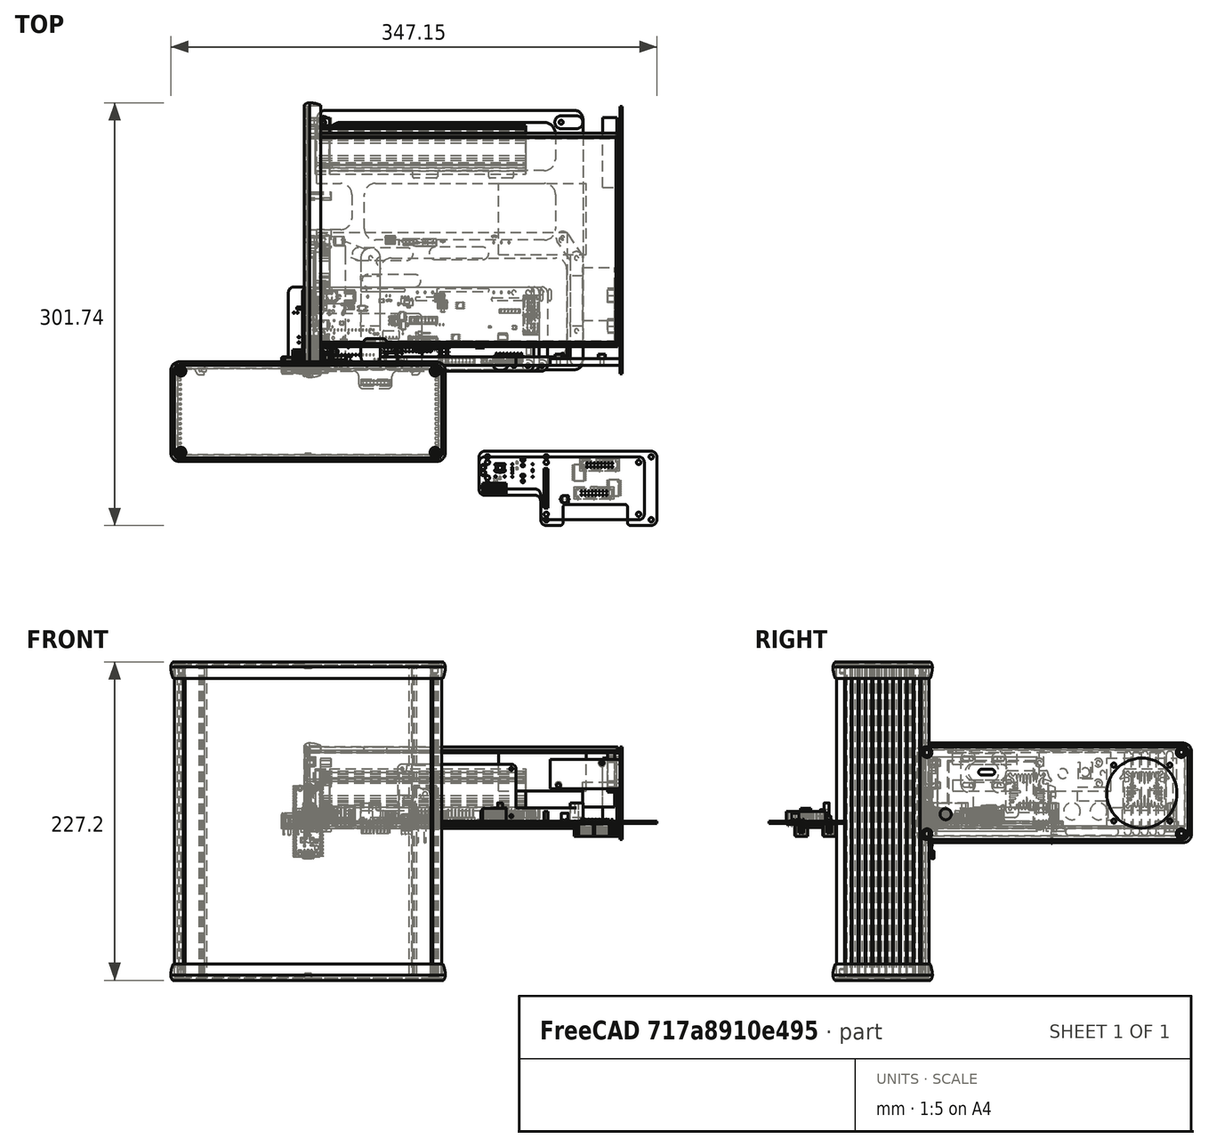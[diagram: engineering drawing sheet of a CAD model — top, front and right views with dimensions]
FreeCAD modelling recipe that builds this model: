
FCSTD DOCUMENT  (FreeCAD 1.0R39285 (Git))
Label: EL-Load-CaseV4
License: All rights reserved
LicenseURL: http://en.wikipedia.org/wiki/All_rights_reserved
objects: App::Link×772, Part::Feature×537, App::Part×80, Sketcher::SketchObject×39, PartDesign::Pad×19, PartDesign::Pocket×15, PartDesign::CoordinateSystem×8, PartDesign::Body×7, PartDesign::SubShapeBinder×6, Part::Box×5, PartDesign::Chamfer×2, PartDesign::Plane×2, PartDesign::FeatureBase×1, Part::Compound×1, Mesh::Feature×1
note: 754 computed .brp shape members not serialized (recipe doc carries the construction recipe); baked Part::Feature solids carry a one-line shape summary decoded from their .brp

FEATURE [Part::Feature] Part__Feature017  label="U extrusion 220mm"
  Placement = pos=(-8e-15,-66,0) rot=(0,0,1;3.14159rad)
  shape: bbox 191 x 66 x 220 mm, 418 faces (baked)
FEATURE [Part::Feature] Part__Feature018  label="T Extrusion Cap 220mm"
  Placement = pos=(8e-15,9.9e-14,0) rot=(0,0,1;0rad)
  shape: bbox 152.4 x 4.29 x 220 mm, 26 faces (baked)
FEATURE [Part::Feature] Part__Feature019  label="1455U Open Bezel"
  Placement = pos=(6.2e-15,-33.01,110) rot=(0,0,1;0rad)
  shape: bbox 196.1 x 71.1 x 11.6 mm, 100 faces (baked)
FEATURE [Part::Feature] Part__Feature020  label="1455U Open Bezel001"
  Placement = pos=(-3.66e-13,-33.01,-110) rot=(1,0,0;3.14159rad)
  shape: bbox 196.1 x 71.1 x 11.6 mm, 100 faces (baked)
FEATURE [Part::Feature] Part__Feature021  label="U End Panel"
  Placement = pos=(-2.49e-13,-33,111.8) rot=(0,0,1;0rad)
  shape: bbox 191 x 66 x 1.626 mm, 14 faces (baked)
FEATURE [Part::Feature] Part__Feature022  label="U End Panel001"
  Placement = pos=(-1.092e-12,-33,-111.8) rot=(1,0,0;3.14159rad)
  shape: bbox 191 x 66 x 1.626 mm, 14 faces (baked)
FEATURE [Part::Feature] Part__Feature023  label="1455 screw"
  Placement = pos=(90.75,-62.01,113.426) rot=(1,0,0;3.14159rad)
  shape: bbox 5.5 x 5.5 x 8 mm, 18 faces (baked)
FEATURE [Part::Feature] Part__Feature024  label="1455 screw001"
  Placement = pos=(90.75,-3.99,113.426) rot=(1,0,0;3.14159rad)
  shape: bbox 5.5 x 5.5 x 8 mm, 18 faces (baked)
FEATURE [Part::Feature] Part__Feature025  label="1455 screw002"
  Placement = pos=(-90.75,-62.01,113.426) rot=(1,0,0;3.14159rad)
  shape: bbox 5.5 x 5.5 x 8 mm, 18 faces (baked)
FEATURE [Part::Feature] Part__Feature026  label="1455 screw003"
  Placement = pos=(-90.75,-3.99,113.426) rot=(1,0,0;3.14159rad)
  shape: bbox 5.5 x 5.5 x 8 mm, 18 faces (baked)
FEATURE [Part::Feature] Part__Feature027  label="1455 screw004"
  Placement = pos=(-90.75,-3.99,-113.426) rot=(0,0,-1;0.01524rad)
  shape: bbox 5.5 x 5.5 x 8 mm, 18 faces (baked)
FEATURE [Part::Feature] Part__Feature028  label="1455 screw005"
  Placement = pos=(-90.75,-62.01,-113.426) rot=(0,0,1;0rad)
  shape: bbox 5.5 x 5.5 x 8 mm, 18 faces (baked)
FEATURE [Part::Feature] Part__Feature029  label="1455 screw006"
  Placement = pos=(90.75,-62.01,-113.426) rot=(0,0,-1;0.007552rad)
  shape: bbox 5.5 x 5.5 x 8 mm, 18 faces (baked)
FEATURE [Part::Feature] Part__Feature030  label="1455 screw007"
  Placement = pos=(90.75,-3.99,-113.426) rot=(0,0,1;0rad)
  shape: bbox 5.5 x 5.5 x 8 mm, 18 faces (baked)
FEATURE [App::Part] _455U2201  label="1455U2201"
  Group = -> [Part__Feature017,Part__Feature018,Part__Feature019,Part__Feature020,Part__Feature021,Part__Feature022,Part__Feature023,Part__Feature024,Part__Feature025,Part__Feature026,Part__Feature027,Part__Feature028,Part__Feature029,Part__Feature030]
  Origin = -> Origin020
  Placement = pos=(111,89.5,53.1) rot=(0.57735,-0.57735,-0.57735;2.0944rad)
FEATURE [Part::Box] Box  label="TFT"
  AttacherType = Attacher::AttachEngine3D
  Height = 53
  Length = 4.5
  Placement = pos=(-0.5,6,-7) rot=(0,0,1;0rad)
  Width = 71
FEATURE [Part::Box] Box001  label="Fan1"
  AttacherType = Attacher::AttachEngine3D
  Height = 50
  Length = 10
  Placement = pos=(210.5,127,-5) rot=(0,0,1;0rad)
  Width = 50
FEATURE [App::Link] C303_C_0805_2012Metric_1d86ef2bb22f_ln_097  label="C26_C_0805_2012Metric_d5dbb9e88232"
  LinkPlacement = pos=(114.675,21.075,0) rot=(0,0,-1;1.5708rad)
  LinkedObject = -> Shape068
  Placement = pos=(114.675,21.075,0) rot=(0,0,-1;1.5708rad)
FEATURE [App::Link] C303_C_0805_2012Metric_1d86ef2bb22f_ln_098  label="C23_C_0805_2012Metric_000a25718fd004"
  LinkPlacement = pos=(127.75,16.625,0) rot=(0,0,1;1.5708rad)
  LinkedObject = -> Shape068
  Placement = pos=(127.75,16.625,0) rot=(0,0,1;1.5708rad)
FEATURE [App::Link] C303_C_0805_2012Metric_1d86ef2bb22f_ln_099  label="C311_C_0805_2012Metric_e7a3c8a1d567"
  LinkPlacement = pos=(69.6,18.85,0) rot=(0,0,1;1.5708rad)
  LinkedObject = -> Shape068
  Placement = pos=(69.6,18.85,0) rot=(0,0,1;1.5708rad)
FEATURE [App::Link] C303_C_0805_2012Metric_1d86ef2bb22f_ln_100  label="C211_C_0805_2012Metric_f6e2775f9a029"
  LinkPlacement = pos=(103.35,92.55,0) rot=(0,0,1;1.5708rad)
  LinkedObject = -> Shape068
  Placement = pos=(103.35,92.55,0) rot=(0,0,1;1.5708rad)
FEATURE [App::Link] C303_C_0805_2012Metric_1d86ef2bb22f_ln_101  label="C13_C_0805_2012Metric_584e764d642c001"
  LinkPlacement = pos=(42.45,2.35,0) rot=(0,0,1;1.5708rad)
  LinkedObject = -> Shape068
  Placement = pos=(42.45,2.35,0) rot=(0,0,1;1.5708rad)
FEATURE [App::Link] C303_C_0805_2012Metric_1d86ef2bb22f_ln_102  label="C49_C_0805_2012Metric_974e61c4247c"
  LinkPlacement = pos=(99.8,39.3625,0) rot=(0,0,1;1.5708rad)
  LinkedObject = -> Shape068
  Placement = pos=(99.8,39.3625,0) rot=(0,0,1;1.5708rad)
FEATURE [App::Link] C303_C_0805_2012Metric_1d86ef2bb22f_ln_103  label="C309_C_0805_2012Metric_4bea97f5e1ff001"
  LinkPlacement = pos=(85.7125,21.575,0) rot=(0,0,-1;1.5708rad)
  LinkedObject = -> Shape068
  Placement = pos=(85.7125,21.575,0) rot=(0,0,-1;1.5708rad)
FEATURE [App::Link] C303_C_0805_2012Metric_1d86ef2bb22f_ln_007  label="C38_C_0805_2012Metric_d30376c11af007"
  LinkPlacement = pos=(135.55,33.075,0) rot=(0,0,1;0rad)
  LinkedObject = -> Shape068
  Placement = pos=(135.55,33.075,0) rot=(0,0,1;0rad)
FEATURE [App::Link] C303_C_0805_2012Metric_1d86ef2bb22f_ln_104  label="C223_C_0805_2012Metric_fc6fab0a5f9d001"
  LinkPlacement = pos=(175,91.5,0) rot=(0,0,1;1.5708rad)
  LinkedObject = -> Shape068
  Placement = pos=(175,91.5,0) rot=(0,0,1;1.5708rad)
FEATURE [App::Link] C303_C_0805_2012Metric_1d86ef2bb22f_ln_105  label="C504_C_0805_2012Metric_f896a043f44d001"
  LinkPlacement = pos=(101.25,30.175,0) rot=(0,0,1;1.5708rad)
  LinkedObject = -> Shape068
  Placement = pos=(101.25,30.175,0) rot=(0,0,1;1.5708rad)
FEATURE [App::Link] C303_C_0805_2012Metric_1d86ef2bb22f_ln_106  label="C226_C_0805_2012Metric_2eb8bf28e24e001"
  LinkPlacement = pos=(117.6,45.9,0) rot=(0,0,1;0rad)
  LinkedObject = -> Shape068
  Placement = pos=(117.6,45.9,0) rot=(0,0,1;0rad)
FEATURE [App::Link] C303_C_0805_2012Metric_1d86ef2bb22f_ln_107  label="C214_C_0805_2012Metric_e2b81b34a7d003"
  LinkPlacement = pos=(51.9,45.5,0) rot=(0,0,1;3.14159rad)
  LinkedObject = -> Shape068
  Placement = pos=(51.9,45.5,0) rot=(0,0,1;3.14159rad)
FEATURE [App::Link] C303_C_0805_2012Metric_1d86ef2bb22f_ln_108  label="C221_C_0805_2012Metric_b44e2667bcf008"
  LinkPlacement = pos=(165.5,5.5,0) rot=(0,0,1;1.5708rad)
  LinkedObject = -> Shape068
  Placement = pos=(165.5,5.5,0) rot=(0,0,1;1.5708rad)
FEATURE [App::Link] C303_C_0805_2012Metric_1d86ef2bb22f_ln_109  label="C209_C_0805_2012Metric_f79f18431d004"
  LinkPlacement = pos=(114.35,91.65,0) rot=(0,0,1;1.5708rad)
  LinkedObject = -> Shape068
  Placement = pos=(114.35,91.65,0) rot=(0,0,1;1.5708rad)
FEATURE [App::Link] C303_C_0805_2012Metric_1d86ef2bb22f_ln_110  label="C205_C_0805_2012Metric_92a2149bb90f001"
  LinkPlacement = pos=(60.2,50.5,0) rot=(0,0,1;1.5708rad)
  LinkedObject = -> Shape068
  Placement = pos=(60.2,50.5,0) rot=(0,0,1;1.5708rad)
FEATURE [App::Link] C303_C_0805_2012Metric_1d86ef2bb22f_ln_111  label="C29_C_0805_2012Metric_fa1848d19679"
  LinkPlacement = pos=(138.375,38.725,0) rot=(0,0,1;0rad)
  LinkedObject = -> Shape068
  Placement = pos=(138.375,38.725,0) rot=(0,0,1;0rad)
FEATURE [App::Link] C303_C_0805_2012Metric_1d86ef2bb22f_ln_112  label="C505_C_0805_2012Metric_bcf27ea4bc011"
  LinkPlacement = pos=(113.225,27.5,0) rot=(0,0,-1;1.5708rad)
  LinkedObject = -> Shape068
  Placement = pos=(113.225,27.5,0) rot=(0,0,-1;1.5708rad)
FEATURE [App::Link] C303_C_0805_2012Metric_1d86ef2bb22f_ln_113  label="C19_C_0805_2012Metric_5594ae341428"
  LinkPlacement = pos=(115.725,25.05,0) rot=(0,0,1;1.5708rad)
  LinkedObject = -> Shape068
  Placement = pos=(115.725,25.05,0) rot=(0,0,1;1.5708rad)
FEATURE [App::Link] C303_C_0805_2012Metric_1d86ef2bb22f_ln_114  label="C217_C_0805_2012Metric_6c92b5ed4841"
  LinkPlacement = pos=(183.3,31.7,0) rot=(0,0,1;1.5708rad)
  LinkedObject = -> Shape068
  Placement = pos=(183.3,31.7,0) rot=(0,0,1;1.5708rad)
FEATURE [App::Link] C303_C_0805_2012Metric_1d86ef2bb22f_ln_115  label="C316_C_0805_2012Metric_cd1ffc8391ec001"
  LinkPlacement = pos=(72.687,27.995,0) rot=(0,0,1;3.14159rad)
  LinkedObject = -> Shape068
  Placement = pos=(72.687,27.995,0) rot=(0,0,1;3.14159rad)
FEATURE [App::Link] C303_C_0805_2012Metric_1d86ef2bb22f_ln_116  label="C225_C_0805_2012Metric_ffd9329e2dcc001"
  LinkPlacement = pos=(161.69,92.5,0) rot=(0,0,1;3.14159rad)
  LinkedObject = -> Shape068
  Placement = pos=(161.69,92.5,0) rot=(0,0,1;3.14159rad)
FEATURE [App::Link] C303_C_0805_2012Metric_1d86ef2bb22f_ln_117  label="C35_C_0805_2012Metric_ffb163dd22d004"
  LinkPlacement = pos=(145.625,33.725,0) rot=(0,0,1;3.14159rad)
  LinkedObject = -> Shape068
  Placement = pos=(145.625,33.725,0) rot=(0,0,1;3.14159rad)
FEATURE [App::Link] C303_C_0805_2012Metric_1d86ef2bb22f_ln_118  label="C52_C_0805_2012Metric_ac194752d0a1"
  LinkPlacement = pos=(80.2,36.8,0) rot=(0,0,1;3.14159rad)
  LinkedObject = -> Shape068
  Placement = pos=(80.2,36.8,0) rot=(0,0,1;3.14159rad)
FEATURE [App::Link] C303_C_0805_2012Metric_1d86ef2bb22f_ln_119  label="C404_C_0805_2012Metric_dd9989736423"
  LinkPlacement = pos=(105.09,9.575,0) rot=(0,0,1;3.14159rad)
  LinkedObject = -> Shape068
  Placement = pos=(105.09,9.575,0) rot=(0,0,1;3.14159rad)
FEATURE [App::Link] C303_C_0805_2012Metric_1d86ef2bb22f_ln_120  label="C27_C_0805_2012Metric_c813a18685a010"
  LinkPlacement = pos=(114.85,12.65,0) rot=(0,0,-1;1.5708rad)
  LinkedObject = -> Shape068
  Placement = pos=(114.85,12.65,0) rot=(0,0,-1;1.5708rad)
FEATURE [App::Link] C303_C_0805_2012Metric_1d86ef2bb22f_ln_121  label="C222_C_0805_2012Metric_211188bab275"
  LinkPlacement = pos=(165.438,13.5,0) rot=(0,0,1;1.5708rad)
  LinkedObject = -> Shape068
  Placement = pos=(165.438,13.5,0) rot=(0,0,1;1.5708rad)
FEATURE [App::Link] C303_C_0805_2012Metric_1d86ef2bb22f_ln_122  label="C1_C_0805_2012Metric_e1adf31e506d001"
  LinkPlacement = pos=(107.075,36.85,0) rot=(0,0,1;3.14159rad)
  LinkedObject = -> Shape068
  Placement = pos=(107.075,36.85,0) rot=(0,0,1;3.14159rad)
FEATURE [App::Link] C303_C_0805_2012Metric_1d86ef2bb22f_ln_123  label="C207_C_0805_2012Metric_e7225891546f001"
  LinkPlacement = pos=(171.545,23.4584,0) rot=(0,0,1;1.5708rad)
  LinkedObject = -> Shape068
  Placement = pos=(171.545,23.4584,0) rot=(0,0,1;1.5708rad)
FEATURE [App::Link] C303_C_0805_2012Metric_1d86ef2bb22f_ln_124  label="C315_C_0805_2012Metric_75f11421f159"
  LinkPlacement = pos=(120.231,38.4938,0) rot=(0,0,-1;1.5708rad)
  LinkedObject = -> Shape068
  Placement = pos=(120.231,38.4938,0) rot=(0,0,-1;1.5708rad)
FEATURE [App::Link] C303_C_0805_2012Metric_1d86ef2bb22f_ln_125  label="C2_C_0805_2012Metric_05101afe5804"
  LinkPlacement = pos=(118.85,34.6,0) rot=(0,0,1;3.14159rad)
  LinkedObject = -> Shape068
  Placement = pos=(118.85,34.6,0) rot=(0,0,1;3.14159rad)
FEATURE [App::Link] C303_C_0805_2012Metric_1d86ef2bb22f_ln_126  label="C24_C_0805_2012Metric_9756039021d010"
  LinkPlacement = pos=(127.8,23.325,0) rot=(0,0,1;1.5708rad)
  LinkedObject = -> Shape068
  Placement = pos=(127.8,23.325,0) rot=(0,0,1;1.5708rad)
FEATURE [App::Link] C303_C_0805_2012Metric_1d86ef2bb22f_ln_127  label="C305_C_0805_2012Metric_8cc8a682d548"
  LinkPlacement = pos=(52,26.85,0) rot=(0,0,1;1.5708rad)
  LinkedObject = -> Shape068
  Placement = pos=(52,26.85,0) rot=(0,0,1;1.5708rad)
FEATURE [App::Link] C303_C_0805_2012Metric_1d86ef2bb22f_ln_128  label="C215_C_0805_2012Metric_46fa3c3d31ac001"
  LinkPlacement = pos=(163.5,88,0) rot=(0,0,1;1.5708rad)
  LinkedObject = -> Shape068
  Placement = pos=(163.5,88,0) rot=(0,0,1;1.5708rad)
FEATURE [App::Link] C303_C_0805_2012Metric_1d86ef2bb22f_ln_129  label="C407_C_0805_2012Metric_fedbb3076933"
  LinkPlacement = pos=(53.45,36.2,0) rot=(0,0,1;3.14159rad)
  LinkedObject = -> Shape068
  Placement = pos=(53.45,36.2,0) rot=(0,0,1;3.14159rad)
FEATURE [App::Link] C303_C_0805_2012Metric_1d86ef2bb22f_ln_130  label="C51_C_0805_2012Metric_83d383f6edd7"
  LinkPlacement = pos=(65.4,39.6,0) rot=(0,0,1;0rad)
  LinkedObject = -> Shape068
  Placement = pos=(65.4,39.6,0) rot=(0,0,1;0rad)
FEATURE [App::Link] C303_C_0805_2012Metric_1d86ef2bb22f_ln_131  label="C54_C_0805_2012Metric_413553e36d7c"
  LinkPlacement = pos=(84.4,44,0) rot=(0,0,1;0rad)
  LinkedObject = -> Shape068
  Placement = pos=(84.4,44,0) rot=(0,0,1;0rad)
FEATURE [App::Link] C303_C_0805_2012Metric_1d86ef2bb22f_ln_132  label="C313_C_0805_2012Metric_612cf4179c1d001"
  LinkPlacement = pos=(56.55,17.875,0) rot=(0,0,1;3.14159rad)
  LinkedObject = -> Shape068
  Placement = pos=(56.55,17.875,0) rot=(0,0,1;3.14159rad)
FEATURE [App::Link] C303_C_0805_2012Metric_1d86ef2bb22f_ln_037  label="C28_C_0805_2012Metric_180589c75c030"
  LinkPlacement = pos=(116.75,21.075,0) rot=(0,0,-1;1.5708rad)
  LinkedObject = -> Shape068
  Placement = pos=(116.75,21.075,0) rot=(0,0,-1;1.5708rad)
FEATURE [App::Link] C303_C_0805_2012Metric_1d86ef2bb22f_ln_133  label="C314_C_0805_2012Metric_20f103a6412f001"
  LinkPlacement = pos=(56.775,26.55,0) rot=(0,0,1;0rad)
  LinkedObject = -> Shape068
  Placement = pos=(56.775,26.55,0) rot=(0,0,1;0rad)
FEATURE [App::Link] C303_C_0805_2012Metric_1d86ef2bb22f_ln_134  label="C218_C_0805_2012Metric_5d7354e4fb6b001"
  LinkPlacement = pos=(183.3,23.7,0) rot=(0,0,1;1.5708rad)
  LinkedObject = -> Shape068
  Placement = pos=(183.3,23.7,0) rot=(0,0,1;1.5708rad)
FEATURE [App::Link] C303_C_0805_2012Metric_1d86ef2bb22f_ln_135  label="C11_C_0805_2012Metric_48f704f1522c001"
  LinkPlacement = pos=(110.45,20.925,0) rot=(0,0,1;1.5708rad)
  LinkedObject = -> Shape068
  Placement = pos=(110.45,20.925,0) rot=(0,0,1;1.5708rad)
FEATURE [App::Link] C303_C_0805_2012Metric_1d86ef2bb22f_ln_136  label="C401_C_0805_2012Metric_e86e7a8ffe026"
  LinkPlacement = pos=(57.5,36.2,0) rot=(0,0,1;0rad)
  LinkedObject = -> Shape068
  Placement = pos=(57.5,36.2,0) rot=(0,0,1;0rad)
FEATURE [App::Link] C303_C_0805_2012Metric_1d86ef2bb22f_ln_137  label="C216_C_0805_2012Metric_21734a4147f005"
  LinkPlacement = pos=(170,93.5,0) rot=(0,0,1;3.14159rad)
  LinkedObject = -> Shape068
  Placement = pos=(170,93.5,0) rot=(0,0,1;3.14159rad)
FEATURE [App::Link] C303_C_0805_2012Metric_1d86ef2bb22f_ln_138  label="C22_C_0805_2012Metric_4bb9130e18a003"
  LinkPlacement = pos=(114.9,16.875,0) rot=(0,0,1;1.5708rad)
  LinkedObject = -> Shape068
  Placement = pos=(114.9,16.875,0) rot=(0,0,1;1.5708rad)
FEATURE [App::Link] C303_C_0805_2012Metric_1d86ef2bb22f_ln_139  label="C43_C_0805_2012Metric_6d7e732d062c001"
  LinkPlacement = pos=(141.725,33.725,0) rot=(0,0,1;3.14159rad)
  LinkedObject = -> Shape068
  Placement = pos=(141.725,33.725,0) rot=(0,0,1;3.14159rad)
FEATURE [App::Link] C303_C_0805_2012Metric_1d86ef2bb22f_ln_140  label="C208_C_0805_2012Metric_e46bcdf7084c001"
  LinkPlacement = pos=(171.545,31.5356,0) rot=(0,0,1;1.5708rad)
  LinkedObject = -> Shape068
  Placement = pos=(171.545,31.5356,0) rot=(0,0,1;1.5708rad)
FEATURE [App::Link] C303_C_0805_2012Metric_1d86ef2bb22f_ln_141  label="C44_C_0805_2012Metric_ee162983a6f006"
  LinkPlacement = pos=(144.025,17.225,0) rot=(0,0,1;1.5708rad)
  LinkedObject = -> Shape068
  Placement = pos=(144.025,17.225,0) rot=(0,0,1;1.5708rad)
FEATURE [App::Link] C303_C_0805_2012Metric_1d86ef2bb22f_ln_142  label="C47_C_0805_2012Metric_5ea36896183c"
  LinkPlacement = pos=(94.3,35.6,0) rot=(0,0,1;1.5708rad)
  LinkedObject = -> Shape068
  Placement = pos=(94.3,35.6,0) rot=(0,0,1;1.5708rad)
FEATURE [App::Link] C303_C_0805_2012Metric_1d86ef2bb22f_ln_143  label="C502_C_0805_2012Metric_bafe37840d085"
  LinkPlacement = pos=(101.25,26.6,0) rot=(0,0,1;1.5708rad)
  LinkedObject = -> Shape068
  Placement = pos=(101.25,26.6,0) rot=(0,0,1;1.5708rad)
FEATURE [App::Link] C303_C_0805_2012Metric_1d86ef2bb22f_ln_049  label="C213_C_0805_2012Metric_9d17bd507aac001"
  LinkPlacement = pos=(116.6,87.8,0) rot=(0,0,-1;1.5708rad)
  LinkedObject = -> Shape068
  Placement = pos=(116.6,87.8,0) rot=(0,0,-1;1.5708rad)
FEATURE [App::Link] C303_C_0805_2012Metric_1d86ef2bb22f_ln_144  label="C220_C_0805_2012Metric_c961a865a417"
  LinkPlacement = pos=(106.929,45.08,0) rot=(0,0,1;0rad)
  LinkedObject = -> Shape068
  Placement = pos=(106.929,45.08,0) rot=(0,0,1;0rad)
FEATURE [App::Link] C303_C_0805_2012Metric_1d86ef2bb22f_ln_145  label="C45_C_0805_2012Metric_5ed4bf02781a001"
  LinkPlacement = pos=(141.95,13.775,0) rot=(0,0,-1;1.5708rad)
  LinkedObject = -> Shape068
  Placement = pos=(141.95,13.775,0) rot=(0,0,-1;1.5708rad)
FEATURE [App::Link] C303_C_0805_2012Metric_1d86ef2bb22f_ln_146  label="C12_C_0805_2012Metric_390cc82b5c077"
  LinkPlacement = pos=(110.45,17.33,0) rot=(0,0,-1;1.5708rad)
  LinkedObject = -> Shape068
  Placement = pos=(110.45,17.33,0) rot=(0,0,-1;1.5708rad)
FEATURE [App::Link] C303_C_0805_2012Metric_1d86ef2bb22f_ln_147  label="C227_C_0805_2012Metric_cabb4cdcbf013"
  LinkPlacement = pos=(175,87.5,0) rot=(0,0,-1;1.5708rad)
  LinkedObject = -> Shape068
  Placement = pos=(175,87.5,0) rot=(0,0,-1;1.5708rad)
FEATURE [App::Link] C303_C_0805_2012Metric_1d86ef2bb22f_ln_148  label="C206_C_0805_2012Metric_59b2e2985f093"
  LinkPlacement = pos=(47.5,48.7,0) rot=(0,0,1;3.14159rad)
  LinkedObject = -> Shape068
  Placement = pos=(47.5,48.7,0) rot=(0,0,1;3.14159rad)
FEATURE [App::Link] C303_C_0805_2012Metric_1d86ef2bb22f_ln_149  label="C37_C_0805_2012Metric_2f8f93623fdd001"
  LinkPlacement = pos=(150.65,26.0125,0) rot=(0,0,1;1.5708rad)
  LinkedObject = -> Shape068
  Placement = pos=(150.65,26.0125,0) rot=(0,0,1;1.5708rad)
FEATURE [App::Link] C303_C_0805_2012Metric_1d86ef2bb22f_ln_150  label="C219_C_0805_2012Metric_1120eae39659"
  LinkPlacement = pos=(113.429,48.58,0) rot=(0,0,1;1.5708rad)
  LinkedObject = -> Shape068
  Placement = pos=(113.429,48.58,0) rot=(0,0,1;1.5708rad)
FEATURE [App::Link] C303_C_0805_2012Metric_1d86ef2bb22f_ln_151  label="C203_C_0805_2012Metric_dba0b3a855a008"
  LinkPlacement = pos=(177.565,5.399,0) rot=(0,0,1;1.5708rad)
  LinkedObject = -> Shape068
  Placement = pos=(177.565,5.399,0) rot=(0,0,1;1.5708rad)
FEATURE [App::Link] C303_C_0805_2012Metric_1d86ef2bb22f_ln_152  label="C39_C_0805_2012Metric_7a4cbeef3a034"
  LinkPlacement = pos=(130.175,31.575,0) rot=(0,0,-1;1.5708rad)
  LinkedObject = -> Shape068
  Placement = pos=(130.175,31.575,0) rot=(0,0,-1;1.5708rad)
FEATURE [App::Link] C303_C_0805_2012Metric_1d86ef2bb22f_ln_153  label="C21_C_0805_2012Metric_01105218e7e007"
  LinkPlacement = pos=(117.825,25.05,0) rot=(0,0,1;1.5708rad)
  LinkedObject = -> Shape068
  Placement = pos=(117.825,25.05,0) rot=(0,0,1;1.5708rad)
FEATURE [App::Link] C303_C_0805_2012Metric_1d86ef2bb22f_ln_154  label="C501_C_0805_2012Metric_228dc7cb5e5d001"
  LinkPlacement = pos=(111.1,31.9,0) rot=(0,0,1;1.5708rad)
  LinkedObject = -> Shape068
  Placement = pos=(111.1,31.9,0) rot=(0,0,1;1.5708rad)
FEATURE [App::Link] C303_C_0805_2012Metric_1d86ef2bb22f_ln_155  label="C503_C_0805_2012Metric_16dcb8b1dc045"
  LinkPlacement = pos=(107.075,16.05,0) rot=(0,0,1;3.14159rad)
  LinkedObject = -> Shape068
  Placement = pos=(107.075,16.05,0) rot=(0,0,1;3.14159rad)
FEATURE [App::Link] C303_C_0805_2012Metric_1d86ef2bb22f_ln_156  label="C307_C_0805_2012Metric_ef573f1286a005"
  LinkPlacement = pos=(153.839,29.544,0) rot=(0,0,-1;1.5708rad)
  LinkedObject = -> Shape068
  Placement = pos=(153.839,29.544,0) rot=(0,0,-1;1.5708rad)
FEATURE [App::Link] C303_C_0805_2012Metric_1d86ef2bb22f_ln_157  label="C312_C_0805_2012Metric_204514eca08f001"
  LinkPlacement = pos=(67.2,22.35,0) rot=(0,0,1;1.5708rad)
  LinkedObject = -> Shape068
  Placement = pos=(67.2,22.35,0) rot=(0,0,1;1.5708rad)
FEATURE [App::Link] C303_C_0805_2012Metric_1d86ef2bb22f_ln_158  label="C10_C_0805_2012Metric_f6a3d44cf72c001"
  LinkPlacement = pos=(100.7,19.225,0) rot=(0,0,-1;1.5708rad)
  LinkedObject = -> Shape068
  Placement = pos=(100.7,19.225,0) rot=(0,0,-1;1.5708rad)
FEATURE [App::Link] C303_C_0805_2012Metric_1d86ef2bb22f_ln_159  label="C308_C_0805_2012Metric_86bc2e49f05b001"
  LinkPlacement = pos=(156.024,22.178,0) rot=(0,0,1;3.14159rad)
  LinkedObject = -> Shape068
  Placement = pos=(156.024,22.178,0) rot=(0,0,1;3.14159rad)
FEATURE [App::Link] C303_C_0805_2012Metric_1d86ef2bb22f_ln_160  label="C48_C_0805_2012Metric_3d6e9560ce49"
  LinkPlacement = pos=(92.8,39.4,0) rot=(0,0,-1;1.5708rad)
  LinkedObject = -> Shape068
  Placement = pos=(92.8,39.4,0) rot=(0,0,-1;1.5708rad)
FEATURE [App::Link] C303_C_0805_2012Metric_1d86ef2bb22f_ln_161  label="C40_C_0805_2012Metric_aa59399f450c001"
  LinkPlacement = pos=(141.637,25.3125,0) rot=(0,0,1;3.14159rad)
  LinkedObject = -> Shape068
  Placement = pos=(141.637,25.3125,0) rot=(0,0,1;3.14159rad)
FEATURE [App::Link] C303_C_0805_2012Metric_1d86ef2bb22f_ln_068  label="C212_C_0805_2012Metric_ff8aa67397a010"
  LinkPlacement = pos=(55.9,45.7,0) rot=(0,0,1;0rad)
  LinkedObject = -> Shape068
  Placement = pos=(55.9,45.7,0) rot=(0,0,1;0rad)
FEATURE [App::Link] C303_C_0805_2012Metric_1d86ef2bb22f_ln_162  label="C210_C_0805_2012Metric_6be0f132b8e008"
  LinkPlacement = pos=(47.5,50.8,0) rot=(0,0,1;0rad)
  LinkedObject = -> Shape068
  Placement = pos=(47.5,50.8,0) rot=(0,0,1;0rad)
FEATURE [App::Link] C303_C_0805_2012Metric_1d86ef2bb22f_ln_163  label="C20_C_0805_2012Metric_5e1706738731"
  LinkPlacement = pos=(117,16.9,0) rot=(0,0,1;1.5708rad)
  LinkedObject = -> Shape068
  Placement = pos=(117,16.9,0) rot=(0,0,1;1.5708rad)
FEATURE [App::Link] C303_C_0805_2012Metric_1d86ef2bb22f_ln_164  label="C310_C_0805_2012Metric_490b81cdc352"
  LinkPlacement = pos=(52.825,20.25,0) rot=(0,0,1;0rad)
  LinkedObject = -> Shape068
  Placement = pos=(52.825,20.25,0) rot=(0,0,1;0rad)
FEATURE [App::Link] C303_C_0805_2012Metric_1d86ef2bb22f_ln_165  label="C42_C_0805_2012Metric_4eb63d81472c001"
  LinkPlacement = pos=(143.675,22.15,0) rot=(0,0,-1;1.5708rad)
  LinkedObject = -> Shape068
  Placement = pos=(143.675,22.15,0) rot=(0,0,-1;1.5708rad)
FEATURE [App::Link] C303_C_0805_2012Metric_1d86ef2bb22f_ln_166  label="C306_C_0805_2012Metric_f55fe554345e001"
  LinkPlacement = pos=(51.95,32,0) rot=(0,0,1;1.5708rad)
  LinkedObject = -> Shape068
  Placement = pos=(51.95,32,0) rot=(0,0,1;1.5708rad)
FEATURE [App::Link] C303_C_0805_2012Metric_1d86ef2bb22f_ln_167  label="C34_C_0805_2012Metric_faa94f78bcbd001"
  LinkPlacement = pos=(144.275,40.025,0) rot=(0,0,1;3.14159rad)
  LinkedObject = -> Shape068
  Placement = pos=(144.275,40.025,0) rot=(0,0,1;3.14159rad)
FEATURE [App::Link] C303_C_0805_2012Metric_1d86ef2bb22f_ln_168  label="C50_C_0805_2012Metric_12a32574f717"
  LinkPlacement = pos=(72.6,38.2,0) rot=(0,0,1;1.5708rad)
  LinkedObject = -> Shape068
  Placement = pos=(72.6,38.2,0) rot=(0,0,1;1.5708rad)
FEATURE [App::Link] C303_C_0805_2012Metric_1d86ef2bb22f_ln_169  label="C18_C_0805_2012Metric_c6e5c3101df009"
  LinkPlacement = pos=(117.475,2.725,0) rot=(0,0,1;0rad)
  LinkedObject = -> Shape068
  Placement = pos=(117.475,2.725,0) rot=(0,0,1;0rad)
FEATURE [App::Link] C303_C_0805_2012Metric_1d86ef2bb22f_ln_077  label="C41_C_0805_2012Metric_23af0ccbd41e001"
  LinkPlacement = pos=(137.738,25.3125,0) rot=(0,0,1;0rad)
  LinkedObject = -> Shape068
  Placement = pos=(137.738,25.3125,0) rot=(0,0,1;0rad)
FEATURE [App::Link] C303_C_0805_2012Metric_1d86ef2bb22f_ln_170  label="C228_C_0805_2012Metric_db3eaee78164"
  LinkPlacement = pos=(110.929,45.08,0) rot=(0,0,1;0rad)
  LinkedObject = -> Shape068
  Placement = pos=(110.929,45.08,0) rot=(0,0,1;0rad)
FEATURE [App::Link] C303_C_0805_2012Metric_1d86ef2bb22f_ln_171  label="C202_C_0805_2012Metric_d255fea7448e001"
  LinkPlacement = pos=(110.25,93.45,0) rot=(0,0,1;3.14159rad)
  LinkedObject = -> Shape068
  Placement = pos=(110.25,93.45,0) rot=(0,0,1;3.14159rad)
FEATURE [App::Link] C303_C_0805_2012Metric_1d86ef2bb22f_ln_172  label="C405_C_0805_2012Metric_7b2220de55d006"
  LinkPlacement = pos=(128.325,2.6,0) rot=(0,0,-1;1.5708rad)
  LinkedObject = -> Shape068
  Placement = pos=(128.325,2.6,0) rot=(0,0,-1;1.5708rad)
FEATURE [App::Link] C303_C_0805_2012Metric_1d86ef2bb22f_ln_173  label="C304_C_0805_2012Metric_d3558c6d708f001"
  LinkPlacement = pos=(92.1,27.376,0) rot=(0,0,1;3.14159rad)
  LinkedObject = -> Shape068
  Placement = pos=(92.1,27.376,0) rot=(0,0,1;3.14159rad)
FEATURE [App::Link] C303_C_0805_2012Metric_1d86ef2bb22f_ln_174  label="C406_C_0805_2012Metric_f1b2804f82f009"
  LinkPlacement = pos=(61.625,41.675,0) rot=(0,0,-1;1.5708rad)
  LinkedObject = -> Shape068
  Placement = pos=(61.625,41.675,0) rot=(0,0,-1;1.5708rad)
FEATURE [App::Link] C303_C_0805_2012Metric_1d86ef2bb22f_ln_175  label="C36_C_0805_2012Metric_3d0ec07c9d2c001"
  LinkPlacement = pos=(147.175,24.2375,0) rot=(0,0,1;0rad)
  LinkedObject = -> Shape068
  Placement = pos=(147.175,24.2375,0) rot=(0,0,1;0rad)
FEATURE [App::Link] C303_C_0805_2012Metric_1d86ef2bb22f_ln_176  label="C53_C_0805_2012Metric_0b477a83f040"
  LinkPlacement = pos=(80.2,39.2,0) rot=(0,0,1;3.14159rad)
  LinkedObject = -> Shape068
  Placement = pos=(80.2,39.2,0) rot=(0,0,1;3.14159rad)
FEATURE [App::Link] C303_C_0805_2012Metric_1d86ef2bb22f_ln_177  label="C224_C_0805_2012Metric_f777ef533c5e001"
  LinkPlacement = pos=(103.015,49.8,0) rot=(0,0,-1;1.5708rad)
  LinkedObject = -> Shape068
  Placement = pos=(103.015,49.8,0) rot=(0,0,-1;1.5708rad)
FEATURE [App::Link] C303_C_0805_2012Metric_1d86ef2bb22f_ln_178  label="C302_C_0805_2012Metric_95746b57ac046"
  LinkPlacement = pos=(108.2,34.2,0) rot=(0,0,1;3.14159rad)
  LinkedObject = -> Shape068
  Placement = pos=(108.2,34.2,0) rot=(0,0,1;3.14159rad)
FEATURE [App::Link] C303_C_0805_2012Metric_1d86ef2bb22f_ln_179  label="C301_C_0805_2012Metric_27f5d4edfcf005"
  LinkPlacement = pos=(116.6,42.175,0) rot=(0,0,1;3.14159rad)
  LinkedObject = -> Shape068
  Placement = pos=(116.6,42.175,0) rot=(0,0,1;3.14159rad)
FEATURE [App::Link] C303_C_0805_2012Metric_1d86ef2bb22f_ln_180  label="C204_C_0805_2012Metric_93e9081341c005"
  LinkPlacement = pos=(177.59,13.4508,0) rot=(0,0,1;1.5708rad)
  LinkedObject = -> Shape068
  Placement = pos=(177.59,13.4508,0) rot=(0,0,1;1.5708rad)
FEATURE [App::Link] C303_C_0805_2012Metric_1d86ef2bb22f_ln_181  label="C201_C_0805_2012Metric_3c6c4e562b077"
  LinkPlacement = pos=(103.9,87.55,0) rot=(0,0,1;1.5708rad)
  LinkedObject = -> Shape068
  Placement = pos=(103.9,87.55,0) rot=(0,0,1;1.5708rad)
FEATURE [App::Link] C303_C_0805_2012Metric_1d86ef2bb22f_ln_182  label="C25_C_0805_2012Metric_a8b56f256ab007"
  LinkPlacement = pos=(117.025,12.65,0) rot=(0,0,-1;1.5708rad)
  LinkedObject = -> Shape068
  Placement = pos=(117.025,12.65,0) rot=(0,0,-1;1.5708rad)
FEATURE [App::Link] C303_C_0805_2012Metric_1d86ef2bb22f_ln_183  label="C402_C_0805_2012Metric_2602be6c4c100"
  LinkPlacement = pos=(125.1,7.25,0) rot=(0,0,1;0rad)
  LinkedObject = -> Shape068
  Placement = pos=(125.1,7.25,0) rot=(0,0,1;0rad)
FEATURE [App::Link] C303_C_0805_2012Metric_1d86ef2bb22f_ln_184  label="C32_C_0805_2012Metric_6c00573259a007"
  LinkPlacement = pos=(138.375,35.925,0) rot=(0,0,1;0rad)
  LinkedObject = -> Shape068
  Placement = pos=(138.375,35.925,0) rot=(0,0,1;0rad)
FEATURE [App::Link] D208_D_MiniMELF_Standard_5646c313d2d3_ln_011  label="D301_D_MiniMELF_Standard_dd8a013c1900"
  LinkPlacement = pos=(109.025,42.1,0) rot=(0,0,1;3.14159rad)
  LinkedObject = -> Shape073
  Placement = pos=(109.025,42.1,0) rot=(0,0,1;3.14159rad)
FEATURE [App::Link] D208_D_MiniMELF_Standard_5646c313d2d3_ln_012  label="D202_D_MiniMELF_Standard_af40c77ecb096"
  LinkPlacement = pos=(71.2,51.5,0) rot=(0,0,1;1.5708rad)
  LinkedObject = -> Shape073
  Placement = pos=(71.2,51.5,0) rot=(0,0,1;1.5708rad)
FEATURE [App::Link] D208_D_MiniMELF_Standard_5646c313d2d3_ln_013  label="D206_D_MiniMELF_Standard_12c2ef1d76fd001"
  LinkPlacement = pos=(79.1,92.2,0) rot=(0,0,1;0rad)
  LinkedObject = -> Shape073
  Placement = pos=(79.1,92.2,0) rot=(0,0,1;0rad)
FEATURE [App::Link] D208_D_MiniMELF_Standard_5646c313d2d3_ln_014  label="D302_D_MiniMELF_Standard_4cb12e1780df001"
  LinkPlacement = pos=(96.0875,22.7,0) rot=(0,0,1;1.5708rad)
  LinkedObject = -> Shape073
  Placement = pos=(96.0875,22.7,0) rot=(0,0,1;1.5708rad)
FEATURE [App::Link] D208_D_MiniMELF_Standard_5646c313d2d3_ln_015  label="D205_D_MiniMELF_Standard_e613e3e799f003"
  LinkPlacement = pos=(127,50.1,0) rot=(0,0,1;0rad)
  LinkedObject = -> Shape073
  Placement = pos=(127,50.1,0) rot=(0,0,1;0rad)
FEATURE [App::Link] D208_D_MiniMELF_Standard_5646c313d2d3_ln_016  label="D209_D_MiniMELF_Standard_1ec4f44d5c035"
  LinkPlacement = pos=(127,47.6,0) rot=(0,0,1;0rad)
  LinkedObject = -> Shape073
  Placement = pos=(127,47.6,0) rot=(0,0,1;0rad)
FEATURE [App::Link] D208_D_MiniMELF_Standard_5646c313d2d3_ln_017  label="D201_D_MiniMELF_Standard_1d564c9b7722"
  LinkPlacement = pos=(84.6,92.2,0) rot=(0,0,1;3.14159rad)
  LinkedObject = -> Shape073
  Placement = pos=(84.6,92.2,0) rot=(0,0,1;3.14159rad)
FEATURE [App::Link] D208_D_MiniMELF_Standard_5646c313d2d3_ln_018  label="D204_D_MiniMELF_Standard_15f0fdcadfec001"
  LinkPlacement = pos=(138.9,92.1,0) rot=(0,0,1;3.14159rad)
  LinkedObject = -> Shape073
  Placement = pos=(138.9,92.1,0) rot=(0,0,1;3.14159rad)
FEATURE [App::Link] D208_D_MiniMELF_Standard_5646c313d2d3_ln_019  label="D207_D_MiniMELF_Standard_e976a3a262de001"
  LinkPlacement = pos=(73.9,51.5,0) rot=(0,0,1;1.5708rad)
  LinkedObject = -> Shape073
  Placement = pos=(73.9,51.5,0) rot=(0,0,1;1.5708rad)
FEATURE [App::Link] D208_D_MiniMELF_Standard_5646c313d2d3_ln_020  label="D2_D_MiniMELF_Standard_05f98c6ed1d009"
  LinkPlacement = pos=(41.5,29.3,-1.57252) rot=(0.707107,-0.707107,0;3.14159rad)
  LinkedObject = -> Shape073
  Placement = pos=(41.5,29.3,-1.57252) rot=(0.707107,-0.707107,0;3.14159rad)
FEATURE [App::Link] D208_D_MiniMELF_Standard_5646c313d2d3_ln_021  label="D3_D_MiniMELF_Standard_f91f685f11d004"
  LinkPlacement = pos=(32.35,29.4,-1.57252) rot=(0.707107,-0.707107,0;3.14159rad)
  LinkedObject = -> Shape073
  Placement = pos=(32.35,29.4,-1.57252) rot=(0.707107,-0.707107,0;3.14159rad)
FEATURE [App::Link] J9_JST_B2B_XH_A_e9e719df0531_ln_  label="J1_JST_B2B_XH_A_c76c184b747b"
  LinkPlacement = pos=(150.65,14.625,0) rot=(0,0,1;0rad)
  LinkedObject = -> Shape078
  Placement = pos=(150.65,14.625,0) rot=(0,0,1;0rad)
FEATURE [PartDesign::CoordinateSystem] Local_CS_29d001
  AttacherType = Attacher::AttachEngine3D
  AttachmentSupport = -> [X_Axis036]
  MapMode = 2
FEATURE [Sketcher::SketchObject] PCB_Sketch_29d001
  ArcFitTolerance = 0
  FullyConstrained = false
  MakeInternals = false
  sketch-geometry (64):
    g0: LineSegment StartX=155 StartY=47.5 StartZ=0 EndX=155 EndY=47 EndZ=0
    g1: LineSegment StartX=131.8 StartY=48.3 StartZ=0 EndX=154.2 EndY=48.3 EndZ=0
    g2: LineSegment StartX=154.2 StartY=46.2 StartZ=0 EndX=131.8 EndY=46.2 EndZ=0
    g3: LineSegment StartX=37.6 StartY=53.9 StartZ=0 EndX=37.6 EndY=53.6 EndZ=0
    g4: LineSegment StartX=185 StartY=95 StartZ=0 EndX=185 EndY=0 EndZ=0
    g5: LineSegment StartX=76.6 StartY=47.7 StartZ=0 EndX=76.6 EndY=47.3 EndZ=0
    g6: LineSegment StartX=91.8 StartY=48.5 StartZ=0 EndX=77.4 EndY=48.5 EndZ=0
    g7: LineSegment StartX=69.3 StartY=53.6 StartZ=0 EndX=69.3 EndY=53.9 EndZ=0
    g8: LineSegment StartX=5.5 StartY=9 StartZ=0 EndX=0 EndY=9 EndZ=0
    g9: LineSegment StartX=36 StartY=75 StartZ=0 EndX=70.5 EndY=75 EndZ=0
    g10: LineSegment StartX=173.5 StartY=53.4 StartZ=0 EndX=173.5 EndY=47.2 EndZ=0
    g11: LineSegment StartX=43 StartY=56 StartZ=0 EndX=76 EndY=56 EndZ=0
    g12: LineSegment StartX=129.3 StartY=53.6 StartZ=0 EndX=129.3 EndY=53.9 EndZ=0
    g13: LineSegment StartX=94.3 StartY=52.8 StartZ=0 EndX=128.5 EndY=52.8 EndZ=0
    g14: LineSegment StartX=6.5 StartY=0 StartZ=0 EndX=6.5 EndY=8 EndZ=0
    g15: LineSegment StartX=77.4 StartY=46.5 StartZ=0 EndX=93.5 EndY=46.5 EndZ=0
    g16: LineSegment StartX=159.3 StartY=53.3 StartZ=0 EndX=159.3 EndY=47.3 EndZ=0
    g17: LineSegment StartX=165.5 StartY=53.3 StartZ=0 EndX=165.5 EndY=47.3 EndZ=0
    g18: LineSegment StartX=128.5 StartY=54.7 StartZ=0 EndX=92.6 EndY=54.7 EndZ=0
    g19: LineSegment StartX=171.5 StartY=47.2 StartZ=0 EndX=171.5 EndY=53.4 EndZ=0
    g20: LineSegment StartX=0 StartY=9 StartZ=0 EndX=0 EndY=86 EndZ=0
    g21: LineSegment StartX=185 StartY=0 StartZ=0 EndX=6.5 EndY=0 EndZ=0
    g22: LineSegment StartX=6.5 StartY=95 StartZ=0 EndX=185 EndY=95 EndZ=0
    g23: LineSegment StartX=167.7 StartY=47.3 StartZ=0 EndX=167.7 EndY=53.3 EndZ=0
    g24: LineSegment StartX=38.4 StartY=52.8 StartZ=0 EndX=68.5 EndY=52.8 EndZ=0
    g25: LineSegment StartX=70.5 StartY=84 StartZ=0 EndX=36 EndY=84 EndZ=0
    g26: LineSegment StartX=68.5 StartY=54.7 StartZ=0 EndX=38.4 EndY=54.7 EndZ=0
    g27: LineSegment StartX=161.5 StartY=47.3 StartZ=0 EndX=161.5 EndY=53.3 EndZ=0
    g28: LineSegment StartX=131 StartY=47 StartZ=0 EndX=131 EndY=47.5 EndZ=0
    g29: LineSegment StartX=124.5 StartY=84.5 StartZ=0 EndX=91 EndY=84.5 EndZ=0
    g30: LineSegment StartX=0 StartY=86 StartZ=0 EndX=5.5 EndY=86 EndZ=0
    g31: LineSegment StartX=94.3 StartY=47.3 StartZ=0 EndX=94.3 EndY=52.8 EndZ=0
    g32: LineSegment StartX=91 StartY=75.5 StartZ=0 EndX=124.5 EndY=75.5 EndZ=0
    g33: LineSegment StartX=6.5 StartY=87 StartZ=0 EndX=6.5 EndY=95 EndZ=0
    g34: LineSegment StartX=91.8 StartY=53.9 StartZ=0 EndX=91.8 EndY=48.5 EndZ=0
    g35: LineSegment StartX=76 StartY=65 StartZ=0 EndX=43 EndY=65 EndZ=0
    g36: ArcOfCircle CenterX=131.8 CenterY=47 CenterZ=0 NormalX=0 NormalY=0 NormalZ=-1 AngleXU=-1.57079 Radius=0.800001 StartAngle=0 EndAngle=1.57079
    g37: ArcOfCircle CenterX=160.4 CenterY=53.3 CenterZ=0 NormalX=0 NormalY=0 NormalZ=-1 AngleXU=-1.29e-14 Radius=1.1 StartAngle=0 EndAngle=3.14159
    g38: ArcOfCircle CenterX=68.5 CenterY=53.9 CenterZ=0 NormalX=0 NormalY=0 NormalZ=-1 AngleXU=1.5708 Radius=0.800001 StartAngle=0 EndAngle=1.57079
    g39: ArcOfCircle CenterX=43 CenterY=60.5 CenterZ=0 NormalX=0 NormalY=0 NormalZ=-1 AngleXU=-1.5708 Radius=4.5 StartAngle=0 EndAngle=3.14159
    g40: ArcOfCircle CenterX=38.4 CenterY=53.9 CenterZ=0 NormalX=0 NormalY=0 NormalZ=-1 AngleXU=1.81358e-06 Radius=0.800001 StartAngle=0 EndAngle=1.57079
    g41: ArcOfCircle CenterX=166.6 CenterY=53.3 CenterZ=0 NormalX=0 NormalY=0 NormalZ=-1 AngleXU=-1.29e-14 Radius=1.1 StartAngle=0 EndAngle=3.14159
    g42: ArcOfCircle CenterX=172.5 CenterY=47.2 CenterZ=0 NormalX=0 NormalY=0 NormalZ=-1 AngleXU=-3.14159 Radius=1 StartAngle=0 EndAngle=3.14159
    g43: ArcOfCircle CenterX=124.5 CenterY=80 CenterZ=0 NormalX=0 NormalY=0 NormalZ=-1 AngleXU=1.5708 Radius=4.5 StartAngle=0 EndAngle=3.14159
    g44: ArcOfCircle CenterX=77.4 CenterY=47.7 CenterZ=0 NormalX=0 NormalY=0 NormalZ=-1 AngleXU=1.81359e-06 Radius=0.800001 StartAngle=0 EndAngle=1.57079
    g45: ArcOfCircle CenterX=93.5 CenterY=47.3 CenterZ=0 NormalX=0 NormalY=0 NormalZ=-1 AngleXU=-3.14159 Radius=0.800001 StartAngle=0 EndAngle=1.57079
    g46: ArcOfCircle CenterX=172.5 CenterY=53.4 CenterZ=0 NormalX=0 NormalY=0 NormalZ=-1 AngleXU=0 Radius=1 StartAngle=0 EndAngle=3.14159
    g47: ArcOfCircle CenterX=128.5 CenterY=53.9 CenterZ=0 NormalX=0 NormalY=0 NormalZ=-1 AngleXU=1.5708 Radius=0.800001 StartAngle=0 EndAngle=1.57079
    g48: ArcOfCircle CenterX=5.5 CenterY=87 CenterZ=0 NormalX=0 NormalY=0 NormalZ=-1 AngleXU=3.14159 Radius=0.999999 StartAngle=0 EndAngle=1.5708
    g49: ArcOfCircle CenterX=38.4 CenterY=53.6 CenterZ=0 NormalX=0 NormalY=0 NormalZ=-1 AngleXU=-1.57079 Radius=0.800001 StartAngle=0 EndAngle=1.57079
    g50: ArcOfCircle CenterX=166.6 CenterY=47.3 CenterZ=0 NormalX=0 NormalY=0 NormalZ=-1 AngleXU=3.14159 Radius=1.1 StartAngle=0 EndAngle=3.14159
    g51: ArcOfCircle CenterX=128.5 CenterY=53.6 CenterZ=0 NormalX=0 NormalY=0 NormalZ=-1 AngleXU=-3.14159 Radius=0.800001 StartAngle=0 EndAngle=1.57079
    g52: ArcOfCircle CenterX=70.5 CenterY=79.5 CenterZ=0 NormalX=0 NormalY=0 NormalZ=-1 AngleXU=1.5708 Radius=4.5 StartAngle=0 EndAngle=3.14159
    g53: ArcOfCircle CenterX=131.8 CenterY=47.5 CenterZ=0 NormalX=0 NormalY=0 NormalZ=-1 AngleXU=1.81358e-06 Radius=0.800001 StartAngle=0 EndAngle=1.57079
    g54: ArcOfCircle CenterX=5.5 CenterY=8 CenterZ=0 NormalX=0 NormalY=0 NormalZ=-1 AngleXU=1.5708 Radius=0.999999 StartAngle=0 EndAngle=1.5708
    g55: ArcOfCircle CenterX=91 CenterY=80 CenterZ=0 NormalX=0 NormalY=0 NormalZ=-1 AngleXU=-1.5708 Radius=4.5 StartAngle=0 EndAngle=3.14159
    g56: ArcOfCircle CenterX=154.2 CenterY=47.5 CenterZ=0 NormalX=0 NormalY=0 NormalZ=-1 AngleXU=1.5708 Radius=0.800001 StartAngle=0 EndAngle=1.57079
    g57: ArcOfCircle CenterX=76 CenterY=60.5 CenterZ=0 NormalX=0 NormalY=0 NormalZ=-1 AngleXU=1.5708 Radius=4.5 StartAngle=0 EndAngle=3.14159
    g58: ArcOfCircle CenterX=68.5 CenterY=53.6 CenterZ=0 NormalX=0 NormalY=0 NormalZ=-1 AngleXU=-3.14159 Radius=0.800001 StartAngle=0 EndAngle=1.57079
    g59: ArcOfCircle CenterX=160.4 CenterY=47.3 CenterZ=0 NormalX=0 NormalY=0 NormalZ=-1 AngleXU=3.14159 Radius=1.1 StartAngle=0 EndAngle=3.14159
    g60: ArcOfCircle CenterX=92.6 CenterY=53.9 CenterZ=0 NormalX=0 NormalY=0 NormalZ=-1 AngleXU=1.81359e-06 Radius=0.800001 StartAngle=0 EndAngle=1.57079
    g61: ArcOfCircle CenterX=36 CenterY=79.5 CenterZ=0 NormalX=0 NormalY=0 NormalZ=-1 AngleXU=-1.5708 Radius=4.5 StartAngle=0 EndAngle=3.14159
    g62: ArcOfCircle CenterX=77.4 CenterY=47.3 CenterZ=0 NormalX=0 NormalY=0 NormalZ=-1 AngleXU=-1.57079 Radius=0.800001 StartAngle=0 EndAngle=1.57079
    g63: ArcOfCircle CenterX=154.2 CenterY=47 CenterZ=0 NormalX=0 NormalY=0 NormalZ=-1 AngleXU=-3.14159 Radius=0.800001 StartAngle=0 EndAngle=1.57079
  constraints (64):
    c: Coincident(g8,g20)
    c: Coincident(g20,g30)
    c: Coincident(g8,g54)
    c: Coincident(g30,g48)
    c: Coincident(g14,g21)
    c: Coincident(g14,g54)
    c: Coincident(g33,g48)
    c: Coincident(g22,g33)
    c: Coincident(g9,g61)
    c: Coincident(g25,g61)
    c: Coincident(g3,g49)
    c: Coincident(g3,g40)
    c: Coincident(g24,g49)
    c: Coincident(g26,g40)
    c: Coincident(g11,g39)
    c: Coincident(g35,g39)
    c: Coincident(g24,g58)
    c: Coincident(g26,g38)
    c: Coincident(g7,g58)
    c: Coincident(g7,g38)
    c: Coincident(g9,g52)
    c: Coincident(g25,g52)
    c: Coincident(g11,g57)
    c: Coincident(g35,g57)
    c: Coincident(g5,g62)
    c: Coincident(g5,g44)
    c: Coincident(g15,g62)
    c: Coincident(g6,g44)
    c: Coincident(g32,g55)
    c: Coincident(g29,g55)
    c: Coincident(g6,g34)
    c: Coincident(g34,g60)
    c: Coincident(g18,g60)
    c: Coincident(g15,g45)
    c: Coincident(g31,g45)
    c: Coincident(g13,g31)
    c: Coincident(g32,g43)
    c: Coincident(g29,g43)
    c: Coincident(g13,g51)
    c: Coincident(g18,g47)
    c: Coincident(g12,g51)
    c: Coincident(g12,g47)
    c: Coincident(g28,g36)
    c: Coincident(g28,g53)
    c: Coincident(g2,g36)
    c: Coincident(g1,g53)
    c: Coincident(g2,g63)
    c: Coincident(g1,g56)
    c: Coincident(g0,g63)
    c: Coincident(g0,g56)
    c: Coincident(g16,g59)
    c: Coincident(g16,g37)
    c: Coincident(g27,g59)
    c: Coincident(g27,g37)
    c: Coincident(g17,g50)
    c: Coincident(g17,g41)
    c: Coincident(g23,g50)
    c: Coincident(g23,g41)
    c: Coincident(g19,g42)
    c: Coincident(g19,g46)
    c: Coincident(g10,g42)
    c: Coincident(g10,g46)
    c: Coincident(g4,g21)
    c: Coincident(g4,g22)
FEATURE [Part::Feature] Part__Feature223  label="729b0bae-9266-11ed-9e62-a0cec80452fd_part001"
  shape: bbox 3.9 x 4.905 x 1.75 mm, 84 faces (baked)
FEATURE [Part::Feature] Part__Feature224  label="729b0e92-9266-11ed-9e62-a0cec80452fd_part009"
  shape: bbox 1.198 x 0.41 x 1.07 mm, 14 faces (baked)
FEATURE [Part::Feature] Part__Feature225  label="729b0e92-9266-11ed-9e62-a0cec80452fd_part010"
  shape: bbox 1.198 x 0.41 x 1.07 mm, 14 faces (baked)
FEATURE [Part::Feature] Part__Feature226  label="729b0e92-9266-11ed-9e62-a0cec80452fd_part011"
  shape: bbox 1.198 x 0.41 x 1.07 mm, 14 faces (baked)
FEATURE [Part::Feature] Part__Feature227  label="729b0e92-9266-11ed-9e62-a0cec80452fd_part012"
  shape: bbox 1.198 x 0.41 x 1.07 mm, 14 faces (baked)
FEATURE [Part::Feature] Part__Feature228  label="729b0e92-9266-11ed-9e62-a0cec80452fd_part013"
  shape: bbox 1.198 x 0.41 x 1.07 mm, 14 faces (baked)
FEATURE [Part::Feature] Part__Feature229  label="729b0e92-9266-11ed-9e62-a0cec80452fd_part014"
  shape: bbox 1.198 x 0.41 x 1.07 mm, 14 faces (baked)
FEATURE [Part::Feature] Part__Feature230  label="729b0e92-9266-11ed-9e62-a0cec80452fd_part015"
  shape: bbox 1.198 x 0.41 x 1.07 mm, 14 faces (baked)
FEATURE [Part::Feature] Part__Feature231  label="729b0e92-9266-11ed-9e62-a0cec80452fd_part016"
  shape: bbox 1.198 x 0.41 x 1.07 mm, 14 faces (baked)
FEATURE [Part::Feature] Part__Feature232  label="729b1108-9266-11ed-9e62-a0cec80452fd_part001"
  shape: bbox 0.4 x 0.4 x 0.05 mm, 3 faces (baked)
FEATURE [Part::Feature] Pcb_29d001
  Placement = pos=(-25,115,0) rot=(0,0,1;0rad)
  shape: bbox 185 x 95 x 1.573 mm, 144 faces (baked)
FEATURE [App::Part] Board_Geoms_29d001  label="Board_Geoms_29d002"
  Group = -> [Pcb_29d001,PCB_Sketch_29d001]
  Origin = -> Origin035
FEATURE [App::Link] Q201_SOT_23_fb4564768f05_ln_006  label="Q2_SOT_23_d3792941e743"
  LinkPlacement = pos=(48.65,37.3,0) rot=(0,0,-1;1.5708rad)
  LinkedObject = -> Shape074
  Placement = pos=(48.65,37.3,0) rot=(0,0,-1;1.5708rad)
FEATURE [App::Link] Q201_SOT_23_fb4564768f05_ln_007  label="Q202_SOT_23_8fd5338d1ad004"
  LinkPlacement = pos=(67.6,50.4,0) rot=(0,0,1;1.5708rad)
  LinkedObject = -> Shape074
  Placement = pos=(67.6,50.4,0) rot=(0,0,1;1.5708rad)
FEATURE [App::Link] Q201_SOT_23_fb4564768f05_ln_008  label="Q206_SOT_23_7613cc9079a006"
  LinkPlacement = pos=(121.1,47.8,0) rot=(0,0,1;1.5708rad)
  LinkedObject = -> Shape074
  Placement = pos=(121.1,47.8,0) rot=(0,0,1;1.5708rad)
FEATURE [App::Link] Q201_SOT_23_fb4564768f05_ln_009  label="Q1_SOT_23_9944ca6c78aa001"
  LinkPlacement = pos=(48.7,21.6875,0) rot=(0,0,1;1.5708rad)
  LinkedObject = -> Shape074
  Placement = pos=(48.7,21.6875,0) rot=(0,0,1;1.5708rad)
FEATURE [App::Link] Q201_SOT_23_fb4564768f05_ln_010  label="Q301_SOT_23_3dcddfe8769a001"
  LinkPlacement = pos=(82.8125,21.55,0) rot=(0,0,1;1.5708rad)
  LinkedObject = -> Shape074
  Placement = pos=(82.8125,21.55,0) rot=(0,0,1;1.5708rad)
FEATURE [App::Link] Q201_SOT_23_fb4564768f05_ln_011  label="Q205_SOT_23_ab3f773d3a7f001"
  LinkPlacement = pos=(150.5,88.5,0) rot=(0,0,1;3.14159rad)
  LinkedObject = -> Shape074
  Placement = pos=(150.5,88.5,0) rot=(0,0,1;3.14159rad)
FEATURE [App::Link] Q201_SOT_23_fb4564768f05_ln_012  label="Q4_SOT_23_78596e99f7ac"
  LinkPlacement = pos=(153.65,10.1,-1.57252) rot=(0.707107,0.707107,0;3.14159rad)
  LinkedObject = -> Shape074
  Placement = pos=(153.65,10.1,-1.57252) rot=(0.707107,0.707107,0;3.14159rad)
FEATURE [App::Link] Q203_TO_247_3_Vertical_e30fe5b94042_ln_003  label="Q207_TO-247-3_Vertical_764ed6fad74f001"
  LinkPlacement = pos=(143.45,87.82,0) rot=(0,0,1;3.14159rad)
  LinkedObject = -> Shape070
  Placement = pos=(143.45,87.82,0) rot=(0,0,1;3.14159rad)
FEATURE [App::Link] Q203_TO_247_3_Vertical_e30fe5b94042_ln_004  label="Q208_TO-247-3_Vertical_50f58b44882c001"
  LinkPlacement = pos=(132.55,52.18,0) rot=(0,0,1;0rad)
  LinkedObject = -> Shape070
  Placement = pos=(132.55,52.18,0) rot=(0,0,1;0rad)
FEATURE [App::Link] Q203_TO_247_3_Vertical_e30fe5b94042_ln_005  label="Q204_TO-247-3_Vertical_97f5affc5a013"
  LinkPlacement = pos=(78.1,52.18,0) rot=(0,0,1;0rad)
  LinkedObject = -> Shape070
  Placement = pos=(78.1,52.18,0) rot=(0,0,1;0rad)
FEATURE [App::Link] R240_R_2512_6332Metric_fe718b218676_ln_003  label="R239_R_2512_6332Metric_f1ce88b7dc038"
  LinkPlacement = pos=(175.5,27.05,-1.57252) rot=(0.707107,-0.707107,0;3.14159rad)
  LinkedObject = -> Shape086
  Placement = pos=(175.5,27.05,-1.57252) rot=(0.707107,-0.707107,0;3.14159rad)
FEATURE [App::Link] R240_R_2512_6332Metric_fe718b218676_ln_004  label="R220_R_2512_6332Metric_bee22148888a001"
  LinkPlacement = pos=(163.5,27,-1.57252) rot=(0.707107,-0.707107,0;3.14159rad)
  LinkedObject = -> Shape086
  Placement = pos=(163.5,27,-1.57252) rot=(0.707107,-0.707107,0;3.14159rad)
FEATURE [App::Link] R240_R_2512_6332Metric_fe718b218676_ln_005  label="R219_R_2512_6332Metric_1ec88cb2b337"
  LinkPlacement = pos=(169.55,11.5,-1.57252) rot=(0.707107,-0.707107,0;3.14159rad)
  LinkedObject = -> Shape086
  Placement = pos=(169.55,11.5,-1.57252) rot=(0.707107,-0.707107,0;3.14159rad)
FEATURE [App::Link] R28_R_0805_2012Metric_56a8941a8a89_ln_101  label="R232_R_0805_2012Metric_d40f949d485b001"
  LinkPlacement = pos=(181.3,23.7,0) rot=(0,0,1;1.5708rad)
  LinkedObject = -> Shape067
  Placement = pos=(181.3,23.7,0) rot=(0,0,1;1.5708rad)
FEATURE [App::Link] R28_R_0805_2012Metric_56a8941a8a89_ln_102  label="R30_R_0805_2012Metric_d3033175b96b001"
  LinkPlacement = pos=(133.6,27.375,0) rot=(0,0,1;0rad)
  LinkedObject = -> Shape067
  Placement = pos=(133.6,27.375,0) rot=(0,0,1;0rad)
FEATURE [App::Link] R28_R_0805_2012Metric_56a8941a8a89_ln_103  label="R234_R_0805_2012Metric_dea6c1b14177"
  LinkPlacement = pos=(163.438,5.5,0) rot=(0,0,1;1.5708rad)
  LinkedObject = -> Shape067
  Placement = pos=(163.438,5.5,0) rot=(0,0,1;1.5708rad)
FEATURE [App::Link] R28_R_0805_2012Metric_56a8941a8a89_ln_104  label="R229_R_0805_2012Metric_297f9286941b001"
  LinkPlacement = pos=(154,90.5,0) rot=(0,0,-1;1.5708rad)
  LinkedObject = -> Shape067
  Placement = pos=(154,90.5,0) rot=(0,0,-1;1.5708rad)
FEATURE [App::Link] R28_R_0805_2012Metric_56a8941a8a89_ln_105  label="R212_R_0805_2012Metric_83b1380610ae001"
  LinkPlacement = pos=(175.564,5.44,0) rot=(0,0,1;1.5708rad)
  LinkedObject = -> Shape067
  Placement = pos=(175.564,5.44,0) rot=(0,0,1;1.5708rad)
FEATURE [App::Link] R28_R_0805_2012Metric_56a8941a8a89_ln_106  label="R402_R_0805_2012Metric_8a70a5abb1a001"
  LinkPlacement = pos=(51.9,41.55,0) rot=(0,0,-1;1.5708rad)
  LinkedObject = -> Shape067
  Placement = pos=(51.9,41.55,0) rot=(0,0,-1;1.5708rad)
FEATURE [App::Link] R28_R_0805_2012Metric_56a8941a8a89_ln_107  label="R405_R_0805_2012Metric_12c457529534"
  LinkPlacement = pos=(128.275,6.125,0) rot=(0,0,1;1.5708rad)
  LinkedObject = -> Shape067
  Placement = pos=(128.275,6.125,0) rot=(0,0,1;1.5708rad)
FEATURE [App::Link] R28_R_0805_2012Metric_56a8941a8a89_ln_108  label="R322_R_0805_2012Metric_120e3dbff6d006"
  LinkPlacement = pos=(60.65,28.175,0) rot=(0,0,1;3.14159rad)
  LinkedObject = -> Shape067
  Placement = pos=(60.65,28.175,0) rot=(0,0,1;3.14159rad)
FEATURE [App::Link] R28_R_0805_2012Metric_56a8941a8a89_ln_109  label="R202_R_0805_2012Metric_c207ca0a30a006"
  LinkPlacement = pos=(40.9,50.3,0) rot=(0,0,1;1.5708rad)
  LinkedObject = -> Shape067
  Placement = pos=(40.9,50.3,0) rot=(0,0,1;1.5708rad)
FEATURE [App::Link] R28_R_0805_2012Metric_56a8941a8a89_ln_110  label="R19_R_0805_2012Metric_4ce773df796d001"
  LinkPlacement = pos=(44.45,16.7,0) rot=(0,0,1;0rad)
  LinkedObject = -> Shape067
  Placement = pos=(44.45,16.7,0) rot=(0,0,1;0rad)
FEATURE [App::Link] R28_R_0805_2012Metric_56a8941a8a89_ln_111  label="R325_R_0805_2012Metric_73d95f8b1a029"
  LinkPlacement = pos=(64.2125,25.05,0) rot=(0,0,1;3.14159rad)
  LinkedObject = -> Shape067
  Placement = pos=(64.2125,25.05,0) rot=(0,0,1;3.14159rad)
FEATURE [App::Link] R28_R_0805_2012Metric_56a8941a8a89_ln_112  label="R305_R_0805_2012Metric_eef09c2e666f001"
  LinkPlacement = pos=(48.95,33.2,0) rot=(0,0,1;0rad)
  LinkedObject = -> Shape067
  Placement = pos=(48.95,33.2,0) rot=(0,0,1;0rad)
FEATURE [App::Link] R28_R_0805_2012Metric_56a8941a8a89_ln_113  label="R40_R_0805_2012Metric_ae05bab19ef2"
  LinkPlacement = pos=(80.2,43.6,0) rot=(0,0,1;0rad)
  LinkedObject = -> Shape067
  Placement = pos=(80.2,43.6,0) rot=(0,0,1;0rad)
FEATURE [App::Link] R28_R_0805_2012Metric_56a8941a8a89_ln_114  label="R323_R_0805_2012Metric_93b05d35d6e008"
  LinkPlacement = pos=(55.8,20.6,0) rot=(0,0,-1;1.5708rad)
  LinkedObject = -> Shape067
  Placement = pos=(55.8,20.6,0) rot=(0,0,-1;1.5708rad)
FEATURE [App::Link] R28_R_0805_2012Metric_56a8941a8a89_ln_115  label="R330_R_0805_2012Metric_4650af7f38e010"
  LinkPlacement = pos=(60.6875,25.05,0) rot=(0,0,1;0rad)
  LinkedObject = -> Shape067
  Placement = pos=(60.6875,25.05,0) rot=(0,0,1;0rad)
FEATURE [App::Link] R28_R_0805_2012Metric_56a8941a8a89_ln_116  label="R218_R_0805_2012Metric_8cee86029e026"
  LinkPlacement = pos=(167.5,23.5,0) rot=(0,0,1;1.5708rad)
  LinkedObject = -> Shape067
  Placement = pos=(167.5,23.5,0) rot=(0,0,1;1.5708rad)
FEATURE [App::Link] R28_R_0805_2012Metric_56a8941a8a89_ln_117  label="R27_R_0805_2012Metric_dfc48d5b5f066"
  LinkPlacement = pos=(152.925,25.625,0) rot=(0,0,1;1.5708rad)
  LinkedObject = -> Shape067
  Placement = pos=(152.925,25.625,0) rot=(0,0,1;1.5708rad)
FEATURE [App::Link] R28_R_0805_2012Metric_56a8941a8a89_ln_118  label="R29_R_0805_2012Metric_b7007f5b310c001"
  LinkPlacement = pos=(149.5,29.9,0) rot=(0,0,1;0rad)
  LinkedObject = -> Shape067
  Placement = pos=(149.5,29.9,0) rot=(0,0,1;0rad)
FEATURE [App::Link] R28_R_0805_2012Metric_56a8941a8a89_ln_119  label="R317_R_0805_2012Metric_18c7baa40ddc001"
  LinkPlacement = pos=(33,37.1,0) rot=(0,0,1;0rad)
  LinkedObject = -> Shape067
  Placement = pos=(33,37.1,0) rot=(0,0,1;0rad)
FEATURE [App::Link] R28_R_0805_2012Metric_56a8941a8a89_ln_120  label="R32_R_0805_2012Metric_d8646d91ff031"
  LinkPlacement = pos=(142.7,28.2625,0) rot=(0,0,-1;1.5708rad)
  LinkedObject = -> Shape067
  Placement = pos=(142.7,28.2625,0) rot=(0,0,-1;1.5708rad)
FEATURE [App::Link] R28_R_0805_2012Metric_56a8941a8a89_ln_121  label="R314_R_0805_2012Metric_0aa6922b32fc001"
  LinkPlacement = pos=(32.85,19.45,0) rot=(0,0,1;0rad)
  LinkedObject = -> Shape067
  Placement = pos=(32.85,19.45,0) rot=(0,0,1;0rad)
FEATURE [App::Link] R28_R_0805_2012Metric_56a8941a8a89_ln_122  label="R301_R_0805_2012Metric_6580910332ae001"
  LinkPlacement = pos=(85.7375,25.1,0) rot=(0,0,-1;1.5708rad)
  LinkedObject = -> Shape067
  Placement = pos=(85.7375,25.1,0) rot=(0,0,-1;1.5708rad)
FEATURE [App::Link] R28_R_0805_2012Metric_56a8941a8a89_ln_123  label="R321_R_0805_2012Metric_afbedf02a5f010"
  LinkPlacement = pos=(52.825,22.325,0) rot=(0,0,1;0rad)
  LinkedObject = -> Shape067
  Placement = pos=(52.825,22.325,0) rot=(0,0,1;0rad)
FEATURE [App::Link] R28_R_0805_2012Metric_56a8941a8a89_ln_124  label="R320_R_0805_2012Metric_c88965fec193"
  LinkPlacement = pos=(82.8375,18.5,0) rot=(0,0,1;3.14159rad)
  LinkedObject = -> Shape067
  Placement = pos=(82.8375,18.5,0) rot=(0,0,1;3.14159rad)
FEATURE [App::Link] R28_R_0805_2012Metric_56a8941a8a89_ln_125  label="R233_R_0805_2012Metric_f44218af8ec009"
  LinkPlacement = pos=(163.438,13.5,0) rot=(0,0,1;1.5708rad)
  LinkedObject = -> Shape067
  Placement = pos=(163.438,13.5,0) rot=(0,0,1;1.5708rad)
FEATURE [App::Link] R28_R_0805_2012Metric_56a8941a8a89_ln_126  label="R238_R_0805_2012Metric_d4b0e688e9b005"
  LinkPlacement = pos=(161.438,5.5,0) rot=(0,0,1;1.5708rad)
  LinkedObject = -> Shape067
  Placement = pos=(161.438,5.5,0) rot=(0,0,1;1.5708rad)
FEATURE [App::Link] R28_R_0805_2012Metric_56a8941a8a89_ln_127  label="R210_R_0805_2012Metric_e3249320b20a001"
  LinkPlacement = pos=(62.3,50.5,0) rot=(0,0,-1;1.5708rad)
  LinkedObject = -> Shape067
  Placement = pos=(62.3,50.5,0) rot=(0,0,-1;1.5708rad)
FEATURE [App::Link] R28_R_0805_2012Metric_56a8941a8a89_ln_128  label="R404_R_0805_2012Metric_8929ad84e0bc001"
  LinkPlacement = pos=(117.45,5.65,0) rot=(0,0,1;3.14159rad)
  LinkedObject = -> Shape067
  Placement = pos=(117.45,5.65,0) rot=(0,0,1;3.14159rad)
FEATURE [App::Link] R28_R_0805_2012Metric_56a8941a8a89_ln_129  label="R303_R_0805_2012Metric_045e79a600fb001"
  LinkPlacement = pos=(122.4,35.7,0) rot=(0,0,-1;1.5708rad)
  LinkedObject = -> Shape067
  Placement = pos=(122.4,35.7,0) rot=(0,0,-1;1.5708rad)
FEATURE [App::Link] R28_R_0805_2012Metric_56a8941a8a89_ln_130  label="R225_R_0805_2012Metric_c06b0ccb0e2f001"
  LinkPlacement = pos=(98.815,50.9,0) rot=(0,0,1;3.14159rad)
  LinkedObject = -> Shape067
  Placement = pos=(98.815,50.9,0) rot=(0,0,1;3.14159rad)
FEATURE [App::Link] R28_R_0805_2012Metric_56a8941a8a89_ln_131  label="R312_R_0805_2012Metric_07deda23b152"
  LinkPlacement = pos=(36.45,21.55,0) rot=(0,0,1;0rad)
  LinkedObject = -> Shape067
  Placement = pos=(36.45,21.55,0) rot=(0,0,1;0rad)
FEATURE [App::Link] R28_R_0805_2012Metric_56a8941a8a89_ln_132  label="R503_R_0805_2012Metric_0159c068ed8e001"
  LinkPlacement = pos=(106.3,23.925,0) rot=(0,0,1;0rad)
  LinkedObject = -> Shape067
  Placement = pos=(106.3,23.925,0) rot=(0,0,1;0rad)
FEATURE [App::Link] R28_R_0805_2012Metric_56a8941a8a89_ln_133  label="R507_R_0805_2012Metric_bb3ac16f6f0c001"
  LinkPlacement = pos=(109.825,25.1,0) rot=(0,0,1;0rad)
  LinkedObject = -> Shape067
  Placement = pos=(109.825,25.1,0) rot=(0,0,1;0rad)
FEATURE [App::Link] R28_R_0805_2012Metric_56a8941a8a89_ln_134  label="R35_R_0805_2012Metric_bc73c2b9906b001"
  LinkPlacement = pos=(138.65,28.2625,0) rot=(0,0,-1;1.5708rad)
  LinkedObject = -> Shape067
  Placement = pos=(138.65,28.2625,0) rot=(0,0,-1;1.5708rad)
FEATURE [App::Link] R28_R_0805_2012Metric_56a8941a8a89_ln_135  label="R223_R_0805_2012Metric_527af22d81bc001"
  LinkPlacement = pos=(182.264,82.996,0) rot=(0,0,1;0rad)
  LinkedObject = -> Shape067
  Placement = pos=(182.264,82.996,0) rot=(0,0,1;0rad)
FEATURE [App::Link] R28_R_0805_2012Metric_56a8941a8a89_ln_136  label="R324_R_0805_2012Metric_1560be6bd8ac001"
  LinkPlacement = pos=(56.725,23.35,0) rot=(0,0,1;3.14159rad)
  LinkedObject = -> Shape067
  Placement = pos=(56.725,23.35,0) rot=(0,0,1;3.14159rad)
FEATURE [App::Link] R28_R_0805_2012Metric_56a8941a8a89_ln_137  label="R204_R_0805_2012Metric_b14df3f58a038"
  LinkPlacement = pos=(161.052,24.972,0) rot=(0,0,1;3.14159rad)
  LinkedObject = -> Shape067
  Placement = pos=(161.052,24.972,0) rot=(0,0,1;3.14159rad)
FEATURE [App::Link] R28_R_0805_2012Metric_56a8941a8a89_ln_138  label="R221_R_0805_2012Metric_e443798ed64c001"
  LinkPlacement = pos=(179.216,80.726,0) rot=(0,0,1;1.5708rad)
  LinkedObject = -> Shape067
  Placement = pos=(179.216,80.726,0) rot=(0,0,1;1.5708rad)
FEATURE [App::Link] R28_R_0805_2012Metric_56a8941a8a89_ln_139  label="R206_R_0805_2012Metric_b3859810ddf008"
  LinkPlacement = pos=(161.052,29.544,0) rot=(0,0,1;3.14159rad)
  LinkedObject = -> Shape067
  Placement = pos=(161.052,29.544,0) rot=(0,0,1;3.14159rad)
FEATURE [App::Link] R28_R_0805_2012Metric_56a8941a8a89_ln_140  label="R208_R_0805_2012Metric_7a516ad4c098"
  LinkPlacement = pos=(64.5,47.3,0) rot=(0,0,1;0rad)
  LinkedObject = -> Shape067
  Placement = pos=(64.5,47.3,0) rot=(0,0,1;0rad)
FEATURE [App::Link] R28_R_0805_2012Metric_56a8941a8a89_ln_141  label="R315_R_0805_2012Metric_a309409b1046"
  LinkPlacement = pos=(161.052,20.3,0) rot=(0,0,1;0rad)
  LinkedObject = -> Shape067
  Placement = pos=(161.052,20.3,0) rot=(0,0,1;0rad)
FEATURE [App::Link] R28_R_0805_2012Metric_56a8941a8a89_ln_142  label="R401_R_0805_2012Metric_89f38c3af4c006"
  LinkPlacement = pos=(55.9,32,0) rot=(0,0,1;1.5708rad)
  LinkedObject = -> Shape067
  Placement = pos=(55.9,32,0) rot=(0,0,1;1.5708rad)
FEATURE [App::Link] R28_R_0805_2012Metric_56a8941a8a89_ln_143  label="R309_R_0805_2012Metric_617f4d9395ee001"
  LinkPlacement = pos=(40.2,37.1,0) rot=(0,0,1;3.14159rad)
  LinkedObject = -> Shape067
  Placement = pos=(40.2,37.1,0) rot=(0,0,1;3.14159rad)
FEATURE [App::Link] R28_R_0805_2012Metric_56a8941a8a89_ln_144  label="R201_R_0805_2012Metric_906e28a1cc1a001"
  LinkPlacement = pos=(117.5,92.45,0) rot=(0,0,1;3.14159rad)
  LinkedObject = -> Shape067
  Placement = pos=(117.5,92.45,0) rot=(0,0,1;3.14159rad)
FEATURE [App::Link] R28_R_0805_2012Metric_56a8941a8a89_ln_145  label="R235_R_0805_2012Metric_c6c2d3c2ed7d001"
  LinkPlacement = pos=(179.3,31.7,0) rot=(0,0,1;1.5708rad)
  LinkedObject = -> Shape067
  Placement = pos=(179.3,31.7,0) rot=(0,0,1;1.5708rad)
FEATURE [App::Link] R28_R_0805_2012Metric_56a8941a8a89_ln_146  label="R217_R_0805_2012Metric_959eef384818"
  LinkPlacement = pos=(167.5,31.5,0) rot=(0,0,1;1.5708rad)
  LinkedObject = -> Shape067
  Placement = pos=(167.5,31.5,0) rot=(0,0,1;1.5708rad)
FEATURE [App::Link] R28_R_0805_2012Metric_56a8941a8a89_ln_147  label="R504_R_0805_2012Metric_879b1bd5ddf010"
  LinkPlacement = pos=(99.15,30.15,0) rot=(0,0,1;1.5708rad)
  LinkedObject = -> Shape067
  Placement = pos=(99.15,30.15,0) rot=(0,0,1;1.5708rad)
FEATURE [App::Link] R28_R_0805_2012Metric_56a8941a8a89_ln_148  label="R502_R_0805_2012Metric_ac830f34afeb001"
  LinkPlacement = pos=(103.45,24.475,0) rot=(0,0,1;1.5708rad)
  LinkedObject = -> Shape067
  Placement = pos=(103.45,24.475,0) rot=(0,0,1;1.5708rad)
FEATURE [App::Link] R28_R_0805_2012Metric_56a8941a8a89_ln_149  label="R205_R_0805_2012Metric_bc8565b3ccd004"
  LinkPlacement = pos=(47.5,46.5,0) rot=(0,0,1;3.14159rad)
  LinkedObject = -> Shape067
  Placement = pos=(47.5,46.5,0) rot=(0,0,1;3.14159rad)
FEATURE [App::Link] R28_R_0805_2012Metric_56a8941a8a89_ln_150  label="R38_R_0805_2012Metric_75b1e7ddb321"
  LinkPlacement = pos=(137.55,13.525,0) rot=(0,0,-1;1.5708rad)
  LinkedObject = -> Shape067
  Placement = pos=(137.55,13.525,0) rot=(0,0,-1;1.5708rad)
FEATURE [App::Link] R28_R_0805_2012Metric_56a8941a8a89_ln_151  label="R213_R_0805_2012Metric_7f63307805dd001"
  LinkPlacement = pos=(169.5,31.5,0) rot=(0,0,1;1.5708rad)
  LinkedObject = -> Shape067
  Placement = pos=(169.5,31.5,0) rot=(0,0,1;1.5708rad)
FEATURE [App::Link] R28_R_0805_2012Metric_56a8941a8a89_ln_152  label="R216_R_0805_2012Metric_6f09a1d043a008"
  LinkPlacement = pos=(173.564,5.44,0) rot=(0,0,1;1.5708rad)
  LinkedObject = -> Shape067
  Placement = pos=(173.564,5.44,0) rot=(0,0,1;1.5708rad)
FEATURE [App::Link] R28_R_0805_2012Metric_56a8941a8a89_ln_153  label="R224_R_0805_2012Metric_6ab6096b3db003"
  LinkPlacement = pos=(161.052,27.258,0) rot=(0,0,1;3.14159rad)
  LinkedObject = -> Shape067
  Placement = pos=(161.052,27.258,0) rot=(0,0,1;3.14159rad)
FEATURE [App::Link] R28_R_0805_2012Metric_56a8941a8a89_ln_154  label="R237_R_0805_2012Metric_03f2d14f6dd008"
  LinkPlacement = pos=(161.438,13.5,0) rot=(0,0,1;1.5708rad)
  LinkedObject = -> Shape067
  Placement = pos=(161.438,13.5,0) rot=(0,0,1;1.5708rad)
FEATURE [App::Link] R28_R_0805_2012Metric_56a8941a8a89_ln_155  label="R226_R_0805_2012Metric_8c5f65e5c5e002"
  LinkPlacement = pos=(161.052,22.636,0) rot=(0,0,1;3.14159rad)
  LinkedObject = -> Shape067
  Placement = pos=(161.052,22.636,0) rot=(0,0,1;3.14159rad)
FEATURE [App::Link] R28_R_0805_2012Metric_56a8941a8a89_ln_156  label="R26_R_0805_2012Metric_964cbbcd5237"
  LinkPlacement = pos=(128.05,30.35,0) rot=(0,0,-1;1.5708rad)
  LinkedObject = -> Shape067
  Placement = pos=(128.05,30.35,0) rot=(0,0,-1;1.5708rad)
FEATURE [App::Link] R28_R_0805_2012Metric_56a8941a8a89_ln_157  label="R20_R_0805_2012Metric_df453e6bea019"
  LinkPlacement = pos=(48.6,40.45,0) rot=(0,0,1;0rad)
  LinkedObject = -> Shape067
  Placement = pos=(48.6,40.45,0) rot=(0,0,1;0rad)
FEATURE [App::Link] R28_R_0805_2012Metric_56a8941a8a89_ln_158  label="R313_R_0805_2012Metric_8c169fd2acfc001"
  LinkPlacement = pos=(33,39.2,0) rot=(0,0,1;3.14159rad)
  LinkedObject = -> Shape067
  Placement = pos=(33,39.2,0) rot=(0,0,1;3.14159rad)
FEATURE [App::Link] R28_R_0805_2012Metric_56a8941a8a89_ln_159  label="R211_R_0805_2012Metric_3ad5823d24fb001"
  LinkPlacement = pos=(175.564,13.44,0) rot=(0,0,1;1.5708rad)
  LinkedObject = -> Shape067
  Placement = pos=(175.564,13.44,0) rot=(0,0,1;1.5708rad)
FEATURE [App::Link] R28_R_0805_2012Metric_56a8941a8a89_ln_160  label="R18_R_0805_2012Metric_05efc19aec047"
  LinkPlacement = pos=(44.5,42.1,0) rot=(0,0,1;0rad)
  LinkedObject = -> Shape067
  Placement = pos=(44.5,42.1,0) rot=(0,0,1;0rad)
FEATURE [App::Link] R28_R_0805_2012Metric_56a8941a8a89_ln_161  label="R319_R_0805_2012Metric_2d5fad86d1aa001"
  LinkPlacement = pos=(158.052,29.798,0) rot=(0,0,-1;1.5708rad)
  LinkedObject = -> Shape067
  Placement = pos=(158.052,29.798,0) rot=(0,0,-1;1.5708rad)
FEATURE [App::Link] R28_R_0805_2012Metric_56a8941a8a89_ln_162  label="R39_R_0805_2012Metric_b2f2924be4e8"
  LinkPlacement = pos=(80.2,41.4,0) rot=(0,0,1;3.14159rad)
  LinkedObject = -> Shape067
  Placement = pos=(80.2,41.4,0) rot=(0,0,1;3.14159rad)
FEATURE [App::Link] R28_R_0805_2012Metric_56a8941a8a89_ln_163  label="R310_R_0805_2012Metric_f6025bc696d010"
  LinkPlacement = pos=(40.05,21.55,0) rot=(0,0,1;0rad)
  LinkedObject = -> Shape067
  Placement = pos=(40.05,21.55,0) rot=(0,0,1;0rad)
FEATURE [App::Link] R28_R_0805_2012Metric_56a8941a8a89_ln_164  label="R308_R_0805_2012Metric_7133bf9c9c008"
  LinkPlacement = pos=(43.65,21.55,0) rot=(0,0,1;0rad)
  LinkedObject = -> Shape067
  Placement = pos=(43.65,21.55,0) rot=(0,0,1;0rad)
FEATURE [App::Link] R28_R_0805_2012Metric_56a8941a8a89_ln_165  label="R37_R_0805_2012Metric_006564c923aa001"
  LinkPlacement = pos=(135.05,13.925,0) rot=(0,0,-1;1.5708rad)
  LinkedObject = -> Shape067
  Placement = pos=(135.05,13.925,0) rot=(0,0,-1;1.5708rad)
FEATURE [App::Link] R28_R_0805_2012Metric_56a8941a8a89_ln_166  label="R214_R_0805_2012Metric_3d6add19a857"
  LinkPlacement = pos=(169.5,23.5,0) rot=(0,0,1;1.5708rad)
  LinkedObject = -> Shape067
  Placement = pos=(169.5,23.5,0) rot=(0,0,1;1.5708rad)
FEATURE [App::Link] R28_R_0805_2012Metric_56a8941a8a89_ln_167  label="R36_R_0805_2012Metric_a42cad75e8b006"
  LinkPlacement = pos=(139.925,13.775,0) rot=(0,0,-1;1.5708rad)
  LinkedObject = -> Shape067
  Placement = pos=(139.925,13.775,0) rot=(0,0,-1;1.5708rad)
FEATURE [App::Link] R28_R_0805_2012Metric_56a8941a8a89_ln_168  label="R316_R_0805_2012Metric_fb924ddbbf051"
  LinkPlacement = pos=(156.052,29.798,0) rot=(0,0,1;1.5708rad)
  LinkedObject = -> Shape067
  Placement = pos=(156.052,29.798,0) rot=(0,0,1;1.5708rad)
FEATURE [App::Link] R28_R_0805_2012Metric_56a8941a8a89_ln_169  label="R304_R_0805_2012Metric_2a688e8f4436"
  LinkPlacement = pos=(118.131,38.4938,0) rot=(0,0,1;1.5708rad)
  LinkedObject = -> Shape067
  Placement = pos=(118.131,38.4938,0) rot=(0,0,1;1.5708rad)
FEATURE [App::Link] R28_R_0805_2012Metric_56a8941a8a89_ln_170  label="R228_R_0805_2012Metric_f03863a12791"
  LinkPlacement = pos=(117.2,49.4,0) rot=(0,0,1;0rad)
  LinkedObject = -> Shape067
  Placement = pos=(117.2,49.4,0) rot=(0,0,1;0rad)
FEATURE [App::Link] R28_R_0805_2012Metric_56a8941a8a89_ln_171  label="R302_R_0805_2012Metric_fa1ee39c645f001"
  LinkPlacement = pos=(107.075,38.875,0) rot=(0,0,1;3.14159rad)
  LinkedObject = -> Shape067
  Placement = pos=(107.075,38.875,0) rot=(0,0,1;3.14159rad)
FEATURE [App::Link] R28_R_0805_2012Metric_56a8941a8a89_ln_172  label="R16_R_0805_2012Metric_b01da35dd509"
  LinkPlacement = pos=(48.7,18.6,0) rot=(0,0,1;3.14159rad)
  LinkedObject = -> Shape067
  Placement = pos=(48.7,18.6,0) rot=(0,0,1;3.14159rad)
FEATURE [App::Link] R28_R_0805_2012Metric_56a8941a8a89_ln_173  label="R236_R_0805_2012Metric_c2c65c50b430"
  LinkPlacement = pos=(179.3,23.7,0) rot=(0,0,1;1.5708rad)
  LinkedObject = -> Shape067
  Placement = pos=(179.3,23.7,0) rot=(0,0,1;1.5708rad)
FEATURE [App::Link] R28_R_0805_2012Metric_56a8941a8a89_ln_174  label="R17_R_0805_2012Metric_430e81cda9d003"
  LinkPlacement = pos=(120.9,9.4,0) rot=(0,0,1;0rad)
  LinkedObject = -> Shape067
  Placement = pos=(120.9,9.4,0) rot=(0,0,1;0rad)
FEATURE [App::Link] R28_R_0805_2012Metric_56a8941a8a89_ln_175  label="R41_R_0805_2012Metric_b5d63ce3a870"
  LinkPlacement = pos=(89.2,44,0) rot=(0,0,1;0rad)
  LinkedObject = -> Shape067
  Placement = pos=(89.2,44,0) rot=(0,0,1;0rad)
FEATURE [App::Link] R28_R_0805_2012Metric_56a8941a8a89_ln_176  label="R306_R_0805_2012Metric_1ae52f8f6f7f001"
  LinkPlacement = pos=(49.05,26.2,0) rot=(0,0,1;0rad)
  LinkedObject = -> Shape067
  Placement = pos=(49.05,26.2,0) rot=(0,0,1;0rad)
FEATURE [App::Link] R28_R_0805_2012Metric_56a8941a8a89_ln_177  label="R230_R_0805_2012Metric_bf8a3ed9581b001"
  LinkPlacement = pos=(122.5,51,0) rot=(0,0,1;3.14159rad)
  LinkedObject = -> Shape067
  Placement = pos=(122.5,51,0) rot=(0,0,1;3.14159rad)
FEATURE [App::Link] R28_R_0805_2012Metric_56a8941a8a89_ln_178  label="R23_R_0805_2012Metric_437ce9947685"
  LinkPlacement = pos=(11.6,11.4,0) rot=(0,0,1;3.14159rad)
  LinkedObject = -> Shape067
  Placement = pos=(11.6,11.4,0) rot=(0,0,1;3.14159rad)
FEATURE [App::Link] R28_R_0805_2012Metric_56a8941a8a89_ln_179  label="R203_R_0805_2012Metric_44af99049a022"
  LinkPlacement = pos=(121,86.9,0) rot=(0,0,1;0rad)
  LinkedObject = -> Shape067
  Placement = pos=(121,86.9,0) rot=(0,0,1;0rad)
FEATURE [App::Link] R28_R_0805_2012Metric_56a8941a8a89_ln_180  label="R509_R_0805_2012Metric_d00c98e99795"
  LinkPlacement = pos=(111.075,28.35,0) rot=(0,0,1;1.5708rad)
  LinkedObject = -> Shape067
  Placement = pos=(111.075,28.35,0) rot=(0,0,1;1.5708rad)
FEATURE [App::Link] R28_R_0805_2012Metric_56a8941a8a89_ln_181  label="R318_R_0805_2012Metric_d8dd17164e4a001"
  LinkPlacement = pos=(32.8625,21.55,0) rot=(0,0,1;3.14159rad)
  LinkedObject = -> Shape067
  Placement = pos=(32.8625,21.55,0) rot=(0,0,1;3.14159rad)
FEATURE [App::Link] R28_R_0805_2012Metric_56a8941a8a89_ln_182  label="R33_R_0805_2012Metric_ee9e5949bf014"
  LinkPlacement = pos=(140.7,28.2625,0) rot=(0,0,-1;1.5708rad)
  LinkedObject = -> Shape067
  Placement = pos=(140.7,28.2625,0) rot=(0,0,-1;1.5708rad)
FEATURE [App::Link] R28_R_0805_2012Metric_56a8941a8a89_ln_183  label="R207_R_0805_2012Metric_bdedbc6ea7d005"
  LinkPlacement = pos=(100.5,87.4,0) rot=(0,0,-1;1.5708rad)
  LinkedObject = -> Shape067
  Placement = pos=(100.5,87.4,0) rot=(0,0,-1;1.5708rad)
FEATURE [App::Link] R28_R_0805_2012Metric_56a8941a8a89_ln_184  label="R209_R_0805_2012Metric_25a065108417"
  LinkPlacement = pos=(93.35,92.4,0) rot=(0,0,1;0rad)
  LinkedObject = -> Shape067
  Placement = pos=(93.35,92.4,0) rot=(0,0,1;0rad)
FEATURE [App::Link] R28_R_0805_2012Metric_56a8941a8a89_ln_185  label="R231_R_0805_2012Metric_e111ffe9ff5f001"
  LinkPlacement = pos=(181.3,31.7,0) rot=(0,0,1;1.5708rad)
  LinkedObject = -> Shape067
  Placement = pos=(181.3,31.7,0) rot=(0,0,1;1.5708rad)
FEATURE [App::Link] R28_R_0805_2012Metric_56a8941a8a89_ln_186  label="R31_R_0805_2012Metric_8e5e187749da001"
  LinkPlacement = pos=(145.65,29.9,0) rot=(0,0,1;3.14159rad)
  LinkedObject = -> Shape067
  Placement = pos=(145.65,29.9,0) rot=(0,0,1;3.14159rad)
FEATURE [App::Link] R28_R_0805_2012Metric_56a8941a8a89_ln_187  label="R34_R_0805_2012Metric_cce574930be010"
  LinkPlacement = pos=(136.625,28.2625,0) rot=(0,0,-1;1.5708rad)
  LinkedObject = -> Shape067
  Placement = pos=(136.625,28.2625,0) rot=(0,0,-1;1.5708rad)
FEATURE [App::Link] R28_R_0805_2012Metric_56a8941a8a89_ln_188  label="R403_R_0805_2012Metric_388f8d12b48e001"
  LinkPlacement = pos=(131.4,8.625,0) rot=(0,0,-1;1.5708rad)
  LinkedObject = -> Shape067
  Placement = pos=(131.4,8.625,0) rot=(0,0,-1;1.5708rad)
FEATURE [App::Link] R28_R_0805_2012Metric_56a8941a8a89_ln_189  label="R227_R_0805_2012Metric_51e4e134bd041"
  LinkPlacement = pos=(150.514,91.632,0) rot=(0,0,1;3.14159rad)
  LinkedObject = -> Shape067
  Placement = pos=(150.514,91.632,0) rot=(0,0,1;3.14159rad)
FEATURE [App::Link] R28_R_0805_2012Metric_56a8941a8a89_ln_190  label="R215_R_0805_2012Metric_b89aa1ef979c001"
  LinkPlacement = pos=(173.564,13.44,0) rot=(0,0,1;1.5708rad)
  LinkedObject = -> Shape067
  Placement = pos=(173.564,13.44,0) rot=(0,0,1;1.5708rad)
FEATURE [App::Link] R28_R_0805_2012Metric_56a8941a8a89_ln_191  label="R311_R_0805_2012Metric_05820cc1f1c001"
  LinkPlacement = pos=(36.6,37.1,0) rot=(0,0,1;3.14159rad)
  LinkedObject = -> Shape067
  Placement = pos=(36.6,37.1,0) rot=(0,0,1;3.14159rad)
FEATURE [App::Link] R28_R_0805_2012Metric_56a8941a8a89_ln_192  label="R222_R_0805_2012Metric_985d7a203053"
  LinkPlacement = pos=(98.815,46.3,0) rot=(0,0,1;0rad)
  LinkedObject = -> Shape067
  Placement = pos=(98.815,46.3,0) rot=(0,0,1;0rad)
FEATURE [App::Link] R28_R_0805_2012Metric_56a8941a8a89_ln_193  label="R307_R_0805_2012Metric_97ea5f9f84ef001"
  LinkPlacement = pos=(43.85,37.1,0) rot=(0,0,1;3.14159rad)
  LinkedObject = -> Shape067
  Placement = pos=(43.85,37.1,0) rot=(0,0,1;3.14159rad)
FEATURE [App::Link] R28_R_0805_2012Metric_56a8941a8a89_ln_194  label="R14_R_0805_2012Metric_c9232d1a5cfb001"
  LinkPlacement = pos=(81,15.8,-1.57252) rot=(0,1,0;3.14159rad)
  LinkedObject = -> Shape067
  Placement = pos=(81,15.8,-1.57252) rot=(0,1,0;3.14159rad)
FEATURE [App::Link] R28_R_0805_2012Metric_56a8941a8a89_ln_195  label="R13_R_0805_2012Metric_f526a781bf017"
  LinkPlacement = pos=(77.5,15.8,-1.57252) rot=(0,1,0;3.14159rad)
  LinkedObject = -> Shape067
  Placement = pos=(77.5,15.8,-1.57252) rot=(0,1,0;3.14159rad)
FEATURE [App::Link] R28_R_0805_2012Metric_56a8941a8a89_ln_196  label="R15_R_0805_2012Metric_05f071cc9f023"
  LinkPlacement = pos=(73.95,15.8,-1.57252) rot=(1,0,0;3.14159rad)
  LinkedObject = -> Shape067
  Placement = pos=(73.95,15.8,-1.57252) rot=(1,0,0;3.14159rad)
FEATURE [Part::Feature] Shape067  label="R28_R_0805_2012Metric_56a8941a8a090"
  Placement = pos=(129.7,27.375,0) rot=(0,0,1;3.14159rad)
  shape: bbox 2 x 1.2 x 0.45 mm, 26 faces (baked)
FEATURE [Part::Feature] Shape068  label="C303_C_0805_2012Metric_1d86ef2bb22f001"
  Placement = pos=(89.1655,19.502,0) rot=(0,0,1;3.14159rad)
  shape: bbox 2 x 1.25 x 1.25 mm, 28 faces (baked)
FEATURE [Part::Feature] Shape069  label="U18_SOT_23_5_bd1fc933e1e001"
  Placement = pos=(147.35,27.0625,0) rot=(0,0,1;3.14159rad)
  shape: bbox 2.8 x 2.9 x 1.55 mm, 109 faces (baked)
FEATURE [Part::Feature] Shape070  label="Q203_TO-247-3_Vertical_e30fe5b94043"
  Placement = pos=(89,87.82,0) rot=(0,0,1;3.14159rad)
  shape: bbox 15.9 x 5.03 x 41.1 mm, 64 faces (baked)
FEATURE [Part::Feature] Shape071  label="F1_A_Schurter_0031_8201_345dd88a4ad007"
  Placement = pos=(10.075,49.05,0) rot=(0,0,1;0rad)
  shape: bbox 22.8 x 9.6 x 15.5 mm, 119 faces (baked)
FEATURE [Part::Feature] Shape072  label="U23_SOT_223_402f57ec59fc"
  Placement = pos=(67,34.8,0) rot=(0,0,1;3.14159rad)
  shape: bbox 7 x 6.5 x 1.7 mm, 78 faces (baked)
FEATURE [Part::Feature] Shape006  label="U4_SOIC_8_39x49mm_P127mm_5e7587483eba001"
  Placement = pos=(105.55,19.9,0) rot=(0,0,1;0rad)
  shape: bbox 6 x 4.9 x 1.75 mm, 156 faces (baked)
FEATURE [Part::Feature] Shape073  label="D208_D_MiniMELF_Standard_5646c313d2d004"
  Placement = pos=(133,92.1,0) rot=(0,0,1;0rad)
  shape: bbox 3.6 x 1.4 x 1.4 mm, 13 faces (baked)
FEATURE [Part::Feature] Shape074  label="Q201_SOT_23_fb4564768f006"
  Placement = pos=(96.2,88.75,0) rot=(0,0,-1;1.5708rad)
  shape: bbox 3 x 2.5 x 1.2 mm, 76 faces (baked)
FEATURE [Part::Feature] Shape075  label="U11_TSSOP_16_44x5mm_P065mm_2417ac1ea51e001"
  Placement = pos=(122.775,14.875,0) rot=(0,0,1;0rad)
  shape: bbox 6.4 x 5 x 1.1 mm, 260 faces (baked)
FEATURE [Part::Feature] Shape076  label="U20_TSSOP_20_44x65mm_P065mm_4fdb420d92f005"
  Placement = pos=(139.025,20.075,0) rot=(0,0,-1;1.5708rad)
  shape: bbox 6.5 x 6.4 x 1.2 mm, 336 faces (baked)
FEATURE [Part::Feature] Shape077  label="J8_PinSocket_2x08_P254mm_Vertical_SMD_d83103ec4f9e001"
  Placement = pos=(143.48,4.95,0) rot=(0,0,1;1.5708rad)
  shape: bbox 20.32 x 7.94 x 7.3 mm, 570 faces (baked)
FEATURE [Part::Feature] Shape078  label="J9_JST_B2B_XH_A_e9e719df0531"
  Placement = pos=(57.5,90.275,0) rot=(0,0,1;0rad)
  shape: bbox 7.4 x 5.75 x 10.4 mm, 89 faces (baked)
FEATURE [Part::Feature] Shape079  label="U8_SO_4_44x43mm_P254mm_922b2c4537c008"
  Placement = pos=(38.7875,40.65,0) rot=(0,0,1;3.14159rad)
  shape: bbox 7 x 4.3 x 1.6 mm, 96 faces (baked)
FEATURE [Part::Feature] Shape080  label="J3_PinSocket_2x06_P254mm_Vertical_SMD_69addfe34575"
  Placement = pos=(96.98,8.25,0) rot=(0,0,1;0rad)
  shape: bbox 7.94 x 15.24 x 7.3 mm, 430 faces (baked)
FEATURE [Part::Feature] Shape081  label="D203_D_SMC_759b5137743e001"
  Placement = pos=(11.3,29.2,0) rot=(0,0,1;3.14159rad)
  shape: bbox 8 x 5.9 x 2.31 mm, 41 faces (baked)
FEATURE [Part::Feature] Shape082  label="HS102_LAM_3_K_93827ea2b8e010"
  Placement = pos=(5.3,70,21) rot=(0.57735,0.57735,0.57735;2.0944rad)
  shape: bbox 10 x 34.69 x 30 mm, 252 faces (baked)
FEATURE [Part::Feature] Shape083  label="J4_PinSocket_2x08_P254mm_Vertical_5fc2a641843f"
  Placement = pos=(73.605,33.49,0) rot=(0,0,1;1.5708rad)
  shape: bbox 20.32 x 5.08 x 10.1 mm, 506 faces (baked)
FEATURE [Part::Feature] Shape084  label="U21_TSOT_23_5_98ea53a2906e"
  Placement = pos=(96.2,39.4,0) rot=(0,0,1;0rad)
  shape: bbox 2.8 x 2.9 x 0.95 mm, 109 faces (baked)
FEATURE [Part::Feature] Shape085  label="Q101_TO-220-3_Vertical_ee802e7c2219"
  Placement = pos=(72.5,88.838,0) rot=(0,0,1;3.14159rad)
  shape: bbox 10.25 x 4.455 x 28.53 mm, 48 faces (baked)
FEATURE [Part::Feature] Shape086  label="R240_R_2512_6332Metric_fe718b218677"
  Placement = pos=(157.4,9.9,-1.57252) rot=(0.707107,-0.707107,0;3.14159rad)
  shape: bbox 3.2 x 6.3 x 0.6 mm, 26 faces (baked)
FEATURE [App::Part] Bot_29d001  label="Bot_29d002"
  Group = -> [R28_R_0805_2012Metric_56a8941a8a89_ln_194,Shape086,R28_R_0805_2012Metric_56a8941a8a89_ln_195,D208_D_MiniMELF_Standard_5646c313d2d3_ln_020,D208_D_MiniMELF_Standard_5646c313d2d3_ln_021,R240_R_2512_6332Metric_fe718b218676_ln_003,Q201_SOT_23_fb4564768f05_ln_012,R240_R_2512_6332Metric_fe718b218676_ln_004,R28_R_0805_2012Metric_56a8941a8a89_ln_196,R240_R_2512_6332Metric_fe718b218676_ln_005]
  Origin = -> Origin039
FEATURE [App::Part] TopV_29d001  label="TopV_29d002"
  Group = -> [Shape082]
  Origin = -> Origin041
FEATURE [App::Part] Step_Virtual_Models_29d001  label="Step_Virtual_Models_29d002"
  Group = -> [TopV_29d001]
  Origin = -> Origin040
FEATURE [App::Link] U11_TSSOP_16_44x5mm_P065mm_2417ac1ea51e_ln_001  label="U12_TSSOP_16_44x5mm_P065mm_b3bc334b253a001"
  LinkPlacement = pos=(122.8,22.225,0) rot=(0,0,1;0rad)
  LinkedObject = -> Shape075
  Placement = pos=(122.8,22.225,0) rot=(0,0,1;0rad)
FEATURE [App::Link] U18_SOT_23_5_bd1fc933e1e0_ln_009  label="U208_SOT_23_5_f89bbcba48aa001"
  LinkPlacement = pos=(164.4,9.5,0) rot=(0,0,-1;1.5708rad)
  LinkedObject = -> Shape069
  Placement = pos=(164.4,9.5,0) rot=(0,0,-1;1.5708rad)
FEATURE [App::Link] U18_SOT_23_5_bd1fc933e1e0_ln_010  label="U17_SOT_23_5_436ec76bf38b001"
  LinkPlacement = pos=(143.7,36.8875,0) rot=(0,0,-1;1.5708rad)
  LinkedObject = -> Shape069
  Placement = pos=(143.7,36.8875,0) rot=(0,0,-1;1.5708rad)
FEATURE [App::Link] U18_SOT_23_5_bd1fc933e1e0_ln_011  label="U15_SOT_23_5_f0dbcf2746ad001"
  LinkPlacement = pos=(134.55,37.35,0) rot=(0,0,-1;1.5708rad)
  LinkedObject = -> Shape069
  Placement = pos=(134.55,37.35,0) rot=(0,0,-1;1.5708rad)
FEATURE [App::Link] U18_SOT_23_5_bd1fc933e1e0_ln_012  label="U204_SOT_23_5_03575cd2eb1a001"
  LinkPlacement = pos=(170.453,27.497,0) rot=(0,0,-1;1.5708rad)
  LinkedObject = -> Shape069
  Placement = pos=(170.453,27.497,0) rot=(0,0,-1;1.5708rad)
FEATURE [App::Link] U18_SOT_23_5_bd1fc933e1e0_ln_013  label="U19_SOT_23_5_20d0edf1befc001"
  LinkPlacement = pos=(133.387,30.2,0) rot=(0,0,1;0rad)
  LinkedObject = -> Shape069
  Placement = pos=(133.387,30.2,0) rot=(0,0,1;0rad)
FEATURE [App::Link] U18_SOT_23_5_bd1fc933e1e0_ln_014  label="U303_SOT_23_5_a2d428d63c041"
  LinkPlacement = pos=(49.0136,29.5848,0) rot=(0,0,-1;1.5708rad)
  LinkedObject = -> Shape069
  Placement = pos=(49.0136,29.5848,0) rot=(0,0,-1;1.5708rad)
FEATURE [App::Link] U18_SOT_23_5_bd1fc933e1e0_ln_015  label="U203_SOT_23_5_686605622b006"
  LinkPlacement = pos=(176.55,9.45,0) rot=(0,0,-1;1.5708rad)
  LinkedObject = -> Shape069
  Placement = pos=(176.55,9.45,0) rot=(0,0,-1;1.5708rad)
FEATURE [App::Link] U18_SOT_23_5_bd1fc933e1e0_ln_016  label="U304_SOT_23_5_069fc6069df007"
  LinkPlacement = pos=(157.04,25.5816,0) rot=(0,0,1;1.5708rad)
  LinkedObject = -> Shape069
  Placement = pos=(157.04,25.5816,0) rot=(0,0,1;1.5708rad)
FEATURE [App::Link] U18_SOT_23_5_bd1fc933e1e0_ln_017  label="U207_SOT_23_5_5b9b638b9294"
  LinkPlacement = pos=(182.5,27.7,0) rot=(0,0,-1;1.5708rad)
  LinkedObject = -> Shape069
  Placement = pos=(182.5,27.7,0) rot=(0,0,-1;1.5708rad)
FEATURE [App::Link] U23_SOT_223_402f57ec59fc_ln_  label="U22_SOT_223_6c512a09e791"
  LinkPlacement = pos=(86.8,39.2,0) rot=(0,0,1;0rad)
  LinkedObject = -> Shape072
  Placement = pos=(86.8,39.2,0) rot=(0,0,1;0rad)
FEATURE [App::Link] U4_SOIC_8_39x49mm_P127mm_5e7587483eba_ln_010  label="U205_SOIC_8_39x49mm_P127mm_c7dffb358f062"
  LinkPlacement = pos=(168.5,89.5,0) rot=(0,0,1;3.14159rad)
  LinkedObject = -> Shape006
  Placement = pos=(168.5,89.5,0) rot=(0,0,1;3.14159rad)
FEATURE [App::Link] U4_SOIC_8_39x49mm_P127mm_5e7587483eba_ln_011  label="U201_SOIC_8_39x49mm_P127mm_d6a775eb0fcb001"
  LinkPlacement = pos=(109.2,89.55,0) rot=(0,0,1;3.14159rad)
  LinkedObject = -> Shape006
  Placement = pos=(109.2,89.55,0) rot=(0,0,1;3.14159rad)
FEATURE [App::Link] U4_SOIC_8_39x49mm_P127mm_5e7587483eba_ln_012  label="U302_SOIC_8_39x49mm_P127mm_e17913fd2d068"
  LinkPlacement = pos=(90.9435,23.312,0) rot=(0,0,1;3.14159rad)
  LinkedObject = -> Shape006
  Placement = pos=(90.9435,23.312,0) rot=(0,0,1;3.14159rad)
FEATURE [App::Link] U4_SOIC_8_39x49mm_P127mm_5e7587483eba_ln_013  label="U306_SOIC_8_39x49mm_P127mm_c9db6429261b001"
  LinkPlacement = pos=(62.3,21.2,0) rot=(0,0,1;0rad)
  LinkedObject = -> Shape006
  Placement = pos=(62.3,21.2,0) rot=(0,0,1;0rad)
FEATURE [App::Link] U4_SOIC_8_39x49mm_P127mm_5e7587483eba_ln_014  label="U301_SOIC_8_39x49mm_P127mm_0413ce41aa030"
  LinkPlacement = pos=(113.231,37.9938,0) rot=(0,0,1;0rad)
  LinkedObject = -> Shape006
  Placement = pos=(113.231,37.9938,0) rot=(0,0,1;0rad)
FEATURE [App::Link] U4_SOIC_8_39x49mm_P127mm_5e7587483eba_ln_015  label="U402_SOIC_8_39x49mm_P127mm_2080084d9266"
  LinkPlacement = pos=(123.125,3.4,0) rot=(0,0,1;0rad)
  LinkedObject = -> Shape006
  Placement = pos=(123.125,3.4,0) rot=(0,0,1;0rad)
FEATURE [App::Link] U4_SOIC_8_39x49mm_P127mm_5e7587483eba_ln_016  label="U10_SOIC_8_39x49mm_P127mm_88c4924da8b004"
  LinkPlacement = pos=(106.1,29,0) rot=(0,0,1;0rad)
  LinkedObject = -> Shape006
  Placement = pos=(106.1,29,0) rot=(0,0,1;0rad)
FEATURE [App::Link] U4_SOIC_8_39x49mm_P127mm_5e7587483eba_ln_017  label="U202_SOIC_8_39x49mm_P127mm_747131a1281f001"
  LinkPlacement = pos=(53.9,49.5,0) rot=(0,0,1;0rad)
  LinkedObject = -> Shape006
  Placement = pos=(53.9,49.5,0) rot=(0,0,1;0rad)
FEATURE [App::Link] U4_SOIC_8_39x49mm_P127mm_5e7587483eba_ln_018  label="U206_SOIC_8_39x49mm_P127mm_1ada100df059"
  LinkPlacement = pos=(108.429,49.08,0) rot=(0,0,1;0rad)
  LinkedObject = -> Shape006
  Placement = pos=(108.429,49.08,0) rot=(0,0,1;0rad)
FEATURE [App::Link] U4_SOIC_8_39x49mm_P127mm_5e7587483eba_ln_019  label="U401_SOIC_8_39x49mm_P127mm_e9e5c7414b6c001"
  LinkPlacement = pos=(56.725,40.05,0) rot=(0,0,1;0rad)
  LinkedObject = -> Shape006
  Placement = pos=(56.725,40.05,0) rot=(0,0,1;0rad)
FEATURE [App::Link] U8_SO_4_44x43mm_P254mm_922b2c4537c7_ln_001  label="U9_SO_4_44x43mm_P254mm_234cd6d6f7de001"
  LinkPlacement = pos=(38.6,18,0) rot=(0,0,1;3.14159rad)
  LinkedObject = -> Shape079
  Placement = pos=(38.6,18,0) rot=(0,0,1;3.14159rad)
FEATURE [App::Part] _29b0bae_9266_11ed_9e62_a0cec80452fd001  label="729b0bae-9266-11ed-9e62-a0cec80452fd001"
  Group = -> [Part__Feature223]
  Origin = -> Origin042
FEATURE [App::Part] _29b0e92_9266_11ed_9e62_a0cec80452fd_part001  label="729b0e92-9266-11ed-9e62-a0cec80452fd_part017"
  Group = -> [Part__Feature224,Part__Feature225,Part__Feature226,Part__Feature227,Part__Feature228,Part__Feature229,Part__Feature230,Part__Feature231]
  Origin = -> Origin043
FEATURE [App::Part] _29b0e92_9266_11ed_9e62_a0cec80452fd001  label="729b0e92-9266-11ed-9e62-a0cec80452fd001"
  Group = -> [_29b0e92_9266_11ed_9e62_a0cec80452fd_part001]
  Origin = -> Origin044
FEATURE [App::Part] _29b1108_9266_11ed_9e62_a0cec80452fd001  label="729b1108-9266-11ed-9e62-a0cec80452fd001"
  Group = -> [Part__Feature232]
  Origin = -> Origin045
FEATURE [App::Part] _29b06ae_9266_11ed_9e62_a0cec80452fd001  label="729b06ae-9266-11ed-9e62-a0cec80452fd001"
  Group = -> [_29b0bae_9266_11ed_9e62_a0cec80452fd001,_29b0e92_9266_11ed_9e62_a0cec80452fd001,_29b1108_9266_11ed_9e62_a0cec80452fd001]
  Origin = -> Origin046
FEATURE [App::Part] CQ_assembly002  label="U5_CQ assembly_2818d1c648ca001"
  Group = -> [_29b06ae_9266_11ed_9e62_a0cec80452fd001]
  Origin = -> Origin047
  Placement = pos=(47.45,3.25,0) rot=(0,0,1;3.14159rad)
FEATURE [App::Part] Top_29d001  label="Top_29d002"
  Group = -> [Shape067,Shape068,C303_C_0805_2012Metric_1d86ef2bb22f_ln_097,Shape069,Shape070,Shape071,C303_C_0805_2012Metric_1d86ef2bb22f_ln_098,C303_C_0805_2012Metric_1d86ef2bb22f_ln_099,R28_R_0805_2012Metric_56a8941a8a89_ln_101,C303_C_0805_2012Metric_1d86ef2bb22f_ln_100,C303_C_0805_2012Metric_1d86ef2bb22f_ln_101,R28_R_0805_2012Metric_56a8941a8a89_ln_102,R28_R_0805_2012Metric_56a8941a8a89_ln_103,+234 more]
  Origin = -> Origin038
FEATURE [App::Part] Step_Models_29d001  label="Step_Models_29d002"
  Group = -> [Top_29d001,Bot_29d001]
  Origin = -> Origin037
FEATURE [App::Part] Board_29d001  label="EL-Load-Analog001"
  Group = -> [Local_CS_29d001,Board_Geoms_29d001,Step_Models_29d001,Step_Virtual_Models_29d001]
  Origin = -> Origin036
  Placement = pos=(0,84,1.5) rot=(0,0,1;0rad)
FEATURE [Part::Box] Box004  label="meanwell rs15-5"
  AttacherType = Attacher::AttachEngine3D
  Height = 28
  Length = 62.5
  Placement = pos=(136,79,21.5) rot=(0,0,1;0rad)
  Width = 51
FEATURE [Part::Box] Box005  label="Cube"
  AttacherType = Attacher::AttachEngine3D
  Height = 18
  Length = 23
  Placement = pos=(196,32,10) rot=(0,0,1;0rad)
  Width = 38
FEATURE [App::Link] C5_C_0805_2012Metric_dc37d78c0e7e_ln_  label="C2_C_0805_2012Metric_83a90d12aea5"
  LinkPlacement = pos=(186.4,-72.5,-1.6) rot=(0.707107,-0.707107,0;3.14159rad)
  LinkedObject = -> Shape003
  Placement = pos=(186.4,-72.5,-1.6) rot=(0.707107,-0.707107,0;3.14159rad)
FEATURE [App::Link] C5_C_0805_2012Metric_dc37d78c0e7e_ln_001  label="C1_C_0805_2012Metric_7f214d5325a3"
  LinkPlacement = pos=(166.7,-76.4,-1.6) rot=(0.707107,0.707107,0;3.14159rad)
  LinkedObject = -> Shape003
  Placement = pos=(166.7,-76.4,-1.6) rot=(0.707107,0.707107,0;3.14159rad)
FEATURE [App::Link] C5_C_0805_2012Metric_dc37d78c0e7e_ln_002  label="C4_C_0805_2012Metric_61f9bc760d65"
  LinkPlacement = pos=(145.65,-84,-1.6) rot=(0.707107,0.707107,0;3.14159rad)
  LinkedObject = -> Shape003
  Placement = pos=(145.65,-84,-1.6) rot=(0.707107,0.707107,0;3.14159rad)
FEATURE [App::Link] C5_C_0805_2012Metric_dc37d78c0e7e_ln_003  label="C3_C_0805_2012Metric_59e6fa2387b6"
  LinkPlacement = pos=(165.05,-84.6,-1.6) rot=(1,0,0;3.14159rad)
  LinkedObject = -> Shape003
  Placement = pos=(165.05,-84.6,-1.6) rot=(1,0,0;3.14159rad)
FEATURE [App::Link] C5_C_0805_2012Metric_dc37d78c0e7e_ln_004  label="C7_C_0805_2012Metric_3fd35ebc905f"
  LinkPlacement = pos=(145.85,-71.3,-1.6) rot=(0.707107,0.707107,0;3.14159rad)
  LinkedObject = -> Shape003
  Placement = pos=(145.85,-71.3,-1.6) rot=(0.707107,0.707107,0;3.14159rad)
FEATURE [PartDesign::CoordinateSystem] Local_CS_85fa
  AttacherType = Attacher::AttachEngine3D
  AttachmentSupport = -> [X_Axis001]
  MapMode = 2
FEATURE [Sketcher::SketchObject] PCB_Sketch_85fa
  ArcFitTolerance = 0
  FullyConstrained = false
  MakeInternals = false
  sketch-geometry (12):
    g0: LineSegment StartX=170.1 StartY=-110.2 StartZ=0 EndX=236.1 EndY=-110.2 EndZ=0
    g1: LineSegment StartX=122.1 StartY=-69.2 StartZ=0 EndX=122.101 EndY=-84.2 EndZ=0
    g2: LineSegment StartX=126.1 StartY=-65.2 StartZ=0 EndX=236.1 EndY=-65.2 EndZ=0
    g3: LineSegment StartX=126.1 StartY=-88.1986 StartZ=0 EndX=162.101 EndY=-88.2014 EndZ=0
    g4: LineSegment StartX=166.1 StartY=-106.2 StartZ=0 EndX=166.1 EndY=-92.2 EndZ=0
    g5: LineSegment StartX=240.1 StartY=-69.2 StartZ=0 EndX=240.1 EndY=-106.2 EndZ=0
    g6: ArcOfCircle CenterX=236.1 CenterY=-69.2 CenterZ=0 NormalX=0 NormalY=0 NormalZ=-1 AngleXU=1.5708 Radius=4 StartAngle=0 EndAngle=1.5708
    g7: ArcOfCircle CenterX=170.1 CenterY=-106.2 CenterZ=0 NormalX=0 NormalY=0 NormalZ=-1 AngleXU=-1.5708 Radius=4 StartAngle=0 EndAngle=1.5708
    g8: ArcOfCircle CenterX=162.101 CenterY=-92.2 CenterZ=0 NormalX=0 NormalY=0 NormalZ=-1 AngleXU=1.5708 Radius=3.99862 StartAngle=0 EndAngle=1.5708
    g9: ArcOfCircle CenterX=126.1 CenterY=-69.2 CenterZ=0 NormalX=0 NormalY=0 NormalZ=-1 AngleXU=1.06478e-07 Radius=4 StartAngle=0 EndAngle=1.5708
    g10: ArcOfCircle CenterX=126.1 CenterY=-84.2 CenterZ=0 NormalX=0 NormalY=0 NormalZ=-1 AngleXU=-1.5708 Radius=3.99862 StartAngle=0 EndAngle=1.5708
    g11: ArcOfCircle CenterX=236.1 CenterY=-106.2 CenterZ=0 NormalX=0 NormalY=0 NormalZ=-1 AngleXU=-3.14159 Radius=4 StartAngle=0 EndAngle=1.5708
  constraints (12):
    c: Coincident(g1,g10)
    c: Coincident(g1,g9)
    c: Coincident(g3,g10)
    c: Coincident(g2,g9)
    c: Coincident(g3,g8)
    c: Coincident(g4,g7)
    c: Coincident(g4,g8)
    c: Coincident(g0,g7)
    c: Coincident(g0,g11)
    c: Coincident(g2,g6)
    c: Coincident(g5,g11)
    c: Coincident(g5,g6)
FEATURE [Part::Feature] Part__Feature  label="EC11_Rotary_Encoder_Switched"
  shape: bbox 1.5 x 1.93 x 7.07 mm, 34 faces (baked)
FEATURE [Part::Feature] Part__Feature001  label="EC11_Rotary_Encoder_Switched001"
  shape: bbox 1.5 x 1.93 x 7.07 mm, 34 faces (baked)
FEATURE [Part::Feature] Part__Feature002  label="EC11_Rotary_Encoder_Switched002"
  shape: bbox 1.5 x 1.93 x 7.07 mm, 34 faces (baked)
FEATURE [Part::Feature] Part__Feature003  label="EC11_Rotary_Encoder_Switched003"
  shape: bbox 1.5 x 1.93 x 7.07 mm, 34 faces (baked)
FEATURE [Part::Feature] Part__Feature004  label="EC11_Rotary_Encoder_Switched004"
  shape: bbox 1.5 x 1.93 x 7.07 mm, 34 faces (baked)
FEATURE [Part::Feature] Part__Feature005  label="EC11_Rotary_Encoder_Switched005"
  shape: bbox 13.1 x 12 x 9.87 mm, 116 faces (baked)
FEATURE [Part::Feature] Part__Feature006  label="EC11_Rotary_Encoder_Switched006"
  shape: bbox 11.8 x 12 x 1.6 mm, 18 faces (baked)
FEATURE [Part::Feature] Part__Feature007  label="EC11_Rotary_Encoder_Switched007"
  shape: bbox 11.8 x 12 x 3.4 mm, 82 faces (baked)
FEATURE [Part::Feature] Part__Feature008  label="EC11_Rotary_Encoder_Switched008"
  shape: bbox 11.8 x 12.5 x 8.743 mm, 73 faces (baked)
FEATURE [Part::Feature] Part__Feature009  label="EC11_Rotary_Encoder_Switched009"
  shape: bbox 5.658 x 5.782 x 13.3 mm, 102 faces (baked)
FEATURE [App::Part] EC11_Rotary_Encoder_Switched  label="ENC1_EC11_Rotary_Encoder_Switched010_dff9b8aaf94f[2]"
  Group = -> [Part__Feature,Part__Feature001,Part__Feature002,Part__Feature003,Part__Feature004,Part__Feature005,Part__Feature006,Part__Feature007,Part__Feature008,Part__Feature009]
  Origin = -> Origin008
  Placement = pos=(153.4,-77,0) rot=(0,0,-1;1.5708rad)
FEATURE [Part::Feature] Pcb_85fa
  shape: bbox 118 x 45 x 1.6 mm, 70 faces (baked)
FEATURE [App::Part] Board_Geoms_85fa
  Group = -> [Pcb_85fa,PCB_Sketch_85fa]
  Origin = -> Origin
FEATURE [App::Link] R13_R_0805_2012Metric_5b6da7abc100_ln_  label="R12_R_0805_2012Metric_ea710e860d27"
  LinkPlacement = pos=(149.1,-76.9875,-1.6) rot=(0.707107,0.707107,0;3.14159rad)
  LinkedObject = -> Shape002
  Placement = pos=(149.1,-76.9875,-1.6) rot=(0.707107,0.707107,0;3.14159rad)
FEATURE [App::Link] R13_R_0805_2012Metric_5b6da7abc100_ln_001  label="R6_R_0805_2012Metric_64955dbcc53a"
  LinkPlacement = pos=(149.1,-83.9875,-1.6) rot=(0.707107,0.707107,0;3.14159rad)
  LinkedObject = -> Shape002
  Placement = pos=(149.1,-83.9875,-1.6) rot=(0.707107,0.707107,0;3.14159rad)
FEATURE [App::Link] R13_R_0805_2012Metric_5b6da7abc100_ln_002  label="R5_R_0805_2012Metric_08355fbe83b5"
  LinkPlacement = pos=(161.35,-84.2,-1.6) rot=(0,1,0;3.14159rad)
  LinkedObject = -> Shape002
  Placement = pos=(161.35,-84.2,-1.6) rot=(0,1,0;3.14159rad)
FEATURE [App::Link] R13_R_0805_2012Metric_5b6da7abc100_ln_003  label="R10_R_0805_2012Metric_d85e806fa757"
  LinkPlacement = pos=(136.9,-73.3125,-1.6) rot=(0.707107,-0.707107,0;3.14159rad)
  LinkedObject = -> Shape002
  Placement = pos=(136.9,-73.3125,-1.6) rot=(0.707107,-0.707107,0;3.14159rad)
FEATURE [App::Link] R13_R_0805_2012Metric_5b6da7abc100_ln_004  label="R2_R_0805_2012Metric_a72552903f90"
  LinkPlacement = pos=(210.287,-71.2,-1.6) rot=(0,1,0;3.14159rad)
  LinkedObject = -> Shape002
  Placement = pos=(210.287,-71.2,-1.6) rot=(0,1,0;3.14159rad)
FEATURE [App::Link] R13_R_0805_2012Metric_5b6da7abc100_ln_005  label="R18_R_0805_2012Metric_25f6bbecb288"
  LinkPlacement = pos=(129.9,-76.7,-1.6) rot=(0,1,0;3.14159rad)
  LinkedObject = -> Shape002
  Placement = pos=(129.9,-76.7,-1.6) rot=(0,1,0;3.14159rad)
FEATURE [App::Link] R13_R_0805_2012Metric_5b6da7abc100_ln_006  label="R7_R_0805_2012Metric_691f852aec81"
  LinkPlacement = pos=(136.9,-76.9,-1.6) rot=(0.707107,0.707107,0;3.14159rad)
  LinkedObject = -> Shape002
  Placement = pos=(136.9,-76.9,-1.6) rot=(0.707107,0.707107,0;3.14159rad)
FEATURE [App::Link] R13_R_0805_2012Metric_5b6da7abc100_ln_007  label="R4_R_0805_2012Metric_bccac18c3cb5"
  LinkPlacement = pos=(161.35,-82.1,-1.6) rot=(0,1,0;3.14159rad)
  LinkedObject = -> Shape002
  Placement = pos=(161.35,-82.1,-1.6) rot=(0,1,0;3.14159rad)
FEATURE [App::Link] R13_R_0805_2012Metric_5b6da7abc100_ln_008  label="R8_R_0805_2012Metric_f9269aa7d845"
  LinkPlacement = pos=(149.1,-80.4875,-1.6) rot=(0.707107,-0.707107,0;3.14159rad)
  LinkedObject = -> Shape002
  Placement = pos=(149.1,-80.4875,-1.6) rot=(0.707107,-0.707107,0;3.14159rad)
FEATURE [App::Link] R13_R_0805_2012Metric_5b6da7abc100_ln_009  label="R3_R_0805_2012Metric_9573904aba2f"
  LinkPlacement = pos=(210.488,-82.1,-1.6) rot=(0,1,0;3.14159rad)
  LinkedObject = -> Shape002
  Placement = pos=(210.488,-82.1,-1.6) rot=(0,1,0;3.14159rad)
FEATURE [App::Link] R13_R_0805_2012Metric_5b6da7abc100_ln_010  label="R1_R_0805_2012Metric_a6e6cdb9ead7"
  LinkPlacement = pos=(210.287,-68.5,-1.6) rot=(0,1,0;3.14159rad)
  LinkedObject = -> Shape002
  Placement = pos=(210.287,-68.5,-1.6) rot=(0,1,0;3.14159rad)
FEATURE [Part::Feature] Shape  label="D1_LED_D3.0mm_e0fd27398e71"
  Placement = pos=(123.725,-76.7,0) rot=(0,0,1;0rad)
  shape: bbox 3.4 x 3.8 x 10.8 mm, 16 faces (baked)
FEATURE [Part::Feature] Shape001  label="J1_PinSocket_1x11_P254mm_Vertical_aa5addac6e48"
  Placement = pos=(170.125,-75.025,0) rot=(0,0,1;0rad)
  shape: bbox 2.54 x 27.94 x 10.1 mm, 351 faces (baked)
FEATURE [Part::Feature] Shape002  label="R13_R_0805_2012Metric_5b6da7abc100"
  Placement = pos=(149.1,-73.4875,-1.6) rot=(0.707107,-0.707107,0;3.14159rad)
  shape: bbox 1.2 x 2 x 0.45 mm, 26 faces (baked)
FEATURE [Part::Feature] Shape003  label="C5_C_0805_2012Metric_dc37d78c0e7e"
  Placement = pos=(136.9,-80.4125,-1.6) rot=(0.707107,-0.707107,0;3.14159rad)
  shape: bbox 1.25 x 2 x 1.25 mm, 28 faces (baked)
FEATURE [Part::Feature] Shape004  label="J2_IDC_Header_2x08_P254mm_Vertical_7d590179e4ec"
  Placement = pos=(195.28,-89.8,-1.6) rot=(0.707107,-0.707107,0;3.14159rad)
  shape: bbox 27.98 x 9.1 x 12.1 mm, 330 faces (baked)
FEATURE [Part::Feature] Shape005  label="U1_SOIC_18W_75x116mm_P127mm_06d87b56a7a8"
  Placement = pos=(193.6,-76.6,-1.6) rot=(0,1,0;3.14159rad)
  shape: bbox 10.3 x 11.55 x 2.75 mm, 306 faces (baked)
FEATURE [App::Part] Bot_85fa
  Group = -> [Shape002,Shape003,R13_R_0805_2012Metric_5b6da7abc100_ln_,R13_R_0805_2012Metric_5b6da7abc100_ln_001,R13_R_0805_2012Metric_5b6da7abc100_ln_002,R13_R_0805_2012Metric_5b6da7abc100_ln_003,R13_R_0805_2012Metric_5b6da7abc100_ln_004,R13_R_0805_2012Metric_5b6da7abc100_ln_005,C5_C_0805_2012Metric_dc37d78c0e7e_ln_,R13_R_0805_2012Metric_5b6da7abc100_ln_006,R13_R_0805_2012Metric_5b6da7abc100_ln_007,+9 more]
  Origin = -> Origin004
FEATURE [App::Part] Top_85fa
  Group = -> [Shape,Shape001,EC11_Rotary_Encoder_Switched]
  Origin = -> Origin003
FEATURE [App::Part] Step_Models_85fa
  Group = -> [Top_85fa,Bot_85fa]
  Origin = -> Origin002
FEATURE [App::Part] Board_85fa  label="EL-Load-Panel"
  Group = -> [Local_CS_85fa,Board_Geoms_85fa,Step_Models_85fa]
  Origin = -> Origin001
  Placement = pos=(11.5,245,113.5) rot=(-0.57735,0.57735,0.57735;4.18879rad)
FEATURE [App::Link] C22_C_0805_2012Metric_c419cd9c4a2f_ln_  label="C11_C_0805_2012Metric_a49b18341ced"
  LinkPlacement = pos=(30.4,11.2,0) rot=(0,0,1;0rad)
  LinkedObject = -> Shape088
  Placement = pos=(30.4,11.2,0) rot=(0,0,1;0rad)
FEATURE [App::Link] C22_C_0805_2012Metric_c419cd9c4a2f_ln_001  label="C26_C_0805_2012Metric_9980a3fec6f0"
  LinkPlacement = pos=(17.9,47.79,0) rot=(0,0,1;1.5708rad)
  LinkedObject = -> Shape088
  Placement = pos=(17.9,47.79,0) rot=(0,0,1;1.5708rad)
FEATURE [App::Link] C22_C_0805_2012Metric_c419cd9c4a2f_ln_002  label="C3_C_0805_2012Metric_15e1a894cb01"
  LinkPlacement = pos=(48,32.7,0) rot=(0,0,1;3.14159rad)
  LinkedObject = -> Shape088
  Placement = pos=(48,32.7,0) rot=(0,0,1;3.14159rad)
FEATURE [App::Link] C22_C_0805_2012Metric_c419cd9c4a2f_ln_003  label="C18_C_0805_2012Metric_e794a3d39e80"
  LinkPlacement = pos=(27.6,47.69,0) rot=(0,0,-1;1.5708rad)
  LinkedObject = -> Shape088
  Placement = pos=(27.6,47.69,0) rot=(0,0,-1;1.5708rad)
FEATURE [App::Link] C22_C_0805_2012Metric_c419cd9c4a2f_ln_004  label="C24_C_0805_2012Metric_f01b138523b2"
  LinkPlacement = pos=(77.05,43.95,0) rot=(0,0,-1;1.5708rad)
  LinkedObject = -> Shape088
  Placement = pos=(77.05,43.95,0) rot=(0,0,-1;1.5708rad)
FEATURE [App::Link] C22_C_0805_2012Metric_c419cd9c4a2f_ln_005  label="C9_C_0805_2012Metric_e36e869397a0"
  LinkPlacement = pos=(113.565,44.65,0) rot=(0,0,-1;1.5708rad)
  LinkedObject = -> Shape088
  Placement = pos=(113.565,44.65,0) rot=(0,0,-1;1.5708rad)
FEATURE [App::Link] C22_C_0805_2012Metric_c419cd9c4a2f_ln_006  label="C5_C_0805_2012Metric_15d6734f493a"
  LinkPlacement = pos=(80.8,23.3,0) rot=(0,0,1;0rad)
  LinkedObject = -> Shape088
  Placement = pos=(80.8,23.3,0) rot=(0,0,1;0rad)
FEATURE [App::Link] C22_C_0805_2012Metric_c419cd9c4a2f_ln_007  label="C23_C_0805_2012Metric_11de36914b62"
  LinkPlacement = pos=(76.35,49.3,0) rot=(0,0,1;0rad)
  LinkedObject = -> Shape088
  Placement = pos=(76.35,49.3,0) rot=(0,0,1;0rad)
FEATURE [App::Link] C22_C_0805_2012Metric_c419cd9c4a2f_ln_008  label="C12_C_0805_2012Metric_732eebdf556d"
  LinkPlacement = pos=(10.8,16.7,0) rot=(0,0,1;0rad)
  LinkedObject = -> Shape088
  Placement = pos=(10.8,16.7,0) rot=(0,0,1;0rad)
FEATURE [App::Link] C22_C_0805_2012Metric_c419cd9c4a2f_ln_009  label="C10_C_0805_2012Metric_be4c2624d97d"
  LinkPlacement = pos=(5.70002,25.2,0) rot=(0,0,1;1.5708rad)
  LinkedObject = -> Shape088
  Placement = pos=(5.70002,25.2,0) rot=(0,0,1;1.5708rad)
FEATURE [App::Link] C22_C_0805_2012Metric_c419cd9c4a2f_ln_010  label="C15_C_0805_2012Metric_1e921fb38b4c"
  LinkPlacement = pos=(14.4,24.2,0) rot=(0,0,1;0rad)
  LinkedObject = -> Shape088
  Placement = pos=(14.4,24.2,0) rot=(0,0,1;0rad)
FEATURE [App::Link] C22_C_0805_2012Metric_c419cd9c4a2f_ln_011  label="C2_C_0805_2012Metric_e26014cc501c"
  LinkPlacement = pos=(47.9,27.7,0) rot=(0,0,1;3.14159rad)
  LinkedObject = -> Shape088
  Placement = pos=(47.9,27.7,0) rot=(0,0,1;3.14159rad)
FEATURE [App::Link] C22_C_0805_2012Metric_c419cd9c4a2f_ln_012  label="C21_C_0805_2012Metric_054ffed93a8c"
  LinkPlacement = pos=(23.13,27.3,0) rot=(0,0,1;0rad)
  LinkedObject = -> Shape088
  Placement = pos=(23.13,27.3,0) rot=(0,0,1;0rad)
FEATURE [App::Link] C22_C_0805_2012Metric_c419cd9c4a2f_ln_013  label="C8_C_0805_2012Metric_242075c039d0"
  LinkPlacement = pos=(21.6,19.6,0) rot=(0,0,1;1.5708rad)
  LinkedObject = -> Shape088
  Placement = pos=(21.6,19.6,0) rot=(0,0,1;1.5708rad)
FEATURE [App::Link] C22_C_0805_2012Metric_c419cd9c4a2f_ln_014  label="C20_C_0805_2012Metric_a8166e63492a"
  LinkPlacement = pos=(63.7,49.1,0) rot=(0,0,1;0rad)
  LinkedObject = -> Shape088
  Placement = pos=(63.7,49.1,0) rot=(0,0,1;0rad)
FEATURE [App::Link] C22_C_0805_2012Metric_c419cd9c4a2f_ln_015  label="C16_C_0805_2012Metric_4b5c9fa2ab9d"
  LinkPlacement = pos=(33.7,12.7,0) rot=(0,0,1;1.5708rad)
  LinkedObject = -> Shape088
  Placement = pos=(33.7,12.7,0) rot=(0,0,1;1.5708rad)
FEATURE [App::Link] C22_C_0805_2012Metric_c419cd9c4a2f_ln_016  label="C17_C_0805_2012Metric_9c817947d75a"
  LinkPlacement = pos=(39.2,12.7285,0) rot=(0,0,1;1.5708rad)
  LinkedObject = -> Shape088
  Placement = pos=(39.2,12.7285,0) rot=(0,0,1;1.5708rad)
FEATURE [App::Link] C6_CP_Elec_63x58_0ee41fe4bfd3_ln_  label="C1_CP_Elec_63x58_5659c7eb80dd"
  LinkPlacement = pos=(58.3,19.8,0) rot=(0,0,1;0rad)
  LinkedObject = -> Shape087
  Placement = pos=(58.3,19.8,0) rot=(0,0,1;0rad)
FEATURE [App::Link] C6_CP_Elec_63x58_0ee41fe4bfd3_ln_001  label="C13_CP_Elec_63x58_4c4f2b69c62b"
  LinkPlacement = pos=(49.7,17.4,0) rot=(0,0,1;3.14159rad)
  LinkedObject = -> Shape087
  Placement = pos=(49.7,17.4,0) rot=(0,0,1;3.14159rad)
FEATURE [App::Link] C6_CP_Elec_63x58_0ee41fe4bfd3_ln_002  label="C30_CP_Elec_63x58_f829d7b62f1d"
  LinkPlacement = pos=(53.4,10,0) rot=(0,0,1;3.14159rad)
  LinkedObject = -> Shape087
  Placement = pos=(53.4,10,0) rot=(0,0,1;3.14159rad)
FEATURE [App::Link] C6_CP_Elec_63x58_0ee41fe4bfd3_ln_003  label="C19_CP_Elec_63x58_eae7f9406b11"
  LinkPlacement = pos=(22.83,36.2,0) rot=(0,0,1;3.14159rad)
  LinkedObject = -> Shape087
  Placement = pos=(22.83,36.2,0) rot=(0,0,1;3.14159rad)
FEATURE [App::Link] C6_CP_Elec_63x58_0ee41fe4bfd3_ln_004  label="C14_CP_Elec_63x58_56145b951646"
  LinkPlacement = pos=(31.7,1.80002,0) rot=(0,0,1;1.5708rad)
  LinkedObject = -> Shape087
  Placement = pos=(31.7,1.80002,0) rot=(0,0,1;1.5708rad)
FEATURE [App::Link] C6_CP_Elec_63x58_0ee41fe4bfd3_ln_005  label="C4_CP_Elec_63x58_b0d551f2ee6d"
  LinkPlacement = pos=(46.2,43,0) rot=(0,0,1;3.14159rad)
  LinkedObject = -> Shape087
  Placement = pos=(46.2,43,0) rot=(0,0,1;3.14159rad)
FEATURE [App::Link] C6_CP_Elec_63x58_0ee41fe4bfd3_ln_006  label="C7_CP_Elec_63x58_6e01dcfa2037"
  LinkPlacement = pos=(57.7,41.2,0) rot=(0,0,1;0rad)
  LinkedObject = -> Shape087
  Placement = pos=(57.7,41.2,0) rot=(0,0,1;0rad)
FEATURE [App::Link] D11_D_SMA_1bb42aa92948_ln_  label="D10_D_SMA_c2646ced11f3"
  LinkPlacement = pos=(8.70002,-1.19998,0) rot=(0,0,1;3.14159rad)
  LinkedObject = -> Shape018
  Placement = pos=(8.70002,-1.19998,0) rot=(0,0,1;3.14159rad)
FEATURE [App::Link] D11_D_SMA_1bb42aa92948_ln_001  label="D5_D_SMA_dbb58a46da9a"
  LinkPlacement = pos=(1.80002,10.7285,0) rot=(0,0,-1;1.5708rad)
  LinkedObject = -> Shape018
  Placement = pos=(1.80002,10.7285,0) rot=(0,0,-1;1.5708rad)
FEATURE [App::Link] D15_D_MiniMELF_Standard_ca1fadf4eb28_ln_  label="D16_D_MiniMELF_Standard_49aaf989b642"
  LinkPlacement = pos=(64.4,23.5,0) rot=(0,0,-1;1.5708rad)
  LinkedObject = -> Shape014
  Placement = pos=(64.4,23.5,0) rot=(0,0,-1;1.5708rad)
FEATURE [App::Link] D15_D_MiniMELF_Standard_ca1fadf4eb28_ln_001  label="D14_D_MiniMELF_Standard_869c8d3e9313"
  LinkPlacement = pos=(45,7.60002,0) rot=(0,0,1;0rad)
  LinkedObject = -> Shape014
  Placement = pos=(45,7.60002,0) rot=(0,0,1;0rad)
FEATURE [App::Link] D1_D_SOD_123_5a20a041a245_ln_  label="D2_D_SOD_123_9f952dc980be"
  LinkPlacement = pos=(48.7,38,0) rot=(0,0,1;3.14159rad)
  LinkedObject = -> Shape089
  Placement = pos=(48.7,38,0) rot=(0,0,1;3.14159rad)
FEATURE [App::Link] D1_D_SOD_123_5a20a041a245_ln_001  label="D4_D_SOD_123_a08d4832a5ee"
  LinkPlacement = pos=(52.3,27.7,0) rot=(0,0,1;3.14159rad)
  LinkedObject = -> Shape089
  Placement = pos=(52.3,27.7,0) rot=(0,0,1;3.14159rad)
FEATURE [App::Link] D1_D_SOD_123_5a20a041a245_ln_002  label="D3_D_SOD_123_c8b4b2da39fe"
  LinkPlacement = pos=(48.6,30.2,0) rot=(0,0,1;3.14159rad)
  LinkedObject = -> Shape089
  Placement = pos=(48.6,30.2,0) rot=(0,0,1;3.14159rad)
FEATURE [App::Link] D1_D_SOD_123_5a20a041a245_ln_003  label="D8_D_SOD_123_5a5f85ca8e2f"
  LinkPlacement = pos=(48.7,35.4,0) rot=(0,0,1;3.14159rad)
  LinkedObject = -> Shape089
  Placement = pos=(48.7,35.4,0) rot=(0,0,1;3.14159rad)
FEATURE [App::Link] D1_D_SOD_123_5a20a041a245_ln_004  label="D9_D_SOD_123_161a8bc13196"
  LinkPlacement = pos=(52.25,32.7,0) rot=(0,0,1;0rad)
  LinkedObject = -> Shape089
  Placement = pos=(52.25,32.7,0) rot=(0,0,1;0rad)
FEATURE [App::Link] D1_D_SOD_123_5a20a041a245_ln_005  label="D7_D_SOD_123_81fc6af181e9"
  LinkPlacement = pos=(48.6,25.1,0) rot=(0,0,1;3.14159rad)
  LinkedObject = -> Shape089
  Placement = pos=(48.6,25.1,0) rot=(0,0,1;3.14159rad)
FEATURE [App::Link] D6_LED_0805_2012Metric_630bc1ac9416_ln_  label="D13_LED_0805_2012Metric_31b94944d83b"
  LinkPlacement = pos=(40.2,3.4,0) rot=(0,0,1;3.14159rad)
  LinkedObject = -> Shape010
  Placement = pos=(40.2,3.4,0) rot=(0,0,1;3.14159rad)
FEATURE [App::Link] D6_LED_0805_2012Metric_630bc1ac9416_ln_001  label="D12_LED_0805_2012Metric_8e83bb0bb170"
  LinkPlacement = pos=(50.5,49.8,0) rot=(0,0,1;0rad)
  LinkedObject = -> Shape010
  Placement = pos=(50.5,49.8,0) rot=(0,0,1;0rad)
FEATURE [App::Link] JP8_PinHeader_1x02_P254mm_Vertical_ed570ec3ee34_ln_  label="J5_PinHeader_1x02_P254mm_Vertical_3b80083b2130"
  LinkPlacement = pos=(20.1,10,0) rot=(0,0,-1;1.5708rad)
  LinkedObject = -> Shape009
  Placement = pos=(20.1,10,0) rot=(0,0,-1;1.5708rad)
FEATURE [App::Link] JP8_PinHeader_1x02_P254mm_Vertical_ed570ec3ee34_ln_001  label="J6_PinHeader_1x02_P254mm_Vertical_92a677824943"
  LinkPlacement = pos=(3.30002,19.9285,0) rot=(0,0,-1;1.5708rad)
  LinkedObject = -> Shape009
  Placement = pos=(3.30002,19.9285,0) rot=(0,0,-1;1.5708rad)
FEATURE [App::Link] JP8_PinHeader_1x02_P254mm_Vertical_ed570ec3ee34_ln_002  label="JP5_PinHeader_1x02_P254mm_Vertical_806d60fd696a"
  LinkPlacement = pos=(67.7,25.2,0) rot=(0,0,1;0rad)
  LinkedObject = -> Shape009
  Placement = pos=(67.7,25.2,0) rot=(0,0,1;0rad)
FEATURE [App::Link] JP8_PinHeader_1x02_P254mm_Vertical_ed570ec3ee34_ln_003  label="JP6_PinHeader_1x02_P254mm_Vertical_0c23ef1a54e6"
  LinkPlacement = pos=(47.5,4.3,0) rot=(0,0,1;1.5708rad)
  LinkedObject = -> Shape009
  Placement = pos=(47.5,4.3,0) rot=(0,0,1;1.5708rad)
FEATURE [App::Link] JP8_PinHeader_1x02_P254mm_Vertical_ed570ec3ee34_ln_004  label="JP4_PinHeader_1x02_P254mm_Vertical_b2b0b4eb230f"
  LinkPlacement = pos=(55.95,49.725,0) rot=(0,0,1;1.5708rad)
  LinkedObject = -> Shape009
  Placement = pos=(55.95,49.725,0) rot=(0,0,1;1.5708rad)
FEATURE [App::Link] L2_L_1210_3225Metric_8f5c69fc0355_ln_  label="L8_L_1210_3225Metric_c8d3be7f3657"
  LinkPlacement = pos=(60.6,25.3,0) rot=(0,0,1;3.14159rad)
  LinkedObject = -> Shape013
  Placement = pos=(60.6,25.3,0) rot=(0,0,1;3.14159rad)
FEATURE [App::Link] L2_L_1210_3225Metric_8f5c69fc0355_ln_001  label="L3_L_1210_3225Metric_d7bc27af3adb"
  LinkPlacement = pos=(46.8,11.3,0) rot=(0,0,1;1.5708rad)
  LinkedObject = -> Shape013
  Placement = pos=(46.8,11.3,0) rot=(0,0,1;1.5708rad)
FEATURE [PartDesign::CoordinateSystem] Local_CS_51fb
  AttacherType = Attacher::AttachEngine3D
  AttachmentSupport = -> [X_Axis049]
  MapMode = 2
FEATURE [App::Link] M2_Fan_Pin_Header_Straight_1x04_4971bfcbb112_ln_  label="M3_Fan_Pin_Header_Straight_1x04_d9628b9d4d16"
  LinkPlacement = pos=(5.92002,4.60002,0) rot=(0,0,1;0rad)
  LinkedObject = -> Shape093
  Placement = pos=(5.92002,4.60002,0) rot=(0,0,1;0rad)
FEATURE [App::Link] M2_Fan_Pin_Header_Straight_1x04_4971bfcbb112_ln_001  label="M1_Fan_Pin_Header_Straight_1x04_37f54f52d17d"
  LinkPlacement = pos=(18.48,4.50002,0) rot=(0,0,1;0rad)
  LinkedObject = -> Shape093
  Placement = pos=(18.48,4.50002,0) rot=(0,0,1;0rad)
FEATURE [Sketcher::SketchObject] PCB_Sketch_51fb
  ArcFitTolerance = 0
  FullyConstrained = false
  MakeInternals = false
  sketch-geometry (16):
    g0: LineSegment StartX=36.25 StartY=-13.5 StartZ=0 EndX=36.25 EndY=-7.99998 EndZ=0
    g1: LineSegment StartX=2e-05 StartY=-3.99998 StartZ=0 EndX=32.25 EndY=-3.99998 EndZ=0
    g2: LineSegment StartX=-3.99998 StartY=2.3e-05 StartZ=0 EndX=-3.99998 EndY=52 EndZ=0
    g3: LineSegment StartX=161 StartY=52 StartZ=0 EndX=161 EndY=2.3e-05 EndZ=0
    g4: LineSegment StartX=64 StartY=-3.99998 StartZ=0 EndX=157 EndY=-3.99998 EndZ=0
    g5: LineSegment StartX=60 StartY=-13.5 StartZ=0 EndX=60 EndY=-7.99998 EndZ=0
    g6: LineSegment StartX=39.25 StartY=-16.5 StartZ=0 EndX=57 EndY=-16.5 EndZ=0
    g7: LineSegment StartX=2e-05 StartY=56 StartZ=0 EndX=157 EndY=56 EndZ=0
    g8: ArcOfCircle CenterX=1.70117e-05 CenterY=52 CenterZ=0 NormalX=0 NormalY=0 NormalZ=-1 AngleXU=-7.47076e-07 Radius=4 StartAngle=0 EndAngle=1.5708
    g9: ArcOfCircle CenterX=57 CenterY=-13.5 CenterZ=0 NormalX=0 NormalY=0 NormalZ=-1 AngleXU=-3.14159 Radius=3 StartAngle=0 EndAngle=1.5708
    g10: ArcOfCircle CenterX=64 CenterY=-7.99995 CenterZ=0 NormalX=0 NormalY=0 NormalZ=-1 AngleXU=-5.86839e-06 Radius=3.99998 StartAngle=0 EndAngle=1.57081
    g11: ArcOfCircle CenterX=157 CenterY=6.78113e-05 CenterZ=0 NormalX=0 NormalY=0 NormalZ=-1 AngleXU=-3.14158 Radius=4.00004 StartAngle=0 EndAngle=1.57077
    g12: ArcOfCircle CenterX=39.25 CenterY=-13.5 CenterZ=0 NormalX=0 NormalY=0 NormalZ=-1 AngleXU=-1.5708 Radius=3 StartAngle=0 EndAngle=1.5708
    g13: ArcOfCircle CenterX=32.25 CenterY=-7.99995 CenterZ=0 NormalX=0 NormalY=0 NormalZ=-1 AngleXU=1.57079 Radius=3.99998 StartAngle=0 EndAngle=1.57081
    g14: ArcOfCircle CenterX=-5.92595e-08 CenterY=2.94074e-06 CenterZ=0 NormalX=0 NormalY=0 NormalZ=-1 AngleXU=-1.5708 Radius=3.99998 StartAngle=0 EndAngle=1.57081
    g15: ArcOfCircle CenterX=157 CenterY=52 CenterZ=0 NormalX=0 NormalY=0 NormalZ=-1 AngleXU=1.5708 Radius=4.00002 StartAngle=0 EndAngle=1.57079
  constraints (16):
    c: Coincident(g2,g14)
    c: Coincident(g2,g8)
    c: Coincident(g1,g14)
    c: Coincident(g7,g8)
    c: Coincident(g1,g13)
    c: Coincident(g0,g12)
    c: Coincident(g0,g13)
    c: Coincident(g6,g12)
    c: Coincident(g6,g9)
    c: Coincident(g5,g9)
    c: Coincident(g5,g10)
    c: Coincident(g4,g10)
    c: Coincident(g4,g11)
    c: Coincident(g7,g15)
    c: Coincident(g3,g11)
    c: Coincident(g3,g15)
FEATURE [Part::Feature] Part__Feature233  label="TestPoint_Loop_D2_54mm_Drill1_5mm_Beaded_cp"
  shape: bbox 3 x 3 x 3 mm, 4 faces (baked)
FEATURE [Part::Feature] Part__Feature234  label="TestPoint_Loop_D2_54mm_Drill1_5mm_Beaded_cp001"
  shape: bbox 3.415 x 0.9501 x 9.255 mm, 7 faces (baked)
FEATURE [Part::Feature] Part__Feature235  label="SC0915"
  shape: bbox 3.8 x 1 x 3.8 mm, 6 faces (baked)
FEATURE [Part::Feature] Part__Feature236  label="SC0916"
  shape: bbox 3.8 x 1 x 3.8 mm, 6 faces (baked)
FEATURE [Part::Feature] Part__Feature237  label="SC0917"
  shape: bbox 3.8 x 1 x 3.8 mm, 6 faces (baked)
FEATURE [Part::Feature] Part__Feature238  label="SC0918"
  shape: bbox 3.8 x 1 x 3.8 mm, 6 faces (baked)
FEATURE [Part::Feature] Part__Feature239  label="SC0919"
  shape: bbox 2.41 x 1 x 1.6 mm, 10 faces (baked)
FEATURE [Part::Feature] Part__Feature240  label="SC0920"
  shape: bbox 2.41 x 1 x 1.6 mm, 10 faces (baked)
FEATURE [Part::Feature] Part__Feature241  label="SC0921"
  shape: bbox 2.41 x 1 x 1.6 mm, 10 faces (baked)
FEATURE [Part::Feature] Part__Feature242  label="SC0922"
  shape: bbox 2.41 x 1 x 1.6 mm, 10 faces (baked)
FEATURE [Part::Feature] Part__Feature010  label="SC0923"
  shape: bbox 2.41 x 1 x 1.6 mm, 10 faces (baked)
FEATURE [Part::Feature] Part__Feature011  label="SC0924"
  shape: bbox 2.41 x 1 x 1.6 mm, 10 faces (baked)
FEATURE [Part::Feature] Part__Feature012  label="SC0925"
  shape: bbox 2.41 x 1 x 1.6 mm, 10 faces (baked)
FEATURE [Part::Feature] Part__Feature013  label="SC0926"
  shape: bbox 2.41 x 1 x 1.6 mm, 10 faces (baked)
FEATURE [Part::Feature] Part__Feature014  label="SC0927"
  shape: bbox 2.41 x 1 x 1.6 mm, 10 faces (baked)
FEATURE [Part::Feature] Part__Feature015  label="SC0928"
  shape: bbox 2.41 x 1 x 1.6 mm, 10 faces (baked)
FEATURE [Part::Feature] Part__Feature016  label="SC0929"
  shape: bbox 2.41 x 1 x 1.6 mm, 10 faces (baked)
FEATURE [Part::Feature] Part__Feature243  label="SC0930"
  shape: bbox 2.41 x 1 x 1.6 mm, 10 faces (baked)
FEATURE [Part::Feature] Part__Feature244  label="SC0931"
  shape: bbox 2.41 x 1 x 1.6 mm, 10 faces (baked)
FEATURE [Part::Feature] Part__Feature245  label="SC0932"
  shape: bbox 2.41 x 1 x 1.6 mm, 10 faces (baked)
FEATURE [Part::Feature] Part__Feature246  label="SC0933"
  shape: bbox 2.41 x 1 x 1.6 mm, 10 faces (baked)
FEATURE [Part::Feature] Part__Feature247  label="SC0934"
  shape: bbox 2.41 x 1 x 1.6 mm, 10 faces (baked)
FEATURE [Part::Feature] Part__Feature248  label="SC0935"
  shape: bbox 2.41 x 1 x 1.6 mm, 12 faces (baked)
FEATURE [Part::Feature] Part__Feature249  label="SC0936"
  shape: bbox 2.41 x 1 x 1.6 mm, 12 faces (baked)
FEATURE [Part::Feature] Part__Feature250  label="SC0937"
  shape: bbox 2.41 x 1 x 1.6 mm, 12 faces (baked)
FEATURE [Part::Feature] Part__Feature251  label="SC0938"
  shape: bbox 2.41 x 1 x 1.6 mm, 12 faces (baked)
FEATURE [Part::Feature] Part__Feature252  label="SC0939"
  shape: bbox 2.41 x 1 x 1.6 mm, 12 faces (baked)
FEATURE [Part::Feature] Part__Feature253  label="SC0940"
  shape: bbox 2.41 x 1 x 1.6 mm, 12 faces (baked)
FEATURE [Part::Feature] Part__Feature254  label="SC0941"
  shape: bbox 2.41 x 1 x 1.6 mm, 12 faces (baked)
FEATURE [Part::Feature] Part__Feature255  label="SC0942"
  shape: bbox 2.41 x 1 x 1.6 mm, 12 faces (baked)
FEATURE [Part::Feature] Part__Feature256  label="SC0943"
  shape: bbox 2.41 x 1 x 1.6 mm, 10 faces (baked)
FEATURE [Part::Feature] Part__Feature031  label="SC0944"
  shape: bbox 2.41 x 1 x 1.6 mm, 10 faces (baked)
FEATURE [Part::Feature] Part__Feature032  label="SC0945"
  shape: bbox 2.41 x 1 x 1.6 mm, 10 faces (baked)
FEATURE [Part::Feature] Part__Feature033  label="SC0946"
  shape: bbox 2.41 x 1 x 1.6 mm, 10 faces (baked)
FEATURE [Part::Feature] Part__Feature034  label="SC0947"
  shape: bbox 2.41 x 1 x 1.6 mm, 10 faces (baked)
FEATURE [Part::Feature] Part__Feature035  label="SC0948"
  shape: bbox 2.41 x 1 x 1.6 mm, 10 faces (baked)
FEATURE [Part::Feature] Part__Feature036  label="SC0949"
  shape: bbox 2.41 x 1 x 1.6 mm, 10 faces (baked)
FEATURE [Part::Feature] Part__Feature037  label="SC0950"
  shape: bbox 2.41 x 1 x 1.6 mm, 10 faces (baked)
FEATURE [Part::Feature] Part__Feature038  label="SC0951"
  shape: bbox 2.41 x 1 x 1.6 mm, 10 faces (baked)
FEATURE [Part::Feature] Part__Feature039  label="SC0952"
  shape: bbox 2.41 x 1 x 1.6 mm, 10 faces (baked)
FEATURE [Part::Feature] Part__Feature040  label="SC0953"
  shape: bbox 2.41 x 1 x 1.6 mm, 10 faces (baked)
FEATURE [Part::Feature] Part__Feature041  label="SC0954"
  shape: bbox 2.41 x 1 x 1.6 mm, 10 faces (baked)
FEATURE [Part::Feature] Part__Feature042  label="SC0955"
  shape: bbox 2.41 x 1 x 1.6 mm, 10 faces (baked)
FEATURE [Part::Feature] Part__Feature043  label="SC0956"
  shape: bbox 2.41 x 1 x 1.6 mm, 10 faces (baked)
FEATURE [Part::Feature] Part__Feature044  label="SC0957"
  shape: bbox 2.41 x 1 x 1.6 mm, 10 faces (baked)
FEATURE [Part::Feature] Part__Feature045  label="SC0958"
  shape: bbox 2.41 x 1 x 1.6 mm, 10 faces (baked)
FEATURE [Part::Feature] Part__Feature046  label="SC0959"
  shape: bbox 1.6 x 1 x 2.41 mm, 12 faces (baked)
FEATURE [Part::Feature] Part__Feature047  label="SC0960"
  shape: bbox 1.6 x 1 x 2.41 mm, 12 faces (baked)
FEATURE [Part::Feature] Part__Feature048  label="SC0961"
  shape: bbox 1.6 x 1 x 2.41 mm, 13 faces (baked)
FEATURE [Part::Feature] Part__Feature049  label="SC0962"
  shape: bbox 3.35 x 0.9 x 4.2 mm, 6 faces (baked)
FEATURE [Part::Feature] Part__Feature050  label="SC0963"
  shape: bbox 2.2 x 0.9 x 2.8 mm, 6 faces (baked)
FEATURE [Part::Feature] Part__Feature051  label="SC0964"
  shape: bbox 7 x 0.9 x 7 mm, 6 faces (baked)
FEATURE [Part::Feature] Part__Feature052  label="SC0965"
  shape: bbox 2.1 x 0.9 x 3 mm, 6 faces (baked)
FEATURE [Part::Feature] Part__Feature053  label="SC0966"
  shape: bbox 3 x 0.9 x 2.2 mm, 6 faces (baked)
FEATURE [Part::Feature] Part__Feature054  label="SC0967"
  shape: bbox 2.4 x 0.9 x 2.4 mm, 6 faces (baked)
FEATURE [Part::Feature] Part__Feature055  label="SC0968"
  shape: bbox 2.25 x 1.1 x 3.4 mm, 13 faces (baked)
FEATURE [Part::Feature] Part__Feature056  label="SC0969"
  shape: bbox 0.35 x 0.1 x 0.5 mm, 6 faces (baked)
FEATURE [Part::Feature] Part__Feature057  label="SC0970"
  shape: bbox 1.75 x 0.1 x 0.9 mm, 6 faces (baked)
FEATURE [Part::Feature] Part__Feature058  label="SC0971"
  shape: bbox 1.2 x 0.1 x 0.505 mm, 6 faces (baked)
FEATURE [Part::Feature] Part__Feature059  label="SC0972"
  shape: bbox 1.2 x 0.1 x 0.505 mm, 6 faces (baked)
FEATURE [Part::Feature] Part__Feature060  label="SC0973"
  shape: bbox 0.35 x 0.1 x 0.5 mm, 6 faces (baked)
FEATURE [Part::Feature] Part__Feature061  label="SC0974"
  shape: bbox 0.35 x 0.1 x 0.5 mm, 6 faces (baked)
FEATURE [Part::Feature] Part__Feature062  label="SC0975"
  shape: bbox 1.2 x 1.25 x 1.2 mm, 6 faces (baked)
FEATURE [Part::Feature] Part__Feature063  label="SC0976"
  shape: bbox 2 x 1.25 x 1 mm, 6 faces (baked)
FEATURE [Part::Feature] Part__Feature064  label="SC0977"
  shape: bbox 1.2 x 1.25 x 1.2 mm, 6 faces (baked)
FEATURE [Part::Feature] Part__Feature065  label="SC0978"
  shape: bbox 0.4 x 1.25 x 1.2 mm, 6 faces (baked)
FEATURE [Part::Feature] Part__Feature066  label="SC0979"
  shape: bbox 2 x 1.25 x 0.7 mm, 6 faces (baked)
FEATURE [Part::Feature] Part__Feature067  label="SC0980"
  shape: bbox 0.4 x 1.25 x 1.2 mm, 6 faces (baked)
FEATURE [Part::Feature] Part__Feature068  label="SC0981"
  shape: bbox 0.4 x 1.25 x 1.2 mm, 6 faces (baked)
FEATURE [Part::Feature] Part__Feature069  label="SC0982"
  shape: bbox 0.4 x 1.25 x 1.2 mm, 6 faces (baked)
FEATURE [Part::Feature] Part__Feature070  label="SC0983"
  shape: bbox 2 x 1.25 x 0.7 mm, 6 faces (baked)
FEATURE [Part::Feature] Part__Feature071  label="SC0984"
  shape: bbox 0.9 x 0.2 x 0.9 mm, 6 faces (baked)
FEATURE [Part::Feature] Part__Feature072  label="SC0985"
  shape: bbox 1.95 x 0.85 x 1 mm, 6 faces (baked)
FEATURE [Part::Feature] Part__Feature073  label="SC0986"
  shape: bbox 0.42 x 0.15 x 2.3 mm, 6 faces (baked)
FEATURE [Part::Feature] Part__Feature074  label="SC0987"
  shape: bbox 0.42 x 0.15 x 2.3 mm, 6 faces (baked)
FEATURE [Part::Feature] Part__Feature075  label="SC0988"
  shape: bbox 0.42 x 0.15 x 2.3 mm, 6 faces (baked)
FEATURE [Part::Feature] Part__Feature076  label="SC0989"
  shape: bbox 0.42 x 0.15 x 2.3 mm, 6 faces (baked)
FEATURE [Part::Feature] Part__Feature077  label="SC0990"
  shape: bbox 0.42 x 0.15 x 2.3 mm, 6 faces (baked)
FEATURE [Part::Feature] Part__Feature078  label="SC0991"
  shape: bbox 7.1 x 2.52 x 4.21 mm, 184 faces (baked)
FEATURE [Part::Feature] Part__Feature079  label="SC0992"
  shape: bbox 8 x 3.48 x 5.5 mm, 288 faces (baked)
FEATURE [Part::Feature] Part__Feature080  label="SC0993"
  shape: bbox 0.25 x 0.25 x 0.7 mm, 14 faces (baked)
FEATURE [Part::Feature] Part__Feature081  label="SC0994"
  shape: bbox 0.25 x 0.25 x 0.7 mm, 14 faces (baked)
FEATURE [Part::Feature] Part__Feature082  label="SC0995"
  shape: bbox 0.25 x 0.25 x 0.7 mm, 14 faces (baked)
FEATURE [Part::Feature] Part__Feature083  label="SC0996"
  shape: bbox 0.25 x 0.25 x 0.7 mm, 14 faces (baked)
FEATURE [Part::Feature] Part__Feature084  label="SC0997"
  shape: bbox 0.25 x 0.25 x 0.7 mm, 14 faces (baked)
FEATURE [Part::Feature] Part__Feature085  label="SC0998"
  shape: bbox 1.5 x 0.1 x 1.5 mm, 10 faces (baked)
FEATURE [Part::Feature] Part__Feature086  label="SC0999"
  shape: bbox 1.5 x 0.1 x 1.5 mm, 10 faces (baked)
FEATURE [Part::Feature] Part__Feature087  label="SC1000"
  shape: bbox 1.5 x 0.1 x 1.5 mm, 10 faces (baked)
FEATURE [Part::Feature] Part__Feature088  label="SC1001"
  shape: bbox 1.5 x 0.1 x 1.5 mm, 10 faces (baked)
FEATURE [Part::Feature] Part__Feature089  label="SC1002"
  shape: bbox 1.5 x 0.1 x 1.5 mm, 10 faces (baked)
FEATURE [Part::Feature] Part__Feature090  label="SC1003"
  shape: bbox 1.5 x 0.1 x 1.5 mm, 10 faces (baked)
FEATURE [Part::Feature] Part__Feature091  label="SC1004"
  shape: bbox 21 x 1 x 51 mm, 284 faces (baked)
FEATURE [Part::Feature] Part__Feature092  label="SC1005"
  shape: bbox 1.1 x 0.1 x 1.8 mm, 7 faces (baked)
FEATURE [Part::Feature] Part__Feature093  label="SC1006"
  shape: bbox 1.1 x 0.1 x 1.8 mm, 7 faces (baked)
FEATURE [Part::Feature] Part__Feature094  label="SC1007"
  shape: bbox 1.05 x 0.1 x 1.45 mm, 7 faces (baked)
FEATURE [Part::Feature] Part__Feature095  label="SC1008"
  shape: bbox 1.05 x 0.1 x 1.45 mm, 7 faces (baked)
FEATURE [Part::Feature] Pcb_51fb
  Placement = pos=(-18.5,81.5285,0) rot=(0,0,1;0rad)
  shape: bbox 165 x 72.5 x 1.592 mm, 116 faces (baked)
FEATURE [App::Part] Board_Geoms_51fb
  Group = -> [Pcb_51fb,PCB_Sketch_51fb]
  Origin = -> Origin048
FEATURE [App::Link] Q2_SOT_23_c919c89d7c35_ln_  label="Q1_SOT_23_a02c5a9bee34"
  LinkPlacement = pos=(74.8,37,0) rot=(0,0,1;3.14159rad)
  LinkedObject = -> Shape008
  Placement = pos=(74.8,37,0) rot=(0,0,1;3.14159rad)
FEATURE [App::Link] R10_R_0805_2012Metric_7538cc60fda0_ln_  label="R3_R_0805_2012Metric_139ca9693518"
  LinkPlacement = pos=(26.5,11.2,0) rot=(0,0,1;3.14159rad)
  LinkedObject = -> Shape092
  Placement = pos=(26.5,11.2,0) rot=(0,0,1;3.14159rad)
FEATURE [App::Link] R10_R_0805_2012Metric_7538cc60fda0_ln_001  label="R7_R_0805_2012Metric_413e6529ed4a"
  LinkPlacement = pos=(14.5,17.9,0) rot=(0,0,1;3.14159rad)
  LinkedObject = -> Shape092
  Placement = pos=(14.5,17.9,0) rot=(0,0,1;3.14159rad)
FEATURE [App::Link] R10_R_0805_2012Metric_7538cc60fda0_ln_002  label="R1_R_0805_2012Metric_e9d7ee01f872"
  LinkPlacement = pos=(24.8,20.9,0) rot=(0,0,1;3.14159rad)
  LinkedObject = -> Shape092
  Placement = pos=(24.8,20.9,0) rot=(0,0,1;3.14159rad)
FEATURE [App::Link] R10_R_0805_2012Metric_7538cc60fda0_ln_003  label="R15_R_0805_2012Metric_28d6e0cd51a2"
  LinkPlacement = pos=(80.5,32.7,0) rot=(0,0,1;3.14159rad)
  LinkedObject = -> Shape092
  Placement = pos=(80.5,32.7,0) rot=(0,0,1;3.14159rad)
FEATURE [App::Link] R10_R_0805_2012Metric_7538cc60fda0_ln_004  label="R11_R_0805_2012Metric_f8762678d082"
  LinkPlacement = pos=(14.5,20,0) rot=(0,0,1;3.14159rad)
  LinkedObject = -> Shape092
  Placement = pos=(14.5,20,0) rot=(0,0,1;3.14159rad)
FEATURE [App::Link] R10_R_0805_2012Metric_7538cc60fda0_ln_005  label="R13_R_0805_2012Metric_bb24aad5734d"
  LinkPlacement = pos=(29.6,19.1,0) rot=(0,0,-1;1.5708rad)
  LinkedObject = -> Shape092
  Placement = pos=(29.6,19.1,0) rot=(0,0,-1;1.5708rad)
FEATURE [App::Link] R10_R_0805_2012Metric_7538cc60fda0_ln_006  label="R20_R_0805_2012Metric_ea6fdd8e8746"
  LinkPlacement = pos=(72.8,33.8,0) rot=(0,0,1;0rad)
  LinkedObject = -> Shape092
  Placement = pos=(72.8,33.8,0) rot=(0,0,1;0rad)
FEATURE [App::Link] R10_R_0805_2012Metric_7538cc60fda0_ln_007  label="R8_R_0805_2012Metric_480b88d35bee"
  LinkPlacement = pos=(7.00002,16.7,0) rot=(0,0,1;3.14159rad)
  LinkedObject = -> Shape092
  Placement = pos=(7.00002,16.7,0) rot=(0,0,1;3.14159rad)
FEATURE [App::Link] R10_R_0805_2012Metric_7538cc60fda0_ln_008  label="R6_R_0805_2012Metric_ed46adc45477"
  LinkPlacement = pos=(10.7,26.4,0) rot=(0,0,1;3.14159rad)
  LinkedObject = -> Shape092
  Placement = pos=(10.7,26.4,0) rot=(0,0,1;3.14159rad)
FEATURE [App::Link] R10_R_0805_2012Metric_7538cc60fda0_ln_009  label="R18_R_0805_2012Metric_272588301ff9"
  LinkPlacement = pos=(43.8,3.40002,0) rot=(0,0,1;0rad)
  LinkedObject = -> Shape092
  Placement = pos=(43.8,3.40002,0) rot=(0,0,1;0rad)
FEATURE [App::Link] R10_R_0805_2012Metric_7538cc60fda0_ln_010  label="R9_R_0805_2012Metric_c71733df7f9f"
  LinkPlacement = pos=(3.10002,16.7,0) rot=(0,0,1;0rad)
  LinkedObject = -> Shape092
  Placement = pos=(3.10002,16.7,0) rot=(0,0,1;0rad)
FEATURE [App::Link] R10_R_0805_2012Metric_7538cc60fda0_ln_011  label="R2_R_0805_2012Metric_0dd0370ec1da"
  LinkPlacement = pos=(29.6,14.6285,0) rot=(0,0,-1;1.5708rad)
  LinkedObject = -> Shape092
  Placement = pos=(29.6,14.6285,0) rot=(0,0,-1;1.5708rad)
FEATURE [App::Link] R10_R_0805_2012Metric_7538cc60fda0_ln_012  label="R4_R_0805_2012Metric_84be3173d965"
  LinkPlacement = pos=(20.9625,43.64,0) rot=(0,0,1;3.14159rad)
  LinkedObject = -> Shape092
  Placement = pos=(20.9625,43.64,0) rot=(0,0,1;3.14159rad)
FEATURE [App::Link] R10_R_0805_2012Metric_7538cc60fda0_ln_013  label="R16_R_0805_2012Metric_d9bee0a38b66"
  LinkPlacement = pos=(80.6,38,0) rot=(0,0,1;3.14159rad)
  LinkedObject = -> Shape092
  Placement = pos=(80.6,38,0) rot=(0,0,1;3.14159rad)
FEATURE [App::Link] R10_R_0805_2012Metric_7538cc60fda0_ln_014  label="R12_R_0805_2012Metric_a6c8c79ee0cd"
  LinkPlacement = pos=(31.7,15.8285,0) rot=(0,0,1;1.5708rad)
  LinkedObject = -> Shape092
  Placement = pos=(31.7,15.8285,0) rot=(0,0,1;1.5708rad)
FEATURE [App::Link] R10_R_0805_2012Metric_7538cc60fda0_ln_015  label="R21_R_0805_2012Metric_fd329559c189"
  LinkPlacement = pos=(154.3,15.5,0) rot=(0,0,-1;1.5708rad)
  LinkedObject = -> Shape092
  Placement = pos=(154.3,15.5,0) rot=(0,0,-1;1.5708rad)
FEATURE [App::Link] R10_R_0805_2012Metric_7538cc60fda0_ln_016  label="R5_R_0805_2012Metric_3d5ced576c1b"
  LinkPlacement = pos=(24,9.20002,0) rot=(0,0,1;0rad)
  LinkedObject = -> Shape092
  Placement = pos=(24,9.20002,0) rot=(0,0,1;0rad)
FEATURE [App::Link] R10_R_0805_2012Metric_7538cc60fda0_ln_017  label="R14_R_0805_2012Metric_33922ef02622"
  LinkPlacement = pos=(46.8,49.8,0) rot=(0,0,1;3.14159rad)
  LinkedObject = -> Shape092
  Placement = pos=(46.8,49.8,0) rot=(0,0,1;3.14159rad)
FEATURE [App::Link] R10_R_0805_2012Metric_7538cc60fda0_ln_018  label="R19_R_0805_2012Metric_b54dcca9e39f"
  LinkPlacement = pos=(71,37.5,0) rot=(0,0,1;0rad)
  LinkedObject = -> Shape092
  Placement = pos=(71,37.5,0) rot=(0,0,1;0rad)
FEATURE [App::Link] R10_R_0805_2012Metric_7538cc60fda0_ln_019  label="R17_R_0805_2012Metric_596a6c57280b"
  LinkPlacement = pos=(154.3,11.8,0) rot=(0,0,-1;1.5708rad)
  LinkedObject = -> Shape092
  Placement = pos=(154.3,11.8,0) rot=(0,0,-1;1.5708rad)
FEATURE [App::Part] SC0915  label="U8_SC1009_bf1f1e83e549"
  Group = -> [Part__Feature235,Part__Feature236,Part__Feature237,Part__Feature238,Part__Feature239,Part__Feature240,Part__Feature241,Part__Feature242,Part__Feature010,Part__Feature011,Part__Feature012,Part__Feature013,Part__Feature014,Part__Feature015,Part__Feature016,Part__Feature243,Part__Feature244,Part__Feature245,Part__Feature246,Part__Feature247,Part__Feature248,Part__Feature249,Part__Feature250,+71 more]
  Origin = -> Origin009
  Placement = pos=(125.8,21.61,0) rot=(0.57735,0.57735,0.57735;2.0944rad)
FEATURE [Part::Feature] Shape087  label="C6_CP_Elec_63x58_0ee41fe4bfd3"
  Placement = pos=(62,32.1,0) rot=(0,0,1;1.5708rad)
  shape: bbox 8.603 x 8.606 x 5.8 mm, 41 faces (baked)
FEATURE [Part::Feature] Shape088  label="C22_C_0805_2012Metric_c419cd9c4a2f"
  Placement = pos=(64.6,43.8,0) rot=(0,0,-1;1.5708rad)
  shape: bbox 1.25 x 2 x 1.25 mm, 28 faces (baked)
FEATURE [Part::Feature] Shape089  label="D1_D_SOD_123_5a20a041a245"
  Placement = pos=(48.6,22.5,0) rot=(0,0,1;3.14159rad)
  shape: bbox 3.8 x 1.6 x 1.25 mm, 67 faces (baked)
FEATURE [Part::Feature] Shape090  label="J2_TerminalBlock_Phoenix_PT_15_2_50_H_1x02_P500mm_Horizontal_57983e5edded001"
  Placement = pos=(3,45.6,0) rot=(0,0,-1;1.5708rad)
  shape: bbox 9 x 10.57 x 15 mm, 126 faces (baked)
FEATURE [Part::Feature] Shape091  label="J3_PinSocket_1x11_P254mm_Vertical_b0b4de05439f"
  Placement = pos=(150.3,2.9,0) rot=(0,0,-1;1.5708rad)
  shape: bbox 27.94 x 2.54 x 10.1 mm, 351 faces (baked)
FEATURE [Part::Feature] Shape092  label="R10_R_0805_2012Metric_7538cc60fda0"
  Placement = pos=(14.5,22.1,0) rot=(0,0,1;0rad)
  shape: bbox 2 x 1.2 x 0.45 mm, 26 faces (baked)
FEATURE [Part::Feature] Shape093  label="M2_Fan_Pin_Header_Straight_1x04_4971bfcbb112"
  Placement = pos=(5.96002,12.0285,0) rot=(0,0,1;0rad)
  shape: bbox 10.2 x 5.84 x 13.5 mm, 99 faces (baked)
FEATURE [Part::Feature] Shape007  label="U6_SOIC_28W_75x179mm_P127mm_746d43082d9a"
  Placement = pos=(83.5,16,0) rot=(0,0,-1;1.5708rad)
  shape: bbox 17.9 x 10.3 x 2.75 mm, 456 faces (baked)
FEATURE [Part::Feature] Shape008  label="Q2_SOT_23_c919c89d7c35"
  Placement = pos=(76.8,32,0) rot=(0,0,1;3.14159rad)
  shape: bbox 2.5 x 3 x 1.2 mm, 76 faces (baked)
FEATURE [Part::Feature] Shape009  label="JP8_PinHeader_1x02_P254mm_Vertical_ed570ec3ee34"
  Placement = pos=(30.5,43.84,0) rot=(0,0,1;0rad)
  shape: bbox 2.54 x 5.08 x 11.54 mm, 52 faces (baked)
FEATURE [Part::Feature] Shape010  label="D6_LED_0805_2012Metric_630bc1ac9416"
  Placement = pos=(24.5625,43.64,0) rot=(0,0,1;0rad)
  shape: bbox 2 x 1.25 x 1.1 mm, 50 faces (baked)
FEATURE [Part::Feature] Shape011  label="U3_QSOP_16_39x49mm_P0635mm_7381d1256304"
  Placement = pos=(9.70002,21.6,0) rot=(0,0,1;1.5708rad)
  shape: bbox 4.9 x 6 x 1.42 mm, 260 faces (baked)
FEATURE [Part::Feature] Shape012  label="J1_MCV_01x02_G_3_81mm_8d2d7ae2d0cf001"
  Placement = pos=(3.7,30.5,0) rot=(0,0,1;1.5708rad)
  shape: bbox 7.55 x 9.01 x 12.6 mm, 76 faces (baked)
FEATURE [Part::Feature] Shape013  label="L2_L_1210_3225Metric_8f5c69fc0355"
  Placement = pos=(52.4,46,0) rot=(0,0,1;3.14159rad)
  shape: bbox 3.2 x 2.5 x 2.5 mm, 28 faces (baked)
FEATURE [Part::Feature] Shape014  label="D15_D_MiniMELF_Standard_ca1fadf4eb28"
  Placement = pos=(57.8,46.4,0) rot=(0,0,1;0rad)
  shape: bbox 3.6 x 1.4 x 1.4 mm, 13 faces (baked)
FEATURE [Part::Feature] Shape015  label="J9_PinHeader_1x06_P254mm_Vertical_f561237d0f53"
  Placement = pos=(137.72,38.7,0) rot=(0,0,1;1.5708rad)
  shape: bbox 15.24 x 2.54 x 11.54 mm, 148 faces (baked)
FEATURE [Part::Feature] Shape016  label="J8_PinHeader_2x08_P254mm_Vertical_411dce5b0f098"
  Placement = pos=(118.075,4.875,0) rot=(0,0,-1;1.5708rad)
  shape: bbox 20.32 x 5.08 x 11.54 mm, 340 faces (baked)
FEATURE [Part::Feature] Shape017  label="J10_JST_B2B_XH_A_3a5731dab8f004"
  Placement = pos=(92.65,48.725,0) rot=(0,0,1;0rad)
  shape: bbox 7.4 x 5.75 x 10.4 mm, 89 faces (baked)
FEATURE [Part::Feature] Shape018  label="D11_D_SMA_1bb42aa92948"
  Placement = pos=(21.6,-1.29998,0) rot=(0,0,1;3.14159rad)
  shape: bbox 5 x 2.7 x 2.22 mm, 41 faces (baked)
FEATURE [Part::Feature] Shape019  label="U7_SOT_223_9813f15a1230"
  Placement = pos=(69.4,46,0) rot=(0,0,-1;1.5708rad)
  shape: bbox 6.5 x 7 x 1.7 mm, 78 faces (baked)
FEATURE [Part::Feature] Shape094  label="U2_SOT_23_6_80ad3168e82c"
  Placement = pos=(24.13,30.2,0) rot=(0,0,1;3.14159rad)
  shape: bbox 2.8 x 2.9 x 1.55 mm, 124 faces (baked)
FEATURE [Part::Feature] Shape021  label="J11_IDC_Header_2x08_P254mm_Vertical_e1f45a9088de"
  Placement = pos=(162.1,27,0) rot=(0,0,1;3.14159rad)
  shape: bbox 9.1 x 27.98 x 12.1 mm, 330 faces (baked)
FEATURE [Part::Feature] Shape022  label="U11_SOIC_8_39x49mm_P127mm_867d4187783b"
  Placement = pos=(108.665,42.85,0) rot=(0,0,1;0rad)
  shape: bbox 6 x 4.9 x 1.75 mm, 156 faces (baked)
FEATURE [Part::Feature] Shape023  label="J7_PinSocket_2x08_P254mm_Vertical_a805aa90854e"
  Placement = pos=(57.075,-11.01,-1.592) rot=(0.707107,0.707107,0;3.14159rad)
  shape: bbox 20.32 x 5.08 x 10.1 mm, 506 faces (baked)
FEATURE [App::Part] Bot_51fb
  Group = -> [Shape023]
  Origin = -> Origin052
FEATURE [App::Link] TP4_TestPoint_Loop_D2_54mm_Drill1_5mm_Beaded_cp002_8f60d36f4fd8_ln_  label="TP5_TestPoint_Loop_D2_54mm_Drill1_5mm_Beaded_cp002_0b7b98566b58"
  LinkPlacement = pos=(42.1,-1.8,0) rot=(0,0,1;0rad)
  LinkedObject = -> TestPoint_Loop_D2_54mm_Drill1_5mm_Beaded_cp
  Placement = pos=(42.1,-1.8,0) rot=(0,0,1;0rad)
FEATURE [App::Link] TP4_TestPoint_Loop_D2_54mm_Drill1_5mm_Beaded_cp002_8f60d36f4fd8_ln_001  label="TP1_TestPoint_Loop_D2_54mm_Drill1_5mm_Beaded_cp002_9e1e075e0d1f"
  LinkPlacement = pos=(42.6,49.1,0) rot=(0,0,1;0rad)
  LinkedObject = -> TestPoint_Loop_D2_54mm_Drill1_5mm_Beaded_cp
  Placement = pos=(42.6,49.1,0) rot=(0,0,1;0rad)
FEATURE [App::Link] TP4_TestPoint_Loop_D2_54mm_Drill1_5mm_Beaded_cp002_8f60d36f4fd8_ln_002  label="TP2_TestPoint_Loop_D2_54mm_Drill1_5mm_Beaded_cp002_4444e0770bde"
  LinkPlacement = pos=(43.2,14.6,0) rot=(0,0,1;0rad)
  LinkedObject = -> TestPoint_Loop_D2_54mm_Drill1_5mm_Beaded_cp
  Placement = pos=(43.2,14.6,0) rot=(0,0,1;0rad)
FEATURE [App::Part] TestPoint_Loop_D2_54mm_Drill1_5mm_Beaded_cp  label="TP4_TestPoint_Loop_D2_54mm_Drill1_5mm_Beaded_cp002_8f60d36f4fd8"
  Group = -> [Part__Feature233,Part__Feature234]
  Origin = -> Origin053
  Placement = pos=(58.5,14,0) rot=(0,0,1;0rad)
FEATURE [App::Link] U11_SOIC_8_39x49mm_P127mm_867d4187783b_ln_  label="U4_SOIC_8_39x49mm_P127mm_4428ff659321"
  LinkPlacement = pos=(36.475,17.4235,0) rot=(0,0,1;3.14159rad)
  LinkedObject = -> Shape022
  Placement = pos=(36.475,17.4235,0) rot=(0,0,1;3.14159rad)
FEATURE [App::Link] U3_QSOP_16_39x49mm_P0635mm_7381d1256304_ln_  label="U1_QSOP_16_39x49mm_P0635mm_61417655afff"
  LinkPlacement = pos=(25.6,16,0) rot=(0,0,1;1.5708rad)
  LinkedObject = -> Shape011
  Placement = pos=(25.6,16,0) rot=(0,0,1;1.5708rad)
FEATURE [App::Link] U7_SOT_223_9813f15a1230_ln_  label="U9_SOT_223_6d2a4fb53031"
  LinkPlacement = pos=(82.05,46.05,0) rot=(0,0,-1;1.5708rad)
  LinkedObject = -> Shape019
  Placement = pos=(82.05,46.05,0) rot=(0,0,-1;1.5708rad)
FEATURE [App::Link] U7_SOT_223_9813f15a1230_ln_001  label="U5_SOT_223_0a21e31ed99f"
  LinkPlacement = pos=(22.7,49.49,0) rot=(0,0,1;1.5708rad)
  LinkedObject = -> Shape019
  Placement = pos=(22.7,49.49,0) rot=(0,0,1;1.5708rad)
FEATURE [App::Part] Top_51fb
  Group = -> [Shape087,Shape088,Shape089,C22_C_0805_2012Metric_c419cd9c4a2f_ln_,D1_D_SOD_123_5a20a041a245_ln_,Shape090,C22_C_0805_2012Metric_c419cd9c4a2f_ln_001,C22_C_0805_2012Metric_c419cd9c4a2f_ln_002,Shape091,TestPoint_Loop_D2_54mm_Drill1_5mm_Beaded_cp,Shape092,C22_C_0805_2012Metric_c419cd9c4a2f_ln_003,Shape093,M2_Fan_Pin_Header_Straight_1x04_4971bfcbb112_ln_,SC0915,C6_CP_Elec_63x58_0ee41fe4bfd3_ln_,+82 more]
  Origin = -> Origin051
FEATURE [App::Part] Step_Models_51fb
  Group = -> [Top_51fb,Bot_51fb]
  Origin = -> Origin050
FEATURE [App::Part] Board_51fb  label="EL-Load-PowerTest2"
  Group = -> [Local_CS_51fb,Board_Geoms_51fb,Step_Models_51fb]
  Origin = -> Origin049
  Placement = pos=(191.67,76.67,12) rot=(0,0,1;3.14159rad)
FEATURE [App::Link] C22_C_0805_2012Metric_c419cd9c4a2f_ln_042  label="C11_C_0805_2012Metric_a49b18341ced002"
  LinkPlacement = pos=(30.4,11.2,0) rot=(0,0,1;0rad)
  LinkedObject = -> Shape096
  Placement = pos=(30.4,11.2,0) rot=(0,0,1;0rad)
FEATURE [App::Link] C22_C_0805_2012Metric_c419cd9c4a2f_ln_043  label="C26_C_0805_2012Metric_9980a3fec6f002"
  LinkPlacement = pos=(17.9,47.79,0) rot=(0,0,1;1.5708rad)
  LinkedObject = -> Shape096
  Placement = pos=(17.9,47.79,0) rot=(0,0,1;1.5708rad)
FEATURE [App::Link] C22_C_0805_2012Metric_c419cd9c4a2f_ln_044  label="C3_C_0805_2012Metric_15e1a894cb003"
  LinkPlacement = pos=(48,32.7,0) rot=(0,0,1;3.14159rad)
  LinkedObject = -> Shape096
  Placement = pos=(48,32.7,0) rot=(0,0,1;3.14159rad)
FEATURE [App::Link] C22_C_0805_2012Metric_c419cd9c4a2f_ln_045  label="C18_C_0805_2012Metric_e794a3d39e082"
  LinkPlacement = pos=(27.6,47.69,0) rot=(0,0,-1;1.5708rad)
  LinkedObject = -> Shape096
  Placement = pos=(27.6,47.69,0) rot=(0,0,-1;1.5708rad)
FEATURE [App::Link] C22_C_0805_2012Metric_c419cd9c4a2f_ln_046  label="C24_C_0805_2012Metric_f01b138523b004"
  LinkPlacement = pos=(77.05,43.95,0) rot=(0,0,-1;1.5708rad)
  LinkedObject = -> Shape096
  Placement = pos=(77.05,43.95,0) rot=(0,0,-1;1.5708rad)
FEATURE [App::Link] C22_C_0805_2012Metric_c419cd9c4a2f_ln_047  label="C9_C_0805_2012Metric_e36e869397a002"
  LinkPlacement = pos=(113.565,44.65,0) rot=(0,0,-1;1.5708rad)
  LinkedObject = -> Shape096
  Placement = pos=(113.565,44.65,0) rot=(0,0,-1;1.5708rad)
FEATURE [App::Link] C22_C_0805_2012Metric_c419cd9c4a2f_ln_048  label="C5_C_0805_2012Metric_15d6734f493a002"
  LinkPlacement = pos=(80.8,23.3,0) rot=(0,0,1;0rad)
  LinkedObject = -> Shape096
  Placement = pos=(80.8,23.3,0) rot=(0,0,1;0rad)
FEATURE [App::Link] C22_C_0805_2012Metric_c419cd9c4a2f_ln_049  label="C23_C_0805_2012Metric_11de36914b064"
  LinkPlacement = pos=(76.35,49.3,0) rot=(0,0,1;0rad)
  LinkedObject = -> Shape096
  Placement = pos=(76.35,49.3,0) rot=(0,0,1;0rad)
FEATURE [App::Link] C22_C_0805_2012Metric_c419cd9c4a2f_ln_050  label="C12_C_0805_2012Metric_732eebdf556d002"
  LinkPlacement = pos=(10.8,16.7,0) rot=(0,0,1;0rad)
  LinkedObject = -> Shape096
  Placement = pos=(10.8,16.7,0) rot=(0,0,1;0rad)
FEATURE [App::Link] C22_C_0805_2012Metric_c419cd9c4a2f_ln_051  label="C10_C_0805_2012Metric_be4c2624d97d002"
  LinkPlacement = pos=(5.70002,25.2,0) rot=(0,0,1;1.5708rad)
  LinkedObject = -> Shape096
  Placement = pos=(5.70002,25.2,0) rot=(0,0,1;1.5708rad)
FEATURE [App::Link] C22_C_0805_2012Metric_c419cd9c4a2f_ln_052  label="C15_C_0805_2012Metric_1e921fb38b4c002"
  LinkPlacement = pos=(14.4,24.2,0) rot=(0,0,1;0rad)
  LinkedObject = -> Shape096
  Placement = pos=(14.4,24.2,0) rot=(0,0,1;0rad)
FEATURE [App::Link] C22_C_0805_2012Metric_c419cd9c4a2f_ln_053  label="C2_C_0805_2012Metric_e26014cc501c002"
  LinkPlacement = pos=(47.9,27.7,0) rot=(0,0,1;3.14159rad)
  LinkedObject = -> Shape096
  Placement = pos=(47.9,27.7,0) rot=(0,0,1;3.14159rad)
FEATURE [App::Link] C22_C_0805_2012Metric_c419cd9c4a2f_ln_054  label="C21_C_0805_2012Metric_054ffed93a8c002"
  LinkPlacement = pos=(23.13,27.3,0) rot=(0,0,1;0rad)
  LinkedObject = -> Shape096
  Placement = pos=(23.13,27.3,0) rot=(0,0,1;0rad)
FEATURE [App::Link] C22_C_0805_2012Metric_c419cd9c4a2f_ln_055  label="C8_C_0805_2012Metric_242075c039d002"
  LinkPlacement = pos=(21.6,19.6,0) rot=(0,0,1;1.5708rad)
  LinkedObject = -> Shape096
  Placement = pos=(21.6,19.6,0) rot=(0,0,1;1.5708rad)
FEATURE [App::Link] C22_C_0805_2012Metric_c419cd9c4a2f_ln_056  label="C20_C_0805_2012Metric_a8166e63492a002"
  LinkPlacement = pos=(63.7,49.1,0) rot=(0,0,1;0rad)
  LinkedObject = -> Shape096
  Placement = pos=(63.7,49.1,0) rot=(0,0,1;0rad)
FEATURE [App::Link] C22_C_0805_2012Metric_c419cd9c4a2f_ln_057  label="C16_C_0805_2012Metric_4b5c9fa2ab9d002"
  LinkPlacement = pos=(33.7,12.7,0) rot=(0,0,1;1.5708rad)
  LinkedObject = -> Shape096
  Placement = pos=(33.7,12.7,0) rot=(0,0,1;1.5708rad)
FEATURE [App::Link] C22_C_0805_2012Metric_c419cd9c4a2f_ln_058  label="C17_C_0805_2012Metric_9c817947d75a002"
  LinkPlacement = pos=(39.2,12.7285,0) rot=(0,0,1;1.5708rad)
  LinkedObject = -> Shape096
  Placement = pos=(39.2,12.7285,0) rot=(0,0,1;1.5708rad)
FEATURE [App::Link] C6_CP_Elec_63x58_0ee41fe4bfd3_ln_014  label="C1_CP_Elec_63x58_5659c7eb80dd002"
  LinkPlacement = pos=(58.3,19.8,0) rot=(0,0,1;0rad)
  LinkedObject = -> Shape095
  Placement = pos=(58.3,19.8,0) rot=(0,0,1;0rad)
FEATURE [App::Link] C6_CP_Elec_63x58_0ee41fe4bfd3_ln_015  label="C13_CP_Elec_63x58_4c4f2b69c62b002"
  LinkPlacement = pos=(49.7,17.4,0) rot=(0,0,1;3.14159rad)
  LinkedObject = -> Shape095
  Placement = pos=(49.7,17.4,0) rot=(0,0,1;3.14159rad)
FEATURE [App::Link] C6_CP_Elec_63x58_0ee41fe4bfd3_ln_016  label="C30_CP_Elec_63x58_f829d7b62f1d002"
  LinkPlacement = pos=(53.4,10,0) rot=(0,0,1;3.14159rad)
  LinkedObject = -> Shape095
  Placement = pos=(53.4,10,0) rot=(0,0,1;3.14159rad)
FEATURE [App::Link] C6_CP_Elec_63x58_0ee41fe4bfd3_ln_017  label="C19_CP_Elec_63x58_eae7f9406b013"
  LinkPlacement = pos=(22.83,36.2,0) rot=(0,0,1;3.14159rad)
  LinkedObject = -> Shape095
  Placement = pos=(22.83,36.2,0) rot=(0,0,1;3.14159rad)
FEATURE [App::Link] C6_CP_Elec_63x58_0ee41fe4bfd3_ln_018  label="C14_CP_Elec_63x58_56145b951648"
  LinkPlacement = pos=(31.7,1.80002,0) rot=(0,0,1;1.5708rad)
  LinkedObject = -> Shape095
  Placement = pos=(31.7,1.80002,0) rot=(0,0,1;1.5708rad)
FEATURE [App::Link] C6_CP_Elec_63x58_0ee41fe4bfd3_ln_019  label="C4_CP_Elec_63x58_b0d551f2ee6d002"
  LinkPlacement = pos=(46.2,43,0) rot=(0,0,1;3.14159rad)
  LinkedObject = -> Shape095
  Placement = pos=(46.2,43,0) rot=(0,0,1;3.14159rad)
FEATURE [App::Link] C6_CP_Elec_63x58_0ee41fe4bfd3_ln_020  label="C7_CP_Elec_63x58_6e01dcfa2039"
  LinkPlacement = pos=(57.7,41.2,0) rot=(0,0,1;0rad)
  LinkedObject = -> Shape095
  Placement = pos=(57.7,41.2,0) rot=(0,0,1;0rad)
FEATURE [App::Link] D11_D_SMA_1bb42aa92948_ln_004  label="D10_D_SMA_c2646ced11f005"
  LinkPlacement = pos=(8.70002,-1.19998,0) rot=(0,0,1;3.14159rad)
  LinkedObject = -> Shape113
  Placement = pos=(8.70002,-1.19998,0) rot=(0,0,1;3.14159rad)
FEATURE [App::Link] D11_D_SMA_1bb42aa92948_ln_005  label="D5_D_SMA_dbb58a46da9a002"
  LinkPlacement = pos=(1.80002,10.7285,0) rot=(0,0,-1;1.5708rad)
  LinkedObject = -> Shape113
  Placement = pos=(1.80002,10.7285,0) rot=(0,0,-1;1.5708rad)
FEATURE [App::Link] D15_D_MiniMELF_Standard_ca1fadf4eb28_ln_004  label="D16_D_MiniMELF_Standard_49aaf989b644"
  LinkPlacement = pos=(64.4,23.5,0) rot=(0,0,-1;1.5708rad)
  LinkedObject = -> Shape109
  Placement = pos=(64.4,23.5,0) rot=(0,0,-1;1.5708rad)
FEATURE [App::Link] D15_D_MiniMELF_Standard_ca1fadf4eb28_ln_005  label="D14_D_MiniMELF_Standard_869c8d3e9315"
  LinkPlacement = pos=(45,7.60002,0) rot=(0,0,1;0rad)
  LinkedObject = -> Shape109
  Placement = pos=(45,7.60002,0) rot=(0,0,1;0rad)
FEATURE [App::Link] D1_D_SOD_123_5a20a041a245_ln_012  label="D2_D_SOD_123_9f952dc980be002"
  LinkPlacement = pos=(48.7,38,0) rot=(0,0,1;3.14159rad)
  LinkedObject = -> Shape097
  Placement = pos=(48.7,38,0) rot=(0,0,1;3.14159rad)
FEATURE [App::Link] D1_D_SOD_123_5a20a041a245_ln_013  label="D4_D_SOD_123_a08d4832a5ee002"
  LinkPlacement = pos=(52.3,27.7,0) rot=(0,0,1;3.14159rad)
  LinkedObject = -> Shape097
  Placement = pos=(52.3,27.7,0) rot=(0,0,1;3.14159rad)
FEATURE [App::Link] D1_D_SOD_123_5a20a041a245_ln_014  label="D3_D_SOD_123_c8b4b2da39fe002"
  LinkPlacement = pos=(48.6,30.2,0) rot=(0,0,1;3.14159rad)
  LinkedObject = -> Shape097
  Placement = pos=(48.6,30.2,0) rot=(0,0,1;3.14159rad)
FEATURE [App::Link] D1_D_SOD_123_5a20a041a245_ln_015  label="D8_D_SOD_123_5a5f85ca8e2f002"
  LinkPlacement = pos=(48.7,35.4,0) rot=(0,0,1;3.14159rad)
  LinkedObject = -> Shape097
  Placement = pos=(48.7,35.4,0) rot=(0,0,1;3.14159rad)
FEATURE [App::Link] D1_D_SOD_123_5a20a041a245_ln_016  label="D9_D_SOD_123_161a8bc13198"
  LinkPlacement = pos=(52.25,32.7,0) rot=(0,0,1;0rad)
  LinkedObject = -> Shape097
  Placement = pos=(52.25,32.7,0) rot=(0,0,1;0rad)
FEATURE [App::Link] D1_D_SOD_123_5a20a041a245_ln_017  label="D7_D_SOD_123_81fc6af181e011"
  LinkPlacement = pos=(48.6,25.1,0) rot=(0,0,1;3.14159rad)
  LinkedObject = -> Shape097
  Placement = pos=(48.6,25.1,0) rot=(0,0,1;3.14159rad)
FEATURE [App::Link] D6_LED_0805_2012Metric_630bc1ac9416_ln_004  label="D13_LED_0805_2012Metric_31b94944d83b002"
  LinkPlacement = pos=(40.2,3.4,0) rot=(0,0,1;3.14159rad)
  LinkedObject = -> Shape105
  Placement = pos=(40.2,3.4,0) rot=(0,0,1;3.14159rad)
FEATURE [App::Link] D6_LED_0805_2012Metric_630bc1ac9416_ln_005  label="D12_LED_0805_2012Metric_8e83bb0bb172"
  LinkPlacement = pos=(50.5,49.8,0) rot=(0,0,1;0rad)
  LinkedObject = -> Shape105
  Placement = pos=(50.5,49.8,0) rot=(0,0,1;0rad)
FEATURE [App::Link] JP8_PinHeader_1x02_P254mm_Vertical_ed570ec3ee34_ln_010  label="J5_PinHeader_1x02_P254mm_Vertical_3b80083b2132"
  LinkPlacement = pos=(20.1,10,0) rot=(0,0,-1;1.5708rad)
  LinkedObject = -> Shape104
  Placement = pos=(20.1,10,0) rot=(0,0,-1;1.5708rad)
FEATURE [App::Link] JP8_PinHeader_1x02_P254mm_Vertical_ed570ec3ee34_ln_011  label="J6_PinHeader_1x02_P254mm_Vertical_92a677824945"
  LinkPlacement = pos=(3.30002,19.9285,0) rot=(0,0,-1;1.5708rad)
  LinkedObject = -> Shape104
  Placement = pos=(3.30002,19.9285,0) rot=(0,0,-1;1.5708rad)
FEATURE [App::Link] JP8_PinHeader_1x02_P254mm_Vertical_ed570ec3ee34_ln_012  label="JP5_PinHeader_1x02_P254mm_Vertical_806d60fd696a002"
  LinkPlacement = pos=(67.7,25.2,0) rot=(0,0,1;0rad)
  LinkedObject = -> Shape104
  Placement = pos=(67.7,25.2,0) rot=(0,0,1;0rad)
FEATURE [App::Link] JP8_PinHeader_1x02_P254mm_Vertical_ed570ec3ee34_ln_013  label="JP6_PinHeader_1x02_P254mm_Vertical_0c23ef1a54e008"
  LinkPlacement = pos=(47.5,4.3,0) rot=(0,0,1;1.5708rad)
  LinkedObject = -> Shape104
  Placement = pos=(47.5,4.3,0) rot=(0,0,1;1.5708rad)
FEATURE [App::Link] JP8_PinHeader_1x02_P254mm_Vertical_ed570ec3ee34_ln_014  label="JP4_PinHeader_1x02_P254mm_Vertical_b2b0b4eb230f002"
  LinkPlacement = pos=(55.95,49.725,0) rot=(0,0,1;1.5708rad)
  LinkedObject = -> Shape104
  Placement = pos=(55.95,49.725,0) rot=(0,0,1;1.5708rad)
FEATURE [App::Link] L2_L_1210_3225Metric_8f5c69fc0355_ln_004  label="L8_L_1210_3225Metric_c8d3be7f3659"
  LinkPlacement = pos=(60.6,25.3,0) rot=(0,0,1;3.14159rad)
  LinkedObject = -> Shape108
  Placement = pos=(60.6,25.3,0) rot=(0,0,1;3.14159rad)
FEATURE [App::Link] L2_L_1210_3225Metric_8f5c69fc0355_ln_005  label="L3_L_1210_3225Metric_d7bc27af3adb002"
  LinkPlacement = pos=(46.8,11.3,0) rot=(0,0,1;1.5708rad)
  LinkedObject = -> Shape108
  Placement = pos=(46.8,11.3,0) rot=(0,0,1;1.5708rad)
FEATURE [PartDesign::CoordinateSystem] Local_CS_51fb002
  AttacherType = Attacher::AttachEngine3D
  AttachmentSupport = -> [X_Axis055]
  MapMode = 2
FEATURE [App::Link] M2_Fan_Pin_Header_Straight_1x04_4971bfcbb112_ln_004  label="M3_Fan_Pin_Header_Straight_1x04_d9628b9d4d018"
  LinkPlacement = pos=(5.92002,4.60002,0) rot=(0,0,1;0rad)
  LinkedObject = -> Shape101
  Placement = pos=(5.92002,4.60002,0) rot=(0,0,1;0rad)
FEATURE [App::Link] M2_Fan_Pin_Header_Straight_1x04_4971bfcbb112_ln_005  label="M1_Fan_Pin_Header_Straight_1x04_37f54f52d17d002"
  LinkPlacement = pos=(18.48,4.50002,0) rot=(0,0,1;0rad)
  LinkedObject = -> Shape101
  Placement = pos=(18.48,4.50002,0) rot=(0,0,1;0rad)
FEATURE [Sketcher::SketchObject] PCB_Sketch_51fb002
  ArcFitTolerance = 0
  FullyConstrained = false
  MakeInternals = false
  sketch-geometry (16):
    g0: LineSegment StartX=36.25 StartY=-13.5 StartZ=0 EndX=36.25 EndY=-7.99998 EndZ=0
    g1: LineSegment StartX=2e-05 StartY=-3.99998 StartZ=0 EndX=32.25 EndY=-3.99998 EndZ=0
    g2: LineSegment StartX=-3.99998 StartY=2.3e-05 StartZ=0 EndX=-3.99998 EndY=52 EndZ=0
    g3: LineSegment StartX=171 StartY=52 StartZ=0 EndX=171 EndY=2.3e-05 EndZ=0
    g4: LineSegment StartX=64 StartY=-3.99998 StartZ=0 EndX=167 EndY=-3.99998 EndZ=0
    g5: LineSegment StartX=60 StartY=-13.5 StartZ=0 EndX=60 EndY=-7.99998 EndZ=0
    g6: LineSegment StartX=39.25 StartY=-16.5 StartZ=0 EndX=57 EndY=-16.5 EndZ=0
    g7: LineSegment StartX=2e-05 StartY=56 StartZ=0 EndX=167 EndY=56 EndZ=0
    g8: ArcOfCircle CenterX=1.70117e-05 CenterY=52 CenterZ=0 NormalX=0 NormalY=0 NormalZ=-1 AngleXU=-7.47076e-07 Radius=4 StartAngle=0 EndAngle=1.5708
    g9: ArcOfCircle CenterX=57 CenterY=-13.5 CenterZ=0 NormalX=0 NormalY=0 NormalZ=-1 AngleXU=-3.14159 Radius=3 StartAngle=0 EndAngle=1.5708
    g10: ArcOfCircle CenterX=64 CenterY=-7.99995 CenterZ=0 NormalX=0 NormalY=0 NormalZ=-1 AngleXU=-5.86839e-06 Radius=3.99998 StartAngle=0 EndAngle=1.57081
    g11: ArcOfCircle CenterX=167 CenterY=6.78113e-05 CenterZ=0 NormalX=0 NormalY=0 NormalZ=-1 AngleXU=-3.14158 Radius=4.00004 StartAngle=0 EndAngle=1.57077
    g12: ArcOfCircle CenterX=39.25 CenterY=-13.5 CenterZ=0 NormalX=0 NormalY=0 NormalZ=-1 AngleXU=-1.5708 Radius=3 StartAngle=0 EndAngle=1.5708
    g13: ArcOfCircle CenterX=32.25 CenterY=-7.99995 CenterZ=0 NormalX=0 NormalY=0 NormalZ=-1 AngleXU=1.57079 Radius=3.99998 StartAngle=0 EndAngle=1.57081
    g14: ArcOfCircle CenterX=-5.92595e-08 CenterY=2.94074e-06 CenterZ=0 NormalX=0 NormalY=0 NormalZ=-1 AngleXU=-1.5708 Radius=3.99998 StartAngle=0 EndAngle=1.57081
    g15: ArcOfCircle CenterX=167 CenterY=52 CenterZ=0 NormalX=0 NormalY=0 NormalZ=-1 AngleXU=1.5708 Radius=4.00002 StartAngle=0 EndAngle=1.57079
  constraints (16):
    c: Coincident(g2,g14)
    c: Coincident(g2,g8)
    c: Coincident(g1,g14)
    c: Coincident(g7,g8)
    c: Coincident(g1,g13)
    c: Coincident(g0,g12)
    c: Coincident(g0,g13)
    c: Coincident(g6,g12)
    c: Coincident(g6,g9)
    c: Coincident(g5,g9)
    c: Coincident(g5,g10)
    c: Coincident(g4,g10)
    c: Coincident(g4,g11)
    c: Coincident(g7,g15)
    c: Coincident(g3,g11)
    c: Coincident(g3,g15)
FEATURE [Part::Feature] Part__Feature257  label="TestPoint_Loop_D2_54mm_Drill1_5mm_Beaded_cp004"
  shape: bbox 3 x 3 x 3 mm, 4 faces (baked)
FEATURE [Part::Feature] Part__Feature258  label="TestPoint_Loop_D2_54mm_Drill1_5mm_Beaded_cp005"
  shape: bbox 3.415 x 0.9501 x 9.255 mm, 7 faces (baked)
FEATURE [Part::Feature] Part__Feature259  label="SC1103"
  shape: bbox 3.8 x 1 x 3.8 mm, 6 faces (baked)
FEATURE [Part::Feature] Part__Feature260  label="SC1104"
  shape: bbox 3.8 x 1 x 3.8 mm, 6 faces (baked)
FEATURE [Part::Feature] Part__Feature261  label="SC1105"
  shape: bbox 3.8 x 1 x 3.8 mm, 6 faces (baked)
FEATURE [Part::Feature] Part__Feature262  label="SC1106"
  shape: bbox 3.8 x 1 x 3.8 mm, 6 faces (baked)
FEATURE [Part::Feature] Part__Feature263  label="SC1107"
  shape: bbox 2.41 x 1 x 1.6 mm, 10 faces (baked)
FEATURE [Part::Feature] Part__Feature264  label="SC1108"
  shape: bbox 2.41 x 1 x 1.6 mm, 10 faces (baked)
FEATURE [Part::Feature] Part__Feature265  label="SC1109"
  shape: bbox 2.41 x 1 x 1.6 mm, 10 faces (baked)
FEATURE [Part::Feature] Part__Feature266  label="SC1110"
  shape: bbox 2.41 x 1 x 1.6 mm, 10 faces (baked)
FEATURE [Part::Feature] Part__Feature267  label="SC1111"
  shape: bbox 2.41 x 1 x 1.6 mm, 10 faces (baked)
FEATURE [Part::Feature] Part__Feature268  label="SC1112"
  shape: bbox 2.41 x 1 x 1.6 mm, 10 faces (baked)
FEATURE [Part::Feature] Part__Feature269  label="SC1113"
  shape: bbox 2.41 x 1 x 1.6 mm, 10 faces (baked)
FEATURE [Part::Feature] Part__Feature270  label="SC1114"
  shape: bbox 2.41 x 1 x 1.6 mm, 10 faces (baked)
FEATURE [Part::Feature] Part__Feature271  label="SC1115"
  shape: bbox 2.41 x 1 x 1.6 mm, 10 faces (baked)
FEATURE [Part::Feature] Part__Feature272  label="SC1116"
  shape: bbox 2.41 x 1 x 1.6 mm, 10 faces (baked)
FEATURE [Part::Feature] Part__Feature273  label="SC1117"
  shape: bbox 2.41 x 1 x 1.6 mm, 10 faces (baked)
FEATURE [Part::Feature] Part__Feature274  label="SC1118"
  shape: bbox 2.41 x 1 x 1.6 mm, 10 faces (baked)
FEATURE [Part::Feature] Part__Feature275  label="SC1119"
  shape: bbox 2.41 x 1 x 1.6 mm, 10 faces (baked)
FEATURE [Part::Feature] Part__Feature276  label="SC1120"
  shape: bbox 2.41 x 1 x 1.6 mm, 10 faces (baked)
FEATURE [Part::Feature] Part__Feature277  label="SC1121"
  shape: bbox 2.41 x 1 x 1.6 mm, 10 faces (baked)
FEATURE [Part::Feature] Part__Feature278  label="SC1122"
  shape: bbox 2.41 x 1 x 1.6 mm, 10 faces (baked)
FEATURE [Part::Feature] Part__Feature279  label="SC1123"
  shape: bbox 2.41 x 1 x 1.6 mm, 12 faces (baked)
FEATURE [Part::Feature] Part__Feature280  label="SC1124"
  shape: bbox 2.41 x 1 x 1.6 mm, 12 faces (baked)
FEATURE [Part::Feature] Part__Feature281  label="SC1125"
  shape: bbox 2.41 x 1 x 1.6 mm, 12 faces (baked)
FEATURE [Part::Feature] Part__Feature282  label="SC1126"
  shape: bbox 2.41 x 1 x 1.6 mm, 12 faces (baked)
FEATURE [Part::Feature] Part__Feature283  label="SC1127"
  shape: bbox 2.41 x 1 x 1.6 mm, 12 faces (baked)
FEATURE [Part::Feature] Part__Feature284  label="SC1128"
  shape: bbox 2.41 x 1 x 1.6 mm, 12 faces (baked)
FEATURE [Part::Feature] Part__Feature285  label="SC1129"
  shape: bbox 2.41 x 1 x 1.6 mm, 12 faces (baked)
FEATURE [Part::Feature] Part__Feature286  label="SC1130"
  shape: bbox 2.41 x 1 x 1.6 mm, 12 faces (baked)
FEATURE [Part::Feature] Part__Feature287  label="SC1131"
  shape: bbox 2.41 x 1 x 1.6 mm, 10 faces (baked)
FEATURE [Part::Feature] Part__Feature288  label="SC1132"
  shape: bbox 2.41 x 1 x 1.6 mm, 10 faces (baked)
FEATURE [Part::Feature] Part__Feature289  label="SC1133"
  shape: bbox 2.41 x 1 x 1.6 mm, 10 faces (baked)
FEATURE [Part::Feature] Part__Feature290  label="SC1134"
  shape: bbox 2.41 x 1 x 1.6 mm, 10 faces (baked)
FEATURE [Part::Feature] Part__Feature291  label="SC1135"
  shape: bbox 2.41 x 1 x 1.6 mm, 10 faces (baked)
FEATURE [Part::Feature] Part__Feature292  label="SC1136"
  shape: bbox 2.41 x 1 x 1.6 mm, 10 faces (baked)
FEATURE [Part::Feature] Part__Feature293  label="SC1137"
  shape: bbox 2.41 x 1 x 1.6 mm, 10 faces (baked)
FEATURE [Part::Feature] Part__Feature294  label="SC1138"
  shape: bbox 2.41 x 1 x 1.6 mm, 10 faces (baked)
FEATURE [Part::Feature] Part__Feature295  label="SC1139"
  shape: bbox 2.41 x 1 x 1.6 mm, 10 faces (baked)
FEATURE [Part::Feature] Part__Feature296  label="SC1140"
  shape: bbox 2.41 x 1 x 1.6 mm, 10 faces (baked)
FEATURE [Part::Feature] Part__Feature297  label="SC1141"
  shape: bbox 2.41 x 1 x 1.6 mm, 10 faces (baked)
FEATURE [Part::Feature] Part__Feature298  label="SC1142"
  shape: bbox 2.41 x 1 x 1.6 mm, 10 faces (baked)
FEATURE [Part::Feature] Part__Feature299  label="SC1143"
  shape: bbox 2.41 x 1 x 1.6 mm, 10 faces (baked)
FEATURE [Part::Feature] Part__Feature300  label="SC1144"
  shape: bbox 2.41 x 1 x 1.6 mm, 10 faces (baked)
FEATURE [Part::Feature] Part__Feature301  label="SC1145"
  shape: bbox 2.41 x 1 x 1.6 mm, 10 faces (baked)
FEATURE [Part::Feature] Part__Feature302  label="SC1146"
  shape: bbox 2.41 x 1 x 1.6 mm, 10 faces (baked)
FEATURE [Part::Feature] Part__Feature303  label="SC1147"
  shape: bbox 1.6 x 1 x 2.41 mm, 12 faces (baked)
FEATURE [Part::Feature] Part__Feature304  label="SC1148"
  shape: bbox 1.6 x 1 x 2.41 mm, 12 faces (baked)
FEATURE [Part::Feature] Part__Feature305  label="SC1149"
  shape: bbox 1.6 x 1 x 2.41 mm, 13 faces (baked)
FEATURE [Part::Feature] Part__Feature306  label="SC1150"
  shape: bbox 3.35 x 0.9 x 4.2 mm, 6 faces (baked)
FEATURE [Part::Feature] Part__Feature307  label="SC1151"
  shape: bbox 2.2 x 0.9 x 2.8 mm, 6 faces (baked)
FEATURE [Part::Feature] Part__Feature308  label="SC1152"
  shape: bbox 7 x 0.9 x 7 mm, 6 faces (baked)
FEATURE [Part::Feature] Part__Feature309  label="SC1153"
  shape: bbox 2.1 x 0.9 x 3 mm, 6 faces (baked)
FEATURE [Part::Feature] Part__Feature310  label="SC1154"
  shape: bbox 3 x 0.9 x 2.2 mm, 6 faces (baked)
FEATURE [Part::Feature] Part__Feature311  label="SC1155"
  shape: bbox 2.4 x 0.9 x 2.4 mm, 6 faces (baked)
FEATURE [Part::Feature] Part__Feature312  label="SC1156"
  shape: bbox 2.25 x 1.1 x 3.4 mm, 13 faces (baked)
FEATURE [Part::Feature] Part__Feature313  label="SC1157"
  shape: bbox 0.35 x 0.1 x 0.5 mm, 6 faces (baked)
FEATURE [Part::Feature] Part__Feature314  label="SC1158"
  shape: bbox 1.75 x 0.1 x 0.9 mm, 6 faces (baked)
FEATURE [Part::Feature] Part__Feature315  label="SC1159"
  shape: bbox 1.2 x 0.1 x 0.505 mm, 6 faces (baked)
FEATURE [Part::Feature] Part__Feature316  label="SC1160"
  shape: bbox 1.2 x 0.1 x 0.505 mm, 6 faces (baked)
FEATURE [Part::Feature] Part__Feature317  label="SC1161"
  shape: bbox 0.35 x 0.1 x 0.5 mm, 6 faces (baked)
FEATURE [Part::Feature] Part__Feature318  label="SC1162"
  shape: bbox 0.35 x 0.1 x 0.5 mm, 6 faces (baked)
FEATURE [Part::Feature] Part__Feature319  label="SC1163"
  shape: bbox 1.2 x 1.25 x 1.2 mm, 6 faces (baked)
FEATURE [Part::Feature] Part__Feature320  label="SC1164"
  shape: bbox 2 x 1.25 x 1 mm, 6 faces (baked)
FEATURE [Part::Feature] Part__Feature321  label="SC1165"
  shape: bbox 1.2 x 1.25 x 1.2 mm, 6 faces (baked)
FEATURE [Part::Feature] Part__Feature322  label="SC1166"
  shape: bbox 0.4 x 1.25 x 1.2 mm, 6 faces (baked)
FEATURE [Part::Feature] Part__Feature323  label="SC1167"
  shape: bbox 2 x 1.25 x 0.7 mm, 6 faces (baked)
FEATURE [Part::Feature] Part__Feature324  label="SC1168"
  shape: bbox 0.4 x 1.25 x 1.2 mm, 6 faces (baked)
FEATURE [Part::Feature] Part__Feature325  label="SC1169"
  shape: bbox 0.4 x 1.25 x 1.2 mm, 6 faces (baked)
FEATURE [Part::Feature] Part__Feature326  label="SC1170"
  shape: bbox 0.4 x 1.25 x 1.2 mm, 6 faces (baked)
FEATURE [Part::Feature] Part__Feature327  label="SC1171"
  shape: bbox 2 x 1.25 x 0.7 mm, 6 faces (baked)
FEATURE [Part::Feature] Part__Feature328  label="SC1172"
  shape: bbox 0.9 x 0.2 x 0.9 mm, 6 faces (baked)
FEATURE [Part::Feature] Part__Feature329  label="SC1173"
  shape: bbox 1.95 x 0.85 x 1 mm, 6 faces (baked)
FEATURE [Part::Feature] Part__Feature330  label="SC1174"
  shape: bbox 0.42 x 0.15 x 2.3 mm, 6 faces (baked)
FEATURE [Part::Feature] Part__Feature331  label="SC1175"
  shape: bbox 0.42 x 0.15 x 2.3 mm, 6 faces (baked)
FEATURE [Part::Feature] Part__Feature332  label="SC1176"
  shape: bbox 0.42 x 0.15 x 2.3 mm, 6 faces (baked)
FEATURE [Part::Feature] Part__Feature333  label="SC1177"
  shape: bbox 0.42 x 0.15 x 2.3 mm, 6 faces (baked)
FEATURE [Part::Feature] Part__Feature334  label="SC1178"
  shape: bbox 0.42 x 0.15 x 2.3 mm, 6 faces (baked)
FEATURE [Part::Feature] Part__Feature335  label="SC1179"
  shape: bbox 7.1 x 2.52 x 4.21 mm, 184 faces (baked)
FEATURE [Part::Feature] Part__Feature336  label="SC1180"
  shape: bbox 8 x 3.48 x 5.5 mm, 288 faces (baked)
FEATURE [Part::Feature] Part__Feature337  label="SC1181"
  shape: bbox 0.25 x 0.25 x 0.7 mm, 14 faces (baked)
FEATURE [Part::Feature] Part__Feature338  label="SC1182"
  shape: bbox 0.25 x 0.25 x 0.7 mm, 14 faces (baked)
FEATURE [Part::Feature] Part__Feature339  label="SC1183"
  shape: bbox 0.25 x 0.25 x 0.7 mm, 14 faces (baked)
FEATURE [Part::Feature] Part__Feature340  label="SC1184"
  shape: bbox 0.25 x 0.25 x 0.7 mm, 14 faces (baked)
FEATURE [Part::Feature] Part__Feature341  label="SC1185"
  shape: bbox 0.25 x 0.25 x 0.7 mm, 14 faces (baked)
FEATURE [Part::Feature] Part__Feature342  label="SC1186"
  shape: bbox 1.5 x 0.1 x 1.5 mm, 10 faces (baked)
FEATURE [Part::Feature] Part__Feature343  label="SC1187"
  shape: bbox 1.5 x 0.1 x 1.5 mm, 10 faces (baked)
FEATURE [Part::Feature] Part__Feature344  label="SC1188"
  shape: bbox 1.5 x 0.1 x 1.5 mm, 10 faces (baked)
FEATURE [Part::Feature] Part__Feature345  label="SC1189"
  shape: bbox 1.5 x 0.1 x 1.5 mm, 10 faces (baked)
FEATURE [Part::Feature] Part__Feature346  label="SC1190"
  shape: bbox 1.5 x 0.1 x 1.5 mm, 10 faces (baked)
FEATURE [Part::Feature] Part__Feature347  label="SC1191"
  shape: bbox 1.5 x 0.1 x 1.5 mm, 10 faces (baked)
FEATURE [Part::Feature] Part__Feature348  label="SC1192"
  shape: bbox 21 x 1 x 51 mm, 284 faces (baked)
FEATURE [Part::Feature] Part__Feature349  label="SC1193"
  shape: bbox 1.1 x 0.1 x 1.8 mm, 7 faces (baked)
FEATURE [Part::Feature] Part__Feature350  label="SC1194"
  shape: bbox 1.1 x 0.1 x 1.8 mm, 7 faces (baked)
FEATURE [Part::Feature] Part__Feature351  label="SC1195"
  shape: bbox 1.05 x 0.1 x 1.45 mm, 7 faces (baked)
FEATURE [Part::Feature] Part__Feature352  label="SC1196"
  shape: bbox 1.05 x 0.1 x 1.45 mm, 7 faces (baked)
FEATURE [Part::Feature] Pcb_51fb002
  Placement = pos=(-18.5,81.5285,0) rot=(0,0,1;0rad)
  shape: bbox 175 x 72.5 x 1.592 mm, 124 faces (baked)
FEATURE [App::Part] Board_Geoms_51fb002  label="Board_Geoms_51fb004"
  Group = -> [Pcb_51fb002,PCB_Sketch_51fb002]
  Origin = -> Origin054
FEATURE [App::Link] Q2_SOT_23_c919c89d7c35_ln_001  label="Q1_SOT_23_a02c5a9bee035"
  LinkPlacement = pos=(74.8,37,0) rot=(0,0,1;3.14159rad)
  LinkedObject = -> Shape103
  Placement = pos=(74.8,37,0) rot=(0,0,1;3.14159rad)
FEATURE [App::Link] R10_R_0805_2012Metric_7538cc60fda0_ln_020  label="R3_R_0805_2012Metric_139ca9693520"
  LinkPlacement = pos=(26.5,11.2,0) rot=(0,0,1;3.14159rad)
  LinkedObject = -> Shape100
  Placement = pos=(26.5,11.2,0) rot=(0,0,1;3.14159rad)
FEATURE [App::Link] R10_R_0805_2012Metric_7538cc60fda0_ln_021  label="R7_R_0805_2012Metric_413e6529ed4a002"
  LinkPlacement = pos=(14.5,17.9,0) rot=(0,0,1;3.14159rad)
  LinkedObject = -> Shape100
  Placement = pos=(14.5,17.9,0) rot=(0,0,1;3.14159rad)
FEATURE [App::Link] R10_R_0805_2012Metric_7538cc60fda0_ln_022  label="R1_R_0805_2012Metric_e9d7ee01f874"
  LinkPlacement = pos=(24.8,20.9,0) rot=(0,0,1;3.14159rad)
  LinkedObject = -> Shape100
  Placement = pos=(24.8,20.9,0) rot=(0,0,1;3.14159rad)
FEATURE [App::Link] R10_R_0805_2012Metric_7538cc60fda0_ln_023  label="R15_R_0805_2012Metric_28d6e0cd51a004"
  LinkPlacement = pos=(80.5,32.7,0) rot=(0,0,1;3.14159rad)
  LinkedObject = -> Shape100
  Placement = pos=(80.5,32.7,0) rot=(0,0,1;3.14159rad)
FEATURE [App::Link] R10_R_0805_2012Metric_7538cc60fda0_ln_024  label="R11_R_0805_2012Metric_f8762678d084"
  LinkPlacement = pos=(14.5,20,0) rot=(0,0,1;3.14159rad)
  LinkedObject = -> Shape100
  Placement = pos=(14.5,20,0) rot=(0,0,1;3.14159rad)
FEATURE [App::Link] R10_R_0805_2012Metric_7538cc60fda0_ln_025  label="R13_R_0805_2012Metric_bb24aad5734d002"
  LinkPlacement = pos=(29.6,19.1,0) rot=(0,0,-1;1.5708rad)
  LinkedObject = -> Shape100
  Placement = pos=(29.6,19.1,0) rot=(0,0,-1;1.5708rad)
FEATURE [App::Link] R10_R_0805_2012Metric_7538cc60fda0_ln_026  label="R20_R_0805_2012Metric_ea6fdd8e8747"
  LinkPlacement = pos=(72.8,33.8,0) rot=(0,0,1;0rad)
  LinkedObject = -> Shape100
  Placement = pos=(72.8,33.8,0) rot=(0,0,1;0rad)
FEATURE [App::Link] R10_R_0805_2012Metric_7538cc60fda0_ln_027  label="R8_R_0805_2012Metric_480b88d35bee002"
  LinkPlacement = pos=(7.00002,16.7,0) rot=(0,0,1;3.14159rad)
  LinkedObject = -> Shape100
  Placement = pos=(7.00002,16.7,0) rot=(0,0,1;3.14159rad)
FEATURE [App::Link] R10_R_0805_2012Metric_7538cc60fda0_ln_028  label="R6_R_0805_2012Metric_ed46adc45479"
  LinkPlacement = pos=(10.7,26.4,0) rot=(0,0,1;3.14159rad)
  LinkedObject = -> Shape100
  Placement = pos=(10.7,26.4,0) rot=(0,0,1;3.14159rad)
FEATURE [App::Link] R10_R_0805_2012Metric_7538cc60fda0_ln_029  label="R18_R_0805_2012Metric_272588301ff011"
  LinkPlacement = pos=(43.8,3.40002,0) rot=(0,0,1;0rad)
  LinkedObject = -> Shape100
  Placement = pos=(43.8,3.40002,0) rot=(0,0,1;0rad)
FEATURE [App::Link] R10_R_0805_2012Metric_7538cc60fda0_ln_030  label="R9_R_0805_2012Metric_c71733df7f9f002"
  LinkPlacement = pos=(3.10002,16.7,0) rot=(0,0,1;0rad)
  LinkedObject = -> Shape100
  Placement = pos=(3.10002,16.7,0) rot=(0,0,1;0rad)
FEATURE [App::Link] R10_R_0805_2012Metric_7538cc60fda0_ln_031  label="R2_R_0805_2012Metric_0dd0370ec1da002"
  LinkPlacement = pos=(29.6,14.6285,0) rot=(0,0,-1;1.5708rad)
  LinkedObject = -> Shape100
  Placement = pos=(29.6,14.6285,0) rot=(0,0,-1;1.5708rad)
FEATURE [App::Link] R10_R_0805_2012Metric_7538cc60fda0_ln_032  label="R4_R_0805_2012Metric_84be3173d967"
  LinkPlacement = pos=(20.9625,43.64,0) rot=(0,0,1;3.14159rad)
  LinkedObject = -> Shape100
  Placement = pos=(20.9625,43.64,0) rot=(0,0,1;3.14159rad)
FEATURE [App::Link] R10_R_0805_2012Metric_7538cc60fda0_ln_033  label="R16_R_0805_2012Metric_d9bee0a38b068"
  LinkPlacement = pos=(80.6,38,0) rot=(0,0,1;3.14159rad)
  LinkedObject = -> Shape100
  Placement = pos=(80.6,38,0) rot=(0,0,1;3.14159rad)
FEATURE [App::Link] R10_R_0805_2012Metric_7538cc60fda0_ln_034  label="R12_R_0805_2012Metric_a6c8c79ee0cd002"
  LinkPlacement = pos=(31.7,15.8285,0) rot=(0,0,1;1.5708rad)
  LinkedObject = -> Shape100
  Placement = pos=(31.7,15.8285,0) rot=(0,0,1;1.5708rad)
FEATURE [App::Link] R10_R_0805_2012Metric_7538cc60fda0_ln_035  label="R21_R_0805_2012Metric_fd329559c190"
  LinkPlacement = pos=(154.3,15.5,0) rot=(0,0,-1;1.5708rad)
  LinkedObject = -> Shape100
  Placement = pos=(154.3,15.5,0) rot=(0,0,-1;1.5708rad)
FEATURE [App::Link] R10_R_0805_2012Metric_7538cc60fda0_ln_036  label="R5_R_0805_2012Metric_3d5ced576c1b002"
  LinkPlacement = pos=(24,9.20002,0) rot=(0,0,1;0rad)
  LinkedObject = -> Shape100
  Placement = pos=(24,9.20002,0) rot=(0,0,1;0rad)
FEATURE [App::Link] R10_R_0805_2012Metric_7538cc60fda0_ln_037  label="R14_R_0805_2012Metric_33922ef02624"
  LinkPlacement = pos=(46.8,49.8,0) rot=(0,0,1;3.14159rad)
  LinkedObject = -> Shape100
  Placement = pos=(46.8,49.8,0) rot=(0,0,1;3.14159rad)
FEATURE [App::Link] R10_R_0805_2012Metric_7538cc60fda0_ln_038  label="R19_R_0805_2012Metric_b54dcca9e39f001"
  LinkPlacement = pos=(71,37.5,0) rot=(0,0,1;0rad)
  LinkedObject = -> Shape100
  Placement = pos=(71,37.5,0) rot=(0,0,1;0rad)
FEATURE [App::Link] R10_R_0805_2012Metric_7538cc60fda0_ln_039  label="R17_R_0805_2012Metric_596a6c57280b001"
  LinkPlacement = pos=(154.3,11.8,0) rot=(0,0,-1;1.5708rad)
  LinkedObject = -> Shape100
  Placement = pos=(154.3,11.8,0) rot=(0,0,-1;1.5708rad)
FEATURE [App::Part] SC0917  label="U8_SC1009_bf1f1e83e551"
  Group = -> [Part__Feature259,Part__Feature260,Part__Feature261,Part__Feature262,Part__Feature263,Part__Feature264,Part__Feature265,Part__Feature266,Part__Feature267,Part__Feature268,Part__Feature269,Part__Feature270,Part__Feature271,Part__Feature272,Part__Feature273,Part__Feature274,Part__Feature275,Part__Feature276,Part__Feature277,Part__Feature278,Part__Feature279,Part__Feature280,Part__Feature281,+71 more]
  Origin = -> Origin060
  Placement = pos=(125.8,21.61,0) rot=(0.57735,0.57735,0.57735;2.0944rad)
FEATURE [Part::Feature] Shape095  label="C6_CP_Elec_63x58_0ee41fe4bfd005"
  Placement = pos=(62,32.1,0) rot=(0,0,1;1.5708rad)
  shape: bbox 8.603 x 8.606 x 5.8 mm, 41 faces (baked)
FEATURE [Part::Feature] Shape096  label="C22_C_0805_2012Metric_c419cd9c4a2f002"
  Placement = pos=(64.6,43.8,0) rot=(0,0,-1;1.5708rad)
  shape: bbox 1.25 x 2 x 1.25 mm, 28 faces (baked)
FEATURE [Part::Feature] Shape097  label="D1_D_SOD_123_5a20a041a247"
  Placement = pos=(48.6,22.5,0) rot=(0,0,1;3.14159rad)
  shape: bbox 3.8 x 1.6 x 1.25 mm, 67 faces (baked)
FEATURE [Part::Feature] Shape098  label="J2_TerminalBlock_Phoenix_PT_15_2_50_H_1x02_P500mm_Horizontal_57983e5edded002"
  Placement = pos=(3,45.6,0) rot=(0,0,-1;1.5708rad)
  shape: bbox 9 x 10.57 x 15 mm, 126 faces (baked)
FEATURE [Part::Feature] Shape099  label="J3_PinSocket_1x11_P254mm_Vertical_b0b4de05439f002"
  Placement = pos=(150.3,2.9,0) rot=(0,0,-1;1.5708rad)
  shape: bbox 27.94 x 2.54 x 10.1 mm, 351 faces (baked)
FEATURE [Part::Feature] Shape100  label="R10_R_0805_2012Metric_7538cc60fda002"
  Placement = pos=(14.5,22.1,0) rot=(0,0,1;0rad)
  shape: bbox 2 x 1.2 x 0.45 mm, 26 faces (baked)
FEATURE [Part::Feature] Shape101  label="M2_Fan_Pin_Header_Straight_1x04_4971bfcbb114"
  Placement = pos=(5.96002,12.0285,0) rot=(0,0,1;0rad)
  shape: bbox 10.2 x 5.84 x 13.5 mm, 99 faces (baked)
FEATURE [Part::Feature] Shape102  label="U6_SOIC_28W_75x179mm_P127mm_746d43082d9a002"
  Placement = pos=(83.5,16,0) rot=(0,0,-1;1.5708rad)
  shape: bbox 17.9 x 10.3 x 2.75 mm, 456 faces (baked)
FEATURE [Part::Feature] Shape103  label="Q2_SOT_23_c919c89d7c036"
  Placement = pos=(76.8,32,0) rot=(0,0,1;3.14159rad)
  shape: bbox 2.5 x 3 x 1.2 mm, 76 faces (baked)
FEATURE [Part::Feature] Shape104  label="JP8_PinHeader_1x02_P254mm_Vertical_ed570ec3ee036"
  Placement = pos=(30.5,43.84,0) rot=(0,0,1;0rad)
  shape: bbox 2.54 x 5.08 x 11.54 mm, 52 faces (baked)
FEATURE [Part::Feature] Shape105  label="D6_LED_0805_2012Metric_630bc1ac9418"
  Placement = pos=(24.5625,43.64,0) rot=(0,0,1;0rad)
  shape: bbox 2 x 1.25 x 1.1 mm, 50 faces (baked)
FEATURE [Part::Feature] Shape106  label="U3_QSOP_16_39x49mm_P0635mm_7381d1256306"
  Placement = pos=(9.70002,21.6,0) rot=(0,0,1;1.5708rad)
  shape: bbox 4.9 x 6 x 1.42 mm, 260 faces (baked)
FEATURE [Part::Feature] Shape107  label="J1_MCV_01x02_G_3_81mm_8d2d7ae2d0cf002"
  Placement = pos=(3.7,30.5,0) rot=(0,0,1;1.5708rad)
  shape: bbox 7.55 x 9.01 x 12.6 mm, 76 faces (baked)
FEATURE [Part::Feature] Shape108  label="L2_L_1210_3225Metric_8f5c69fc0357"
  Placement = pos=(52.4,46,0) rot=(0,0,1;3.14159rad)
  shape: bbox 3.2 x 2.5 x 2.5 mm, 28 faces (baked)
FEATURE [Part::Feature] Shape109  label="D15_D_MiniMELF_Standard_ca1fadf4eb030"
  Placement = pos=(57.8,46.4,0) rot=(0,0,1;0rad)
  shape: bbox 3.6 x 1.4 x 1.4 mm, 13 faces (baked)
FEATURE [Part::Feature] Shape110  label="J9_PinHeader_1x06_P254mm_Vertical_f561237d0f055"
  Placement = pos=(137.72,38.7,0) rot=(0,0,1;1.5708rad)
  shape: bbox 15.24 x 2.54 x 11.54 mm, 148 faces (baked)
FEATURE [Part::Feature] Shape111  label="J8_PinHeader_2x08_P254mm_Vertical_411dce5b0f099"
  Placement = pos=(118.075,4.875,0) rot=(0,0,-1;1.5708rad)
  shape: bbox 20.32 x 5.08 x 11.54 mm, 340 faces (baked)
FEATURE [Part::Feature] Shape112  label="J10_JST_B2B_XH_A_3a5731dab8f005"
  Placement = pos=(92.65,48.725,0) rot=(0,0,1;0rad)
  shape: bbox 7.4 x 5.75 x 10.4 mm, 89 faces (baked)
FEATURE [Part::Feature] Shape113  label="D11_D_SMA_1bb42aa92950"
  Placement = pos=(21.6,-1.29998,0) rot=(0,0,1;3.14159rad)
  shape: bbox 5 x 2.7 x 2.22 mm, 41 faces (baked)
FEATURE [Part::Feature] Shape114  label="U7_SOT_223_9813f15a1232"
  Placement = pos=(69.4,46,0) rot=(0,0,-1;1.5708rad)
  shape: bbox 6.5 x 7 x 1.7 mm, 78 faces (baked)
FEATURE [Part::Feature] Shape115  label="U2_SOT_23_6_80ad3168e82c002"
  Placement = pos=(24.13,30.2,0) rot=(0,0,1;3.14159rad)
  shape: bbox 2.8 x 2.9 x 1.55 mm, 124 faces (baked)
FEATURE [Part::Feature] Shape116  label="J11_IDC_Header_2x08_P254mm_Vertical_e1f45a9088de001"
  Placement = pos=(159.1,27,0) rot=(0,0,1;3.14159rad)
  shape: bbox 9.1 x 27.98 x 12.1 mm, 330 faces (baked)
FEATURE [Part::Feature] Shape117  label="U11_SOIC_8_39x49mm_P127mm_867d4187783b002"
  Placement = pos=(108.665,42.85,0) rot=(0,0,1;0rad)
  shape: bbox 6 x 4.9 x 1.75 mm, 156 faces (baked)
FEATURE [Part::Feature] Shape118  label="J7_PinSocket_2x08_P254mm_Vertical_a805aa90854e002"
  Placement = pos=(57.075,-11.01,-1.592) rot=(0.707107,0.707107,0;3.14159rad)
  shape: bbox 20.32 x 5.08 x 10.1 mm, 506 faces (baked)
FEATURE [App::Part] Bot_51fb002  label="Bot_51fb004"
  Group = -> [Shape118]
  Origin = -> Origin058
FEATURE [App::Link] TP4_TestPoint_Loop_D2_54mm_Drill1_5mm_Beaded_cp002_8f60d36f4fd8_ln_006  label="TP5_TestPoint_Loop_D2_54mm_Drill1_5mm_Beaded_cp002_0b7b98566b060"
  LinkPlacement = pos=(42.1,-1.8,0) rot=(0,0,1;0rad)
  LinkedObject = -> TestPoint_Loop_D2_54mm_Drill1_5mm_Beaded_cp002
  Placement = pos=(42.1,-1.8,0) rot=(0,0,1;0rad)
FEATURE [App::Link] TP4_TestPoint_Loop_D2_54mm_Drill1_5mm_Beaded_cp002_8f60d36f4fd8_ln_007  label="TP1_TestPoint_Loop_D2_54mm_Drill1_5mm_Beaded_cp002_9e1e075e0d1f002"
  LinkPlacement = pos=(42.6,49.1,0) rot=(0,0,1;0rad)
  LinkedObject = -> TestPoint_Loop_D2_54mm_Drill1_5mm_Beaded_cp002
  Placement = pos=(42.6,49.1,0) rot=(0,0,1;0rad)
FEATURE [App::Link] TP4_TestPoint_Loop_D2_54mm_Drill1_5mm_Beaded_cp002_8f60d36f4fd8_ln_008  label="TP2_TestPoint_Loop_D2_54mm_Drill1_5mm_Beaded_cp002_4444e0770bde002"
  LinkPlacement = pos=(43.2,14.6,0) rot=(0,0,1;0rad)
  LinkedObject = -> TestPoint_Loop_D2_54mm_Drill1_5mm_Beaded_cp002
  Placement = pos=(43.2,14.6,0) rot=(0,0,1;0rad)
FEATURE [App::Part] TestPoint_Loop_D2_54mm_Drill1_5mm_Beaded_cp002  label="TP4_TestPoint_Loop_D2_54mm_Drill1_5mm_Beaded_cp002_8f60d36f4fd010"
  Group = -> [Part__Feature257,Part__Feature258]
  Origin = -> Origin059
  Placement = pos=(58.5,14,0) rot=(0,0,1;0rad)
FEATURE [App::Link] U11_SOIC_8_39x49mm_P127mm_867d4187783b_ln_002  label="U4_SOIC_8_39x49mm_P127mm_4428ff659323"
  LinkPlacement = pos=(36.475,17.4235,0) rot=(0,0,1;3.14159rad)
  LinkedObject = -> Shape117
  Placement = pos=(36.475,17.4235,0) rot=(0,0,1;3.14159rad)
FEATURE [App::Link] U3_QSOP_16_39x49mm_P0635mm_7381d1256304_ln_002  label="U1_QSOP_16_39x49mm_P0635mm_61417655afff002"
  LinkPlacement = pos=(25.6,16,0) rot=(0,0,1;1.5708rad)
  LinkedObject = -> Shape106
  Placement = pos=(25.6,16,0) rot=(0,0,1;1.5708rad)
FEATURE [App::Link] U7_SOT_223_9813f15a1230_ln_004  label="U9_SOT_223_6d2a4fb53033"
  LinkPlacement = pos=(82.05,46.05,0) rot=(0,0,-1;1.5708rad)
  LinkedObject = -> Shape114
  Placement = pos=(82.05,46.05,0) rot=(0,0,-1;1.5708rad)
FEATURE [App::Link] U7_SOT_223_9813f15a1230_ln_005  label="U5_SOT_223_0a21e31ed99f002"
  LinkPlacement = pos=(22.7,49.49,0) rot=(0,0,1;1.5708rad)
  LinkedObject = -> Shape114
  Placement = pos=(22.7,49.49,0) rot=(0,0,1;1.5708rad)
FEATURE [App::Part] Top_51fb002  label="Top_51fb004"
  Group = -> [Shape095,Shape096,Shape097,C22_C_0805_2012Metric_c419cd9c4a2f_ln_042,D1_D_SOD_123_5a20a041a245_ln_012,Shape098,C22_C_0805_2012Metric_c419cd9c4a2f_ln_043,C22_C_0805_2012Metric_c419cd9c4a2f_ln_044,Shape099,TestPoint_Loop_D2_54mm_Drill1_5mm_Beaded_cp002,Shape100,C22_C_0805_2012Metric_c419cd9c4a2f_ln_045,Shape101,M2_Fan_Pin_Header_Straight_1x04_4971bfcbb112_ln_004,SC0917,+83 more]
  Origin = -> Origin057
FEATURE [App::Part] Step_Models_51fb002  label="Step_Models_51fb004"
  Group = -> [Top_51fb002,Bot_51fb002]
  Origin = -> Origin056
FEATURE [App::Part] Board_51fb002  label="EL-Load-PowerTest004"
  Group = -> [Local_CS_51fb002,Board_Geoms_51fb002,Step_Models_51fb002]
  Origin = -> Origin055
  Placement = pos=(191.67,76.67,12) rot=(0,0,1;3.14159rad)
FEATURE [Part::Feature] Shape125  label="HeatsinkShroud001"
  Placement = pos=(5.3,154,22.5) rot=(0.57735,0.57735,0.57735;2.0944rad)
  shape: bbox 10 x 34.69 x 30 mm, 252 faces (baked)
FEATURE [PartDesign::SubShapeBinder] Binder
  BindCopyOnChange = 0
  BindMode = 0
  ClaimChildren = false
  Context = -> Body [Binder.]
  Fuse = false
  MakeFace = true
  OffsetFill = false
  OffsetIntersection = false
  OffsetJoinType = 0
  OffsetOpenResult = false
  PartialLoad = false
  Relative = true
  Support = -> [Shape125[Face11]]
  _Version = 2
FEATURE [PartDesign::Pad] Pad
  Direction = (1,0,1e-16)
  Length = 140
  Length2 = 10
  Profile = -> Binder
  Suppressed = false
  Type = 0
FEATURE [PartDesign::Body] Body  label="Heatsink"
  AllowCompound = false
  Group = -> [Binder,Pad]
  Origin = -> Origin067
  Tip = -> Pad
FEATURE [Sketcher::SketchObject] Sketch
  ArcFitTolerance = 0
  AttachmentSupport = -> [XY_Plane068]
  FullyConstrained = false
  MakeInternals = false
  MapMode = 5
  sketch-geometry (72):
    g0: LineSegment StartX=12.25 StartY=182 StartZ=0 EndX=190.25 EndY=182 EndZ=0
    g1: LineSegment StartX=196.25 StartY=176 StartZ=0 EndX=196.25 EndY=3 EndZ=0
    g2: LineSegment StartX=190.25 StartY=-3 StartZ=0 EndX=12.25 EndY=-3 EndZ=0
    g3: LineSegment StartX=6.25 StartY=3 StartZ=0 EndX=6.25 EndY=97 EndZ=0
    g4: ArcOfCircle CenterX=190.25 CenterY=176 CenterZ=0 NormalX=0 NormalY=0 NormalZ=1 AngleXU=0 Radius=6 StartAngle=-2.7e-15 EndAngle=1.5708
    g5: GeomPoint [constr] X=196.25 Y=182 Z=0
    g6: ArcOfCircle CenterX=190.25 CenterY=3 CenterZ=0 NormalX=0 NormalY=0 NormalZ=1 AngleXU=0 Radius=6 StartAngle=4.71239 EndAngle=6.28319
    g7: GeomPoint [constr] X=196.25 Y=-3 Z=0
    g8: ArcOfCircle CenterX=12.25 CenterY=176 CenterZ=0 NormalX=0 NormalY=0 NormalZ=1 AngleXU=0 Radius=6 StartAngle=1.5708 EndAngle=3.14159
    g9: GeomPoint [constr] X=6.25 Y=182 Z=0
    g10: ArcOfCircle CenterX=12.25 CenterY=3 CenterZ=0 NormalX=0 NormalY=0 NormalZ=1 AngleXU=0 Radius=6 StartAngle=3.14159 EndAngle=4.71239
    g11: GeomPoint [constr] X=6.25 Y=-3 Z=0
    g12: Circle CenterX=11 CenterY=173.498 CenterZ=0 NormalX=0 NormalY=0 NormalZ=1 AngleXU=0 Radius=1.45
    g13: Circle CenterX=11 CenterY=89.4976 CenterZ=0 NormalX=0 NormalY=0 NormalZ=1 AngleXU=0 Radius=1.45
    g14: Circle CenterX=180.742 CenterY=173.605 CenterZ=0 NormalX=0 NormalY=0 NormalZ=1 AngleXU=0 Radius=1.45
    g15: Circle CenterX=181.761 CenterY=91.0561 CenterZ=0 NormalX=0 NormalY=0 NormalZ=1 AngleXU=0 Radius=1.45
    g16: ArcOfCircle CenterX=48.25 CenterY=97.4976 CenterZ=0 NormalX=0 NormalY=0 NormalZ=1 AngleXU=0 Radius=8 StartAngle=3.14159 EndAngle=4.71239
    g17: LineSegment StartX=40.25 StartY=97.4976 StartZ=0 EndX=40.25 EndY=122 EndZ=0
    g18: ArcOfCircle CenterX=48.25 CenterY=122 CenterZ=0 NormalX=0 NormalY=0 NormalZ=1 AngleXU=0 Radius=8 StartAngle=1.5708 EndAngle=3.14159
    g19: LineSegment StartX=48.25 StartY=130 StartZ=0 EndX=168.625 EndY=130 EndZ=0
    g20: ArcOfCircle CenterX=168.625 CenterY=122 CenterZ=0 NormalX=0 NormalY=0 NormalZ=1 AngleXU=0 Radius=8 StartAngle=-9.8e-15 EndAngle=1.5708
    g21: LineSegment StartX=176.625 StartY=122 StartZ=0 EndX=176.625 EndY=97.4976 EndZ=0
    g22: ArcOfCircle CenterX=168.625 CenterY=97.4976 CenterZ=0 NormalX=0 NormalY=0 NormalZ=1 AngleXU=0 Radius=8 StartAngle=4.71239 EndAngle=6.28319
    g23: LineSegment StartX=168.625 StartY=89.4976 StartZ=0 EndX=48.25 EndY=89.4976 EndZ=0
    g24: GeomPoint [constr] X=40.25 Y=89.4976 Z=0
    g25: GeomPoint [constr] X=176.625 Y=130 Z=0
    g26: ArcOfCircle CenterX=23.25 CenterY=147 CenterZ=0 NormalX=0 NormalY=0 NormalZ=1 AngleXU=0 Radius=8 StartAngle=3.14159 EndAngle=4.71239
    g27: LineSegment StartX=15.25 StartY=147 StartZ=0 EndX=15.25 EndY=165.498 EndZ=0
    g28: ArcOfCircle CenterX=23.25 CenterY=165.498 CenterZ=0 NormalX=0 NormalY=0 NormalZ=1 AngleXU=0 Radius=8 StartAngle=1.5708 EndAngle=3.14159
    g29: LineSegment StartX=23.25 StartY=173.498 StartZ=0 EndX=168.564 EndY=173.498 EndZ=0
    g30: ArcOfCircle CenterX=168.564 CenterY=165.498 CenterZ=0 NormalX=0 NormalY=0 NormalZ=1 AngleXU=0 Radius=8 StartAngle=-8e-15 EndAngle=1.5708
    g31: LineSegment StartX=176.564 StartY=165.498 StartZ=0 EndX=176.564 EndY=147 EndZ=0
    g32: ArcOfCircle CenterX=168.564 CenterY=147 CenterZ=0 NormalX=0 NormalY=0 NormalZ=1 AngleXU=0 Radius=8 StartAngle=4.71239 EndAngle=6.28319
    g33: LineSegment StartX=168.564 StartY=139 StartZ=0 EndX=23.25 EndY=139 EndZ=0
    g34: GeomPoint [constr] X=15.25 Y=139 Z=0
    g35: GeomPoint [constr] X=176.564 Y=173.498 Z=0
    g36: LineSegment StartX=6.25 StartY=130 StartZ=0 EndX=23.25 EndY=130 EndZ=0
    g37: ArcOfCircle CenterX=23.25 CenterY=122 CenterZ=0 NormalX=0 NormalY=0 NormalZ=1 AngleXU=0 Radius=8 StartAngle=-9.8e-15 EndAngle=1.5708
    g38: LineSegment StartX=31.25 StartY=122 StartZ=0 EndX=31.25 EndY=105 EndZ=0
    g39: ArcOfCircle CenterX=23.25 CenterY=105 CenterZ=0 NormalX=0 NormalY=0 NormalZ=1 AngleXU=0 Radius=8 StartAngle=4.71239 EndAngle=6.28319
    g40: LineSegment StartX=23.25 StartY=97 StartZ=0 EndX=6.25 EndY=97 EndZ=0
    g41: GeomPoint [constr] X=-2.4437 Y=97 Z=0
    g42: GeomPoint [constr] X=31.25 Y=130 Z=0
    g43: LineSegment StartX=6.25 StartY=130 StartZ=0 EndX=6.25 EndY=176 EndZ=0
    g44: LineSegment [constr] StartX=15.25 StartY=147 StartZ=0 EndX=6.25 EndY=147 EndZ=0
    g45: LineSegment [constr] StartX=11 StartY=173.498 StartZ=0 EndX=16.5518 EndY=169.872 EndZ=0
    g46: LineSegment [constr] StartX=180.742 StartY=173.605 StartZ=0 EndX=175.223 EndY=169.931 EndZ=0
    g47: LineSegment [constr] StartX=181.761 StartY=91.0561 StartZ=0 EndX=175.807 EndY=93.9755 EndZ=0
    g48: LineSegment [constr] StartX=23.25 StartY=130 StartZ=0 EndX=23.25 EndY=139 EndZ=0
    g49: LineSegment [constr] StartX=48.25 StartY=130 StartZ=0 EndX=48.25 EndY=139 EndZ=0
    g50: LineSegment [constr] StartX=31.25 StartY=105 StartZ=0 EndX=40.25 EndY=105 EndZ=0
    g51: Circle CenterX=44.67 CenterY=76.67 CenterZ=0 NormalX=0 NormalY=0 NormalZ=1 AngleXU=0 Radius=1.45
    g52: Circle CenterX=44.67 CenterY=24.67 CenterZ=0 NormalX=0 NormalY=0 NormalZ=1 AngleXU=0 Radius=1.45
    g53: Circle CenterX=191.67 CenterY=24.67 CenterZ=0 NormalX=0 NormalY=0 NormalZ=1 AngleXU=0 Radius=1.45
    g54: Circle CenterX=191.67 CenterY=76.67 CenterZ=0 NormalX=0 NormalY=0 NormalZ=1 AngleXU=0 Radius=1.45
    g55: LineSegment [constr] StartX=44.67 StartY=24.67 StartZ=0 EndX=191.67 EndY=24.67 EndZ=0
    g56: LineSegment [constr] StartX=191.67 StartY=24.67 StartZ=0 EndX=191.67 EndY=76.67 EndZ=0
    g57: LineSegment [constr] StartX=191.67 StartY=76.67 StartZ=0 EndX=44.67 EndY=76.67 EndZ=0
    g58: LineSegment [constr] StartX=44.67 StartY=76.67 StartZ=0 EndX=44.67 EndY=24.67 EndZ=0
    g59: ArcOfCircle CenterX=59.67 CenterY=14 CenterZ=0 NormalX=0 NormalY=0 NormalZ=1 AngleXU=0 Radius=8 StartAngle=3.14159 EndAngle=4.71239
    g60: LineSegment StartX=51.67 StartY=14 StartZ=0 EndX=51.67 EndY=68.67 EndZ=0
    g61: ArcOfCircle CenterX=59.67 CenterY=68.67 CenterZ=0 NormalX=0 NormalY=0 NormalZ=1 AngleXU=0 Radius=8 StartAngle=1.5708 EndAngle=3.14159
    g62: LineSegment StartX=59.67 StartY=76.67 StartZ=0 EndX=176.67 EndY=76.67 EndZ=0
    g63: ArcOfCircle CenterX=176.67 CenterY=68.67 CenterZ=0 NormalX=0 NormalY=0 NormalZ=1 AngleXU=0 Radius=8 StartAngle=-8e-15 EndAngle=1.5708
    g64: LineSegment StartX=184.67 StartY=68.67 StartZ=0 EndX=184.67 EndY=14 EndZ=0
    g65: ArcOfCircle CenterX=176.67 CenterY=14 CenterZ=0 NormalX=0 NormalY=0 NormalZ=1 AngleXU=0 Radius=8 StartAngle=4.71239 EndAngle=6.28319
    g66: LineSegment StartX=176.67 StartY=6 StartZ=0 EndX=59.67 EndY=6 EndZ=0
    g67: GeomPoint [constr] X=51.67 Y=6 Z=0
    g68: GeomPoint [constr] X=184.67 Y=76.67 Z=0
    g69: LineSegment [constr] StartX=59.67 StartY=6 StartZ=0 EndX=59.67 EndY=-3 EndZ=0
    g70: LineSegment [constr] StartX=191.67 StartY=76.67 StartZ=0 EndX=183.729 EndY=72.4347 EndZ=0
    g71: LineSegment [constr] StartX=44.67 StartY=76.67 StartZ=0 EndX=52.6112 EndY=72.4347 EndZ=0
  constraints (180):
    c: Horizontal(g0)
    c: Horizontal(g2)
    c: Vertical(g1)
    c: Vertical(g3)
    c: DistanceY(g11,g9) = 185
    c: DistanceY(g11,g-1) = 3
    c: DistanceX(g-1,g11) = 6.25
    c: DistanceX(g9,g5) = 190
    c: PointOnObject(g5,g0)
    c: PointOnObject(g5,g1)
    c: Tangent(g0,g4) = 1.5708
    c: Tangent(g1,g4) = 1.5708
    c: PointOnObject(g7,g1)
    c: PointOnObject(g7,g2)
    c: Tangent(g1,g6) = 1.5708
    c: Tangent(g2,g6) = 1.5708
    c: PointOnObject(g9,g0)
    c: PointOnObject(g9,g3)
    c: Tangent(g0,g8) = 1.5708
    c: PointOnObject(g11,g2)
    c: PointOnObject(g11,g3)
    c: Tangent(g2,g10) = 1.5708
    c: Tangent(g3,g10) = 1.5708
    c: Equal(g10,g8)
    c: Equal(g8,g4)
    c: Equal(g4,g6)
    c: Radius(g4) = 6
    c: Equal(g15,g14)
    c: Equal(g14,g12)
    c: Equal(g12,g13)
    c: Vertical(g12,g13)
    c: Diameter(g15) = 2.9
    c: DistanceX(g15) = 181.761
    c: DistanceY(g15) = 91.0561
    c: DistanceX(g14) = 180.742
    c: DistanceY(g14) = 173.605
    c: DistanceX(g12) = 11
    c: DistanceY(g12) = 173.498
    c: DistanceY(g13,g12) = 84
    c: Tangent(g16,g17) = 1.5708
    c: Tangent(g17,g18) = 1.5708
    c: Tangent(g18,g19) = 1.5708
    c: Tangent(g19,g20) = 1.5708
    c: Tangent(g20,g21) = 1.5708
    c: Tangent(g21,g22) = 1.5708
    c: Tangent(g22,g23) = 1.5708
    c: Tangent(g23,g16) = 1.5708
    c: Horizontal(g19)
    c: Horizontal(g23)
    c: Vertical(g17)
    c: Vertical(g21)
    c: Equal(g16,g18)
    c: Equal(g18,g20)
    c: Equal(g20,g22)
    c: PointOnObject(g24,g17)
    c: PointOnObject(g24,g23)
    c: PointOnObject(g25,g19)
    c: PointOnObject(g25,g21)
    c: Tangent(g26,g27) = 1.5708
    c: Tangent(g27,g28) = 1.5708
    c: Tangent(g28,g29) = 1.5708
    c: Tangent(g29,g30) = 1.5708
    c: Tangent(g30,g31) = 1.5708
    c: Tangent(g31,g32) = 1.5708
    c: Tangent(g32,g33) = 1.5708
    c: Tangent(g33,g26) = 1.5708
    c: Horizontal(g29)
    c: Horizontal(g33)
    c: Vertical(g27)
    c: Vertical(g31)
    c: Equal(g26,g28)
    c: Equal(g28,g30)
    c: Equal(g30,g32)
    c: PointOnObject(g34,g27)
    c: PointOnObject(g34,g33)
    c: PointOnObject(g35,g29)
    c: PointOnObject(g35,g31)
    c: Tangent(g36,g37) = 1.5708
    c: Tangent(g37,g38) = 1.5708
    c: Tangent(g38,g39) = 1.5708
    c: Tangent(g39,g40) = 1.5708
    c: Horizontal(g36)
    c: Horizontal(g40)
    c: Vertical(g38)
    c: Equal(g37,g39)
    c: PointOnObject(g41,g40)
    c: PointOnObject(g42,g36)
    c: PointOnObject(g42,g38)
    c: Coincident(g3,g40)
    c: Coincident(g43,g36)
    c: Equal(g18,g37)
    c: Equal(g37,g26)
    c: Horizontal(g28,g12)
    c: Coincident(g44,g26)
    c: Horizontal(g44)
    c: Coincident(g45,g12)
    c: PointOnObject(g45,g28)
    c: Perpendicular(g28,g45)
    c: Coincident(g46,g14)
    c: PointOnObject(g46,g30)
    c: Perpendicular(g30,g46)
    c: Equal(g46,g45)
    c: Perpendicular(g22,g47)
    c: Equal(g47,g46)
    c: PointOnObject(g47,g22)
    c: Coincident(g47,g15)
    c: Vertical(g43)
    c: PointOnObject(g44,g43)
    c: Radius(g26) = 8
    c: Vertical(g36,g3)
    c: DistanceY(g36,g0) = 52
    c: DistanceY(g3,g36) = 33
    c: Coincident(g48,g36)
    c: Coincident(g48,g26)
    c: Vertical(g48)
    c: Equal(g48,g44)
    c: Horizontal(g16,g13)
    c: Coincident(g49,g18)
    c: PointOnObject(g49,g33)
    c: Vertical(g49)
    c: Coincident(g50,g38)
    c: PointOnObject(g50,g17)
    c: Horizontal(g50)
    c: Equal(g49,g48)
    c: Equal(g50,g48)
    c: DistanceX(g3,g38) = 25
    c: Tangent(g43,g8) = 1.5708
    c: Equal(g54,g53)
    c: Equal(g53,g52)
    c: Equal(g52,g51)
    c: Equal(g51,g15)
    c: Coincident(g55,g56)
    c: Coincident(g56,g57)
    c: Coincident(g57,g58)
    c: Coincident(g58,g55)
    c: Horizontal(g55)
    c: Horizontal(g57)
    c: Vertical(g56)
    c: Vertical(g58)
    c: Coincident(g52,g55)
    c: Coincident(g54,g56)
    c: Coincident(g55,g53)
    c: Coincident(g57,g51)
    c: DistanceY(g58,g58) = 52
    c: DistanceX(g52,g53) = 147
    c: DistanceX(g52) = 44.67
    c: DistanceY(g52) = 24.67
    c: Tangent(g59,g60) = 1.5708
    c: Tangent(g60,g61) = 1.5708
    c: Tangent(g61,g62) = 1.5708
    c: Tangent(g62,g63) = 1.5708
    c: Tangent(g63,g64) = 1.5708
    c: Tangent(g64,g65) = 1.5708
    c: Tangent(g65,g66) = 1.5708
    c: Tangent(g66,g59) = 1.5708
    c: Horizontal(g62)
    c: Horizontal(g66)
    c: Vertical(g60)
    c: Vertical(g64)
    c: Equal(g59,g61)
    c: Equal(g61,g63)
    c: Equal(g63,g65)
    c: PointOnObject(g67,g60)
    c: PointOnObject(g67,g66)
    c: PointOnObject(g68,g62)
    c: PointOnObject(g68,g64)
    c: Equal(g61,g16)
    c: Horizontal(g61,g51)
    c: Coincident(g69,g59)
    c: PointOnObject(g69,g2)
    c: Vertical(g69)
    c: Equal(g69,g50)
    c: Coincident(g70,g54)
    c: PointOnObject(g70,g63)
    c: Perpendicular(g63,g70)
    c: Coincident(g71,g51)
    c: PointOnObject(g71,g61)
    c: Perpendicular(g61,g71)
    c: Equal(g71,g50)
    c: Equal(g71,g70)
FEATURE [PartDesign::Pad] Pad001
  Direction = (0,0,1)
  Length = 1.6
  Length2 = 10
  Profile = -> Sketch
  ReferenceAxis = -> Sketch [N_Axis]
  Reversed = true
  Suppressed = false
  Type = 0
FEATURE [Sketcher::SketchObject] Sketch001
  ArcFitTolerance = 0
  AttachmentSupport = -> [XY_Plane068]
  ExternalGeometry = -> [Pad001]
  FullyConstrained = true
  MakeInternals = false
  MapMode = 5
  sketch-geometry (12):
    g0: Circle CenterX=191.67 CenterY=76.67 CenterZ=0 NormalX=0 NormalY=0 NormalZ=1 AngleXU=0 Radius=1.45
    g1: Circle CenterX=191.67 CenterY=24.67 CenterZ=0 NormalX=0 NormalY=0 NormalZ=1 AngleXU=0 Radius=1.45
    g2: ArcOfCircle CenterX=44.67 CenterY=76.67 CenterZ=0 NormalX=0 NormalY=0 NormalZ=1 AngleXU=0 Radius=7 StartAngle=9e-16 EndAngle=3.14159
    g3: ArcOfCircle CenterX=44.67 CenterY=7 CenterZ=0 NormalX=0 NormalY=0 NormalZ=1 AngleXU=0 Radius=7 StartAngle=3.14159 EndAngle=6.28319
    g4: LineSegment StartX=37.67 StartY=76.67 StartZ=0 EndX=37.67 EndY=7 EndZ=0
    g5: LineSegment StartX=51.67 StartY=7 StartZ=0 EndX=51.67 EndY=76.67 EndZ=0
    g6: ArcOfCircle CenterX=191.67 CenterY=76.67 CenterZ=0 NormalX=0 NormalY=0 NormalZ=1 AngleXU=0 Radius=4.58 StartAngle=-6.022e-13 EndAngle=3.14159
    g7: ArcOfCircle CenterX=191.67 CenterY=4.58 CenterZ=0 NormalX=0 NormalY=0 NormalZ=1 AngleXU=0 Radius=4.58 StartAngle=3.14159 EndAngle=6.28319
    g8: LineSegment StartX=187.09 StartY=76.67 StartZ=0 EndX=187.09 EndY=4.58 EndZ=0
    g9: LineSegment StartX=196.25 StartY=4.58 StartZ=0 EndX=196.25 EndY=76.67 EndZ=0
    g10: Circle CenterX=44.67 CenterY=76.67 CenterZ=0 NormalX=0 NormalY=0 NormalZ=1 AngleXU=0 Radius=1.45
    g11: Circle CenterX=44.67 CenterY=24.67 CenterZ=0 NormalX=0 NormalY=0 NormalZ=1 AngleXU=0 Radius=1.45
  constraints (24):
    c: Tangent(g3,g5) = -1.5708
    c: Tangent(g4,g3) = -1.5708
    c: Tangent(g4,g2) = -1.5708
    c: Tangent(g5,g2) = -1.5708
    c: Coincident(g10,g2)
    c: Vertical(g4)
    c: Tangent(g8,g6) = -1.5708
    c: Tangent(g6,g9) = -1.5708
    c: Coincident(g0,g6)
    c: Coincident(g-7,g0)
    c: Equal(g-7,g0)
    c: Equal(g1,g-4)
    c: Coincident(g1,g-4)
    c: Tangent(g8,g7) = -1.5708
    c: Tangent(g7,g9) = -1.5708
    c: Vertical(g8)
    c: Tangent(g7,g-5) = 1.5708
    c: Tangent(g3,g-8) = -1.5708
    c: Coincident(g-6,g2)
    c: Equal(g-6,g10)
    c: Coincident(g11,g-9)
    c: Equal(g11,g-9)
    c: Tangent(g-1,g3)
    c: Tangent(g7,g-1)
FEATURE [PartDesign::Pad] Pad002
  BaseFeature = -> Pad001
  Direction = (0,0,1)
  Length = 16.25
  Length2 = 10
  Profile = -> Sketch001
  ReferenceAxis = -> Sketch001 [N_Axis]
  Suppressed = false
  Type = 0
FEATURE [Sketcher::SketchObject] Sketch002
  ArcFitTolerance = 0
  AttachmentSupport = -> [Pad002]
  FullyConstrained = true
  MakeInternals = false
  MapMode = 5
  Placement = pos=(196.25,-1.17838e-10,0) rot=(0.57735,0.57735,0.57735;2.0944rad)
  sketch-geometry (10):
    g0: ArcOfCircle CenterX=31 CenterY=19 CenterZ=0 NormalX=0 NormalY=0 NormalZ=1 AngleXU=0 Radius=3 StartAngle=1.5708 EndAngle=3.14159
    g1: LineSegment StartX=31 StartY=22 StartZ=0 EndX=61 EndY=22 EndZ=0
    g2: ArcOfCircle CenterX=61 CenterY=19 CenterZ=0 NormalX=0 NormalY=0 NormalZ=1 AngleXU=0 Radius=3 StartAngle=-2.71463e-11 EndAngle=1.5708
    g3: LineSegment StartX=64 StartY=19 StartZ=0 EndX=64 EndY=9 EndZ=0
    g4: ArcOfCircle CenterX=61 CenterY=9 CenterZ=0 NormalX=0 NormalY=0 NormalZ=1 AngleXU=0 Radius=3 StartAngle=4.71239 EndAngle=6.28319
    g5: LineSegment StartX=61 StartY=6 StartZ=0 EndX=31 EndY=6 EndZ=0
    g6: ArcOfCircle CenterX=31 CenterY=9 CenterZ=0 NormalX=0 NormalY=0 NormalZ=1 AngleXU=0 Radius=3 StartAngle=3.14159 EndAngle=4.71239
    g7: LineSegment StartX=28 StartY=9 StartZ=0 EndX=28 EndY=19 EndZ=0
    g8: GeomPoint [constr] X=28 Y=22 Z=0
    g9: GeomPoint [constr] X=64 Y=6 Z=0
  constraints (24):
    c: Tangent(g0,g1) = 1.5708
    c: Tangent(g1,g2) = 1.5708
    c: Tangent(g2,g3) = 1.5708
    c: Tangent(g3,g4) = 1.5708
    c: Tangent(g4,g5) = 1.5708
    c: Tangent(g5,g6) = 1.5708
    c: Tangent(g6,g7) = 1.5708
    c: Tangent(g7,g0) = 1.5708
    c: Horizontal(g1)
    c: Horizontal(g5)
    c: Vertical(g3)
    c: Vertical(g7)
    c: Equal(g0,g2)
    c: Equal(g2,g4)
    c: Equal(g4,g6)
    c: PointOnObject(g8,g1)
    c: PointOnObject(g8,g7)
    c: PointOnObject(g9,g3)
    c: PointOnObject(g9,g5)
    c: Radius(g4) = 3
    c: DistanceX(g6,g3) = 36
    c: DistanceY(g-1,g5) = 6
    c: DistanceX(g6) = 28
    c: DistanceY(g3,g2) = 10
FEATURE [PartDesign::Pocket] Pocket
  BaseFeature = -> Pad002
  Direction = (-1,6.004e-13,0)
  Length = 15
  Length2 = 5
  Midplane = true
  Profile = -> Sketch002
  ReferenceAxis = -> Sketch002 [N_Axis]
  Suppressed = false
  Type = 1
FEATURE [Sketcher::SketchObject] Sketch003
  ArcFitTolerance = 0
  AttachmentOffset = pos=(0,0,-0.1) rot=(0,0,1;0rad)
  AttachmentSupport = -> [XY_Plane068]
  ExternalGeometry = -> [Pocket]
  FullyConstrained = true
  MakeInternals = false
  MapMode = 5
  Placement = pos=(0,0,-0.1) rot=(0,0,1;0rad)
  sketch-geometry (22):
    g0: ArcOfCircle CenterX=181.761 CenterY=91.0561 CenterZ=0 NormalX=0 NormalY=0 NormalZ=1 AngleXU=0 Radius=4.58 StartAngle=0.603158 EndAngle=3.74475
    g1: ArcOfCircle CenterX=191.67 CenterY=76.67 CenterZ=0 NormalX=0 NormalY=0 NormalZ=1 AngleXU=0 Radius=4.58 StartAngle=3.74475 EndAngle=6.88634
    g2: LineSegment StartX=177.989 StartY=88.4581 StartZ=0 EndX=187.898 EndY=74.072 EndZ=0
    g3: LineSegment StartX=195.442 StartY=79.268 StartZ=0 EndX=185.533 EndY=93.6541 EndZ=0
    g4: ArcOfCircle CenterX=11 CenterY=89.4976 CenterZ=0 NormalX=0 NormalY=0 NormalZ=1 AngleXU=0 Radius=4.75 StartAngle=1.20679 EndAngle=4.34839
    g5: ArcOfCircle CenterX=44.67 CenterY=76.67 CenterZ=0 NormalX=0 NormalY=0 NormalZ=1 AngleXU=0 Radius=4.75 StartAngle=4.34839 EndAngle=7.48998
    g6: LineSegment StartX=9.30891 StartY=85.0588 StartZ=0 EndX=42.9789 EndY=72.2312 EndZ=0
    g7: LineSegment StartX=46.3611 StartY=81.1088 StartZ=0 EndX=12.6911 EndY=93.9364 EndZ=0
    g8: Circle CenterX=191.67 CenterY=76.67 CenterZ=0 NormalX=0 NormalY=0 NormalZ=1 AngleXU=0 Radius=1.45
    g9: Circle CenterX=181.761 CenterY=91.0561 CenterZ=0 NormalX=0 NormalY=0 NormalZ=1 AngleXU=0 Radius=1.45
    g10: Circle CenterX=44.67 CenterY=76.67 CenterZ=0 NormalX=0 NormalY=0 NormalZ=1 AngleXU=0 Radius=1.45
    g11: Circle CenterX=11 CenterY=89.4976 CenterZ=0 NormalX=0 NormalY=0 NormalZ=1 AngleXU=0 Radius=1.45
    g12: ArcOfCircle CenterX=11 CenterY=173.498 CenterZ=0 NormalX=0 NormalY=0 NormalZ=1 AngleXU=0 Radius=4.25 StartAngle=4.738e-13 EndAngle=3.14159
    g13: ArcOfCircle CenterX=11 CenterY=165.498 CenterZ=0 NormalX=0 NormalY=0 NormalZ=1 AngleXU=0 Radius=4.25 StartAngle=3.14159 EndAngle=6.28319
    g14: LineSegment StartX=6.75 StartY=173.498 StartZ=0 EndX=6.75 EndY=165.498 EndZ=0
    g15: LineSegment StartX=15.25 StartY=165.498 StartZ=0 EndX=15.25 EndY=173.498 EndZ=0
    g16: Circle CenterX=11 CenterY=173.498 CenterZ=0 NormalX=0 NormalY=0 NormalZ=1 AngleXU=0 Radius=1.45
    g17: ArcOfCircle CenterX=180.742 CenterY=173.605 CenterZ=0 NormalX=0 NormalY=0 NormalZ=1 AngleXU=0 Radius=4.58 StartAngle=1.5708 EndAngle=4.71239
    g18: ArcOfCircle CenterX=191.67 CenterY=173.605 CenterZ=0 NormalX=0 NormalY=0 NormalZ=1 AngleXU=0 Radius=4.58 StartAngle=4.71239 EndAngle=7.85398
    g19: LineSegment StartX=180.742 StartY=169.025 StartZ=0 EndX=191.67 EndY=169.025 EndZ=0
    g20: LineSegment StartX=191.67 StartY=178.185 StartZ=0 EndX=180.742 EndY=178.185 EndZ=0
    g21: Circle CenterX=180.742 CenterY=173.605 CenterZ=0 NormalX=0 NormalY=0 NormalZ=1 AngleXU=0 Radius=1.45
  constraints (45):
    c: Tangent(g0,g2) = -1.5708
    c: Tangent(g2,g1) = -1.5708
    c: Tangent(g1,g3) = -1.5708
    c: Tangent(g3,g0) = -1.5708
    c: Equal(g0,g1)
    c: Tangent(g4,g6) = -1.5708
    c: Tangent(g6,g5) = -1.5708
    c: Tangent(g5,g7) = -1.5708
    c: Tangent(g7,g4) = -1.5708
    c: Equal(g4,g5)
    c: Equal(g-5,g8)
    c: Equal(g-3,g9)
    c: Coincident(g10,g5)
    c: Coincident(g11,g4)
    c: Tangent(g12,g14) = -1.5708
    c: Tangent(g14,g13) = -1.5708
    c: Tangent(g13,g15) = -1.5708
    c: Tangent(g15,g12) = -1.5708
    c: Equal(g12,g13)
    c: Coincident(g12,g-8)
    c: Vertical(g14)
    c: Coincident(g16,g12)
    c: Equal(g16,g-8)
    c: Tangent(g17,g19) = -1.5708
    c: Tangent(g19,g18) = -1.5708
    c: Tangent(g18,g20) = -1.5708
    c: Tangent(g20,g17) = -1.5708
    c: Equal(g17,g18)
    c: Coincident(g17,g-4)
    c: Horizontal(g19)
    c: Coincident(g21,g17)
    c: Equal(g21,g-4)
    c: Equal(g0,g17)
    c: Equal(g10,g-9)
    c: Coincident(g5,g-9)
    c: Coincident(g-5,g8)
    c: Coincident(g1,g8)
    c: Equal(g1,g-10)
    c: Tangent(g18,g-11)
    c: Coincident(g-12,g13)
    c: Coincident(g9,g0)
    c: Coincident(g0,g-3)
    c: Equal(g-14,g11)
    c: Coincident(g4,g-14)
    c: Tangent(g4,g-15)
FEATURE [PartDesign::Pad] Pad003
  BaseFeature = -> Pocket
  Direction = (0,0,1)
  Length = 3.4
  Length2 = 10
  Profile = -> Sketch003
  ReferenceAxis = -> Sketch003 [N_Axis]
  Suppressed = false
  Type = 0
FEATURE [Sketcher::SketchObject] Sketch004
  ArcFitTolerance = 0
  AttachmentSupport = -> [XY_Plane068]
  FullyConstrained = true
  MakeInternals = false
  MapMode = 5
  sketch-geometry (20):
    g0: ArcOfCircle CenterX=75.7237 CenterY=139.855 CenterZ=0 NormalX=0 NormalY=0 NormalZ=1 AngleXU=0 Radius=1 StartAngle=1.5708 EndAngle=3.14159
    g1: LineSegment StartX=75.7237 StartY=140.855 StartZ=0 EndX=91.4237 EndY=140.855 EndZ=0
    g2: ArcOfCircle CenterX=91.4237 CenterY=139.855 CenterZ=0 NormalX=0 NormalY=0 NormalZ=1 AngleXU=0 Radius=1 StartAngle=9.8e-15 EndAngle=1.5708
    g3: LineSegment StartX=92.4237 StartY=139.855 StartZ=0 EndX=92.4237 EndY=134.855 EndZ=0
    g4: ArcOfCircle CenterX=91.4237 CenterY=134.855 CenterZ=0 NormalX=0 NormalY=0 NormalZ=1 AngleXU=0 Radius=1 StartAngle=4.71239 EndAngle=6.28319
    g5: LineSegment StartX=91.4237 StartY=133.855 StartZ=0 EndX=75.7237 EndY=133.855 EndZ=0
    g6: ArcOfCircle CenterX=75.7237 CenterY=134.855 CenterZ=0 NormalX=0 NormalY=0 NormalZ=1 AngleXU=0 Radius=1 StartAngle=3.14159 EndAngle=4.71239
    g7: LineSegment StartX=74.7237 StartY=134.855 StartZ=0 EndX=74.7237 EndY=139.855 EndZ=0
    g8: GeomPoint [constr] X=74.7237 Y=140.855 Z=0
    g9: GeomPoint [constr] X=92.4237 Y=133.855 Z=0
    g10: ArcOfCircle CenterX=129.924 CenterY=139.855 CenterZ=0 NormalX=0 NormalY=0 NormalZ=1 AngleXU=0 Radius=1 StartAngle=1.5708 EndAngle=3.14159
    g11: LineSegment StartX=129.924 StartY=140.855 StartZ=0 EndX=145.624 EndY=140.855 EndZ=0
    g12: ArcOfCircle CenterX=145.624 CenterY=139.855 CenterZ=0 NormalX=0 NormalY=0 NormalZ=1 AngleXU=0 Radius=1 StartAngle=-8.9e-15 EndAngle=1.5708
    g13: LineSegment StartX=146.624 StartY=139.855 StartZ=0 EndX=146.624 EndY=134.855 EndZ=0
    g14: ArcOfCircle CenterX=145.624 CenterY=134.855 CenterZ=0 NormalX=0 NormalY=0 NormalZ=1 AngleXU=0 Radius=1 StartAngle=4.71239 EndAngle=6.28319
    g15: LineSegment StartX=145.624 StartY=133.855 StartZ=0 EndX=129.924 EndY=133.855 EndZ=0
    g16: ArcOfCircle CenterX=129.924 CenterY=134.855 CenterZ=0 NormalX=0 NormalY=0 NormalZ=1 AngleXU=0 Radius=1 StartAngle=3.14159 EndAngle=4.71239
    g17: LineSegment StartX=128.924 StartY=134.855 StartZ=0 EndX=128.924 EndY=139.855 EndZ=0
    g18: GeomPoint [constr] X=128.924 Y=140.855 Z=0
    g19: GeomPoint [constr] X=146.624 Y=133.855 Z=0
  constraints (48):
    c: Tangent(g0,g1) = 1.5708
    c: Tangent(g1,g2) = 1.5708
    c: Tangent(g2,g3) = 1.5708
    c: Tangent(g3,g4) = 1.5708
    c: Tangent(g4,g5) = 1.5708
    c: Tangent(g5,g6) = 1.5708
    c: Tangent(g6,g7) = 1.5708
    c: Tangent(g7,g0) = 1.5708
    c: Horizontal(g1)
    c: Horizontal(g5)
    c: Vertical(g3)
    c: Vertical(g7)
    c: Equal(g0,g2)
    c: Equal(g2,g4)
    c: Equal(g4,g6)
    c: PointOnObject(g8,g1)
    c: PointOnObject(g8,g7)
    c: PointOnObject(g9,g3)
    c: PointOnObject(g9,g5)
    c: Tangent(g10,g11) = 1.5708
    c: Tangent(g11,g12) = 1.5708
    c: Tangent(g12,g13) = 1.5708
    c: Tangent(g13,g14) = 1.5708
    c: Tangent(g14,g15) = 1.5708
    c: Tangent(g15,g16) = 1.5708
    c: Tangent(g16,g17) = 1.5708
    c: Tangent(g17,g10) = 1.5708
    c: Horizontal(g11)
    c: Horizontal(g15)
    c: Vertical(g13)
    c: Vertical(g17)
    c: Equal(g10,g12)
    c: Equal(g12,g14)
    c: Equal(g14,g16)
    c: PointOnObject(g18,g11)
    c: PointOnObject(g18,g17)
    c: PointOnObject(g19,g13)
    c: PointOnObject(g19,g15)
    c: Horizontal(g4,g15)
    c: Equal(g1,g11)
    c: Equal(g2,g10)
    c: Horizontal(g10,g1)
    c: DistanceX(g5) = 75.7237
    c: DistanceY(g5) = 133.855
    c: DistanceX(g5,g5) = 15.7
    c: DistanceY(g3,g3) = 5
    c: Radius(g2) = 1
    c: DistanceX(g4,g15) = 38.5
FEATURE [PartDesign::Pocket] Pocket001
  BaseFeature = -> Pad003
  Direction = (0,0,-1)
  Length = 5
  Length2 = 5
  Profile = -> Sketch004
  ReferenceAxis = -> Sketch004 [N_Axis]
  Suppressed = false
  Type = 0
FEATURE [PartDesign::SubShapeBinder] Binder001
  BindCopyOnChange = 0
  BindMode = 0
  ClaimChildren = false
  Context = -> Body002 [Binder001.]
  Fuse = false
  MakeFace = true
  OffsetFill = false
  OffsetIntersection = false
  OffsetJoinType = 0
  OffsetOpenResult = false
  PartialLoad = false
  Relative = true
  Support = -> [_455U2201[Part__Feature021.]]
  _Version = 2
FEATURE [Sketcher::SketchObject] Sketch006  label="Fan"
  ArcFitTolerance = 0
  AttachmentOffset = pos=(55,-105,0) rot=(0,0,1;0.785398rad)
  AttachmentSupport = -> [YZ_Plane069]
  FullyConstrained = true
  MakeInternals = false
  MapMode = 5
  Placement = pos=(0,55,-105) rot=(0.678598,0.281085,0.678598;2.59356rad)
  sketch-geometry (11):
    g0: LineSegment [constr] StartX=173.5 StartY=33.6 StartZ=0 EndX=141.5 EndY=33.6 EndZ=0
    g1: LineSegment [constr] StartX=141.5 StartY=33.6 StartZ=0 EndX=141.5 EndY=1.6 EndZ=0
    g2: LineSegment [constr] StartX=141.5 StartY=1.6 StartZ=0 EndX=173.5 EndY=1.6 EndZ=0
    g3: LineSegment [constr] StartX=173.5 StartY=1.6 StartZ=0 EndX=173.5 EndY=33.6 EndZ=0
    g4: Circle CenterX=173.5 CenterY=33.6 CenterZ=0 NormalX=0 NormalY=0 NormalZ=1 AngleXU=0 Radius=2
    g5: Circle CenterX=141.5 CenterY=33.6 CenterZ=0 NormalX=0 NormalY=0 NormalZ=1 AngleXU=0 Radius=2
    g6: Circle CenterX=141.5 CenterY=1.6 CenterZ=0 NormalX=0 NormalY=0 NormalZ=1 AngleXU=0 Radius=2
    g7: Circle CenterX=173.5 CenterY=1.6 CenterZ=0 NormalX=0 NormalY=0 NormalZ=1 AngleXU=0 Radius=2
    g8: Circle CenterX=157.5 CenterY=17.6 CenterZ=0 NormalX=0 NormalY=0 NormalZ=1 AngleXU=0 Radius=19.5
    g9: LineSegment [constr] StartX=157.5 StartY=17.6 StartZ=0 EndX=157.5 EndY=33.6 EndZ=0
    g10: LineSegment [constr] StartX=157.5 StartY=17.6 StartZ=0 EndX=157.5 EndY=1.6 EndZ=0
  constraints (28):
    c: Coincident(g0,g1)
    c: Coincident(g1,g2)
    c: Coincident(g2,g3)
    c: Coincident(g3,g0)
    c: Horizontal(g0)
    c: Horizontal(g2)
    c: Vertical(g1)
    c: Vertical(g3)
    c: Equal(g1,g2)
    c: Coincident(g4,g0)
    c: Coincident(g5,g0)
    c: Coincident(g6,g1)
    c: Coincident(g7,g2)
    c: Equal(g7,g6)
    c: Equal(g6,g5)
    c: Equal(g5,g4)
    c: Diameter(g6) = 4
    c: Coincident(g9,g8)
    c: Vertical(g9)
    c: Symmetric(g5,g4,g9)
    c: Diameter(g8) = 39
    c: Coincident(g10,g8)
    c: PointOnObject(g10,g2)
    c: Vertical(g10)
    c: Equal(g10,g9)
    c: Distance(g0) = 32
    c: DistanceX(g7) = 173.5
    c: DistanceY(g7) = 1.6
FEATURE [Sketcher::SketchObject] Sketch007  label="Panel"
  ArcFitTolerance = 0
  AttachmentSupport = -> [YZ_Plane069]
  ExternalGeometry = -> [Binder001]
  FullyConstrained = true
  MakeInternals = false
  MapMode = 5
  Placement = pos=(0,0,0) rot=(0.57735,0.57735,0.57735;2.0944rad)
  sketch-geometry (18):
    g0: ArcOfCircle CenterX=181.1 CenterY=49.2 CenterZ=0 NormalX=0 NormalY=0 NormalZ=1 AngleXU=0 Radius=3.9 StartAngle=-8.429e-13 EndAngle=1.5708
    g1: LineSegment StartX=185 StartY=49.2 StartZ=0 EndX=185 EndY=-9 EndZ=0
    g2: ArcOfCircle CenterX=181.1 CenterY=-9 CenterZ=0 NormalX=0 NormalY=0 NormalZ=1 AngleXU=0 Radius=3.9 StartAngle=4.71239 EndAngle=6.28319
    g3: LineSegment StartX=181.1 StartY=-12.9 StartZ=0 EndX=-2.1 EndY=-12.9 EndZ=0
    g4: ArcOfCircle CenterX=-2.1 CenterY=-9 CenterZ=0 NormalX=0 NormalY=0 NormalZ=1 AngleXU=0 Radius=3.9 StartAngle=3.14159 EndAngle=4.71239
    g5: LineSegment StartX=-6 StartY=-9 StartZ=0 EndX=-6 EndY=49.2 EndZ=0
    g6: ArcOfCircle CenterX=-2.1 CenterY=49.2 CenterZ=0 NormalX=0 NormalY=0 NormalZ=1 AngleXU=0 Radius=3.9 StartAngle=1.5708 EndAngle=3.14159
    g7: LineSegment StartX=-2.1 StartY=53.1 StartZ=0 EndX=181.1 EndY=53.1 EndZ=0
    g8: GeomPoint [constr] X=185 Y=53.1 Z=0
    g9: GeomPoint [constr] X=-6 Y=-12.9 Z=0
    g10: Circle CenterX=180.25 CenterY=49.11 CenterZ=0 NormalX=0 NormalY=0 NormalZ=1 AngleXU=0 Radius=2.1
    g11: Circle CenterX=180.25 CenterY=-8.91 CenterZ=0 NormalX=0 NormalY=0 NormalZ=1 AngleXU=0 Radius=2.1
    g12: Circle CenterX=-1.25 CenterY=-8.91 CenterZ=0 NormalX=0 NormalY=0 NormalZ=1 AngleXU=0 Radius=2.1
    g13: Circle CenterX=-1.25 CenterY=49.11 CenterZ=0 NormalX=0 NormalY=0 NormalZ=1 AngleXU=0 Radius=2.1
    g14: LineSegment [constr] StartX=-1.25 StartY=49.11 StartZ=0 EndX=180.25 EndY=49.11 EndZ=0
    g15: LineSegment [constr] StartX=180.25 StartY=49.11 StartZ=0 EndX=180.25 EndY=-8.91 EndZ=0
    g16: LineSegment [constr] StartX=180.25 StartY=-8.91 StartZ=0 EndX=-1.25 EndY=-8.91 EndZ=0
    g17: LineSegment [constr] StartX=-1.25 StartY=-8.91 StartZ=0 EndX=-1.25 EndY=49.11 EndZ=0
  constraints (42):
    c: Tangent(g0,g1) = 1.5708
    c: Tangent(g1,g2) = 1.5708
    c: Tangent(g2,g3) = 1.5708
    c: Tangent(g3,g4) = 1.5708
    c: Tangent(g4,g5) = 1.5708
    c: Tangent(g5,g6) = 1.5708
    c: Tangent(g6,g7) = 1.5708
    c: Tangent(g7,g0) = 1.5708
    c: Horizontal(g3)
    c: Horizontal(g7)
    c: Vertical(g1)
    c: Vertical(g5)
    c: Equal(g0,g2)
    c: Equal(g2,g4)
    c: Equal(g4,g6)
    c: PointOnObject(g8,g1)
    c: PointOnObject(g8,g7)
    c: PointOnObject(g9,g3)
    c: PointOnObject(g9,g5)
    c: Coincident(g4,g-6)
    c: Coincident(g0,g-4)
    c: PointOnObject(g2,g-5)
    c: Coincident(g14,g15)
    c: Coincident(g15,g16)
    c: Coincident(g16,g17)
    c: Coincident(g17,g14)
    c: Horizontal(g14)
    c: Horizontal(g16)
    c: Vertical(g15)
    c: Vertical(g17)
    c: Coincident(g11,g15)
    c: Coincident(g10,g14)
    c: Coincident(g13,g14)
    c: Coincident(g12,g16)
    c: Equal(g12,g11)
    c: Equal(g11,g10)
    c: Equal(g10,g13)
    c: Diameter(g13) = 4.2
    c: Distance(g17) = 58.02
    c: Distance(g14) = 181.5
    c: DistanceX(g12) = -1.25
    c: DistanceY(g12) = -8.91
FEATURE [Sketcher::SketchObject] Sketch008
  ArcFitTolerance = 0
  AttachmentSupport = -> [XY_Plane068]
  ExternalGeometry = -> [Pocket001]
  FullyConstrained = true
  MakeInternals = false
  MapMode = 5
  sketch-geometry (6):
    g0: LineSegment StartX=26.73 StartY=3 StartZ=0 EndX=26.73 EndY=85.0588 EndZ=0
    g1: LineSegment StartX=26.73 StartY=85.0588 StartZ=0 EndX=-23.27 EndY=85.0588 EndZ=0
    g2: LineSegment StartX=-23.27 StartY=85.0588 StartZ=0 EndX=-23.27 EndY=-53 EndZ=0
    g3: LineSegment StartX=-23.27 StartY=-53 StartZ=0 EndX=32.73 EndY=-53 EndZ=0
    g4: LineSegment StartX=32.73 StartY=-53 StartZ=0 EndX=32.73 EndY=-3 EndZ=0
    g5: ArcOfCircle CenterX=32.73 CenterY=3 CenterZ=0 NormalX=0 NormalY=0 NormalZ=1 AngleXU=0 Radius=6 StartAngle=3.14159 EndAngle=4.71239
  constraints (18):
    c: Vertical(g0)
    c: Coincident(g1,g0)
    c: Horizontal(g1)
    c: Coincident(g2,g1)
    c: Vertical(g2)
    c: Coincident(g3,g2)
    c: Horizontal(g3)
    c: Coincident(g4,g3)
    c: Vertical(g4)
    c: Equal(g1,g4)
    c: Distance(g4) = 50
    c: Horizontal(g1,g-4)
    c: DistanceX(g0) = 26.73
    c: Coincident(g5,g4)
    c: Perpendicular(g5,g4)
    c: Tangent(g0,g5) = 1.5708
    c: PointOnObject(g4,g-5)
    c: Equal(g-6,g5)
FEATURE [PartDesign::Pocket] Pocket002
  BaseFeature = -> Pocket001
  Direction = (0,0,-1)
  Length = 20
  Length2 = 5
  Midplane = true
  Profile = -> Sketch008
  ReferenceAxis = -> Sketch008 [N_Axis]
  Suppressed = false
  Type = 0
FEATURE [Sketcher::SketchObject] Sketch009  label="Fan003"
  ArcFitTolerance = 0
  AttachmentOffset = pos=(3,-6,0) rot=(0,0,1;0rad)
  AttachmentSupport = -> [YZ_Plane069]
  FullyConstrained = true
  MakeInternals = false
  MapMode = 5
  Placement = pos=(0,3,-6) rot=(0.57735,0.57735,0.57735;2.0944rad)
  sketch-geometry (11):
    g0: LineSegment [constr] StartX=173.5 StartY=41.6 StartZ=0 EndX=133.5 EndY=41.6 EndZ=0
    g1: LineSegment [constr] StartX=133.5 StartY=41.6 StartZ=0 EndX=133.5 EndY=1.6 EndZ=0
    g2: LineSegment [constr] StartX=133.5 StartY=1.6 StartZ=0 EndX=173.5 EndY=1.6 EndZ=0
    g3: LineSegment [constr] StartX=173.5 StartY=1.6 StartZ=0 EndX=173.5 EndY=41.6 EndZ=0
    g4: Circle CenterX=173.5 CenterY=41.6 CenterZ=0 NormalX=0 NormalY=0 NormalZ=1 AngleXU=0 Radius=2
    g5: Circle CenterX=133.5 CenterY=41.6 CenterZ=0 NormalX=0 NormalY=0 NormalZ=1 AngleXU=0 Radius=2
    g6: Circle CenterX=133.5 CenterY=1.6 CenterZ=0 NormalX=0 NormalY=0 NormalZ=1 AngleXU=0 Radius=2
    g7: Circle CenterX=173.5 CenterY=1.6 CenterZ=0 NormalX=0 NormalY=0 NormalZ=1 AngleXU=0 Radius=2
    g8: Circle CenterX=153.5 CenterY=21.6 CenterZ=0 NormalX=0 NormalY=0 NormalZ=1 AngleXU=0 Radius=24
    g9: LineSegment [constr] StartX=153.5 StartY=21.6 StartZ=0 EndX=153.5 EndY=41.6 EndZ=0
    g10: LineSegment [constr] StartX=153.5 StartY=21.6 StartZ=0 EndX=153.5 EndY=1.6 EndZ=0
  constraints (28):
    c: Coincident(g0,g1)
    c: Coincident(g1,g2)
    c: Coincident(g2,g3)
    c: Coincident(g3,g0)
    c: Horizontal(g0)
    c: Horizontal(g2)
    c: Vertical(g1)
    c: Vertical(g3)
    c: Equal(g1,g2)
    c: Coincident(g4,g0)
    c: Coincident(g5,g0)
    c: Coincident(g6,g1)
    c: Coincident(g7,g2)
    c: Equal(g7,g6)
    c: Equal(g6,g5)
    c: Equal(g5,g4)
    c: Diameter(g6) = 4
    c: Coincident(g9,g8)
    c: Vertical(g9)
    c: Symmetric(g5,g4,g9)
    c: Diameter(g8) = 48
    c: Coincident(g10,g8)
    c: PointOnObject(g10,g2)
    c: Vertical(g10)
    c: Equal(g10,g9)
    c: Distance(g0) = 40
    c: DistanceX(g7) = 173.5
    c: DistanceY(g7) = 1.6
FEATURE [App::Link] C303_C_0805_2012Metric_1d86ef2bb22f_ln_  label="C26_C_0805_2012Metric_d5dbb9e88231"
  LinkPlacement = pos=(114.7,21.1,0) rot=(0,0,-1;1.5708rad)
  LinkedObject = -> Shape139
  Placement = pos=(114.7,21.1,0) rot=(0,0,-1;1.5708rad)
FEATURE [App::Link] C303_C_0805_2012Metric_1d86ef2bb22f_ln_001  label="C23_C_0805_2012Metric_000a25718fd3"
  LinkPlacement = pos=(127.75,16.625,0) rot=(0,0,1;1.5708rad)
  LinkedObject = -> Shape139
  Placement = pos=(127.75,16.625,0) rot=(0,0,1;1.5708rad)
FEATURE [App::Link] C303_C_0805_2012Metric_1d86ef2bb22f_ln_002  label="C311_C_0805_2012Metric_e7a3c8a1d566"
  LinkPlacement = pos=(69.6,18.85,0) rot=(0,0,1;1.5708rad)
  LinkedObject = -> Shape139
  Placement = pos=(69.6,18.85,0) rot=(0,0,1;1.5708rad)
FEATURE [App::Link] C303_C_0805_2012Metric_1d86ef2bb22f_ln_003  label="C211_C_0805_2012Metric_f6e2775f9a28"
  LinkPlacement = pos=(103.35,92.55,0) rot=(0,0,1;1.5708rad)
  LinkedObject = -> Shape139
  Placement = pos=(103.35,92.55,0) rot=(0,0,1;1.5708rad)
FEATURE [App::Link] C303_C_0805_2012Metric_1d86ef2bb22f_ln_004  label="C13_C_0805_2012Metric_584e764d642c"
  LinkPlacement = pos=(42.45,2.35,0) rot=(0,0,1;1.5708rad)
  LinkedObject = -> Shape139
  Placement = pos=(42.45,2.35,0) rot=(0,0,1;1.5708rad)
FEATURE [App::Link] C303_C_0805_2012Metric_1d86ef2bb22f_ln_005  label="C49_C_0805_2012Metric_974e61c4247c001"
  LinkPlacement = pos=(99.8,39.3625,0) rot=(0,0,1;1.5708rad)
  LinkedObject = -> Shape139
  Placement = pos=(99.8,39.3625,0) rot=(0,0,1;1.5708rad)
FEATURE [App::Link] C303_C_0805_2012Metric_1d86ef2bb22f_ln_006  label="C309_C_0805_2012Metric_4bea97f5e1ff"
  LinkPlacement = pos=(85.7125,21.575,0) rot=(0,0,-1;1.5708rad)
  LinkedObject = -> Shape139
  Placement = pos=(85.7125,21.575,0) rot=(0,0,-1;1.5708rad)
FEATURE [App::Link] C303_C_0805_2012Metric_1d86ef2bb22f_ln_185  label="C38_C_0805_2012Metric_d30376c11af6"
  LinkPlacement = pos=(135.55,33.075,0) rot=(0,0,1;0rad)
  LinkedObject = -> Shape139
  Placement = pos=(135.55,33.075,0) rot=(0,0,1;0rad)
FEATURE [App::Link] C303_C_0805_2012Metric_1d86ef2bb22f_ln_008  label="C223_C_0805_2012Metric_fc6fab0a5f9d"
  LinkPlacement = pos=(175,91.5,0) rot=(0,0,1;1.5708rad)
  LinkedObject = -> Shape139
  Placement = pos=(175,91.5,0) rot=(0,0,1;1.5708rad)
FEATURE [App::Link] C303_C_0805_2012Metric_1d86ef2bb22f_ln_009  label="C504_C_0805_2012Metric_f896a043f44d"
  LinkPlacement = pos=(101.25,30.175,0) rot=(0,0,1;1.5708rad)
  LinkedObject = -> Shape139
  Placement = pos=(101.25,30.175,0) rot=(0,0,1;1.5708rad)
FEATURE [App::Link] C303_C_0805_2012Metric_1d86ef2bb22f_ln_010  label="C226_C_0805_2012Metric_2eb8bf28e24e"
  LinkPlacement = pos=(117.6,45.9,0) rot=(0,0,1;0rad)
  LinkedObject = -> Shape139
  Placement = pos=(117.6,45.9,0) rot=(0,0,1;0rad)
FEATURE [App::Link] C303_C_0805_2012Metric_1d86ef2bb22f_ln_011  label="C214_C_0805_2012Metric_e2b81b34a7d2"
  LinkPlacement = pos=(51.9,45.5,0) rot=(0,0,1;3.14159rad)
  LinkedObject = -> Shape139
  Placement = pos=(51.9,45.5,0) rot=(0,0,1;3.14159rad)
FEATURE [App::Link] C303_C_0805_2012Metric_1d86ef2bb22f_ln_012  label="C221_C_0805_2012Metric_b44e2667bcf7"
  LinkPlacement = pos=(165.5,5.5,0) rot=(0,0,1;1.5708rad)
  LinkedObject = -> Shape139
  Placement = pos=(165.5,5.5,0) rot=(0,0,1;1.5708rad)
FEATURE [App::Link] C303_C_0805_2012Metric_1d86ef2bb22f_ln_013  label="C209_C_0805_2012Metric_f79f18431d03"
  LinkPlacement = pos=(114.35,91.65,0) rot=(0,0,1;1.5708rad)
  LinkedObject = -> Shape139
  Placement = pos=(114.35,91.65,0) rot=(0,0,1;1.5708rad)
FEATURE [App::Link] C303_C_0805_2012Metric_1d86ef2bb22f_ln_014  label="C205_C_0805_2012Metric_92a2149bb90f"
  LinkPlacement = pos=(60.2,50.5,0) rot=(0,0,1;1.5708rad)
  LinkedObject = -> Shape139
  Placement = pos=(60.2,50.5,0) rot=(0,0,1;1.5708rad)
FEATURE [App::Link] C303_C_0805_2012Metric_1d86ef2bb22f_ln_015  label="C29_C_0805_2012Metric_fa1848d19678"
  LinkPlacement = pos=(138.375,38.725,0) rot=(0,0,1;0rad)
  LinkedObject = -> Shape139
  Placement = pos=(138.375,38.725,0) rot=(0,0,1;0rad)
FEATURE [App::Link] C303_C_0805_2012Metric_1d86ef2bb22f_ln_016  label="C505_C_0805_2012Metric_bcf27ea4bc10"
  LinkPlacement = pos=(113.225,27.5,0) rot=(0,0,-1;1.5708rad)
  LinkedObject = -> Shape139
  Placement = pos=(113.225,27.5,0) rot=(0,0,-1;1.5708rad)
FEATURE [App::Link] C303_C_0805_2012Metric_1d86ef2bb22f_ln_017  label="C19_C_0805_2012Metric_5594ae341427"
  LinkPlacement = pos=(115.725,25.05,0) rot=(0,0,1;1.5708rad)
  LinkedObject = -> Shape139
  Placement = pos=(115.725,25.05,0) rot=(0,0,1;1.5708rad)
FEATURE [App::Link] C303_C_0805_2012Metric_1d86ef2bb22f_ln_018  label="C217_C_0805_2012Metric_6c92b5ed4840"
  LinkPlacement = pos=(183.3,31.7,0) rot=(0,0,1;1.5708rad)
  LinkedObject = -> Shape139
  Placement = pos=(183.3,31.7,0) rot=(0,0,1;1.5708rad)
FEATURE [App::Link] C303_C_0805_2012Metric_1d86ef2bb22f_ln_019  label="C316_C_0805_2012Metric_cd1ffc8391ec"
  LinkPlacement = pos=(72.687,27.995,0) rot=(0,0,1;3.14159rad)
  LinkedObject = -> Shape139
  Placement = pos=(72.687,27.995,0) rot=(0,0,1;3.14159rad)
FEATURE [App::Link] C303_C_0805_2012Metric_1d86ef2bb22f_ln_020  label="C225_C_0805_2012Metric_ffd9329e2dcc"
  LinkPlacement = pos=(161.69,92.5,0) rot=(0,0,1;3.14159rad)
  LinkedObject = -> Shape139
  Placement = pos=(161.69,92.5,0) rot=(0,0,1;3.14159rad)
FEATURE [App::Link] C303_C_0805_2012Metric_1d86ef2bb22f_ln_021  label="C35_C_0805_2012Metric_ffb163dd22d3"
  LinkPlacement = pos=(145.625,33.725,0) rot=(0,0,1;3.14159rad)
  LinkedObject = -> Shape139
  Placement = pos=(145.625,33.725,0) rot=(0,0,1;3.14159rad)
FEATURE [App::Link] C303_C_0805_2012Metric_1d86ef2bb22f_ln_022  label="C52_C_0805_2012Metric_ac194752d0a002"
  LinkPlacement = pos=(80.2,36.8,0) rot=(0,0,1;3.14159rad)
  LinkedObject = -> Shape139
  Placement = pos=(80.2,36.8,0) rot=(0,0,1;3.14159rad)
FEATURE [App::Link] C303_C_0805_2012Metric_1d86ef2bb22f_ln_023  label="C404_C_0805_2012Metric_dd9989736422"
  LinkPlacement = pos=(105.09,9.575,0) rot=(0,0,1;3.14159rad)
  LinkedObject = -> Shape139
  Placement = pos=(105.09,9.575,0) rot=(0,0,1;3.14159rad)
FEATURE [App::Link] C303_C_0805_2012Metric_1d86ef2bb22f_ln_024  label="C27_C_0805_2012Metric_c813a18685a9"
  LinkPlacement = pos=(114.85,12.65,0) rot=(0,0,-1;1.5708rad)
  LinkedObject = -> Shape139
  Placement = pos=(114.85,12.65,0) rot=(0,0,-1;1.5708rad)
FEATURE [App::Link] C303_C_0805_2012Metric_1d86ef2bb22f_ln_025  label="C222_C_0805_2012Metric_211188bab274"
  LinkPlacement = pos=(165.438,13.5,0) rot=(0,0,1;1.5708rad)
  LinkedObject = -> Shape139
  Placement = pos=(165.438,13.5,0) rot=(0,0,1;1.5708rad)
FEATURE [App::Link] C303_C_0805_2012Metric_1d86ef2bb22f_ln_026  label="C1_C_0805_2012Metric_e1adf31e506d"
  LinkPlacement = pos=(107.075,36.85,0) rot=(0,0,1;3.14159rad)
  LinkedObject = -> Shape139
  Placement = pos=(107.075,36.85,0) rot=(0,0,1;3.14159rad)
FEATURE [App::Link] C303_C_0805_2012Metric_1d86ef2bb22f_ln_027  label="C207_C_0805_2012Metric_e7225891546f"
  LinkPlacement = pos=(171.545,23.4584,0) rot=(0,0,1;1.5708rad)
  LinkedObject = -> Shape139
  Placement = pos=(171.545,23.4584,0) rot=(0,0,1;1.5708rad)
FEATURE [App::Link] C303_C_0805_2012Metric_1d86ef2bb22f_ln_028  label="C315_C_0805_2012Metric_75f11421f158"
  LinkPlacement = pos=(120.231,38.4938,0) rot=(0,0,-1;1.5708rad)
  LinkedObject = -> Shape139
  Placement = pos=(120.231,38.4938,0) rot=(0,0,-1;1.5708rad)
FEATURE [App::Link] C303_C_0805_2012Metric_1d86ef2bb22f_ln_029  label="C2_C_0805_2012Metric_05101afe5803"
  LinkPlacement = pos=(118.85,34.6,0) rot=(0,0,1;3.14159rad)
  LinkedObject = -> Shape139
  Placement = pos=(118.85,34.6,0) rot=(0,0,1;3.14159rad)
FEATURE [App::Link] C303_C_0805_2012Metric_1d86ef2bb22f_ln_030  label="C24_C_0805_2012Metric_9756039021d9"
  LinkPlacement = pos=(127.8,23.325,0) rot=(0,0,1;1.5708rad)
  LinkedObject = -> Shape139
  Placement = pos=(127.8,23.325,0) rot=(0,0,1;1.5708rad)
FEATURE [App::Link] C303_C_0805_2012Metric_1d86ef2bb22f_ln_031  label="C305_C_0805_2012Metric_8cc8a682d547"
  LinkPlacement = pos=(52,26.85,0) rot=(0,0,1;1.5708rad)
  LinkedObject = -> Shape139
  Placement = pos=(52,26.85,0) rot=(0,0,1;1.5708rad)
FEATURE [App::Link] C303_C_0805_2012Metric_1d86ef2bb22f_ln_032  label="C215_C_0805_2012Metric_46fa3c3d31ac"
  LinkPlacement = pos=(163.5,88,0) rot=(0,0,1;1.5708rad)
  LinkedObject = -> Shape139
  Placement = pos=(163.5,88,0) rot=(0,0,1;1.5708rad)
FEATURE [App::Link] C303_C_0805_2012Metric_1d86ef2bb22f_ln_033  label="C407_C_0805_2012Metric_fedbb3076932"
  LinkPlacement = pos=(53.45,36.2,0) rot=(0,0,1;3.14159rad)
  LinkedObject = -> Shape139
  Placement = pos=(53.45,36.2,0) rot=(0,0,1;3.14159rad)
FEATURE [App::Link] C303_C_0805_2012Metric_1d86ef2bb22f_ln_034  label="C51_C_0805_2012Metric_83d383f6edd008"
  LinkPlacement = pos=(65.4,39.6,0) rot=(0,0,1;0rad)
  LinkedObject = -> Shape139
  Placement = pos=(65.4,39.6,0) rot=(0,0,1;0rad)
FEATURE [App::Link] C303_C_0805_2012Metric_1d86ef2bb22f_ln_035  label="C54_C_0805_2012Metric_413553e36d7c001"
  LinkPlacement = pos=(84.4,44,0) rot=(0,0,1;0rad)
  LinkedObject = -> Shape139
  Placement = pos=(84.4,44,0) rot=(0,0,1;0rad)
FEATURE [App::Link] C303_C_0805_2012Metric_1d86ef2bb22f_ln_036  label="C313_C_0805_2012Metric_612cf4179c1d"
  LinkPlacement = pos=(56.55,17.875,0) rot=(0,0,1;3.14159rad)
  LinkedObject = -> Shape139
  Placement = pos=(56.55,17.875,0) rot=(0,0,1;3.14159rad)
FEATURE [App::Link] C303_C_0805_2012Metric_1d86ef2bb22f_ln_186  label="C28_C_0805_2012Metric_180589c75c29"
  LinkPlacement = pos=(116.75,21.075,0) rot=(0,0,-1;1.5708rad)
  LinkedObject = -> Shape139
  Placement = pos=(116.75,21.075,0) rot=(0,0,-1;1.5708rad)
FEATURE [App::Link] C303_C_0805_2012Metric_1d86ef2bb22f_ln_038  label="C314_C_0805_2012Metric_20f103a6412f"
  LinkPlacement = pos=(56.775,26.55,0) rot=(0,0,1;0rad)
  LinkedObject = -> Shape139
  Placement = pos=(56.775,26.55,0) rot=(0,0,1;0rad)
FEATURE [App::Link] C303_C_0805_2012Metric_1d86ef2bb22f_ln_039  label="C218_C_0805_2012Metric_5d7354e4fb6b"
  LinkPlacement = pos=(183.3,23.7,0) rot=(0,0,1;1.5708rad)
  LinkedObject = -> Shape139
  Placement = pos=(183.3,23.7,0) rot=(0,0,1;1.5708rad)
FEATURE [App::Link] C303_C_0805_2012Metric_1d86ef2bb22f_ln_040  label="C11_C_0805_2012Metric_48f704f1522c"
  LinkPlacement = pos=(110.45,20.925,0) rot=(0,0,1;1.5708rad)
  LinkedObject = -> Shape139
  Placement = pos=(110.45,20.925,0) rot=(0,0,1;1.5708rad)
FEATURE [App::Link] C303_C_0805_2012Metric_1d86ef2bb22f_ln_041  label="C401_C_0805_2012Metric_e86e7a8ffe25"
  LinkPlacement = pos=(57.5,36.2,0) rot=(0,0,1;0rad)
  LinkedObject = -> Shape139
  Placement = pos=(57.5,36.2,0) rot=(0,0,1;0rad)
FEATURE [App::Link] C303_C_0805_2012Metric_1d86ef2bb22f_ln_042  label="C216_C_0805_2012Metric_21734a4147f4"
  LinkPlacement = pos=(170,93.5,0) rot=(0,0,1;3.14159rad)
  LinkedObject = -> Shape139
  Placement = pos=(170,93.5,0) rot=(0,0,1;3.14159rad)
FEATURE [App::Link] C303_C_0805_2012Metric_1d86ef2bb22f_ln_043  label="C22_C_0805_2012Metric_4bb9130e18a2"
  LinkPlacement = pos=(114.9,16.9,0) rot=(0,0,1;1.5708rad)
  LinkedObject = -> Shape139
  Placement = pos=(114.9,16.9,0) rot=(0,0,1;1.5708rad)
FEATURE [App::Link] C303_C_0805_2012Metric_1d86ef2bb22f_ln_044  label="C43_C_0805_2012Metric_6d7e732d062c"
  LinkPlacement = pos=(141.725,33.725,0) rot=(0,0,1;3.14159rad)
  LinkedObject = -> Shape139
  Placement = pos=(141.725,33.725,0) rot=(0,0,1;3.14159rad)
FEATURE [App::Link] C303_C_0805_2012Metric_1d86ef2bb22f_ln_045  label="C208_C_0805_2012Metric_e46bcdf7084c"
  LinkPlacement = pos=(171.545,31.5356,0) rot=(0,0,1;1.5708rad)
  LinkedObject = -> Shape139
  Placement = pos=(171.545,31.5356,0) rot=(0,0,1;1.5708rad)
FEATURE [App::Link] C303_C_0805_2012Metric_1d86ef2bb22f_ln_046  label="C44_C_0805_2012Metric_ee162983a6f5"
  LinkPlacement = pos=(144.025,17.225,0) rot=(0,0,1;1.5708rad)
  LinkedObject = -> Shape139
  Placement = pos=(144.025,17.225,0) rot=(0,0,1;1.5708rad)
FEATURE [App::Link] C303_C_0805_2012Metric_1d86ef2bb22f_ln_047  label="C47_C_0805_2012Metric_5ea36896183c001"
  LinkPlacement = pos=(94.3,35.6,0) rot=(0,0,1;1.5708rad)
  LinkedObject = -> Shape139
  Placement = pos=(94.3,35.6,0) rot=(0,0,1;1.5708rad)
FEATURE [App::Link] C303_C_0805_2012Metric_1d86ef2bb22f_ln_048  label="C502_C_0805_2012Metric_bafe37840d84"
  LinkPlacement = pos=(101.25,26.6,0) rot=(0,0,1;1.5708rad)
  LinkedObject = -> Shape139
  Placement = pos=(101.25,26.6,0) rot=(0,0,1;1.5708rad)
FEATURE [App::Link] C303_C_0805_2012Metric_1d86ef2bb22f_ln_187  label="C213_C_0805_2012Metric_9d17bd507aac"
  LinkPlacement = pos=(116.6,87.8,0) rot=(0,0,-1;1.5708rad)
  LinkedObject = -> Shape139
  Placement = pos=(116.6,87.8,0) rot=(0,0,-1;1.5708rad)
FEATURE [App::Link] C303_C_0805_2012Metric_1d86ef2bb22f_ln_050  label="C220_C_0805_2012Metric_c961a865a416"
  LinkPlacement = pos=(106.929,45.08,0) rot=(0,0,1;0rad)
  LinkedObject = -> Shape139
  Placement = pos=(106.929,45.08,0) rot=(0,0,1;0rad)
FEATURE [App::Link] C303_C_0805_2012Metric_1d86ef2bb22f_ln_051  label="C45_C_0805_2012Metric_5ed4bf02781a"
  LinkPlacement = pos=(141.95,13.775,0) rot=(0,0,-1;1.5708rad)
  LinkedObject = -> Shape139
  Placement = pos=(141.95,13.775,0) rot=(0,0,-1;1.5708rad)
FEATURE [App::Link] C303_C_0805_2012Metric_1d86ef2bb22f_ln_052  label="C12_C_0805_2012Metric_390cc82b5c76"
  LinkPlacement = pos=(110.45,17.33,0) rot=(0,0,-1;1.5708rad)
  LinkedObject = -> Shape139
  Placement = pos=(110.45,17.33,0) rot=(0,0,-1;1.5708rad)
FEATURE [App::Link] C303_C_0805_2012Metric_1d86ef2bb22f_ln_053  label="C227_C_0805_2012Metric_cabb4cdcbf12"
  LinkPlacement = pos=(175,87.5,0) rot=(0,0,-1;1.5708rad)
  LinkedObject = -> Shape139
  Placement = pos=(175,87.5,0) rot=(0,0,-1;1.5708rad)
FEATURE [App::Link] C303_C_0805_2012Metric_1d86ef2bb22f_ln_054  label="C206_C_0805_2012Metric_59b2e2985f92"
  LinkPlacement = pos=(47.5,48.7,0) rot=(0,0,1;3.14159rad)
  LinkedObject = -> Shape139
  Placement = pos=(47.5,48.7,0) rot=(0,0,1;3.14159rad)
FEATURE [App::Link] C303_C_0805_2012Metric_1d86ef2bb22f_ln_055  label="C37_C_0805_2012Metric_2f8f93623fdd"
  LinkPlacement = pos=(150.65,26.0125,0) rot=(0,0,1;1.5708rad)
  LinkedObject = -> Shape139
  Placement = pos=(150.65,26.0125,0) rot=(0,0,1;1.5708rad)
FEATURE [App::Link] C303_C_0805_2012Metric_1d86ef2bb22f_ln_056  label="C219_C_0805_2012Metric_1120eae39658"
  LinkPlacement = pos=(113.429,48.58,0) rot=(0,0,1;1.5708rad)
  LinkedObject = -> Shape139
  Placement = pos=(113.429,48.58,0) rot=(0,0,1;1.5708rad)
FEATURE [App::Link] C303_C_0805_2012Metric_1d86ef2bb22f_ln_057  label="C203_C_0805_2012Metric_dba0b3a855a7"
  LinkPlacement = pos=(177.565,5.399,0) rot=(0,0,1;1.5708rad)
  LinkedObject = -> Shape139
  Placement = pos=(177.565,5.399,0) rot=(0,0,1;1.5708rad)
FEATURE [App::Link] C303_C_0805_2012Metric_1d86ef2bb22f_ln_058  label="C39_C_0805_2012Metric_7a4cbeef3a33"
  LinkPlacement = pos=(130.175,31.575,0) rot=(0,0,-1;1.5708rad)
  LinkedObject = -> Shape139
  Placement = pos=(130.175,31.575,0) rot=(0,0,-1;1.5708rad)
FEATURE [App::Link] C303_C_0805_2012Metric_1d86ef2bb22f_ln_059  label="C21_C_0805_2012Metric_01105218e7e6"
  LinkPlacement = pos=(117.8,25.05,0) rot=(0,0,1;1.5708rad)
  LinkedObject = -> Shape139
  Placement = pos=(117.8,25.05,0) rot=(0,0,1;1.5708rad)
FEATURE [App::Link] C303_C_0805_2012Metric_1d86ef2bb22f_ln_060  label="C501_C_0805_2012Metric_228dc7cb5e5d"
  LinkPlacement = pos=(111.1,31.9,0) rot=(0,0,1;1.5708rad)
  LinkedObject = -> Shape139
  Placement = pos=(111.1,31.9,0) rot=(0,0,1;1.5708rad)
FEATURE [App::Link] C303_C_0805_2012Metric_1d86ef2bb22f_ln_061  label="C503_C_0805_2012Metric_16dcb8b1dc44"
  LinkPlacement = pos=(107.075,16.05,0) rot=(0,0,1;3.14159rad)
  LinkedObject = -> Shape139
  Placement = pos=(107.075,16.05,0) rot=(0,0,1;3.14159rad)
FEATURE [App::Link] C303_C_0805_2012Metric_1d86ef2bb22f_ln_062  label="C307_C_0805_2012Metric_ef573f1286a4"
  LinkPlacement = pos=(153.839,29.544,0) rot=(0,0,-1;1.5708rad)
  LinkedObject = -> Shape139
  Placement = pos=(153.839,29.544,0) rot=(0,0,-1;1.5708rad)
FEATURE [App::Link] C303_C_0805_2012Metric_1d86ef2bb22f_ln_063  label="C312_C_0805_2012Metric_204514eca08f"
  LinkPlacement = pos=(67.2,22.35,0) rot=(0,0,1;1.5708rad)
  LinkedObject = -> Shape139
  Placement = pos=(67.2,22.35,0) rot=(0,0,1;1.5708rad)
FEATURE [App::Link] C303_C_0805_2012Metric_1d86ef2bb22f_ln_064  label="C10_C_0805_2012Metric_f6a3d44cf72c"
  LinkPlacement = pos=(100.7,19.225,0) rot=(0,0,-1;1.5708rad)
  LinkedObject = -> Shape139
  Placement = pos=(100.7,19.225,0) rot=(0,0,-1;1.5708rad)
FEATURE [App::Link] C303_C_0805_2012Metric_1d86ef2bb22f_ln_065  label="C308_C_0805_2012Metric_86bc2e49f05b"
  LinkPlacement = pos=(156.024,22.178,0) rot=(0,0,1;3.14159rad)
  LinkedObject = -> Shape139
  Placement = pos=(156.024,22.178,0) rot=(0,0,1;3.14159rad)
FEATURE [App::Link] C303_C_0805_2012Metric_1d86ef2bb22f_ln_066  label="C48_C_0805_2012Metric_3d6e9560ce050"
  LinkPlacement = pos=(92.8,39.4,0) rot=(0,0,-1;1.5708rad)
  LinkedObject = -> Shape139
  Placement = pos=(92.8,39.4,0) rot=(0,0,-1;1.5708rad)
FEATURE [App::Link] C303_C_0805_2012Metric_1d86ef2bb22f_ln_067  label="C40_C_0805_2012Metric_aa59399f450c"
  LinkPlacement = pos=(141.637,25.3125,0) rot=(0,0,1;3.14159rad)
  LinkedObject = -> Shape139
  Placement = pos=(141.637,25.3125,0) rot=(0,0,1;3.14159rad)
FEATURE [App::Link] C303_C_0805_2012Metric_1d86ef2bb22f_ln_188  label="C212_C_0805_2012Metric_ff8aa67397a9"
  LinkPlacement = pos=(55.9,45.7,0) rot=(0,0,1;0rad)
  LinkedObject = -> Shape139
  Placement = pos=(55.9,45.7,0) rot=(0,0,1;0rad)
FEATURE [App::Link] C303_C_0805_2012Metric_1d86ef2bb22f_ln_069  label="C210_C_0805_2012Metric_6be0f132b8e7"
  LinkPlacement = pos=(47.5,50.8,0) rot=(0,0,1;0rad)
  LinkedObject = -> Shape139
  Placement = pos=(47.5,50.8,0) rot=(0,0,1;0rad)
FEATURE [App::Link] C303_C_0805_2012Metric_1d86ef2bb22f_ln_070  label="C20_C_0805_2012Metric_5e1706738730"
  LinkPlacement = pos=(117,16.9,0) rot=(0,0,1;1.5708rad)
  LinkedObject = -> Shape139
  Placement = pos=(117,16.9,0) rot=(0,0,1;1.5708rad)
FEATURE [App::Link] C303_C_0805_2012Metric_1d86ef2bb22f_ln_071  label="C310_C_0805_2012Metric_490b81cdc351"
  LinkPlacement = pos=(52.825,21,0) rot=(0,0,1;0rad)
  LinkedObject = -> Shape139
  Placement = pos=(52.825,21,0) rot=(0,0,1;0rad)
FEATURE [App::Link] C303_C_0805_2012Metric_1d86ef2bb22f_ln_072  label="C42_C_0805_2012Metric_4eb63d81472c"
  LinkPlacement = pos=(143.675,22.15,0) rot=(0,0,-1;1.5708rad)
  LinkedObject = -> Shape139
  Placement = pos=(143.675,22.15,0) rot=(0,0,-1;1.5708rad)
FEATURE [App::Link] C303_C_0805_2012Metric_1d86ef2bb22f_ln_073  label="C306_C_0805_2012Metric_f55fe554345e"
  LinkPlacement = pos=(51.95,32,0) rot=(0,0,1;1.5708rad)
  LinkedObject = -> Shape139
  Placement = pos=(51.95,32,0) rot=(0,0,1;1.5708rad)
FEATURE [App::Link] C303_C_0805_2012Metric_1d86ef2bb22f_ln_074  label="C34_C_0805_2012Metric_faa94f78bcbd"
  LinkPlacement = pos=(144.275,40.1,0) rot=(0,0,1;3.14159rad)
  LinkedObject = -> Shape139
  Placement = pos=(144.275,40.1,0) rot=(0,0,1;3.14159rad)
FEATURE [App::Link] C303_C_0805_2012Metric_1d86ef2bb22f_ln_075  label="C50_C_0805_2012Metric_12a32574f718"
  LinkPlacement = pos=(72.6,38.2,0) rot=(0,0,1;1.5708rad)
  LinkedObject = -> Shape139
  Placement = pos=(72.6,38.2,0) rot=(0,0,1;1.5708rad)
FEATURE [App::Link] C303_C_0805_2012Metric_1d86ef2bb22f_ln_076  label="C18_C_0805_2012Metric_c6e5c3101df8"
  LinkPlacement = pos=(117.475,2.725,0) rot=(0,0,1;0rad)
  LinkedObject = -> Shape139
  Placement = pos=(117.475,2.725,0) rot=(0,0,1;0rad)
FEATURE [App::Link] C303_C_0805_2012Metric_1d86ef2bb22f_ln_189  label="C41_C_0805_2012Metric_23af0ccbd41e"
  LinkPlacement = pos=(137.738,25.3125,0) rot=(0,0,1;0rad)
  LinkedObject = -> Shape139
  Placement = pos=(137.738,25.3125,0) rot=(0,0,1;0rad)
FEATURE [App::Link] C303_C_0805_2012Metric_1d86ef2bb22f_ln_078  label="C228_C_0805_2012Metric_db3eaee78163"
  LinkPlacement = pos=(110.929,45.08,0) rot=(0,0,1;0rad)
  LinkedObject = -> Shape139
  Placement = pos=(110.929,45.08,0) rot=(0,0,1;0rad)
FEATURE [App::Link] C303_C_0805_2012Metric_1d86ef2bb22f_ln_079  label="C202_C_0805_2012Metric_d255fea7448e"
  LinkPlacement = pos=(110.25,93.45,0) rot=(0,0,1;3.14159rad)
  LinkedObject = -> Shape139
  Placement = pos=(110.25,93.45,0) rot=(0,0,1;3.14159rad)
FEATURE [App::Link] C303_C_0805_2012Metric_1d86ef2bb22f_ln_080  label="C405_C_0805_2012Metric_7b2220de55d5"
  LinkPlacement = pos=(128.325,2.6,0) rot=(0,0,-1;1.5708rad)
  LinkedObject = -> Shape139
  Placement = pos=(128.325,2.6,0) rot=(0,0,-1;1.5708rad)
FEATURE [App::Link] C303_C_0805_2012Metric_1d86ef2bb22f_ln_081  label="C304_C_0805_2012Metric_d3558c6d708f"
  LinkPlacement = pos=(92.1,27.376,0) rot=(0,0,1;3.14159rad)
  LinkedObject = -> Shape139
  Placement = pos=(92.1,27.376,0) rot=(0,0,1;3.14159rad)
FEATURE [App::Link] C303_C_0805_2012Metric_1d86ef2bb22f_ln_082  label="C406_C_0805_2012Metric_f1b2804f82f8"
  LinkPlacement = pos=(61.625,41.675,0) rot=(0,0,-1;1.5708rad)
  LinkedObject = -> Shape139
  Placement = pos=(61.625,41.675,0) rot=(0,0,-1;1.5708rad)
FEATURE [App::Link] C303_C_0805_2012Metric_1d86ef2bb22f_ln_083  label="C36_C_0805_2012Metric_3d0ec07c9d2c"
  LinkPlacement = pos=(147.175,24.2375,0) rot=(0,0,1;0rad)
  LinkedObject = -> Shape139
  Placement = pos=(147.175,24.2375,0) rot=(0,0,1;0rad)
FEATURE [App::Link] C303_C_0805_2012Metric_1d86ef2bb22f_ln_084  label="C53_C_0805_2012Metric_0b477a83f041"
  LinkPlacement = pos=(80.2,39.2,0) rot=(0,0,1;3.14159rad)
  LinkedObject = -> Shape139
  Placement = pos=(80.2,39.2,0) rot=(0,0,1;3.14159rad)
FEATURE [App::Link] C303_C_0805_2012Metric_1d86ef2bb22f_ln_085  label="C224_C_0805_2012Metric_f777ef533c5e"
  LinkPlacement = pos=(103.015,49.8,0) rot=(0,0,-1;1.5708rad)
  LinkedObject = -> Shape139
  Placement = pos=(103.015,49.8,0) rot=(0,0,-1;1.5708rad)
FEATURE [App::Link] C303_C_0805_2012Metric_1d86ef2bb22f_ln_086  label="C302_C_0805_2012Metric_95746b57ac45"
  LinkPlacement = pos=(108.2,34.2,0) rot=(0,0,1;3.14159rad)
  LinkedObject = -> Shape139
  Placement = pos=(108.2,34.2,0) rot=(0,0,1;3.14159rad)
FEATURE [App::Link] C303_C_0805_2012Metric_1d86ef2bb22f_ln_087  label="C301_C_0805_2012Metric_27f5d4edfcf4"
  LinkPlacement = pos=(116.6,42.175,0) rot=(0,0,1;3.14159rad)
  LinkedObject = -> Shape139
  Placement = pos=(116.6,42.175,0) rot=(0,0,1;3.14159rad)
FEATURE [App::Link] C303_C_0805_2012Metric_1d86ef2bb22f_ln_088  label="C204_C_0805_2012Metric_93e9081341c4"
  LinkPlacement = pos=(177.59,13.4508,0) rot=(0,0,1;1.5708rad)
  LinkedObject = -> Shape139
  Placement = pos=(177.59,13.4508,0) rot=(0,0,1;1.5708rad)
FEATURE [App::Link] C303_C_0805_2012Metric_1d86ef2bb22f_ln_089  label="C201_C_0805_2012Metric_3c6c4e562b76"
  LinkPlacement = pos=(103.9,87.55,0) rot=(0,0,1;1.5708rad)
  LinkedObject = -> Shape139
  Placement = pos=(103.9,87.55,0) rot=(0,0,1;1.5708rad)
FEATURE [App::Link] C303_C_0805_2012Metric_1d86ef2bb22f_ln_090  label="C25_C_0805_2012Metric_a8b56f256ab6"
  LinkPlacement = pos=(117.025,12.65,0) rot=(0,0,-1;1.5708rad)
  LinkedObject = -> Shape139
  Placement = pos=(117.025,12.65,0) rot=(0,0,-1;1.5708rad)
FEATURE [App::Link] C303_C_0805_2012Metric_1d86ef2bb22f_ln_091  label="C402_C_0805_2012Metric_2602be6c4c99"
  LinkPlacement = pos=(125.1,7.25,0) rot=(0,0,1;0rad)
  LinkedObject = -> Shape139
  Placement = pos=(125.1,7.25,0) rot=(0,0,1;0rad)
FEATURE [App::Link] C303_C_0805_2012Metric_1d86ef2bb22f_ln_092  label="C32_C_0805_2012Metric_6c00573259a6"
  LinkPlacement = pos=(138.375,35.925,0) rot=(0,0,1;0rad)
  LinkedObject = -> Shape139
  Placement = pos=(138.375,35.925,0) rot=(0,0,1;0rad)
FEATURE [App::Link] D208_D_MiniMELF_Standard_5646c313d2d3_ln_  label="D301_D_MiniMELF_Standard_dd8a013c1899"
  LinkPlacement = pos=(109.025,42.1,0) rot=(0,0,1;3.14159rad)
  LinkedObject = -> Shape146
  Placement = pos=(109.025,42.1,0) rot=(0,0,1;3.14159rad)
FEATURE [App::Link] D208_D_MiniMELF_Standard_5646c313d2d3_ln_001  label="D202_D_MiniMELF_Standard_af40c77ecb95"
  LinkPlacement = pos=(71.2,51.5,0) rot=(0,0,1;1.5708rad)
  LinkedObject = -> Shape146
  Placement = pos=(71.2,51.5,0) rot=(0,0,1;1.5708rad)
FEATURE [App::Link] D208_D_MiniMELF_Standard_5646c313d2d3_ln_002  label="D206_D_MiniMELF_Standard_12c2ef1d76fd"
  LinkPlacement = pos=(79.1,92.2,0) rot=(0,0,1;0rad)
  LinkedObject = -> Shape146
  Placement = pos=(79.1,92.2,0) rot=(0,0,1;0rad)
FEATURE [App::Link] D208_D_MiniMELF_Standard_5646c313d2d3_ln_003  label="D302_D_MiniMELF_Standard_4cb12e1780df"
  LinkPlacement = pos=(96.0875,22.7,0) rot=(0,0,1;1.5708rad)
  LinkedObject = -> Shape146
  Placement = pos=(96.0875,22.7,0) rot=(0,0,1;1.5708rad)
FEATURE [App::Link] D208_D_MiniMELF_Standard_5646c313d2d3_ln_004  label="D205_D_MiniMELF_Standard_e613e3e799f2"
  LinkPlacement = pos=(127,50.1,0) rot=(0,0,1;0rad)
  LinkedObject = -> Shape146
  Placement = pos=(127,50.1,0) rot=(0,0,1;0rad)
FEATURE [App::Link] D208_D_MiniMELF_Standard_5646c313d2d3_ln_005  label="D209_D_MiniMELF_Standard_1ec4f44d5c34"
  LinkPlacement = pos=(127,47.6,0) rot=(0,0,1;0rad)
  LinkedObject = -> Shape146
  Placement = pos=(127,47.6,0) rot=(0,0,1;0rad)
FEATURE [App::Link] D208_D_MiniMELF_Standard_5646c313d2d3_ln_006  label="D201_D_MiniMELF_Standard_1d564c9b7721"
  LinkPlacement = pos=(84.6,92.2,0) rot=(0,0,1;3.14159rad)
  LinkedObject = -> Shape146
  Placement = pos=(84.6,92.2,0) rot=(0,0,1;3.14159rad)
FEATURE [App::Link] D208_D_MiniMELF_Standard_5646c313d2d3_ln_007  label="D204_D_MiniMELF_Standard_15f0fdcadfec"
  LinkPlacement = pos=(138.9,92.1,0) rot=(0,0,1;3.14159rad)
  LinkedObject = -> Shape146
  Placement = pos=(138.9,92.1,0) rot=(0,0,1;3.14159rad)
FEATURE [App::Link] D208_D_MiniMELF_Standard_5646c313d2d3_ln_008  label="D207_D_MiniMELF_Standard_e976a3a262de"
  LinkPlacement = pos=(73.9,51.5,0) rot=(0,0,1;1.5708rad)
  LinkedObject = -> Shape146
  Placement = pos=(73.9,51.5,0) rot=(0,0,1;1.5708rad)
FEATURE [App::Link] D208_D_MiniMELF_Standard_5646c313d2d3_ln_009  label="D2_D_MiniMELF_Standard_05f98c6ed1d8"
  LinkPlacement = pos=(41.5,29.3,-1.57252) rot=(0.707107,-0.707107,0;3.14159rad)
  LinkedObject = -> Shape146
  Placement = pos=(41.5,29.3,-1.57252) rot=(0.707107,-0.707107,0;3.14159rad)
FEATURE [App::Link] D208_D_MiniMELF_Standard_5646c313d2d3_ln_010  label="D3_D_MiniMELF_Standard_f91f685f11d3"
  LinkPlacement = pos=(32.35,29.4,-1.57252) rot=(0.707107,-0.707107,0;3.14159rad)
  LinkedObject = -> Shape146
  Placement = pos=(32.35,29.4,-1.57252) rot=(0.707107,-0.707107,0;3.14159rad)
FEATURE [App::Link] J2_SWEB_8094_AU___RT_v006_932d9c1a5973_ln_  label="J5_SWEB 8094 AU / RT v006_23028d124e11"
  LinkPlacement = pos=(11.46,37.12,5.5) rot=(0,0,1;3.14159rad)
  LinkedObject = -> SWEB_8094_AU___RT_v1
  Placement = pos=(11.46,37.12,5.5) rot=(0,0,1;3.14159rad)
FEATURE [App::Link] J9_JST_B2B_XH_A_e9e719df0531_ln_001  label="J1_JST_B2B_XH_A_c76c184b747b001"
  LinkPlacement = pos=(150.65,14.625,0) rot=(0,0,1;0rad)
  LinkedObject = -> Shape151
  Placement = pos=(150.65,14.625,0) rot=(0,0,1;0rad)
FEATURE [PartDesign::CoordinateSystem] Local_CS_29d
  AttacherType = Attacher::AttachEngine3D
  AttachmentSupport = -> [X_Axis083]
  MapMode = 2
FEATURE [Sketcher::SketchObject] PCB_Sketch_29d
  ArcFitTolerance = 0
  FullyConstrained = false
  MakeInternals = false
  sketch-geometry (64):
    g0: LineSegment StartX=155 StartY=47.5 StartZ=0 EndX=155 EndY=47 EndZ=0
    g1: LineSegment StartX=131.8 StartY=48.3 StartZ=0 EndX=154.2 EndY=48.3 EndZ=0
    g2: LineSegment StartX=154.2 StartY=46.2 StartZ=0 EndX=131.8 EndY=46.2 EndZ=0
    g3: LineSegment StartX=41.6 StartY=53.9 StartZ=0 EndX=41.6 EndY=53.6 EndZ=0
    g4: LineSegment StartX=185 StartY=95 StartZ=0 EndX=185 EndY=0 EndZ=0
    g5: LineSegment StartX=76.6 StartY=47.7 StartZ=0 EndX=76.6 EndY=47.3 EndZ=0
    g6: LineSegment StartX=91.8 StartY=48.5 StartZ=0 EndX=77.4 EndY=48.5 EndZ=0
    g7: LineSegment StartX=69.3 StartY=53.6 StartZ=0 EndX=69.3 EndY=53.9 EndZ=0
    g8: LineSegment StartX=5.5 StartY=9 StartZ=0 EndX=0 EndY=9 EndZ=0
    g9: LineSegment StartX=36 StartY=75 StartZ=0 EndX=70.5 EndY=75 EndZ=0
    g10: LineSegment StartX=173.5 StartY=53.4 StartZ=0 EndX=173.5 EndY=47.2 EndZ=0
    g11: LineSegment StartX=43 StartY=56 StartZ=0 EndX=76 EndY=56 EndZ=0
    g12: LineSegment StartX=129.3 StartY=53.6 StartZ=0 EndX=129.3 EndY=53.9 EndZ=0
    g13: LineSegment StartX=94.3 StartY=52.8 StartZ=0 EndX=128.5 EndY=52.8 EndZ=0
    g14: LineSegment StartX=6.5 StartY=0 StartZ=0 EndX=6.5 EndY=8 EndZ=0
    g15: LineSegment StartX=77.4 StartY=46.5 StartZ=0 EndX=93.5 EndY=46.5 EndZ=0
    g16: LineSegment StartX=159.3 StartY=53.3 StartZ=0 EndX=159.3 EndY=47.3 EndZ=0
    g17: LineSegment StartX=165.5 StartY=53.3 StartZ=0 EndX=165.5 EndY=47.3 EndZ=0
    g18: LineSegment StartX=128.5 StartY=54.7 StartZ=0 EndX=92.6 EndY=54.7 EndZ=0
    g19: LineSegment StartX=171.5 StartY=47.2 StartZ=0 EndX=171.5 EndY=53.4 EndZ=0
    g20: LineSegment StartX=0 StartY=9 StartZ=0 EndX=0 EndY=86 EndZ=0
    g21: LineSegment StartX=185 StartY=0 StartZ=0 EndX=6.5 EndY=0 EndZ=0
    g22: LineSegment StartX=6.5 StartY=95 StartZ=0 EndX=185 EndY=95 EndZ=0
    g23: LineSegment StartX=167.7 StartY=47.3 StartZ=0 EndX=167.7 EndY=53.3 EndZ=0
    g24: LineSegment StartX=42.4 StartY=52.8 StartZ=0 EndX=68.5 EndY=52.8 EndZ=0
    g25: LineSegment StartX=70.5 StartY=84 StartZ=0 EndX=36 EndY=84 EndZ=0
    g26: LineSegment StartX=68.5 StartY=54.7 StartZ=0 EndX=42.4 EndY=54.7 EndZ=0
    g27: LineSegment StartX=161.5 StartY=47.3 StartZ=0 EndX=161.5 EndY=53.3 EndZ=0
    g28: LineSegment StartX=131 StartY=47 StartZ=0 EndX=131 EndY=47.5 EndZ=0
    g29: LineSegment StartX=124.5 StartY=84.5 StartZ=0 EndX=91 EndY=84.5 EndZ=0
    g30: LineSegment StartX=0 StartY=86 StartZ=0 EndX=5.5 EndY=86 EndZ=0
    g31: LineSegment StartX=94.3 StartY=47.3 StartZ=0 EndX=94.3 EndY=52.8 EndZ=0
    g32: LineSegment StartX=91 StartY=75.5 StartZ=0 EndX=124.5 EndY=75.5 EndZ=0
    g33: LineSegment StartX=6.5 StartY=87 StartZ=0 EndX=6.5 EndY=95 EndZ=0
    g34: LineSegment StartX=91.8 StartY=53.9 StartZ=0 EndX=91.8 EndY=48.5 EndZ=0
    g35: LineSegment StartX=76 StartY=65 StartZ=0 EndX=43 EndY=65 EndZ=0
    g36: ArcOfCircle CenterX=131.8 CenterY=47 CenterZ=0 NormalX=0 NormalY=0 NormalZ=-1 AngleXU=-1.57079 Radius=0.800001 StartAngle=0 EndAngle=1.57079
    g37: ArcOfCircle CenterX=160.4 CenterY=53.3 CenterZ=0 NormalX=0 NormalY=0 NormalZ=-1 AngleXU=-1.29e-14 Radius=1.1 StartAngle=0 EndAngle=3.14159
    g38: ArcOfCircle CenterX=68.5 CenterY=53.9 CenterZ=0 NormalX=0 NormalY=0 NormalZ=-1 AngleXU=1.5708 Radius=0.800001 StartAngle=0 EndAngle=1.57079
    g39: ArcOfCircle CenterX=43 CenterY=60.5 CenterZ=0 NormalX=0 NormalY=0 NormalZ=-1 AngleXU=-1.5708 Radius=4.5 StartAngle=0 EndAngle=3.14159
    g40: ArcOfCircle CenterX=42.4 CenterY=53.9 CenterZ=0 NormalX=0 NormalY=0 NormalZ=-1 AngleXU=1.81359e-06 Radius=0.800001 StartAngle=0 EndAngle=1.57079
    g41: ArcOfCircle CenterX=166.6 CenterY=53.3 CenterZ=0 NormalX=0 NormalY=0 NormalZ=-1 AngleXU=-1.29e-14 Radius=1.1 StartAngle=0 EndAngle=3.14159
    g42: ArcOfCircle CenterX=172.5 CenterY=47.2 CenterZ=0 NormalX=0 NormalY=0 NormalZ=-1 AngleXU=-3.14159 Radius=1 StartAngle=0 EndAngle=3.14159
    g43: ArcOfCircle CenterX=124.5 CenterY=80 CenterZ=0 NormalX=0 NormalY=0 NormalZ=-1 AngleXU=1.5708 Radius=4.5 StartAngle=0 EndAngle=3.14159
    g44: ArcOfCircle CenterX=77.4 CenterY=47.7 CenterZ=0 NormalX=0 NormalY=0 NormalZ=-1 AngleXU=1.81359e-06 Radius=0.800001 StartAngle=0 EndAngle=1.57079
    g45: ArcOfCircle CenterX=93.5 CenterY=47.3 CenterZ=0 NormalX=0 NormalY=0 NormalZ=-1 AngleXU=-3.14159 Radius=0.800001 StartAngle=0 EndAngle=1.57079
    g46: ArcOfCircle CenterX=172.5 CenterY=53.4 CenterZ=0 NormalX=0 NormalY=0 NormalZ=-1 AngleXU=0 Radius=1 StartAngle=0 EndAngle=3.14159
    g47: ArcOfCircle CenterX=128.5 CenterY=53.9 CenterZ=0 NormalX=0 NormalY=0 NormalZ=-1 AngleXU=1.5708 Radius=0.800001 StartAngle=0 EndAngle=1.57079
    g48: ArcOfCircle CenterX=5.5 CenterY=87 CenterZ=0 NormalX=0 NormalY=0 NormalZ=-1 AngleXU=3.14159 Radius=0.999999 StartAngle=0 EndAngle=1.5708
    g49: ArcOfCircle CenterX=42.4 CenterY=53.6 CenterZ=0 NormalX=0 NormalY=0 NormalZ=-1 AngleXU=-1.57079 Radius=0.800001 StartAngle=0 EndAngle=1.57079
    g50: ArcOfCircle CenterX=166.6 CenterY=47.3 CenterZ=0 NormalX=0 NormalY=0 NormalZ=-1 AngleXU=3.14159 Radius=1.1 StartAngle=0 EndAngle=3.14159
    g51: ArcOfCircle CenterX=128.5 CenterY=53.6 CenterZ=0 NormalX=0 NormalY=0 NormalZ=-1 AngleXU=-3.14159 Radius=0.800001 StartAngle=0 EndAngle=1.57079
    g52: ArcOfCircle CenterX=70.5 CenterY=79.5 CenterZ=0 NormalX=0 NormalY=0 NormalZ=-1 AngleXU=1.5708 Radius=4.5 StartAngle=0 EndAngle=3.14159
    g53: ArcOfCircle CenterX=131.8 CenterY=47.5 CenterZ=0 NormalX=0 NormalY=0 NormalZ=-1 AngleXU=1.81358e-06 Radius=0.800001 StartAngle=0 EndAngle=1.57079
    g54: ArcOfCircle CenterX=5.5 CenterY=8 CenterZ=0 NormalX=0 NormalY=0 NormalZ=-1 AngleXU=1.5708 Radius=0.999999 StartAngle=0 EndAngle=1.5708
    g55: ArcOfCircle CenterX=91 CenterY=80 CenterZ=0 NormalX=0 NormalY=0 NormalZ=-1 AngleXU=-1.5708 Radius=4.5 StartAngle=0 EndAngle=3.14159
    g56: ArcOfCircle CenterX=154.2 CenterY=47.5 CenterZ=0 NormalX=0 NormalY=0 NormalZ=-1 AngleXU=1.5708 Radius=0.800001 StartAngle=0 EndAngle=1.57079
    g57: ArcOfCircle CenterX=76 CenterY=60.5 CenterZ=0 NormalX=0 NormalY=0 NormalZ=-1 AngleXU=1.5708 Radius=4.5 StartAngle=0 EndAngle=3.14159
    g58: ArcOfCircle CenterX=68.5 CenterY=53.6 CenterZ=0 NormalX=0 NormalY=0 NormalZ=-1 AngleXU=-3.14159 Radius=0.800001 StartAngle=0 EndAngle=1.57079
    g59: ArcOfCircle CenterX=160.4 CenterY=47.3 CenterZ=0 NormalX=0 NormalY=0 NormalZ=-1 AngleXU=3.14159 Radius=1.1 StartAngle=0 EndAngle=3.14159
    g60: ArcOfCircle CenterX=92.6 CenterY=53.9 CenterZ=0 NormalX=0 NormalY=0 NormalZ=-1 AngleXU=1.81359e-06 Radius=0.800001 StartAngle=0 EndAngle=1.57079
    g61: ArcOfCircle CenterX=36 CenterY=79.5 CenterZ=0 NormalX=0 NormalY=0 NormalZ=-1 AngleXU=-1.5708 Radius=4.5 StartAngle=0 EndAngle=3.14159
    g62: ArcOfCircle CenterX=77.4 CenterY=47.3 CenterZ=0 NormalX=0 NormalY=0 NormalZ=-1 AngleXU=-1.57079 Radius=0.800001 StartAngle=0 EndAngle=1.57079
    g63: ArcOfCircle CenterX=154.2 CenterY=47 CenterZ=0 NormalX=0 NormalY=0 NormalZ=-1 AngleXU=-3.14159 Radius=0.800001 StartAngle=0 EndAngle=1.57079
  constraints (64):
    c: Coincident(g8,g20)
    c: Coincident(g20,g30)
    c: Coincident(g8,g54)
    c: Coincident(g30,g48)
    c: Coincident(g14,g21)
    c: Coincident(g14,g54)
    c: Coincident(g33,g48)
    c: Coincident(g22,g33)
    c: Coincident(g9,g61)
    c: Coincident(g25,g61)
    c: Coincident(g3,g49)
    c: Coincident(g3,g40)
    c: Coincident(g24,g49)
    c: Coincident(g26,g40)
    c: Coincident(g11,g39)
    c: Coincident(g35,g39)
    c: Coincident(g24,g58)
    c: Coincident(g26,g38)
    c: Coincident(g7,g58)
    c: Coincident(g7,g38)
    c: Coincident(g9,g52)
    c: Coincident(g25,g52)
    c: Coincident(g11,g57)
    c: Coincident(g35,g57)
    c: Coincident(g5,g62)
    c: Coincident(g5,g44)
    c: Coincident(g15,g62)
    c: Coincident(g6,g44)
    c: Coincident(g32,g55)
    c: Coincident(g29,g55)
    c: Coincident(g6,g34)
    c: Coincident(g34,g60)
    c: Coincident(g18,g60)
    c: Coincident(g15,g45)
    c: Coincident(g31,g45)
    c: Coincident(g13,g31)
    c: Coincident(g32,g43)
    c: Coincident(g29,g43)
    c: Coincident(g13,g51)
    c: Coincident(g18,g47)
    c: Coincident(g12,g51)
    c: Coincident(g12,g47)
    c: Coincident(g28,g36)
    c: Coincident(g28,g53)
    c: Coincident(g2,g36)
    c: Coincident(g1,g53)
    c: Coincident(g2,g63)
    c: Coincident(g1,g56)
    c: Coincident(g0,g63)
    c: Coincident(g0,g56)
    c: Coincident(g16,g59)
    c: Coincident(g16,g37)
    c: Coincident(g27,g59)
    c: Coincident(g27,g37)
    c: Coincident(g17,g50)
    c: Coincident(g17,g41)
    c: Coincident(g23,g50)
    c: Coincident(g23,g41)
    c: Coincident(g19,g42)
    c: Coincident(g19,g46)
    c: Coincident(g10,g42)
    c: Coincident(g10,g46)
    c: Coincident(g4,g21)
    c: Coincident(g4,g22)
FEATURE [Part::Feature] Part__Feature384  label="5712e517-7b30-11ed-bcdd-db420251a6ca_part"
  shape: bbox 3.9 x 8.65 x 1.375 mm, 114 faces (baked)
FEATURE [Part::Feature] Part__Feature385  label="5712e518-7b30-11ed-bcdd-db420251a6ca_part"
  shape: bbox 1.425 x 0.42 x 0.9875 mm, 14 faces (baked)
FEATURE [Part::Feature] Part__Feature386  label="5712e518-7b30-11ed-bcdd-db420251a6ca_part001"
  shape: bbox 1.425 x 0.42 x 0.9875 mm, 14 faces (baked)
FEATURE [Part::Feature] Part__Feature387  label="5712e518-7b30-11ed-bcdd-db420251a6ca_part002"
  shape: bbox 1.425 x 0.42 x 0.9875 mm, 14 faces (baked)
FEATURE [Part::Feature] Part__Feature388  label="5712e518-7b30-11ed-bcdd-db420251a6ca_part003"
  shape: bbox 1.425 x 0.42 x 0.9875 mm, 14 faces (baked)
FEATURE [Part::Feature] Part__Feature389  label="5712e518-7b30-11ed-bcdd-db420251a6ca_part004"
  shape: bbox 1.425 x 0.42 x 0.9875 mm, 14 faces (baked)
FEATURE [Part::Feature] Part__Feature390  label="5712e518-7b30-11ed-bcdd-db420251a6ca_part005"
  shape: bbox 1.425 x 0.42 x 0.9875 mm, 14 faces (baked)
FEATURE [Part::Feature] Part__Feature391  label="5712e518-7b30-11ed-bcdd-db420251a6ca_part006"
  shape: bbox 1.425 x 0.42 x 0.9875 mm, 14 faces (baked)
FEATURE [Part::Feature] Part__Feature392  label="5712e518-7b30-11ed-bcdd-db420251a6ca_part007"
  shape: bbox 1.425 x 0.42 x 0.9875 mm, 14 faces (baked)
FEATURE [Part::Feature] Part__Feature393  label="5712e518-7b30-11ed-bcdd-db420251a6ca_part008"
  shape: bbox 1.425 x 0.42 x 0.9875 mm, 14 faces (baked)
FEATURE [Part::Feature] Part__Feature394  label="5712e518-7b30-11ed-bcdd-db420251a6ca_part009"
  shape: bbox 1.425 x 0.42 x 0.9875 mm, 14 faces (baked)
FEATURE [Part::Feature] Part__Feature395  label="5712e518-7b30-11ed-bcdd-db420251a6ca_part010"
  shape: bbox 1.425 x 0.42 x 0.9875 mm, 14 faces (baked)
FEATURE [Part::Feature] Part__Feature396  label="5712e518-7b30-11ed-bcdd-db420251a6ca_part011"
  shape: bbox 1.425 x 0.42 x 0.9875 mm, 14 faces (baked)
FEATURE [Part::Feature] Part__Feature397  label="5712e518-7b30-11ed-bcdd-db420251a6ca_part012"
  shape: bbox 1.425 x 0.42 x 0.9875 mm, 14 faces (baked)
FEATURE [Part::Feature] Part__Feature398  label="5712e518-7b30-11ed-bcdd-db420251a6ca_part013"
  shape: bbox 1.425 x 0.42 x 0.9875 mm, 14 faces (baked)
FEATURE [Part::Feature] Part__Feature399  label="5712e519-7b30-11ed-bcdd-db420251a6ca_part"
  shape: bbox 0.6 x 0.6 x 0.05 mm, 3 faces (baked)
FEATURE [Part::Feature] Part__Feature400  label="SWEB 8094 AU / RT v1"
  shape: bbox 1.164 x 10.96 x 15.3 mm, 54 faces (baked)
FEATURE [Part::Feature] Part__Feature401  label="SWEB 8094 AU / RT v002"
  shape: bbox 1.164 x 10.96 x 15.3 mm, 54 faces (baked)
FEATURE [Part::Feature] Part__Feature402  label="SWEB 8094 AU / RT v003"
  shape: bbox 2.108 x 2.108 x 12.21 mm, 108 faces (baked)
FEATURE [Part::Feature] Part__Feature403  label="SWEB 8094 AU / RT v004"
  shape: bbox 24.51 x 5.007 x 5.007 mm, 12 faces (baked)
FEATURE [Part::Feature] Part__Feature404  label="SWEB 8094 AU / RT v005"
  shape: bbox 33.02 x 12.85 x 12.85 mm, 258 faces (baked)
FEATURE [Part::Feature] Part__Feature405  label="729b0bae-9266-11ed-9e62-a0cec80452fd_part"
  shape: bbox 3.9 x 4.905 x 1.75 mm, 84 faces (baked)
FEATURE [Part::Feature] Part__Feature406  label="729b0e92-9266-11ed-9e62-a0cec80452fd_part"
  shape: bbox 1.198 x 0.41 x 1.07 mm, 14 faces (baked)
FEATURE [Part::Feature] Part__Feature407  label="729b0e92-9266-11ed-9e62-a0cec80452fd_part001"
  shape: bbox 1.198 x 0.41 x 1.07 mm, 14 faces (baked)
FEATURE [Part::Feature] Part__Feature408  label="729b0e92-9266-11ed-9e62-a0cec80452fd_part002"
  shape: bbox 1.198 x 0.41 x 1.07 mm, 14 faces (baked)
FEATURE [Part::Feature] Part__Feature409  label="729b0e92-9266-11ed-9e62-a0cec80452fd_part003"
  shape: bbox 1.198 x 0.41 x 1.07 mm, 14 faces (baked)
FEATURE [Part::Feature] Part__Feature410  label="729b0e92-9266-11ed-9e62-a0cec80452fd_part004"
  shape: bbox 1.198 x 0.41 x 1.07 mm, 14 faces (baked)
FEATURE [Part::Feature] Part__Feature411  label="729b0e92-9266-11ed-9e62-a0cec80452fd_part005"
  shape: bbox 1.198 x 0.41 x 1.07 mm, 14 faces (baked)
FEATURE [Part::Feature] Part__Feature412  label="729b0e92-9266-11ed-9e62-a0cec80452fd_part006"
  shape: bbox 1.198 x 0.41 x 1.07 mm, 14 faces (baked)
FEATURE [Part::Feature] Part__Feature413  label="729b0e92-9266-11ed-9e62-a0cec80452fd_part007"
  shape: bbox 1.198 x 0.41 x 1.07 mm, 14 faces (baked)
FEATURE [Part::Feature] Part__Feature414  label="729b1108-9266-11ed-9e62-a0cec80452fd_part"
  shape: bbox 0.4 x 0.4 x 0.05 mm, 3 faces (baked)
FEATURE [Part::Feature] Pcb_29d
  Placement = pos=(-25,115,0) rot=(0,0,1;0rad)
  shape: bbox 185 x 95 x 1.573 mm, 148 faces (baked)
FEATURE [App::Part] Board_Geoms_29d
  Group = -> [Pcb_29d,PCB_Sketch_29d]
  Origin = -> Origin082
FEATURE [App::Link] Q201_SOT_23_fb4564768f05_ln_  label="Q2_SOT_23_d3792941e742"
  LinkPlacement = pos=(48.65,37.3,0) rot=(0,0,-1;1.5708rad)
  LinkedObject = -> Shape147
  Placement = pos=(48.65,37.3,0) rot=(0,0,-1;1.5708rad)
FEATURE [App::Link] Q201_SOT_23_fb4564768f05_ln_001  label="Q202_SOT_23_8fd5338d1ad3"
  LinkPlacement = pos=(67.6,50.4,0) rot=(0,0,1;1.5708rad)
  LinkedObject = -> Shape147
  Placement = pos=(67.6,50.4,0) rot=(0,0,1;1.5708rad)
FEATURE [App::Link] Q201_SOT_23_fb4564768f05_ln_002  label="Q206_SOT_23_7613cc9079a5"
  LinkPlacement = pos=(121.1,47.8,0) rot=(0,0,1;1.5708rad)
  LinkedObject = -> Shape147
  Placement = pos=(121.1,47.8,0) rot=(0,0,1;1.5708rad)
FEATURE [App::Link] Q201_SOT_23_fb4564768f05_ln_003  label="Q1_SOT_23_9944ca6c78aa"
  LinkPlacement = pos=(48.7,21.6875,0) rot=(0,0,1;1.5708rad)
  LinkedObject = -> Shape147
  Placement = pos=(48.7,21.6875,0) rot=(0,0,1;1.5708rad)
FEATURE [App::Link] Q201_SOT_23_fb4564768f05_ln_004  label="Q301_SOT_23_3dcddfe8769a"
  LinkPlacement = pos=(82.8125,21.55,0) rot=(0,0,1;1.5708rad)
  LinkedObject = -> Shape147
  Placement = pos=(82.8125,21.55,0) rot=(0,0,1;1.5708rad)
FEATURE [App::Link] Q201_SOT_23_fb4564768f05_ln_005  label="Q205_SOT_23_ab3f773d3a7f"
  LinkPlacement = pos=(150.5,88.5,0) rot=(0,0,1;3.14159rad)
  LinkedObject = -> Shape147
  Placement = pos=(150.5,88.5,0) rot=(0,0,1;3.14159rad)
FEATURE [App::Link] Q201_SOT_23_fb4564768f05_ln_013  label="Q4_SOT_23_78596e99f7ac001"
  LinkPlacement = pos=(153.65,10.1,-1.57252) rot=(0.707107,0.707107,0;3.14159rad)
  LinkedObject = -> Shape147
  Placement = pos=(153.65,10.1,-1.57252) rot=(0.707107,0.707107,0;3.14159rad)
FEATURE [App::Link] Q203_TO_247_3_Vertical_e30fe5b94042_ln_  label="Q207_TO-247-3_Vertical_764ed6fad74f"
  LinkPlacement = pos=(143.45,87.82,0) rot=(0,0,1;3.14159rad)
  LinkedObject = -> Shape141
  Placement = pos=(143.45,87.82,0) rot=(0,0,1;3.14159rad)
FEATURE [App::Link] Q203_TO_247_3_Vertical_e30fe5b94042_ln_001  label="Q208_TO-247-3_Vertical_50f58b44882c"
  LinkPlacement = pos=(132.55,52.18,0) rot=(0,0,1;0rad)
  LinkedObject = -> Shape141
  Placement = pos=(132.55,52.18,0) rot=(0,0,1;0rad)
FEATURE [App::Link] Q203_TO_247_3_Vertical_e30fe5b94042_ln_002  label="Q204_TO-247-3_Vertical_97f5affc5a12"
  LinkPlacement = pos=(78.1,52.18,0) rot=(0,0,1;0rad)
  LinkedObject = -> Shape141
  Placement = pos=(78.1,52.18,0) rot=(0,0,1;0rad)
FEATURE [App::Link] R240_R_2512_6332Metric_fe718b218676_ln_  label="R239_R_2512_6332Metric_f1ce88b7dc37"
  LinkPlacement = pos=(175.5,27.05,-1.57252) rot=(0.707107,-0.707107,0;3.14159rad)
  LinkedObject = -> Shape160
  Placement = pos=(175.5,27.05,-1.57252) rot=(0.707107,-0.707107,0;3.14159rad)
FEATURE [App::Link] R240_R_2512_6332Metric_fe718b218676_ln_001  label="R220_R_2512_6332Metric_bee22148888a"
  LinkPlacement = pos=(163.5,27,-1.57252) rot=(0.707107,-0.707107,0;3.14159rad)
  LinkedObject = -> Shape160
  Placement = pos=(163.5,27,-1.57252) rot=(0.707107,-0.707107,0;3.14159rad)
FEATURE [App::Link] R240_R_2512_6332Metric_fe718b218676_ln_002  label="R219_R_2512_6332Metric_1ec88cb2b336"
  LinkPlacement = pos=(169.55,11.5,-1.57252) rot=(0.707107,-0.707107,0;3.14159rad)
  LinkedObject = -> Shape160
  Placement = pos=(169.55,11.5,-1.57252) rot=(0.707107,-0.707107,0;3.14159rad)
FEATURE [App::Link] R28_R_0805_2012Metric_56a8941a8a89_ln_  label="R232_R_0805_2012Metric_d40f949d485b"
  LinkPlacement = pos=(181.3,23.7,0) rot=(0,0,1;1.5708rad)
  LinkedObject = -> Shape138
  Placement = pos=(181.3,23.7,0) rot=(0,0,1;1.5708rad)
FEATURE [App::Link] R28_R_0805_2012Metric_56a8941a8a89_ln_001  label="R30_R_0805_2012Metric_d3033175b96b"
  LinkPlacement = pos=(133.5,27.4,0) rot=(0,0,1;0rad)
  LinkedObject = -> Shape138
  Placement = pos=(133.5,27.4,0) rot=(0,0,1;0rad)
FEATURE [App::Link] R28_R_0805_2012Metric_56a8941a8a89_ln_002  label="R234_R_0805_2012Metric_dea6c1b14176"
  LinkPlacement = pos=(163.438,5.5,0) rot=(0,0,1;1.5708rad)
  LinkedObject = -> Shape138
  Placement = pos=(163.438,5.5,0) rot=(0,0,1;1.5708rad)
FEATURE [App::Link] R28_R_0805_2012Metric_56a8941a8a89_ln_003  label="R229_R_0805_2012Metric_297f9286941b"
  LinkPlacement = pos=(154,90.5,0) rot=(0,0,-1;1.5708rad)
  LinkedObject = -> Shape138
  Placement = pos=(154,90.5,0) rot=(0,0,-1;1.5708rad)
FEATURE [App::Link] R28_R_0805_2012Metric_56a8941a8a89_ln_004  label="R212_R_0805_2012Metric_83b1380610ae"
  LinkPlacement = pos=(175.564,5.44,0) rot=(0,0,1;1.5708rad)
  LinkedObject = -> Shape138
  Placement = pos=(175.564,5.44,0) rot=(0,0,1;1.5708rad)
FEATURE [App::Link] R28_R_0805_2012Metric_56a8941a8a89_ln_005  label="R402_R_0805_2012Metric_8a70a5abb1a0"
  LinkPlacement = pos=(51.9,41.55,0) rot=(0,0,-1;1.5708rad)
  LinkedObject = -> Shape138
  Placement = pos=(51.9,41.55,0) rot=(0,0,-1;1.5708rad)
FEATURE [App::Link] R28_R_0805_2012Metric_56a8941a8a89_ln_006  label="R405_R_0805_2012Metric_12c457529533"
  LinkPlacement = pos=(128.275,6.125,0) rot=(0,0,1;1.5708rad)
  LinkedObject = -> Shape138
  Placement = pos=(128.275,6.125,0) rot=(0,0,1;1.5708rad)
FEATURE [App::Link] R28_R_0805_2012Metric_56a8941a8a89_ln_007  label="R322_R_0805_2012Metric_120e3dbff6d5"
  LinkPlacement = pos=(60.65,28.175,0) rot=(0,0,1;3.14159rad)
  LinkedObject = -> Shape138
  Placement = pos=(60.65,28.175,0) rot=(0,0,1;3.14159rad)
FEATURE [App::Link] R28_R_0805_2012Metric_56a8941a8a89_ln_008  label="R202_R_0805_2012Metric_c207ca0a30a5"
  LinkPlacement = pos=(40.9,50.3,0) rot=(0,0,1;1.5708rad)
  LinkedObject = -> Shape138
  Placement = pos=(40.9,50.3,0) rot=(0,0,1;1.5708rad)
FEATURE [App::Link] R28_R_0805_2012Metric_56a8941a8a89_ln_009  label="R19_R_0805_2012Metric_4ce773df796d"
  LinkPlacement = pos=(44.45,16.7,0) rot=(0,0,1;0rad)
  LinkedObject = -> Shape138
  Placement = pos=(44.45,16.7,0) rot=(0,0,1;0rad)
FEATURE [App::Link] R28_R_0805_2012Metric_56a8941a8a89_ln_010  label="R325_R_0805_2012Metric_73d95f8b1a28"
  LinkPlacement = pos=(64.2125,25.05,0) rot=(0,0,1;3.14159rad)
  LinkedObject = -> Shape138
  Placement = pos=(64.2125,25.05,0) rot=(0,0,1;3.14159rad)
FEATURE [App::Link] R28_R_0805_2012Metric_56a8941a8a89_ln_011  label="R305_R_0805_2012Metric_eef09c2e666f"
  LinkPlacement = pos=(48.95,33.2,0) rot=(0,0,1;0rad)
  LinkedObject = -> Shape138
  Placement = pos=(48.95,33.2,0) rot=(0,0,1;0rad)
FEATURE [App::Link] R28_R_0805_2012Metric_56a8941a8a89_ln_012  label="R40_R_0805_2012Metric_ae05bab19ef003"
  LinkPlacement = pos=(80.2,43.6,0) rot=(0,0,1;0rad)
  LinkedObject = -> Shape138
  Placement = pos=(80.2,43.6,0) rot=(0,0,1;0rad)
FEATURE [App::Link] R28_R_0805_2012Metric_56a8941a8a89_ln_013  label="R323_R_0805_2012Metric_93b05d35d6e7"
  LinkPlacement = pos=(55.8,20.6,0) rot=(0,0,-1;1.5708rad)
  LinkedObject = -> Shape138
  Placement = pos=(55.8,20.6,0) rot=(0,0,-1;1.5708rad)
FEATURE [App::Link] R28_R_0805_2012Metric_56a8941a8a89_ln_014  label="R330_R_0805_2012Metric_4650af7f38e9"
  LinkPlacement = pos=(60.6875,25.05,0) rot=(0,0,1;0rad)
  LinkedObject = -> Shape138
  Placement = pos=(60.6875,25.05,0) rot=(0,0,1;0rad)
FEATURE [App::Link] R28_R_0805_2012Metric_56a8941a8a89_ln_015  label="R218_R_0805_2012Metric_8cee86029e25"
  LinkPlacement = pos=(167.5,23.5,0) rot=(0,0,1;1.5708rad)
  LinkedObject = -> Shape138
  Placement = pos=(167.5,23.5,0) rot=(0,0,1;1.5708rad)
FEATURE [App::Link] R28_R_0805_2012Metric_56a8941a8a89_ln_016  label="R27_R_0805_2012Metric_dfc48d5b5f65"
  LinkPlacement = pos=(152.925,25.625,0) rot=(0,0,1;1.5708rad)
  LinkedObject = -> Shape138
  Placement = pos=(152.925,25.625,0) rot=(0,0,1;1.5708rad)
FEATURE [App::Link] R28_R_0805_2012Metric_56a8941a8a89_ln_017  label="R29_R_0805_2012Metric_b7007f5b310c"
  LinkPlacement = pos=(149.5,29.9,0) rot=(0,0,1;0rad)
  LinkedObject = -> Shape138
  Placement = pos=(149.5,29.9,0) rot=(0,0,1;0rad)
FEATURE [App::Link] R28_R_0805_2012Metric_56a8941a8a89_ln_018  label="R317_R_0805_2012Metric_18c7baa40ddc"
  LinkPlacement = pos=(33,37.1,0) rot=(0,0,1;0rad)
  LinkedObject = -> Shape138
  Placement = pos=(33,37.1,0) rot=(0,0,1;0rad)
FEATURE [App::Link] R28_R_0805_2012Metric_56a8941a8a89_ln_019  label="R32_R_0805_2012Metric_d8646d91ff30"
  LinkPlacement = pos=(142.7,28.2625,0) rot=(0,0,-1;1.5708rad)
  LinkedObject = -> Shape138
  Placement = pos=(142.7,28.2625,0) rot=(0,0,-1;1.5708rad)
FEATURE [App::Link] R28_R_0805_2012Metric_56a8941a8a89_ln_020  label="R314_R_0805_2012Metric_0aa6922b32fc"
  LinkPlacement = pos=(32.85,19.45,0) rot=(0,0,1;0rad)
  LinkedObject = -> Shape138
  Placement = pos=(32.85,19.45,0) rot=(0,0,1;0rad)
FEATURE [App::Link] R28_R_0805_2012Metric_56a8941a8a89_ln_021  label="R301_R_0805_2012Metric_6580910332ae"
  LinkPlacement = pos=(85.7375,25.1,0) rot=(0,0,-1;1.5708rad)
  LinkedObject = -> Shape138
  Placement = pos=(85.7375,25.1,0) rot=(0,0,-1;1.5708rad)
FEATURE [App::Link] R28_R_0805_2012Metric_56a8941a8a89_ln_022  label="R321_R_0805_2012Metric_afbedf02a5f9"
  LinkPlacement = pos=(52.825,23,0) rot=(0,0,1;0rad)
  LinkedObject = -> Shape138
  Placement = pos=(52.825,23,0) rot=(0,0,1;0rad)
FEATURE [App::Link] R28_R_0805_2012Metric_56a8941a8a89_ln_023  label="R320_R_0805_2012Metric_c88965fec192"
  LinkPlacement = pos=(82.8375,18.5,0) rot=(0,0,1;3.14159rad)
  LinkedObject = -> Shape138
  Placement = pos=(82.8375,18.5,0) rot=(0,0,1;3.14159rad)
FEATURE [App::Link] R28_R_0805_2012Metric_56a8941a8a89_ln_024  label="R233_R_0805_2012Metric_f44218af8ec8"
  LinkPlacement = pos=(163.438,13.5,0) rot=(0,0,1;1.5708rad)
  LinkedObject = -> Shape138
  Placement = pos=(163.438,13.5,0) rot=(0,0,1;1.5708rad)
FEATURE [App::Link] R28_R_0805_2012Metric_56a8941a8a89_ln_025  label="R238_R_0805_2012Metric_d4b0e688e9b4"
  LinkPlacement = pos=(161.438,5.5,0) rot=(0,0,1;1.5708rad)
  LinkedObject = -> Shape138
  Placement = pos=(161.438,5.5,0) rot=(0,0,1;1.5708rad)
FEATURE [App::Link] R28_R_0805_2012Metric_56a8941a8a89_ln_026  label="R210_R_0805_2012Metric_e3249320b20a"
  LinkPlacement = pos=(62.3,50.5,0) rot=(0,0,-1;1.5708rad)
  LinkedObject = -> Shape138
  Placement = pos=(62.3,50.5,0) rot=(0,0,-1;1.5708rad)
FEATURE [App::Link] R28_R_0805_2012Metric_56a8941a8a89_ln_027  label="R404_R_0805_2012Metric_8929ad84e0bc"
  LinkPlacement = pos=(117.45,5.65,0) rot=(0,0,1;3.14159rad)
  LinkedObject = -> Shape138
  Placement = pos=(117.45,5.65,0) rot=(0,0,1;3.14159rad)
FEATURE [App::Link] R28_R_0805_2012Metric_56a8941a8a89_ln_028  label="R303_R_0805_2012Metric_045e79a600fb"
  LinkPlacement = pos=(122.4,35.7,0) rot=(0,0,-1;1.5708rad)
  LinkedObject = -> Shape138
  Placement = pos=(122.4,35.7,0) rot=(0,0,-1;1.5708rad)
FEATURE [App::Link] R28_R_0805_2012Metric_56a8941a8a89_ln_029  label="R225_R_0805_2012Metric_c06b0ccb0e2f"
  LinkPlacement = pos=(98.815,50.9,0) rot=(0,0,1;3.14159rad)
  LinkedObject = -> Shape138
  Placement = pos=(98.815,50.9,0) rot=(0,0,1;3.14159rad)
FEATURE [App::Link] R28_R_0805_2012Metric_56a8941a8a89_ln_030  label="R312_R_0805_2012Metric_07deda23b151"
  LinkPlacement = pos=(36.45,21.55,0) rot=(0,0,1;0rad)
  LinkedObject = -> Shape138
  Placement = pos=(36.45,21.55,0) rot=(0,0,1;0rad)
FEATURE [App::Link] R28_R_0805_2012Metric_56a8941a8a89_ln_031  label="R503_R_0805_2012Metric_0159c068ed8e"
  LinkPlacement = pos=(106.3,23.925,0) rot=(0,0,1;0rad)
  LinkedObject = -> Shape138
  Placement = pos=(106.3,23.925,0) rot=(0,0,1;0rad)
FEATURE [App::Link] R28_R_0805_2012Metric_56a8941a8a89_ln_032  label="R507_R_0805_2012Metric_bb3ac16f6f0c"
  LinkPlacement = pos=(109.825,25.1,0) rot=(0,0,1;0rad)
  LinkedObject = -> Shape138
  Placement = pos=(109.825,25.1,0) rot=(0,0,1;0rad)
FEATURE [App::Link] R28_R_0805_2012Metric_56a8941a8a89_ln_033  label="R35_R_0805_2012Metric_bc73c2b9906b"
  LinkPlacement = pos=(138.65,28.2625,0) rot=(0,0,-1;1.5708rad)
  LinkedObject = -> Shape138
  Placement = pos=(138.65,28.2625,0) rot=(0,0,-1;1.5708rad)
FEATURE [App::Link] R28_R_0805_2012Metric_56a8941a8a89_ln_034  label="R223_R_0805_2012Metric_527af22d81bc"
  LinkPlacement = pos=(182.264,82.996,0) rot=(0,0,1;0rad)
  LinkedObject = -> Shape138
  Placement = pos=(182.264,82.996,0) rot=(0,0,1;0rad)
FEATURE [App::Link] R28_R_0805_2012Metric_56a8941a8a89_ln_035  label="R324_R_0805_2012Metric_1560be6bd8ac"
  LinkPlacement = pos=(56.725,23.35,0) rot=(0,0,1;3.14159rad)
  LinkedObject = -> Shape138
  Placement = pos=(56.725,23.35,0) rot=(0,0,1;3.14159rad)
FEATURE [App::Link] R28_R_0805_2012Metric_56a8941a8a89_ln_036  label="R204_R_0805_2012Metric_b14df3f58a37"
  LinkPlacement = pos=(161.052,24.972,0) rot=(0,0,1;3.14159rad)
  LinkedObject = -> Shape138
  Placement = pos=(161.052,24.972,0) rot=(0,0,1;3.14159rad)
FEATURE [App::Link] R28_R_0805_2012Metric_56a8941a8a89_ln_037  label="R221_R_0805_2012Metric_e443798ed64c"
  LinkPlacement = pos=(179.216,80.726,0) rot=(0,0,1;1.5708rad)
  LinkedObject = -> Shape138
  Placement = pos=(179.216,80.726,0) rot=(0,0,1;1.5708rad)
FEATURE [App::Link] R28_R_0805_2012Metric_56a8941a8a89_ln_038  label="R206_R_0805_2012Metric_b3859810ddf7"
  LinkPlacement = pos=(161.052,29.544,0) rot=(0,0,1;3.14159rad)
  LinkedObject = -> Shape138
  Placement = pos=(161.052,29.544,0) rot=(0,0,1;3.14159rad)
FEATURE [App::Link] R28_R_0805_2012Metric_56a8941a8a89_ln_039  label="R208_R_0805_2012Metric_7a516ad4c097"
  LinkPlacement = pos=(64.5,47.3,0) rot=(0,0,1;0rad)
  LinkedObject = -> Shape138
  Placement = pos=(64.5,47.3,0) rot=(0,0,1;0rad)
FEATURE [App::Link] R28_R_0805_2012Metric_56a8941a8a89_ln_040  label="R315_R_0805_2012Metric_a309409b1045"
  LinkPlacement = pos=(161.052,20.3,0) rot=(0,0,1;0rad)
  LinkedObject = -> Shape138
  Placement = pos=(161.052,20.3,0) rot=(0,0,1;0rad)
FEATURE [App::Link] R28_R_0805_2012Metric_56a8941a8a89_ln_041  label="R401_R_0805_2012Metric_89f38c3af4c5"
  LinkPlacement = pos=(55.9,32,0) rot=(0,0,1;1.5708rad)
  LinkedObject = -> Shape138
  Placement = pos=(55.9,32,0) rot=(0,0,1;1.5708rad)
FEATURE [App::Link] R28_R_0805_2012Metric_56a8941a8a89_ln_042  label="R309_R_0805_2012Metric_617f4d9395ee"
  LinkPlacement = pos=(40.2,37.1,0) rot=(0,0,1;3.14159rad)
  LinkedObject = -> Shape138
  Placement = pos=(40.2,37.1,0) rot=(0,0,1;3.14159rad)
FEATURE [App::Link] R28_R_0805_2012Metric_56a8941a8a89_ln_043  label="R201_R_0805_2012Metric_906e28a1cc1a"
  LinkPlacement = pos=(117.5,92.45,0) rot=(0,0,1;3.14159rad)
  LinkedObject = -> Shape138
  Placement = pos=(117.5,92.45,0) rot=(0,0,1;3.14159rad)
FEATURE [App::Link] R28_R_0805_2012Metric_56a8941a8a89_ln_044  label="R235_R_0805_2012Metric_c6c2d3c2ed7d"
  LinkPlacement = pos=(179.3,31.7,0) rot=(0,0,1;1.5708rad)
  LinkedObject = -> Shape138
  Placement = pos=(179.3,31.7,0) rot=(0,0,1;1.5708rad)
FEATURE [App::Link] R28_R_0805_2012Metric_56a8941a8a89_ln_045  label="R217_R_0805_2012Metric_959eef384817"
  LinkPlacement = pos=(167.5,31.5,0) rot=(0,0,1;1.5708rad)
  LinkedObject = -> Shape138
  Placement = pos=(167.5,31.5,0) rot=(0,0,1;1.5708rad)
FEATURE [App::Link] R28_R_0805_2012Metric_56a8941a8a89_ln_046  label="R504_R_0805_2012Metric_879b1bd5ddf9"
  LinkPlacement = pos=(99.15,30.15,0) rot=(0,0,1;1.5708rad)
  LinkedObject = -> Shape138
  Placement = pos=(99.15,30.15,0) rot=(0,0,1;1.5708rad)
FEATURE [App::Link] R28_R_0805_2012Metric_56a8941a8a89_ln_047  label="R502_R_0805_2012Metric_ac830f34afeb"
  LinkPlacement = pos=(103.45,24.475,0) rot=(0,0,1;1.5708rad)
  LinkedObject = -> Shape138
  Placement = pos=(103.45,24.475,0) rot=(0,0,1;1.5708rad)
FEATURE [App::Link] R28_R_0805_2012Metric_56a8941a8a89_ln_048  label="R205_R_0805_2012Metric_bc8565b3ccd3"
  LinkPlacement = pos=(47.5,46.5,0) rot=(0,0,1;3.14159rad)
  LinkedObject = -> Shape138
  Placement = pos=(47.5,46.5,0) rot=(0,0,1;3.14159rad)
FEATURE [App::Link] R28_R_0805_2012Metric_56a8941a8a89_ln_049  label="R38_R_0805_2012Metric_75b1e7ddb320"
  LinkPlacement = pos=(137.55,13.525,0) rot=(0,0,-1;1.5708rad)
  LinkedObject = -> Shape138
  Placement = pos=(137.55,13.525,0) rot=(0,0,-1;1.5708rad)
FEATURE [App::Link] R28_R_0805_2012Metric_56a8941a8a89_ln_050  label="R213_R_0805_2012Metric_7f63307805dd"
  LinkPlacement = pos=(169.5,31.5,0) rot=(0,0,1;1.5708rad)
  LinkedObject = -> Shape138
  Placement = pos=(169.5,31.5,0) rot=(0,0,1;1.5708rad)
FEATURE [App::Link] R28_R_0805_2012Metric_56a8941a8a89_ln_051  label="R216_R_0805_2012Metric_6f09a1d043a7"
  LinkPlacement = pos=(173.564,5.44,0) rot=(0,0,1;1.5708rad)
  LinkedObject = -> Shape138
  Placement = pos=(173.564,5.44,0) rot=(0,0,1;1.5708rad)
FEATURE [App::Link] R28_R_0805_2012Metric_56a8941a8a89_ln_052  label="R1_R_0805_2012Metric_95b6a14b4e94"
  LinkPlacement = pos=(52.8,18.1,0) rot=(0,0,1;0rad)
  LinkedObject = -> Shape138
  Placement = pos=(52.8,18.1,0) rot=(0,0,1;0rad)
FEATURE [App::Link] R28_R_0805_2012Metric_56a8941a8a89_ln_053  label="R224_R_0805_2012Metric_6ab6096b3db2"
  LinkPlacement = pos=(161.052,27.258,0) rot=(0,0,1;3.14159rad)
  LinkedObject = -> Shape138
  Placement = pos=(161.052,27.258,0) rot=(0,0,1;3.14159rad)
FEATURE [App::Link] R28_R_0805_2012Metric_56a8941a8a89_ln_054  label="R237_R_0805_2012Metric_03f2d14f6dd7"
  LinkPlacement = pos=(161.438,13.5,0) rot=(0,0,1;1.5708rad)
  LinkedObject = -> Shape138
  Placement = pos=(161.438,13.5,0) rot=(0,0,1;1.5708rad)
FEATURE [App::Link] R28_R_0805_2012Metric_56a8941a8a89_ln_055  label="R226_R_0805_2012Metric_8c5f65e5c5e1"
  LinkPlacement = pos=(161.052,22.636,0) rot=(0,0,1;3.14159rad)
  LinkedObject = -> Shape138
  Placement = pos=(161.052,22.636,0) rot=(0,0,1;3.14159rad)
FEATURE [App::Link] R28_R_0805_2012Metric_56a8941a8a89_ln_056  label="R26_R_0805_2012Metric_964cbbcd5236"
  LinkPlacement = pos=(128.05,30.35,0) rot=(0,0,-1;1.5708rad)
  LinkedObject = -> Shape138
  Placement = pos=(128.05,30.35,0) rot=(0,0,-1;1.5708rad)
FEATURE [App::Link] R28_R_0805_2012Metric_56a8941a8a89_ln_057  label="R20_R_0805_2012Metric_df453e6bea18"
  LinkPlacement = pos=(48.6,40.45,0) rot=(0,0,1;0rad)
  LinkedObject = -> Shape138
  Placement = pos=(48.6,40.45,0) rot=(0,0,1;0rad)
FEATURE [App::Link] R28_R_0805_2012Metric_56a8941a8a89_ln_058  label="R313_R_0805_2012Metric_8c169fd2acfc"
  LinkPlacement = pos=(33,39.2,0) rot=(0,0,1;3.14159rad)
  LinkedObject = -> Shape138
  Placement = pos=(33,39.2,0) rot=(0,0,1;3.14159rad)
FEATURE [App::Link] R28_R_0805_2012Metric_56a8941a8a89_ln_059  label="R211_R_0805_2012Metric_3ad5823d24fb"
  LinkPlacement = pos=(175.564,13.44,0) rot=(0,0,1;1.5708rad)
  LinkedObject = -> Shape138
  Placement = pos=(175.564,13.44,0) rot=(0,0,1;1.5708rad)
FEATURE [App::Link] R28_R_0805_2012Metric_56a8941a8a89_ln_060  label="R18_R_0805_2012Metric_05efc19aec46"
  LinkPlacement = pos=(44.5,42.1,0) rot=(0,0,1;0rad)
  LinkedObject = -> Shape138
  Placement = pos=(44.5,42.1,0) rot=(0,0,1;0rad)
FEATURE [App::Link] R28_R_0805_2012Metric_56a8941a8a89_ln_061  label="R319_R_0805_2012Metric_2d5fad86d1aa"
  LinkPlacement = pos=(158.052,29.798,0) rot=(0,0,-1;1.5708rad)
  LinkedObject = -> Shape138
  Placement = pos=(158.052,29.798,0) rot=(0,0,-1;1.5708rad)
FEATURE [App::Link] R28_R_0805_2012Metric_56a8941a8a89_ln_062  label="R39_R_0805_2012Metric_b2f2924be4e009"
  LinkPlacement = pos=(80.2,41.4,0) rot=(0,0,1;3.14159rad)
  LinkedObject = -> Shape138
  Placement = pos=(80.2,41.4,0) rot=(0,0,1;3.14159rad)
FEATURE [App::Link] R28_R_0805_2012Metric_56a8941a8a89_ln_063  label="R310_R_0805_2012Metric_f6025bc696d9"
  LinkPlacement = pos=(40.05,21.55,0) rot=(0,0,1;0rad)
  LinkedObject = -> Shape138
  Placement = pos=(40.05,21.55,0) rot=(0,0,1;0rad)
FEATURE [App::Link] R28_R_0805_2012Metric_56a8941a8a89_ln_064  label="R308_R_0805_2012Metric_7133bf9c9c07"
  LinkPlacement = pos=(43.65,21.55,0) rot=(0,0,1;0rad)
  LinkedObject = -> Shape138
  Placement = pos=(43.65,21.55,0) rot=(0,0,1;0rad)
FEATURE [App::Link] R28_R_0805_2012Metric_56a8941a8a89_ln_065  label="R37_R_0805_2012Metric_006564c923aa"
  LinkPlacement = pos=(135.05,13.925,0) rot=(0,0,-1;1.5708rad)
  LinkedObject = -> Shape138
  Placement = pos=(135.05,13.925,0) rot=(0,0,-1;1.5708rad)
FEATURE [App::Link] R28_R_0805_2012Metric_56a8941a8a89_ln_066  label="R214_R_0805_2012Metric_3d6add19a856"
  LinkPlacement = pos=(169.5,23.5,0) rot=(0,0,1;1.5708rad)
  LinkedObject = -> Shape138
  Placement = pos=(169.5,23.5,0) rot=(0,0,1;1.5708rad)
FEATURE [App::Link] R28_R_0805_2012Metric_56a8941a8a89_ln_067  label="R36_R_0805_2012Metric_a42cad75e8b5"
  LinkPlacement = pos=(139.925,13.775,0) rot=(0,0,-1;1.5708rad)
  LinkedObject = -> Shape138
  Placement = pos=(139.925,13.775,0) rot=(0,0,-1;1.5708rad)
FEATURE [App::Link] R28_R_0805_2012Metric_56a8941a8a89_ln_068  label="R316_R_0805_2012Metric_fb924ddbbf50"
  LinkPlacement = pos=(156.052,29.798,0) rot=(0,0,1;1.5708rad)
  LinkedObject = -> Shape138
  Placement = pos=(156.052,29.798,0) rot=(0,0,1;1.5708rad)
FEATURE [App::Link] R28_R_0805_2012Metric_56a8941a8a89_ln_069  label="R304_R_0805_2012Metric_2a688e8f4435"
  LinkPlacement = pos=(118.131,38.4938,0) rot=(0,0,1;1.5708rad)
  LinkedObject = -> Shape138
  Placement = pos=(118.131,38.4938,0) rot=(0,0,1;1.5708rad)
FEATURE [App::Link] R28_R_0805_2012Metric_56a8941a8a89_ln_070  label="R228_R_0805_2012Metric_f03863a12790"
  LinkPlacement = pos=(117.2,49.4,0) rot=(0,0,1;0rad)
  LinkedObject = -> Shape138
  Placement = pos=(117.2,49.4,0) rot=(0,0,1;0rad)
FEATURE [App::Link] R28_R_0805_2012Metric_56a8941a8a89_ln_071  label="R302_R_0805_2012Metric_fa1ee39c645f"
  LinkPlacement = pos=(107.075,38.875,0) rot=(0,0,1;3.14159rad)
  LinkedObject = -> Shape138
  Placement = pos=(107.075,38.875,0) rot=(0,0,1;3.14159rad)
FEATURE [App::Link] R28_R_0805_2012Metric_56a8941a8a89_ln_072  label="R16_R_0805_2012Metric_b01da35dd508"
  LinkPlacement = pos=(48.7,18.6,0) rot=(0,0,1;3.14159rad)
  LinkedObject = -> Shape138
  Placement = pos=(48.7,18.6,0) rot=(0,0,1;3.14159rad)
FEATURE [App::Link] R28_R_0805_2012Metric_56a8941a8a89_ln_073  label="R236_R_0805_2012Metric_c2c65c50b429"
  LinkPlacement = pos=(179.3,23.7,0) rot=(0,0,1;1.5708rad)
  LinkedObject = -> Shape138
  Placement = pos=(179.3,23.7,0) rot=(0,0,1;1.5708rad)
FEATURE [App::Link] R28_R_0805_2012Metric_56a8941a8a89_ln_074  label="R17_R_0805_2012Metric_430e81cda9d2"
  LinkPlacement = pos=(120.9,9.4,0) rot=(0,0,1;0rad)
  LinkedObject = -> Shape138
  Placement = pos=(120.9,9.4,0) rot=(0,0,1;0rad)
FEATURE [App::Link] R28_R_0805_2012Metric_56a8941a8a89_ln_075  label="R41_R_0805_2012Metric_b5d63ce3a871"
  LinkPlacement = pos=(89.2,44,0) rot=(0,0,1;0rad)
  LinkedObject = -> Shape138
  Placement = pos=(89.2,44,0) rot=(0,0,1;0rad)
FEATURE [App::Link] R28_R_0805_2012Metric_56a8941a8a89_ln_076  label="R306_R_0805_2012Metric_1ae52f8f6f7f"
  LinkPlacement = pos=(49.05,26.2,0) rot=(0,0,1;0rad)
  LinkedObject = -> Shape138
  Placement = pos=(49.05,26.2,0) rot=(0,0,1;0rad)
FEATURE [App::Link] R28_R_0805_2012Metric_56a8941a8a89_ln_077  label="R230_R_0805_2012Metric_bf8a3ed9581b"
  LinkPlacement = pos=(122.5,51,0) rot=(0,0,1;3.14159rad)
  LinkedObject = -> Shape138
  Placement = pos=(122.5,51,0) rot=(0,0,1;3.14159rad)
FEATURE [App::Link] R28_R_0805_2012Metric_56a8941a8a89_ln_078  label="R23_R_0805_2012Metric_437ce9947684"
  LinkPlacement = pos=(32.7,15.4,0) rot=(0,0,1;0rad)
  LinkedObject = -> Shape138
  Placement = pos=(32.7,15.4,0) rot=(0,0,1;0rad)
FEATURE [App::Link] R28_R_0805_2012Metric_56a8941a8a89_ln_079  label="R203_R_0805_2012Metric_44af99049a21"
  LinkPlacement = pos=(121,86.9,0) rot=(0,0,1;0rad)
  LinkedObject = -> Shape138
  Placement = pos=(121,86.9,0) rot=(0,0,1;0rad)
FEATURE [App::Link] R28_R_0805_2012Metric_56a8941a8a89_ln_080  label="R509_R_0805_2012Metric_d00c98e99794"
  LinkPlacement = pos=(111.075,28.35,0) rot=(0,0,1;1.5708rad)
  LinkedObject = -> Shape138
  Placement = pos=(111.075,28.35,0) rot=(0,0,1;1.5708rad)
FEATURE [App::Link] R28_R_0805_2012Metric_56a8941a8a89_ln_081  label="R318_R_0805_2012Metric_d8dd17164e4a"
  LinkPlacement = pos=(32.8625,21.55,0) rot=(0,0,1;3.14159rad)
  LinkedObject = -> Shape138
  Placement = pos=(32.8625,21.55,0) rot=(0,0,1;3.14159rad)
FEATURE [App::Link] R28_R_0805_2012Metric_56a8941a8a89_ln_082  label="R33_R_0805_2012Metric_ee9e5949bf13"
  LinkPlacement = pos=(140.7,28.2625,0) rot=(0,0,-1;1.5708rad)
  LinkedObject = -> Shape138
  Placement = pos=(140.7,28.2625,0) rot=(0,0,-1;1.5708rad)
FEATURE [App::Link] R28_R_0805_2012Metric_56a8941a8a89_ln_083  label="R207_R_0805_2012Metric_bdedbc6ea7d4"
  LinkPlacement = pos=(100.5,87.4,0) rot=(0,0,-1;1.5708rad)
  LinkedObject = -> Shape138
  Placement = pos=(100.5,87.4,0) rot=(0,0,-1;1.5708rad)
FEATURE [App::Link] R28_R_0805_2012Metric_56a8941a8a89_ln_084  label="R209_R_0805_2012Metric_25a065108416"
  LinkPlacement = pos=(93.35,92.4,0) rot=(0,0,1;0rad)
  LinkedObject = -> Shape138
  Placement = pos=(93.35,92.4,0) rot=(0,0,1;0rad)
FEATURE [App::Link] R28_R_0805_2012Metric_56a8941a8a89_ln_085  label="R231_R_0805_2012Metric_e111ffe9ff5f"
  LinkPlacement = pos=(181.3,31.7,0) rot=(0,0,1;1.5708rad)
  LinkedObject = -> Shape138
  Placement = pos=(181.3,31.7,0) rot=(0,0,1;1.5708rad)
FEATURE [App::Link] R28_R_0805_2012Metric_56a8941a8a89_ln_086  label="R31_R_0805_2012Metric_8e5e187749da"
  LinkPlacement = pos=(145.65,29.9,0) rot=(0,0,1;3.14159rad)
  LinkedObject = -> Shape138
  Placement = pos=(145.65,29.9,0) rot=(0,0,1;3.14159rad)
FEATURE [App::Link] R28_R_0805_2012Metric_56a8941a8a89_ln_087  label="R34_R_0805_2012Metric_cce574930be9"
  LinkPlacement = pos=(136.625,28.2625,0) rot=(0,0,-1;1.5708rad)
  LinkedObject = -> Shape138
  Placement = pos=(136.625,28.2625,0) rot=(0,0,-1;1.5708rad)
FEATURE [App::Link] R28_R_0805_2012Metric_56a8941a8a89_ln_088  label="R403_R_0805_2012Metric_388f8d12b48e"
  LinkPlacement = pos=(131.4,8.625,0) rot=(0,0,-1;1.5708rad)
  LinkedObject = -> Shape138
  Placement = pos=(131.4,8.625,0) rot=(0,0,-1;1.5708rad)
FEATURE [App::Link] R28_R_0805_2012Metric_56a8941a8a89_ln_089  label="R227_R_0805_2012Metric_51e4e134bd40"
  LinkPlacement = pos=(150.514,91.632,0) rot=(0,0,1;3.14159rad)
  LinkedObject = -> Shape138
  Placement = pos=(150.514,91.632,0) rot=(0,0,1;3.14159rad)
FEATURE [App::Link] R28_R_0805_2012Metric_56a8941a8a89_ln_090  label="R215_R_0805_2012Metric_b89aa1ef979c"
  LinkPlacement = pos=(173.564,13.44,0) rot=(0,0,1;1.5708rad)
  LinkedObject = -> Shape138
  Placement = pos=(173.564,13.44,0) rot=(0,0,1;1.5708rad)
FEATURE [App::Link] R28_R_0805_2012Metric_56a8941a8a89_ln_091  label="R311_R_0805_2012Metric_05820cc1f1c0"
  LinkPlacement = pos=(36.6,37.1,0) rot=(0,0,1;3.14159rad)
  LinkedObject = -> Shape138
  Placement = pos=(36.6,37.1,0) rot=(0,0,1;3.14159rad)
FEATURE [App::Link] R28_R_0805_2012Metric_56a8941a8a89_ln_092  label="R222_R_0805_2012Metric_985d7a203052"
  LinkPlacement = pos=(98.815,46.3,0) rot=(0,0,1;0rad)
  LinkedObject = -> Shape138
  Placement = pos=(98.815,46.3,0) rot=(0,0,1;0rad)
FEATURE [App::Link] R28_R_0805_2012Metric_56a8941a8a89_ln_093  label="R307_R_0805_2012Metric_97ea5f9f84ef"
  LinkPlacement = pos=(43.85,37.1,0) rot=(0,0,1;3.14159rad)
  LinkedObject = -> Shape138
  Placement = pos=(43.85,37.1,0) rot=(0,0,1;3.14159rad)
FEATURE [App::Link] R28_R_0805_2012Metric_56a8941a8a89_ln_094  label="R14_R_0805_2012Metric_c9232d1a5cfb"
  LinkPlacement = pos=(81,15.8,-1.57252) rot=(0,1,0;3.14159rad)
  LinkedObject = -> Shape138
  Placement = pos=(81,15.8,-1.57252) rot=(0,1,0;3.14159rad)
FEATURE [App::Link] R28_R_0805_2012Metric_56a8941a8a89_ln_095  label="R13_R_0805_2012Metric_f526a781bf16"
  LinkPlacement = pos=(77.5,15.8,-1.57252) rot=(0,1,0;3.14159rad)
  LinkedObject = -> Shape138
  Placement = pos=(77.5,15.8,-1.57252) rot=(0,1,0;3.14159rad)
FEATURE [App::Link] R28_R_0805_2012Metric_56a8941a8a89_ln_096  label="R15_R_0805_2012Metric_05f071cc9f22"
  LinkPlacement = pos=(73.95,15.8,-1.57252) rot=(1,0,0;3.14159rad)
  LinkedObject = -> Shape138
  Placement = pos=(73.95,15.8,-1.57252) rot=(1,0,0;3.14159rad)
FEATURE [App::Part] SWEB_8094_AU___RT_v1  label="J2_SWEB 8094 AU / RT v006_932d9c1a5973"
  Group = -> [Part__Feature400,Part__Feature401,Part__Feature402,Part__Feature403,Part__Feature404]
  Origin = -> Origin014
  Placement = pos=(11.46,18.18,5.5) rot=(0,0,1;3.14159rad)
FEATURE [Part::Feature] Shape138  label="R28_R_0805_2012Metric_56a8941a8a89"
  Placement = pos=(129.7,27.375,0) rot=(0,0,1;3.14159rad)
  shape: bbox 2 x 1.2 x 0.45 mm, 26 faces (baked)
FEATURE [Part::Feature] Shape139  label="C303_C_0805_2012Metric_1d86ef2bb22f"
  Placement = pos=(89.1655,19.502,0) rot=(0,0,1;3.14159rad)
  shape: bbox 2 x 1.25 x 1.25 mm, 28 faces (baked)
FEATURE [Part::Feature] Shape140  label="U18_SOT_23_5_bd1fc933e1e0"
  Placement = pos=(147.35,27.0625,0) rot=(0,0,1;3.14159rad)
  shape: bbox 2.8 x 2.9 x 1.55 mm, 109 faces (baked)
FEATURE [Part::Feature] Shape141  label="Q203_TO-247-3_Vertical_e30fe5b94042"
  Placement = pos=(89,87.82,0) rot=(0,0,1;3.14159rad)
  shape: bbox 15.9 x 5.03 x 41.1 mm, 64 faces (baked)
FEATURE [Part::Feature] Shape142  label="F1_A_Schurter_0031_8201_345dd88a4ad6"
  Placement = pos=(11.075,49.05,0) rot=(0,0,1;0rad)
  shape: bbox 22.8 x 9.6 x 15.5 mm, 119 faces (baked)
FEATURE [Part::Feature] Shape143  label="J7_MC_01x02_G_3_81mm_cf5404935162"
  Placement = pos=(4.8,51,0) rot=(0,0,-1;1.5708rad)
  shape: bbox 9.2 x 9.01 x 10.95 mm, 76 faces (baked)
FEATURE [Part::Feature] Shape144  label="U23_SOT_223_402f57ec59fc001"
  Placement = pos=(67,34.8,0) rot=(0,0,1;3.14159rad)
  shape: bbox 7 x 6.5 x 1.7 mm, 78 faces (baked)
FEATURE [Part::Feature] Shape145  label="U4_SOIC_8_39x49mm_P127mm_5e7587483eba"
  Placement = pos=(105.55,19.9,0) rot=(0,0,1;0rad)
  shape: bbox 6 x 4.9 x 1.75 mm, 156 faces (baked)
FEATURE [Part::Feature] Shape146  label="D208_D_MiniMELF_Standard_5646c313d2d3"
  Placement = pos=(133,92.1,0) rot=(0,0,1;0rad)
  shape: bbox 3.6 x 1.4 x 1.4 mm, 13 faces (baked)
FEATURE [Part::Feature] Shape147  label="Q201_SOT_23_fb4564768f05"
  Placement = pos=(96.2,88.75,0) rot=(0,0,-1;1.5708rad)
  shape: bbox 3 x 2.5 x 1.2 mm, 76 faces (baked)
FEATURE [Part::Feature] Shape148  label="U11_TSSOP_16_44x5mm_P065mm_2417ac1ea51e"
  Placement = pos=(122.775,14.875,0) rot=(0,0,1;0rad)
  shape: bbox 6.4 x 5 x 1.1 mm, 260 faces (baked)
FEATURE [Part::Feature] Shape149  label="U20_TSSOP_20_44x65mm_P065mm_4fdb420d92f4"
  Placement = pos=(139.025,20.075,0) rot=(0,0,-1;1.5708rad)
  shape: bbox 6.5 x 6.4 x 1.2 mm, 336 faces (baked)
FEATURE [Part::Feature] Shape150  label="J8_PinSocket_2x08_P254mm_Vertical_SMD_d83103ec4f9e"
  Placement = pos=(143.48,4.95,0) rot=(0,0,1;1.5708rad)
  shape: bbox 20.32 x 7.94 x 7.3 mm, 570 faces (baked)
FEATURE [Part::Feature] Shape151  label="J9_JST_B2B_XH_A_e9e719df0532"
  Placement = pos=(57.5,90.275,0) rot=(0,0,1;0rad)
  shape: bbox 7.4 x 5.75 x 10.4 mm, 89 faces (baked)
FEATURE [Part::Feature] Shape152  label="U8_SO_4_44x43mm_P254mm_922b2c4537c7"
  Placement = pos=(38.7875,40.65,0) rot=(0,0,1;3.14159rad)
  shape: bbox 7 x 4.3 x 1.6 mm, 96 faces (baked)
FEATURE [Part::Feature] Shape153  label="J3_PinSocket_2x06_P254mm_Vertical_SMD_69addfe34574"
  Placement = pos=(96.98,8.25,0) rot=(0,0,1;0rad)
  shape: bbox 7.94 x 15.24 x 7.3 mm, 430 faces (baked)
FEATURE [Part::Feature] Shape154  label="D203_D_SMC_759b5137743e"
  Placement = pos=(22.2,88.9,0) rot=(0,0,1;3.14159rad)
  shape: bbox 8 x 5.9 x 2.31 mm, 41 faces (baked)
FEATURE [Part::Feature] Shape155  label="HS102_LAM_3_K_93827ea2b8e9"
  Placement = pos=(5.3,70,21) rot=(0.57735,0.57735,0.57735;2.0944rad)
  shape: bbox 10 x 34.69 x 30 mm, 252 faces (baked)
FEATURE [Part::Feature] Shape156  label="J4_PinHeader_2x08_P254mm_Vertical_5fc2a641843f"
  Placement = pos=(73.605,30.925,0) rot=(0,0,1;1.5708rad)
  shape: bbox 20.32 x 5.08 x 11.54 mm, 340 faces (baked)
FEATURE [Part::Feature] Shape157  label="J6_PinHeader_2x03_P254mm_Vertical_SMD_7e3f0c72d359"
  Placement = pos=(159.7,36.8,0) rot=(0,0,1;3.14159rad)
  shape: bbox 7.54 x 7.62 x 9.3 mm, 148 faces (baked)
FEATURE [Part::Feature] Shape158  label="U21_TSOT_23_5_98ea53a2906e001"
  Placement = pos=(96.2,39.4,0) rot=(0,0,1;0rad)
  shape: bbox 2.8 x 2.9 x 0.95 mm, 109 faces (baked)
FEATURE [Part::Feature] Shape159  label="Q101_TO-220-3_Vertical_ee802e7c2218"
  Placement = pos=(72.5,88.838,0) rot=(0,0,1;3.14159rad)
  shape: bbox 10.25 x 4.455 x 28.53 mm, 48 faces (baked)
FEATURE [Part::Feature] Shape160  label="R240_R_2512_6332Metric_fe718b218676"
  Placement = pos=(157.4,9.9,-1.57252) rot=(0.707107,-0.707107,0;3.14159rad)
  shape: bbox 3.2 x 6.3 x 0.6 mm, 26 faces (baked)
FEATURE [App::Part] Bot_29d
  Group = -> [R28_R_0805_2012Metric_56a8941a8a89_ln_094,Shape160,R28_R_0805_2012Metric_56a8941a8a89_ln_095,D208_D_MiniMELF_Standard_5646c313d2d3_ln_009,D208_D_MiniMELF_Standard_5646c313d2d3_ln_010,R240_R_2512_6332Metric_fe718b218676_ln_,Q201_SOT_23_fb4564768f05_ln_013,R240_R_2512_6332Metric_fe718b218676_ln_001,R28_R_0805_2012Metric_56a8941a8a89_ln_096,R240_R_2512_6332Metric_fe718b218676_ln_002]
  Origin = -> Origin086
FEATURE [App::Part] TopV_29d
  Group = -> [Shape155]
  Origin = -> Origin006
FEATURE [App::Part] Step_Virtual_Models_29d
  Group = -> [TopV_29d]
  Origin = -> Origin005
FEATURE [App::Link] U11_TSSOP_16_44x5mm_P065mm_2417ac1ea51e_ln_  label="U12_TSSOP_16_44x5mm_P065mm_b3bc334b253a"
  LinkPlacement = pos=(122.8,22.225,0) rot=(0,0,1;0rad)
  LinkedObject = -> Shape148
  Placement = pos=(122.8,22.225,0) rot=(0,0,1;0rad)
FEATURE [App::Link] U18_SOT_23_5_bd1fc933e1e0_ln_  label="U208_SOT_23_5_f89bbcba48aa"
  LinkPlacement = pos=(164.4,9.5,0) rot=(0,0,-1;1.5708rad)
  LinkedObject = -> Shape140
  Placement = pos=(164.4,9.5,0) rot=(0,0,-1;1.5708rad)
FEATURE [App::Link] U18_SOT_23_5_bd1fc933e1e0_ln_001  label="U17_SOT_23_5_436ec76bf38b"
  LinkPlacement = pos=(143.7,36.8875,0) rot=(0,0,-1;1.5708rad)
  LinkedObject = -> Shape140
  Placement = pos=(143.7,36.8875,0) rot=(0,0,-1;1.5708rad)
FEATURE [App::Link] U18_SOT_23_5_bd1fc933e1e0_ln_002  label="U15_SOT_23_5_f0dbcf2746ad"
  LinkPlacement = pos=(134.55,37.35,0) rot=(0,0,-1;1.5708rad)
  LinkedObject = -> Shape140
  Placement = pos=(134.55,37.35,0) rot=(0,0,-1;1.5708rad)
FEATURE [App::Link] U18_SOT_23_5_bd1fc933e1e0_ln_003  label="U204_SOT_23_5_03575cd2eb1a"
  LinkPlacement = pos=(170.453,27.497,0) rot=(0,0,-1;1.5708rad)
  LinkedObject = -> Shape140
  Placement = pos=(170.453,27.497,0) rot=(0,0,-1;1.5708rad)
FEATURE [App::Link] U18_SOT_23_5_bd1fc933e1e0_ln_004  label="U19_SOT_23_5_20d0edf1befc"
  LinkPlacement = pos=(133.387,30.2,0) rot=(0,0,1;0rad)
  LinkedObject = -> Shape140
  Placement = pos=(133.387,30.2,0) rot=(0,0,1;0rad)
FEATURE [App::Link] U18_SOT_23_5_bd1fc933e1e0_ln_005  label="U303_SOT_23_5_a2d428d63c40"
  LinkPlacement = pos=(49.0136,29.5848,0) rot=(0,0,-1;1.5708rad)
  LinkedObject = -> Shape140
  Placement = pos=(49.0136,29.5848,0) rot=(0,0,-1;1.5708rad)
FEATURE [App::Link] U18_SOT_23_5_bd1fc933e1e0_ln_006  label="U203_SOT_23_5_686605622b05"
  LinkPlacement = pos=(176.55,9.45,0) rot=(0,0,-1;1.5708rad)
  LinkedObject = -> Shape140
  Placement = pos=(176.55,9.45,0) rot=(0,0,-1;1.5708rad)
FEATURE [App::Link] U18_SOT_23_5_bd1fc933e1e0_ln_007  label="U304_SOT_23_5_069fc6069df6"
  LinkPlacement = pos=(157.04,25.5816,0) rot=(0,0,1;1.5708rad)
  LinkedObject = -> Shape140
  Placement = pos=(157.04,25.5816,0) rot=(0,0,1;1.5708rad)
FEATURE [App::Link] U18_SOT_23_5_bd1fc933e1e0_ln_008  label="U207_SOT_23_5_5b9b638b9293"
  LinkPlacement = pos=(182.5,27.7,0) rot=(0,0,-1;1.5708rad)
  LinkedObject = -> Shape140
  Placement = pos=(182.5,27.7,0) rot=(0,0,-1;1.5708rad)
FEATURE [App::Link] U23_SOT_223_402f57ec59fc_ln_001  label="U22_SOT_223_6c512a09e792"
  LinkPlacement = pos=(86.8,39.2,0) rot=(0,0,1;0rad)
  LinkedObject = -> Shape144
  Placement = pos=(86.8,39.2,0) rot=(0,0,1;0rad)
FEATURE [App::Link] U305_CQ_assembly_5f207b676c46_ln_  label="U403_CQ assembly_59e6374d4606"
  LinkPlacement = pos=(107.99,4.4,0) rot=(0,0,1;1.5708rad)
  LinkedObject = -> CQ_assembly
  Placement = pos=(107.99,4.4,0) rot=(0,0,1;1.5708rad)
FEATURE [App::Link] U4_SOIC_8_39x49mm_P127mm_5e7587483eba_ln_  label="U205_SOIC_8_39x49mm_P127mm_c7dffb358f61"
  LinkPlacement = pos=(168.5,89.5,0) rot=(0,0,1;3.14159rad)
  LinkedObject = -> Shape145
  Placement = pos=(168.5,89.5,0) rot=(0,0,1;3.14159rad)
FEATURE [App::Link] U4_SOIC_8_39x49mm_P127mm_5e7587483eba_ln_001  label="U201_SOIC_8_39x49mm_P127mm_d6a775eb0fcb"
  LinkPlacement = pos=(109.2,89.55,0) rot=(0,0,1;3.14159rad)
  LinkedObject = -> Shape145
  Placement = pos=(109.2,89.55,0) rot=(0,0,1;3.14159rad)
FEATURE [App::Link] U4_SOIC_8_39x49mm_P127mm_5e7587483eba_ln_002  label="U302_SOIC_8_39x49mm_P127mm_e17913fd2d67"
  LinkPlacement = pos=(90.9435,23.312,0) rot=(0,0,1;3.14159rad)
  LinkedObject = -> Shape145
  Placement = pos=(90.9435,23.312,0) rot=(0,0,1;3.14159rad)
FEATURE [App::Link] U4_SOIC_8_39x49mm_P127mm_5e7587483eba_ln_003  label="U306_SOIC_8_39x49mm_P127mm_c9db6429261b"
  LinkPlacement = pos=(62.3,21.2,0) rot=(0,0,1;0rad)
  LinkedObject = -> Shape145
  Placement = pos=(62.3,21.2,0) rot=(0,0,1;0rad)
FEATURE [App::Link] U4_SOIC_8_39x49mm_P127mm_5e7587483eba_ln_004  label="U301_SOIC_8_39x49mm_P127mm_0413ce41aa29"
  LinkPlacement = pos=(113.231,37.9938,0) rot=(0,0,1;0rad)
  LinkedObject = -> Shape145
  Placement = pos=(113.231,37.9938,0) rot=(0,0,1;0rad)
FEATURE [App::Link] U4_SOIC_8_39x49mm_P127mm_5e7587483eba_ln_005  label="U402_SOIC_8_39x49mm_P127mm_2080084d9265"
  LinkPlacement = pos=(123.125,3.4,0) rot=(0,0,1;0rad)
  LinkedObject = -> Shape145
  Placement = pos=(123.125,3.4,0) rot=(0,0,1;0rad)
FEATURE [App::Link] U4_SOIC_8_39x49mm_P127mm_5e7587483eba_ln_006  label="U10_SOIC_8_39x49mm_P127mm_88c4924da8b3"
  LinkPlacement = pos=(106.1,29,0) rot=(0,0,1;0rad)
  LinkedObject = -> Shape145
  Placement = pos=(106.1,29,0) rot=(0,0,1;0rad)
FEATURE [App::Link] U4_SOIC_8_39x49mm_P127mm_5e7587483eba_ln_007  label="U202_SOIC_8_39x49mm_P127mm_747131a1281f"
  LinkPlacement = pos=(53.9,49.5,0) rot=(0,0,1;0rad)
  LinkedObject = -> Shape145
  Placement = pos=(53.9,49.5,0) rot=(0,0,1;0rad)
FEATURE [App::Link] U4_SOIC_8_39x49mm_P127mm_5e7587483eba_ln_008  label="U206_SOIC_8_39x49mm_P127mm_1ada100df058"
  LinkPlacement = pos=(108.429,49.08,0) rot=(0,0,1;0rad)
  LinkedObject = -> Shape145
  Placement = pos=(108.429,49.08,0) rot=(0,0,1;0rad)
FEATURE [App::Link] U4_SOIC_8_39x49mm_P127mm_5e7587483eba_ln_009  label="U401_SOIC_8_39x49mm_P127mm_e9e5c7414b6c"
  LinkPlacement = pos=(56.725,40.05,0) rot=(0,0,1;0rad)
  LinkedObject = -> Shape145
  Placement = pos=(56.725,40.05,0) rot=(0,0,1;0rad)
FEATURE [App::Link] U8_SO_4_44x43mm_P254mm_922b2c4537c7_ln_  label="U9_SO_4_44x43mm_P254mm_234cd6d6f7de"
  LinkPlacement = pos=(38.6,18,0) rot=(0,0,1;3.14159rad)
  LinkedObject = -> Shape152
  Placement = pos=(38.6,18,0) rot=(0,0,1;3.14159rad)
FEATURE [App::Part] _29b0bae_9266_11ed_9e62_a0cec80452fd  label="729b0bae-9266-11ed-9e62-a0cec80452fd"
  Group = -> [Part__Feature405]
  Origin = -> Origin015
FEATURE [App::Part] _29b0e92_9266_11ed_9e62_a0cec80452fd_part  label="729b0e92-9266-11ed-9e62-a0cec80452fd_part008"
  Group = -> [Part__Feature406,Part__Feature407,Part__Feature408,Part__Feature409,Part__Feature410,Part__Feature411,Part__Feature412,Part__Feature413]
  Origin = -> Origin016
FEATURE [App::Part] _29b0e92_9266_11ed_9e62_a0cec80452fd  label="729b0e92-9266-11ed-9e62-a0cec80452fd"
  Group = -> [_29b0e92_9266_11ed_9e62_a0cec80452fd_part]
  Origin = -> Origin017
FEATURE [App::Part] _29b1108_9266_11ed_9e62_a0cec80452fd  label="729b1108-9266-11ed-9e62-a0cec80452fd"
  Group = -> [Part__Feature414]
  Origin = -> Origin018
FEATURE [App::Part] _29b06ae_9266_11ed_9e62_a0cec80452fd  label="729b06ae-9266-11ed-9e62-a0cec80452fd"
  Group = -> [_29b0bae_9266_11ed_9e62_a0cec80452fd,_29b0e92_9266_11ed_9e62_a0cec80452fd,_29b1108_9266_11ed_9e62_a0cec80452fd]
  Origin = -> Origin019
FEATURE [App::Part] CQ_assembly001  label="U5_CQ assembly_2818d1c648ca"
  Group = -> [_29b06ae_9266_11ed_9e62_a0cec80452fd]
  Origin = -> Origin089
  Placement = pos=(47.45,3.25,0) rot=(0,0,1;3.14159rad)
FEATURE [App::Part] _712e517_7b30_11ed_bcdd_db420251a6ca  label="5712e517-7b30-11ed-bcdd-db420251a6ca"
  Group = -> [Part__Feature384]
  Origin = -> Origin087
FEATURE [App::Part] _712e518_7b30_11ed_bcdd_db420251a6ca_part  label="5712e518-7b30-11ed-bcdd-db420251a6ca_part014"
  Group = -> [Part__Feature385,Part__Feature386,Part__Feature387,Part__Feature388,Part__Feature389,Part__Feature390,Part__Feature391,Part__Feature392,Part__Feature393,Part__Feature394,Part__Feature395,Part__Feature396,Part__Feature397,Part__Feature398]
  Origin = -> Origin088
FEATURE [App::Part] _712e518_7b30_11ed_bcdd_db420251a6ca  label="5712e518-7b30-11ed-bcdd-db420251a6ca"
  Group = -> [_712e518_7b30_11ed_bcdd_db420251a6ca_part]
  Origin = -> Origin010
FEATURE [App::Part] _712e519_7b30_11ed_bcdd_db420251a6ca  label="5712e519-7b30-11ed-bcdd-db420251a6ca"
  Group = -> [Part__Feature399]
  Origin = -> Origin011
FEATURE [App::Part] _712e516_7b30_11ed_bcdd_db420251a6ca  label="5712e516-7b30-11ed-bcdd-db420251a6ca"
  Group = -> [_712e517_7b30_11ed_bcdd_db420251a6ca,_712e518_7b30_11ed_bcdd_db420251a6ca,_712e519_7b30_11ed_bcdd_db420251a6ca]
  Origin = -> Origin012
FEATURE [App::Part] CQ_assembly  label="U305_CQ assembly_5f207b676c46"
  Group = -> [_712e516_7b30_11ed_bcdd_db420251a6ca]
  Origin = -> Origin013
  Placement = pos=(74.575,22.135,0) rot=(0,0,1;3.14159rad)
FEATURE [App::Part] Top_29d
  Group = -> [Shape138,Shape139,C303_C_0805_2012Metric_1d86ef2bb22f_ln_,Shape140,Shape141,Shape142,C303_C_0805_2012Metric_1d86ef2bb22f_ln_001,C303_C_0805_2012Metric_1d86ef2bb22f_ln_002,R28_R_0805_2012Metric_56a8941a8a89_ln_,Shape143,C303_C_0805_2012Metric_1d86ef2bb22f_ln_003,C303_C_0805_2012Metric_1d86ef2bb22f_ln_004,R28_R_0805_2012Metric_56a8941a8a89_ln_001,R28_R_0805_2012Metric_56a8941a8a89_ln_002,+240 more]
  Origin = -> Origin085
FEATURE [App::Part] Step_Models_29d
  Group = -> [Top_29d,Bot_29d]
  Origin = -> Origin084
FEATURE [App::Part] Board_29d  label="EL-Load-Analog"
  Group = -> [Local_CS_29d,Board_Geoms_29d,Step_Models_29d,Step_Virtual_Models_29d]
  Origin = -> Origin083
  Placement = pos=(0,84,1.5) rot=(0,0,1;0rad)
FEATURE [Sketcher::SketchObject] Sketch010  label="Analog cutouts"
  ArcFitTolerance = 0
  AttachmentSupport = -> [YZ_Plane069]
  FullyConstrained = true
  MakeInternals = false
  MapMode = 5
  Placement = pos=(0,0,0) rot=(0.57735,0.57735,0.57735;2.0944rad)
  sketch-geometry (36):
    g0: Circle CenterX=121.17 CenterY=7 CenterZ=0 NormalX=0 NormalY=0 NormalZ=1 AngleXU=0 Radius=6
    g1: Circle CenterX=102.17 CenterY=7 CenterZ=0 NormalX=0 NormalY=0 NormalZ=1 AngleXU=0 Radius=6
    g2: LineSegment StartX=138.28 StartY=9.5 StartZ=0 EndX=127.88 EndY=9.5 EndZ=0
    g3: LineSegment StartX=127.88 StartY=9.5 StartZ=0 EndX=127.88 EndY=1 EndZ=0
    g4: LineSegment StartX=127.88 StartY=1 StartZ=0 EndX=138.28 EndY=1 EndZ=0
    g5: LineSegment StartX=138.28 StartY=1 StartZ=0 EndX=138.28 EndY=9.5 EndZ=0
    g6: LineSegment [constr] StartX=127.88 StartY=1 StartZ=0 EndX=121.17 EndY=1 EndZ=0
    g7: ArcOfCircle CenterX=172 CenterY=47.45 CenterZ=0 NormalX=0 NormalY=0 NormalZ=1 AngleXU=0 Radius=2.5 StartAngle=5.07e-14 EndAngle=3.14159
    g8: ArcOfCircle CenterX=172 CenterY=-7.55 CenterZ=0 NormalX=0 NormalY=0 NormalZ=1 AngleXU=0 Radius=2.5 StartAngle=3.14159 EndAngle=6.28319
    g9: LineSegment StartX=169.5 StartY=47.45 StartZ=0 EndX=169.5 EndY=-7.55 EndZ=0
    g10: LineSegment StartX=174.5 StartY=-7.55 StartZ=0 EndX=174.5 EndY=47.45 EndZ=0
    g11: ArcOfCircle CenterX=166 CenterY=47.45 CenterZ=0 NormalX=0 NormalY=0 NormalZ=1 AngleXU=0 Radius=2.5 StartAngle=-9.95e-14 EndAngle=3.14159
    g12: ArcOfCircle CenterX=166 CenterY=-7.55 CenterZ=0 NormalX=0 NormalY=0 NormalZ=1 AngleXU=0 Radius=2.5 StartAngle=3.14159 EndAngle=6.28319
    g13: LineSegment StartX=163.5 StartY=47.45 StartZ=0 EndX=163.5 EndY=-7.55 EndZ=0
    g14: LineSegment StartX=168.5 StartY=-7.55 StartZ=0 EndX=168.5 EndY=47.45 EndZ=0
    g15: ArcOfCircle CenterX=160 CenterY=47.45 CenterZ=0 NormalX=0 NormalY=0 NormalZ=1 AngleXU=0 Radius=2.5 StartAngle=-9.33e-14 EndAngle=3.14159
    g16: ArcOfCircle CenterX=160 CenterY=-7.55 CenterZ=0 NormalX=0 NormalY=0 NormalZ=1 AngleXU=0 Radius=2.5 StartAngle=3.14159 EndAngle=6.28319
    g17: LineSegment StartX=157.5 StartY=47.45 StartZ=0 EndX=157.5 EndY=-7.55 EndZ=0
    g18: LineSegment StartX=162.5 StartY=-7.55 StartZ=0 EndX=162.5 EndY=47.45 EndZ=0
    g19: ArcOfCircle CenterX=154 CenterY=47.45 CenterZ=0 NormalX=0 NormalY=0 NormalZ=1 AngleXU=0 Radius=2.5 StartAngle=-7.82e-14 EndAngle=3.14159
    g20: ArcOfCircle CenterX=154 CenterY=-7.55 CenterZ=0 NormalX=0 NormalY=0 NormalZ=1 AngleXU=0 Radius=2.5 StartAngle=3.14159 EndAngle=6.28319
    g21: LineSegment StartX=151.5 StartY=47.45 StartZ=0 EndX=151.5 EndY=-7.55 EndZ=0
    g22: LineSegment StartX=156.5 StartY=-7.55 StartZ=0 EndX=156.5 EndY=47.45 EndZ=0
    g23: ArcOfCircle CenterX=148 CenterY=47.45 CenterZ=0 NormalX=0 NormalY=0 NormalZ=1 AngleXU=0 Radius=2.5 StartAngle=-5.6e-14 EndAngle=3.14159
    g24: ArcOfCircle CenterX=148 CenterY=-7.55 CenterZ=0 NormalX=0 NormalY=0 NormalZ=1 AngleXU=0 Radius=2.5 StartAngle=3.14159 EndAngle=6.28319
    g25: LineSegment StartX=145.5 StartY=47.45 StartZ=0 EndX=145.5 EndY=-7.55 EndZ=0
    g26: LineSegment StartX=150.5 StartY=-7.55 StartZ=0 EndX=150.5 EndY=47.45 EndZ=0
    g27: LineSegment [constr] StartX=169.5 StartY=47.45 StartZ=0 EndX=168.5 EndY=47.45 EndZ=0
    g28: LineSegment [constr] StartX=163.5 StartY=47.45 StartZ=0 EndX=162.5 EndY=47.45 EndZ=0
    g29: LineSegment [constr] StartX=157.5 StartY=47.45 StartZ=0 EndX=156.5 EndY=47.45 EndZ=0
    g30: LineSegment [constr] StartX=151.5 StartY=47.45 StartZ=0 EndX=150.5 EndY=47.45 EndZ=0
    g31: ArcOfCircle CenterX=142 CenterY=47.45 CenterZ=0 NormalX=0 NormalY=0 NormalZ=1 AngleXU=0 Radius=2.5 StartAngle=-3.02e-14 EndAngle=3.14159
    g32: ArcOfCircle CenterX=142 CenterY=-7.55 CenterZ=0 NormalX=0 NormalY=0 NormalZ=1 AngleXU=0 Radius=2.5 StartAngle=3.14159 EndAngle=6.28319
    g33: LineSegment StartX=139.5 StartY=47.45 StartZ=0 EndX=139.5 EndY=-7.55 EndZ=0
    g34: LineSegment StartX=144.5 StartY=-7.55 StartZ=0 EndX=144.5 EndY=47.45 EndZ=0
    g35: LineSegment [constr] StartX=145.5 StartY=47.45 StartZ=0 EndX=144.5 EndY=47.45 EndZ=0
  constraints (90):
    c: Coincident(g2,g3)
    c: Coincident(g3,g4)
    c: Coincident(g4,g5)
    c: Coincident(g5,g2)
    c: Horizontal(g2)
    c: Horizontal(g4)
    c: Vertical(g3)
    c: Vertical(g5)
    c: Horizontal(g0,g1)
    c: Equal(g0,g1)
    c: Diameter(g1) = 12
    c: DistanceX(g2,g2) = 10.4
    c: Distance(g5) = 8.5
    c: DistanceX(g1,g0) = 19
    c: Coincident(g6,g3)
    c: Horizontal(g6)
    c: Tangent(g6,g0) = 1.5708
    c: DistanceY(g-1,g6) = 1
    c: DistanceX(g-1,g1) = 102.17
    c: DistanceX(g6,g6) = 6.71
    c: Tangent(g7,g9) = -1.5708
    c: Tangent(g9,g8) = -1.5708
    c: Tangent(g8,g10) = -1.5708
    c: Tangent(g10,g7) = -1.5708
    c: Equal(g7,g8)
    c: Vertical(g9)
    c: Diameter(g7) = 5
    c: Distance(g10) = 55
    c: DistanceX(g8) = 172
    c: DistanceY(g8) = -7.55
    c: Tangent(g11,g13) = -1.5708
    c: Tangent(g13,g12) = -1.5708
    c: Tangent(g12,g14) = -1.5708
    c: Tangent(g14,g11) = -1.5708
    c: Equal(g11,g12)
    c: Vertical(g13)
    c: Equal(g7,g11)
    c: Equal(g14,g9)
    c: Tangent(g15,g17) = -1.5708
    c: Tangent(g17,g16) = -1.5708
    c: Tangent(g16,g18) = -1.5708
    c: Tangent(g18,g15) = -1.5708
    c: Equal(g15,g16)
    c: Vertical(g17)
    c: Tangent(g19,g21) = -1.5708
    c: Tangent(g21,g20) = -1.5708
    c: Tangent(g20,g22) = -1.5708
    c: Tangent(g22,g19) = -1.5708
    c: Equal(g19,g20)
    c: Vertical(g21)
    c: Equal(g7,g15)
    c: Equal(g7,g19)
    c: Equal(g18,g9)
    c: Equal(g22,g9)
    c: Horizontal(g15,g11)
    c: Horizontal(g11,g7)
    c: Horizontal(g19,g15)
    c: Tangent(g23,g25) = -1.5708
    c: Tangent(g25,g24) = -1.5708
    c: Tangent(g24,g26) = -1.5708
    c: Tangent(g26,g23) = -1.5708
    c: Equal(g23,g24)
    c: Vertical(g25)
    c: Equal(g7,g23)
    c: Equal(g26,g9)
    c: Horizontal(g19,g23)
    c: Coincident(g27,g7)
    c: Coincident(g27,g11)
    c: Coincident(g28,g11)
    c: Coincident(g28,g15)
    c: Coincident(g29,g15)
    c: Coincident(g29,g19)
    c: Coincident(g30,g19)
    c: Coincident(g30,g23)
    c: Equal(g27,g28)
    c: Equal(g28,g29)
    c: Equal(g29,g30)
    c: Distance(g30) = 1
    c: Tangent(g31,g33) = -1.5708
    c: Tangent(g33,g32) = -1.5708
    c: Tangent(g32,g34) = -1.5708
    c: Tangent(g34,g31) = -1.5708
    c: Equal(g31,g32)
    c: Vertical(g33)
    c: Equal(g7,g31)
    c: Equal(g34,g9)
    c: Horizontal(g31,g23)
    c: Coincident(g35,g23)
    c: Coincident(g35,g31)
    c: Equal(g35,g30)
FEATURE [PartDesign::Pad] Pad004
  Direction = (1,0,0)
  Length = 1.83
  Length2 = 10
  Placement = pos=(0,0,0) rot=(1,1,1;2.0944rad)
  Profile = -> Sketch007
  ReferenceAxis = -> Sketch007 [N_Axis]
  Reversed = true
  Suppressed = false
  Type = 0
FEATURE [PartDesign::Chamfer] Chamfer
  Angle = 45
  Base = -> Pad004 [Edge33,Edge36,Edge30,Edge27]
  BaseFeature = -> Pad004
  ChamferType = 0
  FlipDirection = false
  Placement = pos=(0,0,0) rot=(1,1,1;2.0944rad)
  Size = 1.6
  Size2 = 1
  SupportTransform = false
  Suppressed = false
  UseAllEdges = false
FEATURE [PartDesign::Pocket] Pocket003
  BaseFeature = -> Chamfer
  Direction = (-1,0,0)
  Length = 5
  Length2 = 5
  Placement = pos=(0,0,0) rot=(1,1,1;2.0944rad)
  Profile = -> Sketch010
  ReferenceAxis = -> Sketch010 [N_Axis]
  Suppressed = false
  Type = 0
FEATURE [Sketcher::SketchObject] Sketch011
  ArcFitTolerance = 0
  AttachmentSupport = -> [YZ_Plane069]
  FullyConstrained = true
  MakeInternals = false
  MapMode = 5
  Placement = pos=(0,0,0) rot=(0.57735,0.57735,0.57735;2.0944rad)
  sketch-geometry (15):
    g0: Circle CenterX=123.99 CenterY=34.2979 CenterZ=0 NormalX=0 NormalY=0 NormalZ=1 AngleXU=0 Radius=1.75
    g1: Circle CenterX=95.6034 CenterY=33.9737 CenterZ=0 NormalX=0 NormalY=0 NormalZ=1 AngleXU=0 Radius=3.5
    g2: LineSegment StartX=74.79 StartY=42.16 StartZ=0 EndX=14.14 EndY=42.16 EndZ=0
    g3: LineSegment StartX=14.14 StartY=42.16 StartZ=0 EndX=14.14 EndY=-4 EndZ=0
    g4: LineSegment StartX=14.14 StartY=-4 StartZ=0 EndX=74.79 EndY=-4 EndZ=0
    g5: LineSegment StartX=74.79 StartY=-4 StartZ=0 EndX=74.79 EndY=42.16 EndZ=0
    g6: LineSegment StartX=116.776 StartY=42.1588 StartZ=0 EndX=116.776 EndY=30.1588 EndZ=0
    g7: LineSegment StartX=116.776 StartY=30.1588 StartZ=0 EndX=106.776 EndY=30.1588 EndZ=0
    g8: LineSegment StartX=106.776 StartY=30.1588 StartZ=0 EndX=106.776 EndY=42.1588 EndZ=0
    g9: LineSegment StartX=106.776 StartY=42.1588 StartZ=0 EndX=107.776 EndY=42.1588 EndZ=0
    g10: LineSegment StartX=107.776 StartY=42.1588 StartZ=0 EndX=107.776 EndY=31.1588 EndZ=0
    g11: LineSegment StartX=107.776 StartY=31.1588 StartZ=0 EndX=115.776 EndY=31.1588 EndZ=0
    g12: LineSegment StartX=115.776 StartY=31.1588 StartZ=0 EndX=115.776 EndY=42.1588 EndZ=0
    g13: LineSegment StartX=115.776 StartY=42.1588 StartZ=0 EndX=116.776 EndY=42.1588 EndZ=0
    g14: LineSegment [constr] StartX=115.776 StartY=31.1588 StartZ=0 EndX=115.776 EndY=30.1588 EndZ=0
  constraints (45):
    c: Coincident(g2,g3)
    c: Coincident(g3,g4)
    c: Coincident(g4,g5)
    c: Coincident(g5,g2)
    c: Horizontal(g2)
    c: Horizontal(g4)
    c: Vertical(g3)
    c: Vertical(g5)
    c: Vertical(g6)
    c: Coincident(g6,g7)
    c: Horizontal(g7)
    c: Coincident(g7,g8)
    c: Vertical(g8)
    c: Coincident(g8,g9)
    c: Horizontal(g9)
    c: Coincident(g9,g10)
    c: Vertical(g10)
    c: Coincident(g10,g11)
    c: Horizontal(g11)
    c: Coincident(g11,g12)
    c: Vertical(g12)
    c: Coincident(g12,g13)
    c: Coincident(g13,g6)
    c: Horizontal(g13)
    c: Horizontal(g12,g9)
    c: Equal(g13,g9)
    c: Distance(g9) = 1
    c: Coincident(g14,g11)
    c: PointOnObject(g14,g7)
    c: Vertical(g14)
    c: Equal(g14,g13)
    c: Distance(g9,g12) = 8
    c: Distance(g8) = 12
    c: DistanceX(g1) = 95.6034
    c: DistanceY(g1) = 33.9737
    c: DistanceX(g0) = 123.99
    c: DistanceY(g0) = 34.2979
    c: DistanceX(g7) = 106.776
    c: DistanceY(g7) = 30.1588
    c: Diameter(g1) = 7
    c: Diameter(g0) = 3.5
    c: DistanceX(g3) = 14.14
    c: DistanceY(g3) = -4
    c: Distance(g5) = 46.16
    c: Distance(g2) = 60.65
FEATURE [Sketcher::SketchObject] Sketch012
  ArcFitTolerance = 0
  AttachmentSupport = -> [YZ_Plane069]
  FullyConstrained = true
  MakeInternals = false
  MapMode = 5
  Placement = pos=(0,0,0) rot=(0.57735,0.57735,0.57735;2.0944rad)
  sketch-geometry (12):
    g0: Circle CenterX=120.903 CenterY=41.7901 CenterZ=0 NormalX=0 NormalY=0 NormalZ=1 AngleXU=0 Radius=1.45
    g1: Circle CenterX=120.903 CenterY=26.7901 CenterZ=0 NormalX=0 NormalY=0 NormalZ=1 AngleXU=0 Radius=1.45
    g2: Circle CenterX=78.9035 CenterY=41.7901 CenterZ=0 NormalX=0 NormalY=0 NormalZ=1 AngleXU=0 Radius=1.45
    g3: Circle CenterX=3.90349 CenterY=41.7901 CenterZ=0 NormalX=0 NormalY=0 NormalZ=1 AngleXU=0 Radius=1.45
    g4: Circle CenterX=3.90349 CenterY=-3.20994 CenterZ=0 NormalX=0 NormalY=0 NormalZ=1 AngleXU=0 Radius=1.45
    g5: Circle CenterX=78.9035 CenterY=-3.20994 CenterZ=0 NormalX=0 NormalY=0 NormalZ=1 AngleXU=0 Radius=1.45
    g6: Circle CenterX=3.90349 CenterY=-3.20994 CenterZ=0 NormalX=0 NormalY=0 NormalZ=1 AngleXU=0 Radius=3
    g7: Circle CenterX=3.90349 CenterY=41.7901 CenterZ=0 NormalX=0 NormalY=0 NormalZ=1 AngleXU=0 Radius=3
    g8: Circle CenterX=78.9035 CenterY=41.7901 CenterZ=0 NormalX=0 NormalY=0 NormalZ=1 AngleXU=0 Radius=3
    g9: Circle CenterX=120.903 CenterY=41.7901 CenterZ=0 NormalX=0 NormalY=0 NormalZ=1 AngleXU=0 Radius=3
    g10: Circle CenterX=120.903 CenterY=26.7901 CenterZ=0 NormalX=0 NormalY=0 NormalZ=1 AngleXU=0 Radius=3
    g11: Circle CenterX=78.9035 CenterY=-3.20994 CenterZ=0 NormalX=0 NormalY=0 NormalZ=1 AngleXU=0 Radius=3
  constraints (30):
    c: Horizontal(g0,g2)
    c: Horizontal(g2,g3)
    c: Horizontal(g5,g4)
    c: Vertical(g5,g2)
    c: Vertical(g1,g0)
    c: Vertical(g4,g3)
    c: Equal(g4,g3)
    c: Equal(g3,g2)
    c: Equal(g2,g5)
    c: Equal(g5,g1)
    c: Equal(g1,g0)
    c: Distance(g0,g1) = 15
    c: Distance(g0,g2) = 42
    c: DistanceX(g3,g2) = 75
    c: DistanceY(g4,g3) = 45
    c: Diameter(g5) = 2.9
    c: DistanceX(g4) = 3.90349
    c: DistanceY(g4) = -3.20994
    c: Coincident(g6,g4)
    c: Coincident(g7,g3)
    c: Coincident(g8,g2)
    c: Coincident(g9,g0)
    c: Coincident(g10,g1)
    c: Coincident(g11,g5)
    c: Diameter(g11) = 6
    c: Equal(g11,g10)
    c: Equal(g10,g9)
    c: Equal(g9,g8)
    c: Equal(g8,g7)
    c: Equal(g7,g6)
FEATURE [PartDesign::Pad] Pad005
  BaseFeature = -> Pocket003
  Direction = (1,0,0)
  Length = 4.5
  Length2 = 10
  Placement = pos=(0,0,0) rot=(1,1,1;2.0944rad)
  Profile = -> Sketch012
  ReferenceAxis = -> Sketch012 [N_Axis]
  Suppressed = false
  Type = 0
FEATURE [PartDesign::Pocket] Pocket004
  BaseFeature = -> Pad005
  Direction = (-1,0,0)
  Length = 15
  Length2 = 5
  Midplane = true
  Placement = pos=(0,0,0) rot=(1,1,1;2.0944rad)
  Profile = -> Sketch011
  ReferenceAxis = -> Sketch011 [N_Axis]
  Suppressed = false
  Type = 0
FEATURE [PartDesign::Chamfer] Chamfer001
  Angle = 45
  Base = -> Pocket004 [Edge120,Edge117,Edge118,Edge119]
  BaseFeature = -> Pocket004
  ChamferType = 0
  FlipDirection = false
  Placement = pos=(0,0,0) rot=(1,1,1;2.0944rad)
  Size = 1
  Size2 = 1
  SupportTransform = false
  Suppressed = false
  UseAllEdges = false
FEATURE [Sketcher::SketchObject] Sketch013
  ArcFitTolerance = 0
  AttachmentSupport = -> [YZ_Plane069]
  FullyConstrained = true
  MakeInternals = false
  MapMode = 5
  Placement = pos=(0,0,0) rot=(0.57735,0.57735,0.57735;2.0944rad)
  sketch-geometry (4):
    g0: LineSegment StartX=76.75 StartY=45.9 StartZ=0 EndX=6.25 EndY=45.9 EndZ=0
    g1: LineSegment StartX=6.25 StartY=45.9 StartZ=0 EndX=6.25 EndY=-7.1 EndZ=0
    g2: LineSegment StartX=6.25 StartY=-7.1 StartZ=0 EndX=76.75 EndY=-7.1 EndZ=0
    g3: LineSegment StartX=76.75 StartY=-7.1 StartZ=0 EndX=76.75 EndY=45.9 EndZ=0
  constraints (12):
    c: Coincident(g0,g1)
    c: Coincident(g1,g2)
    c: Coincident(g2,g3)
    c: Coincident(g3,g0)
    c: Horizontal(g0)
    c: Horizontal(g2)
    c: Vertical(g1)
    c: Vertical(g3)
    c: DistanceX(g1) = 6.25
    c: DistanceY(g1) = -7.1
    c: DistanceX(g2,g2) = 70.5
    c: DistanceY(g3,g3) = 53
FEATURE [PartDesign::Pocket] Pocket005
  BaseFeature = -> Chamfer001
  Direction = (-1,0,0)
  Length = 5
  Length2 = 5
  Placement = pos=(0,0,0) rot=(1,1,1;2.0944rad)
  Profile = -> Sketch013
  ReferenceAxis = -> Sketch013 [N_Axis]
  Reversed = true
  Suppressed = false
  Type = 0
FEATURE [Part::Box] Box006  label="TFT-PCB"
  AttacherType = Attacher::AttachEngine3D
  Height = 53
  Length = 1.6
  Placement = pos=(4,1,-7) rot=(0,0,1;0rad)
  Width = 81
FEATURE [PartDesign::Pad] Pad006
  BaseFeature = -> Pocket005
  Direction = (1,0,1e-15)
  Length = 0.001
  Length2 = 10
  Placement = pos=(0,0,0) rot=(1,1,1;2.0944rad)
  Profile = -> Pocket005 [Face89]
  Suppressed = false
  Type = 0
FEATURE [PartDesign::Pad] Pad007
  BaseFeature = -> Pad006
  Direction = (4e-16,1,-2e-16)
  Length = 0.001
  Length2 = 10
  Placement = pos=(0,0,0) rot=(1,1,1;2.0944rad)
  Profile = -> Pad006 [Face88]
  Suppressed = false
  Type = 0
FEATURE [Sketcher::SketchObject] Sketch014
  ArcFitTolerance = 0
  AttachmentSupport = -> [YZ_Plane069]
  FullyConstrained = true
  MakeInternals = false
  MapMode = 5
  Placement = pos=(0,0,0) rot=(0.57735,0.57735,0.57735;2.0944rad)
  sketch-geometry (8):
    g0: LineSegment StartX=84 StartY=-5 StartZ=0 EndX=97 EndY=-5 EndZ=0
    g1: LineSegment StartX=97 StartY=-5 StartZ=0 EndX=97 EndY=-7.5 EndZ=0
    g2: LineSegment StartX=97 StartY=-7.5 StartZ=0 EndX=84 EndY=-7.5 EndZ=0
    g3: LineSegment StartX=84 StartY=-7.5 StartZ=0 EndX=84 EndY=-5 EndZ=0
    g4: LineSegment StartX=177 StartY=-5 StartZ=0 EndX=169 EndY=-5 EndZ=0
    g5: LineSegment StartX=169 StartY=-5 StartZ=0 EndX=169 EndY=-7.5 EndZ=0
    g6: LineSegment StartX=169 StartY=-7.5 StartZ=0 EndX=177 EndY=-7.5 EndZ=0
    g7: LineSegment StartX=177 StartY=-7.5 StartZ=0 EndX=177 EndY=-5 EndZ=0
  constraints (24):
    c: Coincident(g0,g1)
    c: Coincident(g1,g2)
    c: Coincident(g2,g3)
    c: Coincident(g3,g0)
    c: Horizontal(g0)
    c: Horizontal(g2)
    c: Vertical(g1)
    c: Vertical(g3)
    c: DistanceY(g3,g3) = 2.5
    c: DistanceX(g2,g2) = 13
    c: Coincident(g4,g5)
    c: Coincident(g5,g6)
    c: Coincident(g6,g7)
    c: Coincident(g7,g4)
    c: Horizontal(g4)
    c: Horizontal(g6)
    c: Vertical(g5)
    c: Vertical(g7)
    c: Horizontal(g0,g4)
    c: Equal(g5,g1)
    c: DistanceX(g4) = 177
    c: DistanceY(g4) = -5
    c: DistanceX(g-1,g0) = 84
    c: DistanceX(g6,g6) = 8
FEATURE [PartDesign::Pad] Pad008
  BaseFeature = -> Pad007
  Direction = (1,0,0)
  Length = 17
  Length2 = 10
  Placement = pos=(0,0,0) rot=(1,1,1;2.0944rad)
  Profile = -> Sketch014
  ReferenceAxis = -> Sketch014 [N_Axis]
  Suppressed = false
  Type = 0
FEATURE [Sketcher::SketchObject] Sketch015
  ArcFitTolerance = 0
  AttachmentSupport = -> [XY_Plane069]
  FullyConstrained = true
  MakeInternals = false
  MapMode = 5
  sketch-geometry (2):
    g0: Circle CenterX=11.8 CenterY=173.5 CenterZ=0 NormalX=0 NormalY=0 NormalZ=1 AngleXU=0 Radius=1.6
    g1: Circle CenterX=11.8 CenterY=89.5 CenterZ=0 NormalX=0 NormalY=0 NormalZ=1 AngleXU=0 Radius=1.6
  constraints (6):
    c: Diameter(g0) = 3.2
    c: DistanceX(g0) = 11.8
    c: DistanceY(g0) = 173.5
    c: Equal(g0,g1)
    c: Vertical(g1,g0)
    c: DistanceY(g1,g0) = 84
FEATURE [PartDesign::Pocket] Pocket006
  BaseFeature = -> Pad008
  Direction = (0,0,-1)
  Length = 32
  Length2 = 5
  Midplane = true
  Placement = pos=(0,0,0) rot=(1,1,1;2.0944rad)
  Profile = -> Sketch015
  ReferenceAxis = -> Sketch015 [N_Axis]
  Suppressed = false
  Type = 0
FEATURE [Sketcher::SketchObject] Sketch016
  ArcFitTolerance = 0
  AttachmentSupport = -> [YZ_Plane069]
  FullyConstrained = true
  MakeInternals = false
  MapMode = 5
  Placement = pos=(0,0,0) rot=(0.57735,0.57735,0.57735;2.0944rad)
  sketch-geometry (4):
    g0: LineSegment StartX=169.017 StartY=10 StartZ=0 EndX=169.017 EndY=-11 EndZ=0
    g1: LineSegment StartX=169.017 StartY=-11 StartZ=0 EndX=175.017 EndY=-11 EndZ=0
    g2: LineSegment StartX=175.017 StartY=-11 StartZ=0 EndX=175.017 EndY=10 EndZ=0
    g3: ArcOfCircle CenterX=172.017 CenterY=10 CenterZ=0 NormalX=0 NormalY=0 NormalZ=1 AngleXU=0 Radius=3 StartAngle=3.14159 EndAngle=6.28319
  constraints (13):
    c: Coincident(g0,g1)
    c: Coincident(g1,g2)
    c: Horizontal(g1)
    c: Vertical(g0)
    c: Vertical(g2)
    c: DistanceX(g0,g2) = 6
    c: DistanceX(g0) = 169.017
    c: DistanceY(g1,g-1) = 11
    c: Coincident(g3,g0)
    c: Coincident(g3,g2)
    c: Horizontal(g2,g3)
    c: Equal(g2,g0)
    c: DistanceY(g2,g2) = 21
FEATURE [PartDesign::Pad] Pad009
  BaseFeature = -> Pocket006
  Direction = (1,0,0)
  Length = 10
  Length2 = 10
  Placement = pos=(0,0,0) rot=(1,1,1;2.0944rad)
  Profile = -> Sketch016
  ReferenceAxis = -> Sketch016 [N_Axis]
  Reversed = true
  Suppressed = false
  Type = 3
  UpToFace = -> Pocket006 [Face1]
FEATURE [Sketcher::SketchObject] Sketch017
  ArcFitTolerance = 0
  AttachmentSupport = -> [YZ_Plane069]
  ExternalGeometry = -> [Pad009]
  FullyConstrained = true
  MakeInternals = false
  MapMode = 5
  Placement = pos=(0,0,0) rot=(0.57735,0.57735,0.57735;2.0944rad)
  sketch-geometry (7):
    g0: ArcOfCircle CenterX=133 CenterY=-7.55 CenterZ=0 NormalX=0 NormalY=0 NormalZ=1 AngleXU=0 Radius=2.5 StartAngle=4.71239 EndAngle=7.85398
    g1: ArcOfCircle CenterX=100 CenterY=-7.55 CenterZ=0 NormalX=0 NormalY=0 NormalZ=1 AngleXU=0 Radius=2.5 StartAngle=1.5708 EndAngle=4.71239
    g2: LineSegment StartX=133 StartY=-5.05 StartZ=0 EndX=100 EndY=-5.05 EndZ=0
    g3: LineSegment StartX=100 StartY=-10.05 StartZ=0 EndX=133 EndY=-10.05 EndZ=0
    g4: Circle CenterX=173.502 CenterY=3.91 CenterZ=0 NormalX=0 NormalY=0 NormalZ=1 AngleXU=0 Radius=1.625
    g5: Circle CenterX=89.5018 CenterY=3.91 CenterZ=0 NormalX=0 NormalY=0 NormalZ=1 AngleXU=0 Radius=1.625
    g6: LineSegment [constr] StartX=133 StartY=-10.05 StartZ=0 EndX=142 EndY=-10.05 EndZ=0
  constraints (18):
    c: Tangent(g0,g2) = -1.5708
    c: Tangent(g2,g1) = -1.5708
    c: Tangent(g1,g3) = -1.5708
    c: Tangent(g3,g0) = -1.5708
    c: Equal(g0,g1)
    c: Horizontal(g2)
    c: Diameter(g0) = 5
    c: DistanceX(g3,g3) = 33
    c: DistanceX(g-1,g1) = 100
    c: Equal(g5,g4)
    c: Horizontal(g4,g5)
    c: DistanceX(g5,g4) = 84
    c: Diameter(g5) = 3.25
    c: DistanceX(g5) = 89.5018
    c: DistanceY(g5) = 3.91
    c: Coincident(g6,g0)
    c: Horizontal(g6)
    c: Tangent(g6,g-3) = -1.5708
FEATURE [PartDesign::Pocket] Pocket007
  BaseFeature = -> Pad009
  Direction = (-1,0,0)
  Length = 5
  Length2 = 5
  Placement = pos=(0,0,0) rot=(1,1,1;2.0944rad)
  Profile = -> Sketch017
  ReferenceAxis = -> Sketch017 [N_Axis]
  Suppressed = false
  Type = 0
FEATURE [Part::Feature] Chamfer002  label="PMB-1"
  Placement = pos=(-0.5,173.5,-0.1) rot=(-1,0,0;1.5708rad)
  shape: bbox 16 x 6 x 13 mm, 15 faces (baked)
FEATURE [Part::Feature] Chamfer003  label="PMB-002"
  Placement = pos=(-0.5,89.5,-0.1) rot=(-1,0,0;1.5708rad)
  shape: bbox 16 x 6 x 13 mm, 15 faces (baked)
FEATURE [Sketcher::SketchObject] Sketch018
  ArcFitTolerance = 0
  AttachmentSupport = -> [YZ_Plane069]
  FullyConstrained = true
  MakeInternals = false
  MapMode = 5
  Placement = pos=(0,0,0) rot=(0.57735,0.57735,0.57735;2.0944rad)
  sketch-geometry (1):
    g0: Circle CenterX=111.65 CenterY=34.9425 CenterZ=0 NormalX=0 NormalY=0 NormalZ=1 AngleXU=0 Radius=3
  constraints (3):
    c: DistanceX(g0) = 111.65
    c: DistanceY(g0) = 34.9425
    c: Diameter(g0) = 6
FEATURE [PartDesign::Pad] Pad010
  BaseFeature = -> Pocket007
  Direction = (1,0,0)
  Length = 1
  Length2 = 10
  Placement = pos=(0,0,0) rot=(1,1,1;2.0944rad)
  Profile = -> Sketch018
  ReferenceAxis = -> Sketch018 [N_Axis]
  Suppressed = false
  Type = 0
FEATURE [App::Link] C5_C_0805_2012Metric_c37d78c0e7e__ln_006  label="C2_C_0805_2012Metric_3a90d12aea5"001"
  LinkPlacement = pos=(211.2,-83.3425,-1.6) rot=(0.707107,-0.707107,0;3.14159rad)
  LinkedObject = -> Shape215
  Placement = pos=(211.2,-83.3425,-1.6) rot=(0.707107,-0.707107,0;3.14159rad)
FEATURE [App::Link] C5_C_0805_2012Metric_c37d78c0e7e__ln_007  label="C1_C_0805_2012Metric_f214d5325a3"001"
  LinkPlacement = pos=(167.5,-98.8,-1.6) rot=(0.707107,-0.707107,0;3.14159rad)
  LinkedObject = -> Shape215
  Placement = pos=(167.5,-98.8,-1.6) rot=(0.707107,-0.707107,0;3.14159rad)
FEATURE [App::Link] C5_C_0805_2012Metric_c37d78c0e7e__ln_008  label="C4_C_0805_2012Metric_1f9bc760d65"001"
  LinkPlacement = pos=(145.65,-80,-1.6) rot=(0.707107,0.707107,0;3.14159rad)
  LinkedObject = -> Shape215
  Placement = pos=(145.65,-80,-1.6) rot=(0.707107,0.707107,0;3.14159rad)
FEATURE [App::Link] C5_C_0805_2012Metric_c37d78c0e7e__ln_009  label="C3_C_0805_2012Metric_9e6fa2387b6"001"
  LinkPlacement = pos=(163,-82.7,-1.6) rot=(0,1,0;3.14159rad)
  LinkedObject = -> Shape215
  Placement = pos=(163,-82.7,-1.6) rot=(0,1,0;3.14159rad)
FEATURE [App::Link] C5_C_0805_2012Metric_c37d78c0e7e__ln_010  label="C7_C_0805_2012Metric_fd35ebc905f"001"
  LinkPlacement = pos=(145.85,-67.3,-1.6) rot=(0.707107,0.707107,0;3.14159rad)
  LinkedObject = -> Shape215
  Placement = pos=(145.85,-67.3,-1.6) rot=(0.707107,0.707107,0;3.14159rad)
FEATURE [App::Link] C5_C_0805_2012Metric_c37d78c0e7e__ln_011  label="C9_C_0805_2012Metric_53a94e2bf13"001"
  LinkPlacement = pos=(192.4,-71.4,-1.6) rot=(0.707107,0.707107,0;3.14159rad)
  LinkedObject = -> Shape215
  Placement = pos=(192.4,-71.4,-1.6) rot=(0.707107,0.707107,0;3.14159rad)
FEATURE [App::Link] C5_C_0805_2012Metric_c37d78c0e7e__ln_012  label="C10_C_0805_2012Metric_7853a08ffed""
  LinkPlacement = pos=(137.7,-82.7,-1.6) rot=(0,1,0;3.14159rad)
  LinkedObject = -> Shape215
  Placement = pos=(137.7,-82.7,-1.6) rot=(0,1,0;3.14159rad)
FEATURE [App::Link] C8_CP_Elec_5x58_62bf51b026a__ln_001  label="C6_CP_Elec_5x58_6693afb63cc"001"
  LinkPlacement = pos=(188,-70.8,-1.6) rot=(0.707107,0.707107,0;3.14159rad)
  LinkedObject = -> Shape213
  Placement = pos=(188,-70.8,-1.6) rot=(0.707107,0.707107,0;3.14159rad)
FEATURE [PartDesign::CoordinateSystem] Local_CS_85fa007
  AttacherType = Attacher::AttachEngine3D
  AttachmentSupport = -> [X_Axis116]
  MapMode = 2
FEATURE [Sketcher::SketchObject] PCB_Sketch_85fa007
  ArcFitTolerance = 0
  FullyConstrained = false
  MakeInternals = false
  sketch-geometry (20):
    g0: LineSegment StartX=184.1 StartY=-99.2 StartZ=0 EndX=226.1 EndY=-99.2 EndZ=0
    g1: LineSegment StartX=245.1 StartY=-114.2 StartZ=0 EndX=230.1 EndY=-114.2 EndZ=0
    g2: LineSegment StartX=122.1 StartY=-65.2 StartZ=0 EndX=122.101 EndY=-88.7 EndZ=0
    g3: LineSegment StartX=126.1 StartY=-61.2 StartZ=0 EndX=245.1 EndY=-61.2 EndZ=0
    g4: LineSegment StartX=170.1 StartY=-114.2 StartZ=0 EndX=180.1 EndY=-114.2 EndZ=0
    g5: LineSegment StartX=182.1 StartY=-112.2 StartZ=0 EndX=182.1 EndY=-101.2 EndZ=0
    g6: LineSegment StartX=126.1 StartY=-92.6986 StartZ=0 EndX=162.101 EndY=-92.7014 EndZ=0
    g7: LineSegment StartX=166.1 StartY=-110.2 StartZ=0 EndX=166.1 EndY=-96.7 EndZ=0
    g8: LineSegment StartX=228.1 StartY=-112.2 StartZ=0 EndX=228.1 EndY=-101.2 EndZ=0
    g9: LineSegment StartX=249.1 StartY=-65.2 StartZ=0 EndX=249.1 EndY=-110.2 EndZ=0
    g10: ArcOfCircle CenterX=245.1 CenterY=-65.2 CenterZ=0 NormalX=0 NormalY=0 NormalZ=-1 AngleXU=1.5708 Radius=4 StartAngle=0 EndAngle=1.5708
    g11: ArcOfCircle CenterX=226.1 CenterY=-101.2 CenterZ=0 NormalX=0 NormalY=0 NormalZ=-1 AngleXU=1.5708 Radius=2 StartAngle=0 EndAngle=1.5708
    g12: ArcOfCircle CenterX=180.1 CenterY=-112.2 CenterZ=0 NormalX=0 NormalY=0 NormalZ=-1 AngleXU=3.14159 Radius=2 StartAngle=0 EndAngle=1.5708
    g13: ArcOfCircle CenterX=170.1 CenterY=-110.2 CenterZ=0 NormalX=0 NormalY=0 NormalZ=-1 AngleXU=-1.5708 Radius=4 StartAngle=0 EndAngle=1.5708
    g14: ArcOfCircle CenterX=162.101 CenterY=-96.7 CenterZ=0 NormalX=0 NormalY=0 NormalZ=-1 AngleXU=1.57079 Radius=3.99859 StartAngle=0 EndAngle=1.57081
    g15: ArcOfCircle CenterX=184.1 CenterY=-101.2 CenterZ=0 NormalX=0 NormalY=0 NormalZ=-1 AngleXU=-7.47076e-07 Radius=2 StartAngle=0 EndAngle=1.5708
    g16: ArcOfCircle CenterX=230.1 CenterY=-112.2 CenterZ=0 NormalX=0 NormalY=0 NormalZ=-1 AngleXU=-1.5708 Radius=2 StartAngle=0 EndAngle=1.5708
    g17: ArcOfCircle CenterX=126.1 CenterY=-65.2 CenterZ=0 NormalX=0 NormalY=0 NormalZ=-1 AngleXU=1.06478e-07 Radius=4 StartAngle=0 EndAngle=1.5708
    g18: ArcOfCircle CenterX=126.1 CenterY=-88.7 CenterZ=0 NormalX=0 NormalY=0 NormalZ=-1 AngleXU=-1.5708 Radius=3.99862 StartAngle=0 EndAngle=1.5708
    g19: ArcOfCircle CenterX=245.1 CenterY=-110.2 CenterZ=0 NormalX=0 NormalY=0 NormalZ=-1 AngleXU=-3.14159 Radius=4 StartAngle=0 EndAngle=1.5708
  constraints (20):
    c: Coincident(g2,g18)
    c: Coincident(g2,g17)
    c: Coincident(g6,g18)
    c: Coincident(g3,g17)
    c: Coincident(g6,g14)
    c: Coincident(g7,g13)
    c: Coincident(g7,g14)
    c: Coincident(g4,g13)
    c: Coincident(g4,g12)
    c: Coincident(g5,g12)
    c: Coincident(g5,g15)
    c: Coincident(g0,g15)
    c: Coincident(g0,g11)
    c: Coincident(g8,g16)
    c: Coincident(g8,g11)
    c: Coincident(g1,g16)
    c: Coincident(g1,g19)
    c: Coincident(g3,g10)
    c: Coincident(g9,g19)
    c: Coincident(g9,g10)
FEATURE [Part::Feature] Part__Feature541  label="EC11_Rotary_Encoder_Switched070"
  shape: bbox 1.5 x 1.93 x 7.07 mm, 34 faces (baked)
FEATURE [Part::Feature] Part__Feature542  label="EC11_Rotary_Encoder_Switched071"
  shape: bbox 1.5 x 1.93 x 7.07 mm, 34 faces (baked)
FEATURE [Part::Feature] Part__Feature543  label="EC11_Rotary_Encoder_Switched072"
  shape: bbox 1.5 x 1.93 x 7.07 mm, 34 faces (baked)
FEATURE [Part::Feature] Part__Feature544  label="EC11_Rotary_Encoder_Switched073"
  shape: bbox 1.5 x 1.93 x 7.07 mm, 34 faces (baked)
FEATURE [Part::Feature] Part__Feature545  label="EC11_Rotary_Encoder_Switched074"
  shape: bbox 1.5 x 1.93 x 7.07 mm, 34 faces (baked)
FEATURE [Part::Feature] Part__Feature546  label="EC11_Rotary_Encoder_Switched075"
  shape: bbox 13.1 x 12 x 9.87 mm, 116 faces (baked)
FEATURE [Part::Feature] Part__Feature547  label="EC11_Rotary_Encoder_Switched076"
  shape: bbox 11.8 x 12 x 1.6 mm, 18 faces (baked)
FEATURE [Part::Feature] Part__Feature548  label="EC11_Rotary_Encoder_Switched077"
  shape: bbox 11.8 x 12 x 3.4 mm, 82 faces (baked)
FEATURE [Part::Feature] Part__Feature549  label="EC11_Rotary_Encoder_Switched078"
  shape: bbox 11.8 x 12.5 x 8.743 mm, 73 faces (baked)
FEATURE [Part::Feature] Part__Feature550  label="EC11_Rotary_Encoder_Switched079"
  shape: bbox 5.658 x 5.782 x 13.3 mm, 102 faces (baked)
FEATURE [App::Part] EC11_Rotary_Encoder_Switched007  label="ENC1_EC11_Rotary_Encoder_Switched010_ff9b8aaf94f"[2]001"
  Group = -> [Part__Feature541,Part__Feature542,Part__Feature543,Part__Feature544,Part__Feature545,Part__Feature546,Part__Feature547,Part__Feature548,Part__Feature549,Part__Feature550]
  Origin = -> Origin120
  Placement = pos=(153.4,-73,0) rot=(0,0,-1;1.5708rad)
FEATURE [Part::Feature] Pcb_85fa007
  shape: bbox 127 x 53 x 1.6 mm, 86 faces (baked)
FEATURE [App::Part] Board_Geoms_85fa007  label="Board_Geoms_85fa012"
  Group = -> [Pcb_85fa007,PCB_Sketch_85fa007]
  Origin = -> Origin115
FEATURE [App::Link] R13_R_0805_2012Metric_b6da7abc100__ln_011  label="R12_R_0805_2012Metric_a710e860d27"001"
  LinkPlacement = pos=(149.1,-72.9875,-1.6) rot=(0.707107,0.707107,0;3.14159rad)
  LinkedObject = -> Shape214
  Placement = pos=(149.1,-72.9875,-1.6) rot=(0.707107,0.707107,0;3.14159rad)
FEATURE [App::Link] R13_R_0805_2012Metric_b6da7abc100__ln_012  label="R6_R_0805_2012Metric_4955dbcc53a"001"
  LinkPlacement = pos=(149.1,-79.9875,-1.6) rot=(0.707107,0.707107,0;3.14159rad)
  LinkedObject = -> Shape214
  Placement = pos=(149.1,-79.9875,-1.6) rot=(0.707107,0.707107,0;3.14159rad)
FEATURE [App::Link] R13_R_0805_2012Metric_b6da7abc100__ln_013  label="R5_R_0805_2012Metric_8355fbe83b5"001"
  LinkPlacement = pos=(161.35,-80.2,-1.6) rot=(0,1,0;3.14159rad)
  LinkedObject = -> Shape214
  Placement = pos=(161.35,-80.2,-1.6) rot=(0,1,0;3.14159rad)
FEATURE [App::Link] R13_R_0805_2012Metric_b6da7abc100__ln_014  label="R10_R_0805_2012Metric_85e806fa757"001"
  LinkPlacement = pos=(136.9,-69.3125,-1.6) rot=(0.707107,-0.707107,0;3.14159rad)
  LinkedObject = -> Shape214
  Placement = pos=(136.9,-69.3125,-1.6) rot=(0.707107,-0.707107,0;3.14159rad)
FEATURE [App::Link] R13_R_0805_2012Metric_b6da7abc100__ln_015  label="R2_R_0805_2012Metric_72552903f90"001"
  LinkPlacement = pos=(235.088,-82.0425,-1.6) rot=(0,1,0;3.14159rad)
  LinkedObject = -> Shape214
  Placement = pos=(235.088,-82.0425,-1.6) rot=(0,1,0;3.14159rad)
FEATURE [App::Link] R13_R_0805_2012Metric_b6da7abc100__ln_016  label="R18_R_0805_2012Metric_5f6bbecb288"001"
  LinkPlacement = pos=(129.9,-72.7,-1.6) rot=(0,1,0;3.14159rad)
  LinkedObject = -> Shape214
  Placement = pos=(129.9,-72.7,-1.6) rot=(0,1,0;3.14159rad)
FEATURE [App::Link] R13_R_0805_2012Metric_b6da7abc100__ln_017  label="R7_R_0805_2012Metric_91f852aec81"001"
  LinkPlacement = pos=(136.9,-72.9,-1.6) rot=(0.707107,0.707107,0;3.14159rad)
  LinkedObject = -> Shape214
  Placement = pos=(136.9,-72.9,-1.6) rot=(0.707107,0.707107,0;3.14159rad)
FEATURE [App::Link] R13_R_0805_2012Metric_b6da7abc100__ln_018  label="R4_R_0805_2012Metric_ccac18c3cb5"001"
  LinkPlacement = pos=(161.35,-78.1,-1.6) rot=(0,1,0;3.14159rad)
  LinkedObject = -> Shape214
  Placement = pos=(161.35,-78.1,-1.6) rot=(0,1,0;3.14159rad)
FEATURE [App::Link] R13_R_0805_2012Metric_b6da7abc100__ln_019  label="R8_R_0805_2012Metric_9269aa7d845"001"
  LinkPlacement = pos=(149.1,-76.4875,-1.6) rot=(0.707107,-0.707107,0;3.14159rad)
  LinkedObject = -> Shape214
  Placement = pos=(149.1,-76.4875,-1.6) rot=(0.707107,-0.707107,0;3.14159rad)
FEATURE [App::Link] R13_R_0805_2012Metric_b6da7abc100__ln_020  label="R3_R_0805_2012Metric_573904aba2f"001"
  LinkPlacement = pos=(235.287,-92.9425,-1.6) rot=(0,1,0;3.14159rad)
  LinkedObject = -> Shape214
  Placement = pos=(235.287,-92.9425,-1.6) rot=(0,1,0;3.14159rad)
FEATURE [App::Link] R13_R_0805_2012Metric_b6da7abc100__ln_021  label="R1_R_0805_2012Metric_6e6cdb9ead7"001"
  LinkPlacement = pos=(235.088,-79.3425,-1.6) rot=(0,1,0;3.14159rad)
  LinkedObject = -> Shape214
  Placement = pos=(235.088,-79.3425,-1.6) rot=(0,1,0;3.14159rad)
FEATURE [Part::Feature] Shape209  label="D1_LED_D3.0mm_0fd27398e71"001"
  Placement = pos=(123.725,-72.7,0) rot=(0,0,1;0rad)
  shape: bbox 3.4 x 3.8 x 10.8 mm, 16 faces (baked)
FEATURE [Part::Feature] Shape210  label="J3_MCV_01x04_G_3_81mm_2eac01a156a""
  Placement = pos=(127.29,-88.7,0) rot=(0,0,1;0rad)
  shape: bbox 16.63 x 7.55 x 12.6 mm, 142 faces (baked)
FEATURE [Part::Feature] Shape211  label="SW1_SW_PUSH_6mm_h13mm_d4ea787a014"[2]001"
  Placement = pos=(133.9,-70.75,0) rot=(0,0,1;0rad)
  shape: bbox 7.174 x 6 x 16.5 mm, 105 faces (baked)
FEATURE [Part::Feature] Shape212  label="J1_PinSocket_1x11_P254mm_Vertical_a5addac6e48"001"
  Placement = pos=(169.875,-100.375,0) rot=(0,0,1;3.14159rad)
  shape: bbox 2.54 x 27.94 x 10.1 mm, 351 faces (baked)
FEATURE [Part::Feature] Shape213  label="C8_CP_Elec_5x58_62bf51b026a"001"
  Placement = pos=(183.2,-95.5,0) rot=(0,0,1;0rad)
  shape: bbox 6.985 x 6.828 x 5.8 mm, 41 faces (baked)
FEATURE [Part::Feature] Shape214  label="R13_R_0805_2012Metric_b6da7abc100"001"
  Placement = pos=(149.1,-69.4875,-1.6) rot=(0.707107,-0.707107,0;3.14159rad)
  shape: bbox 1.2 x 2 x 0.45 mm, 26 faces (baked)
FEATURE [Part::Feature] Shape215  label="C5_C_0805_2012Metric_c37d78c0e7e"001"
  Placement = pos=(136.9,-76.4125,-1.6) rot=(0.707107,-0.707107,0;3.14159rad)
  shape: bbox 1.25 x 2 x 1.25 mm, 28 faces (baked)
FEATURE [Part::Feature] Shape216  label="U2_SOT_23_6_5c380d68c4f""
  Placement = pos=(133.9,-81.5,-1.6) rot=(0.707107,0.707107,0;3.14159rad)
  shape: bbox 2.9 x 2.8 x 1.55 mm, 124 faces (baked)
FEATURE [Part::Feature] Shape217  label="J2_IDC_Header_2x08_P254mm_Vertical_d590179e4ec"001"
  Placement = pos=(199.28,-69.8,-1.6) rot=(0.707107,-0.707107,0;3.14159rad)
  shape: bbox 27.98 x 9.1 x 12.1 mm, 330 faces (baked)
FEATURE [Part::Feature] Shape218  label="U1_SOIC_18W_75x116mm_P127mm_6d87b56a7a8"001"
  Placement = pos=(218.4,-87.4425,-1.6) rot=(0,1,0;3.14159rad)
  shape: bbox 10.3 x 11.55 x 2.75 mm, 306 faces (baked)
FEATURE [App::Part] Bot_85fa007  label="Bot_85fa012"
  Group = -> [C8_CP_Elec_5x58_62bf51b026a__ln_001,Shape214,Shape215,R13_R_0805_2012Metric_b6da7abc100__ln_011,R13_R_0805_2012Metric_b6da7abc100__ln_012,R13_R_0805_2012Metric_b6da7abc100__ln_013,R13_R_0805_2012Metric_b6da7abc100__ln_014,R13_R_0805_2012Metric_b6da7abc100__ln_015,R13_R_0805_2012Metric_b6da7abc100__ln_016,Shape216,C5_C_0805_2012Metric_c37d78c0e7e__ln_006,R13_R_0805_2012Metric_b6da7abc100__ln_017,+12 more]
  Origin = -> Origin119
FEATURE [App::Part] Top_85fa007  label="Top_85fa012"
  Group = -> [Shape209,Shape210,Shape211,Shape212,Shape213,EC11_Rotary_Encoder_Switched007]
  Origin = -> Origin118
FEATURE [App::Part] Step_Models_85fa007  label="Step_Models_85fa012"
  Group = -> [Top_85fa007,Bot_85fa007]
  Origin = -> Origin117
FEATURE [App::Part] Board_85fa007  label="EL-Load-Panel007"
  Group = -> [Local_CS_85fa007,Board_Geoms_85fa007,Step_Models_85fa007]
  Origin = -> Origin116
  Placement = pos=(16,249,107) rot=(-1,1,1;4.18879rad)
FEATURE [Sketcher::SketchObject] Sketch019
  ArcFitTolerance = 0
  AttachmentSupport = -> [YZ_Plane069]
  FullyConstrained = true
  MakeInternals = false
  MapMode = 5
  Placement = pos=(0,0,0) rot=(0.57735,0.57735,0.57735;2.0944rad)
  sketch-geometry (5):
    g0: LineSegment StartX=106 StartY=14.3 StartZ=0 EndX=106 EndY=24.3 EndZ=0
    g1: LineSegment StartX=106 StartY=24.3 StartZ=0 EndX=126 EndY=24.3 EndZ=0
    g2: LineSegment StartX=126 StartY=24.3 StartZ=0 EndX=126 EndY=14.3 EndZ=0
    g3: LineSegment StartX=126 StartY=14.3 StartZ=0 EndX=106 EndY=14.3 EndZ=0
    g4: GeomPoint [constr] X=116 Y=19.3 Z=0
  constraints (13):
    c: Coincident(g0,g1)
    c: Coincident(g1,g2)
    c: Coincident(g2,g3)
    c: Coincident(g3,g0)
    c: Horizontal(g1)
    c: Horizontal(g3)
    c: Vertical(g0)
    c: Vertical(g2)
    c: Symmetric(g1,g0,g4)
    c: DistanceX(g1,g1) = 20
    c: DistanceY(g0,g0) = 10
    c: DistanceX(g4) = 116
    c: DistanceY(g4) = 19.3
FEATURE [PartDesign::Pocket] Pocket008
  BaseFeature = -> Pad010
  Direction = (-1,0,0)
  Length = 5
  Length2 = 5
  Midplane = true
  Placement = pos=(0,0,0) rot=(1,1,1;2.0944rad)
  Profile = -> Sketch019
  ReferenceAxis = -> Sketch019 [N_Axis]
  Suppressed = false
  Type = 1
FEATURE [Part::Feature] Part__Feature551  label="2023_07_19_08_52_51_0117"
  shape: bbox 1.2 x 4.95 x 1.2 mm, 6 faces (baked)
FEATURE [Part::Feature] Part__Feature552  label="2023_07_19_08_52_51_0101"
  shape: bbox 2.85 x 3.75 x 1.7 mm, 15 faces (baked)
FEATURE [Part::Feature] Part__Feature553  label="2023_07_19_08_52_51_0085"
  shape: bbox 1.2 x 4.95 x 1.2 mm, 6 faces (baked)
FEATURE [Part::Feature] Part__Feature554  label="2023_07_19_08_52_51_0070"
  shape: bbox 2.85 x 3.75 x 1.7 mm, 15 faces (baked)
FEATURE [Part::Feature] Part__Feature555  label="2023_07_19_08_52_51_0054"
  shape: bbox 1.2 x 4.95 x 1.2 mm, 6 faces (baked)
FEATURE [Part::Feature] Part__Feature556  label="2023_07_19_08_52_51_0039"
  shape: bbox 2.85 x 3.75 x 1.7 mm, 15 faces (baked)
FEATURE [Part::Feature] Part__Feature557  label="2023_07_19_08_52_51_0023"
  shape: bbox 1.2 x 4.95 x 1.2 mm, 6 faces (baked)
FEATURE [Part::Feature] Part__Feature558  label="2023_07_19_08_52_51_0007"
  shape: bbox 2.85 x 3.75 x 1.7 mm, 15 faces (baked)
FEATURE [Part::Feature] Part__Feature559  label="2023_07_19_08_52_50_0945"
  shape: bbox 15.72 x 21.9 x 7.811 mm, 985 faces (baked)
FEATURE [App::Part] _023_07_19_08_52_50_0648  label="2023_07_19_08_52_50_0648"
  Group = -> [Part__Feature551,Part__Feature552,Part__Feature553,Part__Feature554,Part__Feature555,Part__Feature556,Part__Feature557,Part__Feature558,Part__Feature559]
  Origin = -> Origin121
  Placement = pos=(-7.4,123.8,15.5) rot=(0,0,1;4.71239rad)
FEATURE [Part::Feature] Part__Feature560  label="1455U Open Bezel002"
  Placement = pos=(1,89.49,20.2) rot=(0.57735,-0.57735,-0.57735;2.0944rad)
  shape: bbox 11.6 x 196.1 x 71.1 mm, 100 faces (baked)
FEATURE [PartDesign::Pad] Pad011
  BaseFeature = -> Pocket008
  Direction = (1,0,3.7e-15)
  Length = 12.5
  Length2 = 10
  Placement = pos=(0,0,0) rot=(1,1,1;2.0944rad)
  Profile = -> Pocket008 [Face112]
  Suppressed = false
  Type = 0
FEATURE [PartDesign::Pad] Pad012
  BaseFeature = -> Pad011
  Direction = (1,0,4e-15)
  Length = 12.5
  Length2 = 10
  Placement = pos=(0,0,0) rot=(1,1,1;2.0944rad)
  Profile = -> Pad011 [Face77]
  Suppressed = false
  Type = 0
FEATURE [PartDesign::Body] Body002  label="Front Panel"
  AllowCompound = false
  Group = -> [Binder001,Sketch006,Sketch007,Sketch009,Sketch010,Pad004,Chamfer,Pocket003,Sketch011,Sketch012,Pad005,Pocket004,Chamfer001,Sketch013,Pocket005,Pad006,Pad007,Sketch014,Pad008,Sketch015,Pocket006,Sketch016,Pad009,Sketch017,Pocket007,Sketch018,Pad010,Sketch019,Pocket008,Pad011,Pad012]
  Origin = -> Origin069
  Placement = pos=(-0.6,0,0) rot=(0,0,1;0rad)
  Tip = -> Pad012
FEATURE [Part::Feature] Part__Feature561  label="U End Panel003"
  Placement = pos=(222.8,89.4,20) rot=(0.57735,0.57735,0.57735;2.0944rad)
  shape: bbox 1.626 x 191 x 66 mm, 14 faces (baked)
FEATURE [PartDesign::SubShapeBinder] Binder002
  BindCopyOnChange = 0
  BindMode = 0
  ClaimChildren = false
  Context = -> Body004 [Binder002.]
  Fuse = false
  MakeFace = true
  OffsetFill = false
  OffsetIntersection = false
  OffsetJoinType = 0
  OffsetOpenResult = false
  PartialLoad = false
  Relative = true
  Support = -> [Part__Feature561[Face11]]
  _Version = 2
FEATURE [Sketcher::SketchObject] Sketch025
  ArcFitTolerance = 1e-06
  AttachmentOffset = pos=(0,2,0) rot=(0,0,1;0rad)
  AttachmentSupport = -> [XZ_Plane123]
  FullyConstrained = true
  MakeInternals = false
  MapMode = 5
  Placement = pos=(0,4e-16,2) rot=(1,0,0;1.5708rad)
  sketch-geometry (8):
    g0: LineSegment StartX=3.55e-14 StartY=42 StartZ=0 EndX=-50 EndY=42 EndZ=0
    g1: LineSegment StartX=-50 StartY=42 StartZ=0 EndX=-50 EndY=21 EndZ=0
    g2: LineSegment StartX=-50 StartY=21 StartZ=0 EndX=3.55e-14 EndY=21 EndZ=0
    g3: LineSegment StartX=3.55e-14 StartY=21 StartZ=0 EndX=3.55e-14 EndY=42 EndZ=0
    g4: Circle CenterX=-13 CenterY=39.5 CenterZ=0 NormalX=0 NormalY=0 NormalZ=1 AngleXU=0 Radius=1.4
    g5: Circle CenterX=-44 CenterY=23.5 CenterZ=0 NormalX=0 NormalY=0 NormalZ=1 AngleXU=0 Radius=1.4
    g6: LineSegment [constr] StartX=-44 StartY=23.5 StartZ=0 EndX=-44 EndY=21 EndZ=0
    g7: LineSegment [constr] StartX=-13 StartY=39.5 StartZ=0 EndX=-13 EndY=42 EndZ=0
  constraints (24):
    c: Coincident(g0,g1)
    c: Coincident(g1,g2)
    c: Coincident(g2,g3)
    c: Coincident(g3,g0)
    c: Horizontal(g0)
    c: Horizontal(g2)
    c: Vertical(g1)
    c: Vertical(g3)
    c: PointOnObject(g0,g-2)
    c: DistanceX(g0,g0) = 50
    c: DistanceY(g1,g1) = 21
    c: DistanceY(g2) = 21
    c: DistanceY(g5,g4) = 16
    c: DistanceX(g5,g4) = 31
    c: Equal(g5,g4)
    c: Diameter(g5) = 2.8
    c: Coincident(g6,g5)
    c: PointOnObject(g6,g2)
    c: Vertical(g6)
    c: Coincident(g7,g4)
    c: PointOnObject(g7,g0)
    c: Vertical(g7)
    c: Equal(g7,g6)
    c: DistanceX(g1,g5) = 6
FEATURE [PartDesign::Pad] Pad014
  Direction = (0,-1,2e-16)
  Length = 5
  Length2 = 10
  Placement = pos=(0,0,0) rot=(1,0,0;1.5708rad)
  Profile = -> Sketch025
  ReferenceAxis = -> Sketch025 [N_Axis]
  Reversed = true
  Suppressed = false
  Type = 0
FEATURE [Sketcher::SketchObject] Sketch026
  ArcFitTolerance = 1e-06
  AttachmentSupport = -> [Pad014]
  ExternalGeometry = -> [Pad014]
  FullyConstrained = true
  MakeInternals = false
  MapMode = 5
  Placement = pos=(0,5,0) rot=(-1,0,0;1.5708rad)
  sketch-geometry (4):
    g0: Circle CenterX=-13 CenterY=-41.5 CenterZ=0 NormalX=0 NormalY=0 NormalZ=1 AngleXU=0 Radius=1.4
    g1: Circle CenterX=-13 CenterY=-41.5 CenterZ=0 NormalX=0 NormalY=0 NormalZ=1 AngleXU=0 Radius=2.5
    g2: Circle CenterX=-44 CenterY=-25.5 CenterZ=0 NormalX=0 NormalY=0 NormalZ=1 AngleXU=0 Radius=1.4
    g3: Circle CenterX=-44 CenterY=-25.5 CenterZ=0 NormalX=0 NormalY=0 NormalZ=1 AngleXU=0 Radius=2.5
  constraints (8):
    c: Coincident(g0,g-3)
    c: Coincident(g1,g0)
    c: Coincident(g2,g-4)
    c: Coincident(g3,g2)
    c: Equal(g2,g-4)
    c: Equal(g0,g-3)
    c: Tangent(g3,g-5)
    c: Tangent(g1,g-6)
FEATURE [PartDesign::Pad] Pad015
  BaseFeature = -> Pad014
  Direction = (0,1,2e-16)
  Length = 3
  Length2 = 10
  Placement = pos=(0,0,0) rot=(1,0,0;1.5708rad)
  Profile = -> Sketch026
  ReferenceAxis = -> Sketch026 [N_Axis]
  Suppressed = false
  Type = 0
FEATURE [PartDesign::Body] Body004  label="RearPanel_DCDCholder"
  AllowCompound = false
  Group = -> [Binder002,Sketch025,Pad014,Sketch026,Pad015]
  Origin = -> Origin123
  Placement = pos=(222.8,0,0) rot=(0,0,1;0rad)
  Tip = -> Pad015
FEATURE [PartDesign::FeatureBase] Clone
  BaseFeature = -> Part__Feature561
  Placement = pos=(222.8,89.4,20) rot=(0.57735,0.57735,0.57735;2.0944rad)
  Suppressed = false
FEATURE [Sketcher::SketchObject] Sketch028
  ArcFitTolerance = 1e-06
  AttachmentOffset = pos=(0,0,222.8) rot=(0,0,1;0rad)
  AttachmentSupport = -> [YZ_Plane124]
  FullyConstrained = true
  MakeInternals = false
  MapMode = 5
  Placement = pos=(222.8,0,0) rot=(0.57735,0.57735,0.57735;2.0944rad)
  sketch-geometry (15):
    g0: Circle CenterX=12 CenterY=5 CenterZ=0 NormalX=0 NormalY=0 NormalZ=1 AngleXU=0 Radius=4
    g1: Circle CenterX=132 CenterY=40 CenterZ=0 NormalX=0 NormalY=0 NormalZ=1 AngleXU=0 Radius=1.5
    g2: Circle CenterX=172 CenterY=40 CenterZ=0 NormalX=0 NormalY=0 NormalZ=1 AngleXU=0 Radius=1.5
    g3: Circle CenterX=132 CenterY=1.94831e-11 CenterZ=0 NormalX=0 NormalY=0 NormalZ=1 AngleXU=0 Radius=1.5
    g4: Circle CenterX=172 CenterY=1.94831e-11 CenterZ=0 NormalX=0 NormalY=0 NormalZ=1 AngleXU=0 Radius=1.5
    g5: LineSegment [constr] StartX=132 StartY=40 StartZ=0 EndX=132 EndY=1.94831e-11 EndZ=0
    g6: LineSegment [constr] StartX=132 StartY=1.94831e-11 StartZ=0 EndX=172 EndY=1.94831e-11 EndZ=0
    g7: LineSegment [constr] StartX=172 StartY=1.94831e-11 StartZ=0 EndX=172 EndY=40 EndZ=0
    g8: LineSegment [constr] StartX=172 StartY=40 StartZ=0 EndX=132 EndY=40 EndZ=0
    g9: GeomPoint [constr] X=152 Y=20 Z=0
    g10: Circle CenterX=152 CenterY=20 CenterZ=0 NormalX=0 NormalY=0 NormalZ=1 AngleXU=0 Radius=25
    g11: ArcOfCircle CenterX=37.5 CenterY=35 CenterZ=0 NormalX=0 NormalY=0 NormalZ=1 AngleXU=0 Radius=2 StartAngle=1.5708 EndAngle=4.71239
    g12: ArcOfCircle CenterX=45 CenterY=35 CenterZ=0 NormalX=0 NormalY=0 NormalZ=1 AngleXU=0 Radius=2 StartAngle=4.71239 EndAngle=7.85398
    g13: LineSegment StartX=37.5 StartY=37 StartZ=0 EndX=45 EndY=37 EndZ=0
    g14: LineSegment StartX=37.5 StartY=33 StartZ=0 EndX=45 EndY=33 EndZ=0
  constraints (36):
    c: DistanceX(g0) = 12
    c: DistanceY(g0) = 5
    c: Diameter(g0) = 8
    c: Coincident(g5,g6)
    c: Coincident(g6,g7)
    c: Coincident(g7,g8)
    c: Coincident(g8,g5)
    c: Vertical(g5)
    c: Vertical(g7)
    c: Horizontal(g6)
    c: Horizontal(g8)
    c: Symmetric(g7,g5,g9)
    c: Equal(g8,g5)
    c: DistanceX(g8,g8) = 40
    c: Equal(g1,g3)
    c: Equal(g3,g4)
    c: Equal(g4,g2)
    c: Coincident(g5,g1)
    c: Coincident(g5,g3)
    c: Coincident(g6,g4)
    c: Coincident(g7,g2)
    c: Diameter(g4) = 3
    c: PointOnObject(g3,g-1)
    c: Diameter(g10) = 50
    c: Coincident(g10,g9)
    c: DistanceX(g9) = 152
    c: Tangent(g11,g13) = 1.5708
    c: Tangent(g11,g14) = -1.5708
    c: Tangent(g12,g13) = 1.5708
    c: Tangent(g12,g14) = -1.5708
    c: Equal(g11,g12)
    c: Horizontal(g14)
    c: Distance(g11,g12) = 7.5
    c: Radius(g11) = 2
    c: DistanceX(g12) = 45
    c: DistanceY(g12) = 35
FEATURE [PartDesign::Pocket] Pocket011
  BaseFeature = -> Clone
  Direction = (-1,0,0)
  Length = 5
  Length2 = 5
  Placement = pos=(222.8,89.4,20) rot=(0.57735,0.57735,0.57735;2.0944rad)
  Profile = -> Sketch028
  ReferenceAxis = -> Sketch028 [N_Axis]
  Reversed = true
  Suppressed = false
  Type = 0
FEATURE [Part::Feature] Part__Feature562  label="T Extrusion Cap 220mm001"
  Placement = pos=(111,89.5,53.1) rot=(0.57735,0.57735,0.57735;2.0944rad)
  shape: bbox 220 x 152.4 x 4.29 mm, 26 faces (baked)
FEATURE [PartDesign::SubShapeBinder] Binder003
  BindCopyOnChange = 0
  BindMode = 0
  ClaimChildren = false
  Context = -> Body006 [Binder003.]
  Fuse = false
  MakeFace = true
  OffsetFill = false
  OffsetIntersection = false
  OffsetJoinType = 0
  OffsetOpenResult = false
  PartialLoad = false
  Relative = true
  Support = -> [Part__Feature562[Face26]]
  _Version = 2
FEATURE [Sketcher::SketchObject] Sketch029
  ArcFitTolerance = 1e-06
  AttachmentSupport = -> [YZ_Plane125]
  ExternalGeometry = -> [Binder003]
  FullyConstrained = true
  MakeInternals = false
  MapMode = 5
  Placement = pos=(0,0,0) rot=(0.57735,0.57735,0.57735;2.0944rad)
  sketch-geometry (8):
    g0: LineSegment StartX=164.88 StartY=48.81 StartZ=0 EndX=14.12 EndY=48.81 EndZ=0
    g1: LineSegment StartX=16.4642 StartY=53.1 StartZ=0 EndX=16.4642 EndY=50.21 EndZ=0
    g2: LineSegment StartX=16.4642 StartY=50.21 StartZ=0 EndX=14.12 EndY=50.21 EndZ=0
    g3: ArcOfCircle CenterX=14.12 CenterY=49.51 CenterZ=0 NormalX=0 NormalY=0 NormalZ=1 AngleXU=0 Radius=0.7 StartAngle=1.5708 EndAngle=4.71239
    g4: LineSegment StartX=16.4642 StartY=53.1 StartZ=0 EndX=162.536 EndY=53.1 EndZ=0
    g5: LineSegment StartX=162.536 StartY=53.1 StartZ=0 EndX=162.536 EndY=50.21 EndZ=0
    g6: LineSegment StartX=162.536 StartY=50.21 StartZ=0 EndX=164.88 EndY=50.21 EndZ=0
    g7: ArcOfCircle CenterX=164.88 CenterY=49.51 CenterZ=0 NormalX=0 NormalY=0 NormalZ=1 AngleXU=0 Radius=0.7 StartAngle=4.71239 EndAngle=7.85398
  constraints (18):
    c: Coincident(g0,g-5)
    c: Coincident(g0,g-4)
    c: Coincident(g1,g-3)
    c: Vertical(g1)
    c: Coincident(g2,g1)
    c: Tangent(g3,g0) = 1.5708
    c: Horizontal(g2)
    c: Tangent(g3,g2) = -1.5708
    c: DistanceY(g0,g2) = 1.4
    c: Coincident(g4,g1)
    c: Coincident(g4,g-3)
    c: Coincident(g5,g4)
    c: Vertical(g5)
    c: Coincident(g6,g5)
    c: Horizontal(g6)
    c: Tangent(g6,g7) = 1.5708
    c: Tangent(g0,g7) = 1.5708
    c: Equal(g7,g3)
FEATURE [PartDesign::Pad] Pad016
  Direction = (1,0,0)
  Length = 220
  Length2 = 10
  Placement = pos=(0,0,0) rot=(1,1,1;2.0944rad)
  Profile = -> Sketch029
  ReferenceAxis = -> Sketch029 [N_Axis]
  Suppressed = false
  Type = 0
FEATURE [Sketcher::SketchObject] Sketch030
  ArcFitTolerance = 1e-06
  AttachmentSupport = -> [XY_Plane125]
  FullyConstrained = true
  MakeInternals = false
  MapMode = 5
  sketch-geometry (10):
    g0: LineSegment StartX=42 StartY=6.104e-13 StartZ=0 EndX=54 EndY=6.104e-13 EndZ=0
    g1: LineSegment StartX=56 StartY=2 StartZ=0 EndX=56 EndY=17 EndZ=0
    g2: LineSegment StartX=54 StartY=19 StartZ=0 EndX=42 EndY=19 EndZ=0
    g3: LineSegment StartX=40 StartY=17 StartZ=0 EndX=40 EndY=2 EndZ=0
    g4: ArcOfCircle CenterX=42 CenterY=2 CenterZ=0 NormalX=0 NormalY=0 NormalZ=1 AngleXU=0 Radius=2 StartAngle=3.14159 EndAngle=4.71239
    g5: ArcOfCircle CenterX=54 CenterY=2 CenterZ=0 NormalX=0 NormalY=0 NormalZ=1 AngleXU=0 Radius=2 StartAngle=4.71239 EndAngle=6.28319
    g6: ArcOfCircle CenterX=54 CenterY=17 CenterZ=0 NormalX=0 NormalY=0 NormalZ=1 AngleXU=0 Radius=2 StartAngle=3.081e-13 EndAngle=1.5708
    g7: ArcOfCircle CenterX=42 CenterY=17 CenterZ=0 NormalX=0 NormalY=0 NormalZ=1 AngleXU=0 Radius=2 StartAngle=1.5708 EndAngle=3.14159
    g8: GeomPoint [constr] X=40 Y=6.776e-13 Z=0
    g9: GeomPoint [constr] X=56 Y=19 Z=0
  constraints (24):
    c: Tangent(g0,g5) = -1.5708
    c: Tangent(g1,g5) = -1.5708
    c: Tangent(g1,g6) = -1.5708
    c: Tangent(g2,g6) = -1.5708
    c: Tangent(g2,g7) = -1.5708
    c: Tangent(g3,g7) = -1.5708
    c: Horizontal(g2)
    c: Vertical(g1)
    c: Vertical(g3)
    c: Equal(g4,g5)
    c: Equal(g5,g6)
    c: Equal(g6,g7)
    c: PointOnObject(g8,g0)
    c: PointOnObject(g8,g3)
    c: PointOnObject(g9,g1)
    c: PointOnObject(g9,g2)
    c: Radius(g5) = 2
    c: Tangent(g4,g0) = -1.5708
    c: Tangent(g4,g3) = -1.5708
    c: PointOnObject(g0,g-1)
    c: Horizontal(g0)
    c: DistanceX(g8) = 40
    c: DistanceX(g3,g1) = 16
    c: DistanceY(g0,g2) = 19
FEATURE [PartDesign::Pocket] Pocket012
  BaseFeature = -> Pad016
  Direction = (0,0,-1)
  Length = 5
  Length2 = 5
  Midplane = true
  Placement = pos=(0,0,0) rot=(1,1,1;2.0944rad)
  Profile = -> Sketch030
  ReferenceAxis = -> Sketch030 [N_Axis]
  Suppressed = false
  Type = 1
FEATURE [PartDesign::Body] Body006  label="Cover"
  AllowCompound = false
  Group = -> [Binder003,Sketch029,Pad016,Sketch030,Pocket012]
  Origin = -> Origin125
  Tip = -> Pocket012
FEATURE [App::Link] C4_C_0805_2012Metric_503ca12e0183_ln_  label="C3_C_0805_2012Metric_4e72cca1f386"
  LinkPlacement = pos=(67.8019,24.15,0) rot=(0,0,1;0rad)
  LinkedObject = -> Shape220
  Placement = pos=(67.8019,24.15,0) rot=(0,0,1;0rad)
FEATURE [App::Link] C4_C_0805_2012Metric_503ca12e0183_ln_001  label="C5_C_0805_2012Metric_28ae47cbd626"
  LinkPlacement = pos=(73.9519,26.45,0) rot=(0,0,-1;1.5708rad)
  LinkedObject = -> Shape220
  Placement = pos=(73.9519,26.45,0) rot=(0,0,-1;1.5708rad)
FEATURE [App::Link] C4_C_0805_2012Metric_503ca12e0183_ln_002  label="C1_C_0805_2012Metric_d37accec2705"
  LinkPlacement = pos=(54.8019,12.4625,0) rot=(0,0,1;1.5708rad)
  LinkedObject = -> Shape220
  Placement = pos=(54.8019,12.4625,0) rot=(0,0,1;1.5708rad)
FEATURE [App::Link] C4_C_0805_2012Metric_503ca12e0183_ln_003  label="C2_C_0805_2012Metric_2ac89fd6181a"
  LinkPlacement = pos=(55.1519,26.35,0) rot=(0,0,1;3.14159rad)
  LinkedObject = -> Shape220
  Placement = pos=(55.1519,26.35,0) rot=(0,0,1;3.14159rad)
FEATURE [App::Link] D5_LED_0805_2012Metric_addddc7d8c4d_ln_  label="D2_LED_0805_2012Metric_b1ac93e87744"
  LinkPlacement = pos=(65.5519,34.2,0) rot=(0,0,1;3.14159rad)
  LinkedObject = -> Shape219
  Placement = pos=(65.5519,34.2,0) rot=(0,0,1;3.14159rad)
FEATURE [App::Link] D5_LED_0805_2012Metric_addddc7d8c4d_ln_001  label="D4_LED_0805_2012Metric_2f2898e6044c"
  LinkPlacement = pos=(21.8019,-1.4,0) rot=(0,0,1;0rad)
  LinkedObject = -> Shape219
  Placement = pos=(21.8019,-1.4,0) rot=(0,0,1;0rad)
FEATURE [App::Link] D5_LED_0805_2012Metric_addddc7d8c4d_ln_002  label="D3_LED_0805_2012Metric_f59d025524fa"
  LinkPlacement = pos=(34.2519,-1.35,0) rot=(0,0,1;0rad)
  LinkedObject = -> Shape219
  Placement = pos=(34.2519,-1.35,0) rot=(0,0,1;0rad)
FEATURE [App::Link] D5_LED_0805_2012Metric_addddc7d8c4d_ln_003  label="D1_LED_0805_2012Metric_24725dc72cbf"
  LinkPlacement = pos=(45.7294,33.85,0) rot=(0,0,1;0rad)
  LinkedObject = -> Shape219
  Placement = pos=(45.7294,33.85,0) rot=(0,0,1;0rad)
FEATURE [PartDesign::CoordinateSystem] Local_CS_af2
  AttacherType = Attacher::AttachEngine3D
  MapMode = 2
FEATURE [Sketcher::SketchObject] PCB_Sketch_af2
  ArcFitTolerance = 1e-06
  FullyConstrained = false
  MakeInternals = false
  sketch-geometry (8):
    g0: LineSegment StartX=-3.25 StartY=33.75 StartZ=0 EndX=-3.25 EndY=0 EndZ=0
    g1: LineSegment StartX=-3e-06 StartY=-3.25 StartZ=0 EndX=78.1069 EndY=-3.25 EndZ=0
    g2: LineSegment StartX=78.0684 StartY=37.05 StartZ=0 EndX=-3e-06 EndY=37 EndZ=0
    g3: LineSegment StartX=81.3569 StartY=-0.05 StartZ=0 EndX=81.3519 EndY=33.75 EndZ=0
    g4: ArcOfCircle CenterX=-4.57444e-06 CenterY=33.75 CenterZ=0 NormalX=0 NormalY=0 NormalZ=-1 AngleXU=-4.84444e-07 Radius=3.25 StartAngle=0 EndAngle=1.5708
    g5: ArcOfCircle CenterX=78.1565 CenterY=-0.0500005 CenterZ=0 NormalX=0 NormalY=0 NormalZ=-1 AngleXU=3.14159 Radius=3.20038 StartAngle=0 EndAngle=1.5863
    g6: ArcOfCircle CenterX=2.25399e-06 CenterY=5.25399e-06 CenterZ=0 NormalX=0 NormalY=0 NormalZ=-1 AngleXU=-1.57079 Radius=3.25001 StartAngle=0 EndAngle=1.57079
    g7: ArcOfCircle CenterX=78.0684 CenterY=33.7665 CenterZ=0 NormalX=0 NormalY=0 NormalZ=-1 AngleXU=1.5708 Radius=3.28349 StartAngle=0 EndAngle=1.57582
  constraints (8):
    c: Coincident(g0,g6)
    c: Coincident(g0,g4)
    c: Coincident(g1,g6)
    c: Coincident(g2,g4)
    c: Coincident(g2,g7)
    c: Coincident(g1,g5)
    c: Coincident(g3,g5)
    c: Coincident(g3,g7)
FEATURE [Part::Feature] Part__Feature563  label="EG1271--3DModel-STEP-520916"
  Placement = pos=(-0.95,3.3,1e-16) rot=(-1,0,0;1.5708rad)
  shape: bbox 8.5 x 8.5 x 3.6 mm, 203 faces (baked)
FEATURE [App::Part] EG1271  label="SW1_EG1271_4a5e37d836bd[2]"
  Group = -> [Part__Feature563]
  Origin = -> Origin131
  Placement = pos=(59.4019,31.9925,0) rot=(0.57735,-0.57735,-0.57735;2.0944rad)
FEATURE [Part::Feature] Pcb_af2
  Placement = pos=(-116.598,132.8,0) rot=(0,0,1;0rad)
  shape: bbox 84.61 x 40.3 x 1.6 mm, 93 faces (baked)
FEATURE [App::Part] Board_Geoms_af2
  Group = -> [Pcb_af2,PCB_Sketch_af2]
  Origin = -> Origin126
FEATURE [App::Link] R6_R_0805_2012Metric_107d00e598e8_ln_  label="R10_R_0805_2012Metric_bc79bea3652c"
  LinkPlacement = pos=(70.5019,8.75,0) rot=(0,0,1;0rad)
  LinkedObject = -> Shape221
  Placement = pos=(70.5019,8.75,0) rot=(0,0,1;0rad)
FEATURE [App::Link] R6_R_0805_2012Metric_107d00e598e8_ln_001  label="R5_R_0805_2012Metric_7b1dd90d981d"
  LinkPlacement = pos=(71.1519,4.5,0) rot=(0,0,-1;1.5708rad)
  LinkedObject = -> Shape221
  Placement = pos=(71.1519,4.5,0) rot=(0,0,-1;1.5708rad)
FEATURE [App::Link] R6_R_0805_2012Metric_107d00e598e8_ln_002  label="R8_R_0805_2012Metric_019b0a23d302"
  LinkPlacement = pos=(17.7019,-1.4,0) rot=(0,0,1;3.14159rad)
  LinkedObject = -> Shape221
  Placement = pos=(17.7019,-1.4,0) rot=(0,0,1;3.14159rad)
FEATURE [App::Link] R6_R_0805_2012Metric_107d00e598e8_ln_003  label="R7_R_0805_2012Metric_f2bb4e87471c"
  LinkPlacement = pos=(30.3019,-1.35,0) rot=(0,0,1;3.14159rad)
  LinkedObject = -> Shape221
  Placement = pos=(30.3019,-1.35,0) rot=(0,0,1;3.14159rad)
FEATURE [App::Link] R6_R_0805_2012Metric_107d00e598e8_ln_004  label="R11_R_0805_2012Metric_cbb1ffbb871f"
  LinkPlacement = pos=(74.1019,3.5,0) rot=(0,0,1;0rad)
  LinkedObject = -> Shape221
  Placement = pos=(74.1019,3.5,0) rot=(0,0,1;0rad)
FEATURE [App::Link] R6_R_0805_2012Metric_107d00e598e8_ln_005  label="R4_R_0805_2012Metric_79a709f99c1f"
  LinkPlacement = pos=(64.3019,13.85,0) rot=(0,0,-1;1.5708rad)
  LinkedObject = -> Shape221
  Placement = pos=(64.3019,13.85,0) rot=(0,0,-1;1.5708rad)
FEATURE [App::Link] R6_R_0805_2012Metric_107d00e598e8_ln_006  label="R1_R_0805_2012Metric_f812c57f1ae6"
  LinkPlacement = pos=(41.6794,33.85,0) rot=(0,0,1;3.14159rad)
  LinkedObject = -> Shape221
  Placement = pos=(41.6794,33.85,0) rot=(0,0,1;3.14159rad)
FEATURE [App::Link] R6_R_0805_2012Metric_107d00e598e8_ln_007  label="R12_R_0805_2012Metric_5b2256aa78e2"
  LinkPlacement = pos=(67.6519,19.4,0) rot=(0,0,1;1.5708rad)
  LinkedObject = -> Shape221
  Placement = pos=(67.6519,19.4,0) rot=(0,0,1;1.5708rad)
FEATURE [App::Link] R6_R_0805_2012Metric_107d00e598e8_ln_008  label="R13_R_0805_2012Metric_9ae3f8a0fe08"
  LinkPlacement = pos=(74.4019,6.6,0) rot=(0,0,1;0rad)
  LinkedObject = -> Shape221
  Placement = pos=(74.4019,6.6,0) rot=(0,0,1;0rad)
FEATURE [App::Link] R6_R_0805_2012Metric_107d00e598e8_ln_009  label="R9_R_0805_2012Metric_579d020efb7b"
  LinkPlacement = pos=(5.2019,0,0) rot=(0,0,1;1.5708rad)
  LinkedObject = -> Shape221
  Placement = pos=(5.2019,0,0) rot=(0,0,1;1.5708rad)
FEATURE [App::Link] R6_R_0805_2012Metric_107d00e598e8_ln_010  label="R2_R_0805_2012Metric_2c582bd89e6a"
  LinkPlacement = pos=(44.5019,0.2,0) rot=(0,0,1;1.5708rad)
  LinkedObject = -> Shape221
  Placement = pos=(44.5019,0.2,0) rot=(0,0,1;1.5708rad)
FEATURE [App::Link] R6_R_0805_2012Metric_107d00e598e8_ln_011  label="R3_R_0805_2012Metric_9362438b08fe"
  LinkPlacement = pos=(46.6019,0.2,0) rot=(0,0,1;1.5708rad)
  LinkedObject = -> Shape221
  Placement = pos=(46.6019,0.2,0) rot=(0,0,1;1.5708rad)
FEATURE [Part::Feature] Shape219  label="D5_LED_0805_2012Metric_addddc7d8c4d"
  Placement = pos=(10.6019,-1.4,0) rot=(0,0,1;0rad)
  shape: bbox 2 x 1.25 x 1.1 mm, 50 faces (baked)
FEATURE [Part::Feature] Shape220  label="C4_C_0805_2012Metric_503ca12e0183"
  Placement = pos=(62.5519,10.65,0) rot=(0,0,1;3.14159rad)
  shape: bbox 2 x 1.25 x 1.25 mm, 28 faces (baked)
FEATURE [Part::Feature] Shape221  label="R6_R_0805_2012Metric_107d00e598e8"
  Placement = pos=(69.6019,34.2,0) rot=(0,0,1;0rad)
  shape: bbox 2 x 1.2 x 0.45 mm, 26 faces (baked)
FEATURE [Part::Feature] Shape222  label="J1_PinHeader_1x06_P254mm_Horizontal_d97fc2a6fff9"
  Placement = pos=(77.1269,23.15,0) rot=(0,0,1;0rad)
  shape: bbox 10.36 x 15.24 x 5.54 mm, 166 faces (baked)
FEATURE [Part::Feature] Shape223  label="U2_SOIC_16W_75x103mm_P127mm_fa65b6f71744"
  Placement = pos=(59.4019,4.05,0) rot=(0,0,1;0rad)
  shape: bbox 10.3 x 10.3 x 2.75 mm, 276 faces (baked)
FEATURE [Part::Feature] Shape224  label="PS1_Converter_DCDC_muRata_CRE1xxxxxx3C_THT_47c8bddfce11[2]"
  Placement = pos=(55.6019,20,0) rot=(0,0,1;1.5708rad)
  shape: bbox 11.62 x 6.195 x 11.72 mm, 30 faces (baked)
FEATURE [Part::Feature] Shape225  label="U3_SOT_223_665b96088a82"
  Placement = pos=(68.1019,29.15,0) rot=(0,0,1;0rad)
  shape: bbox 7 x 6.5 x 1.7 mm, 78 faces (baked)
FEATURE [Part::Feature] Shape226  label="U5_SOT_23_6_c7d6b6168944"
  Placement = pos=(72.6319,19.4652,-1.6) rot=(0,1,0;3.14159rad)
  shape: bbox 2.8 x 2.9 x 1.55 mm, 124 faces (baked)
FEATURE [App::Part] Top_af2
  Group = -> [Shape219,Shape220,Shape221,Shape222,D5_LED_0805_2012Metric_addddc7d8c4d_ln_,C4_C_0805_2012Metric_503ca12e0183_ln_,R6_R_0805_2012Metric_107d00e598e8_ln_,C4_C_0805_2012Metric_503ca12e0183_ln_001,R6_R_0805_2012Metric_107d00e598e8_ln_001,R6_R_0805_2012Metric_107d00e598e8_ln_002,R6_R_0805_2012Metric_107d00e598e8_ln_003,R6_R_0805_2012Metric_107d00e598e8_ln_004,R6_R_0805_2012Metric_107d00e598e8_ln_005,+15 more]
  Origin = -> Origin129
FEATURE [App::Link] U5_SOT_23_6_c7d6b6168944_ln_  label="U6_SOT_23_6_a45df391a2c1"
  LinkPlacement = pos=(72.3779,12.912,-1.6) rot=(0,1,0;3.14159rad)
  LinkedObject = -> Shape226
  Placement = pos=(72.3779,12.912,-1.6) rot=(0,1,0;3.14159rad)
FEATURE [App::Part] Bot_af2
  Group = -> [Shape226,U5_SOT_23_6_c7d6b6168944_ln_]
  Origin = -> Origin130
FEATURE [App::Part] Step_Models_af2
  Group = -> [Top_af2,Bot_af2]
  Origin = -> Origin128
FEATURE [App::Part] Board_af2  label="IsolatedPicoprobeV1"
  Group = -> [Local_CS_af2,Board_Geoms_af2,Step_Models_af2]
  Origin = -> Origin127
  Placement = pos=(145.2,7.7,3.6) rot=(0,0.707107,0.707107;3.14159rad)
FEATURE [Sketcher::SketchObject] Sketch031
  ArcFitTolerance = 1e-06
  AttachmentOffset = pos=(0,0,-6) rot=(0,0,1;0rad)
  AttachmentSupport = -> [XZ_Plane068]
  ExternalGeometry = -> [Pocket002]
  FullyConstrained = true
  MakeInternals = false
  MapMode = 5
  Placement = pos=(0,6,-1.3e-15) rot=(1,0,0;1.5708rad)
  sketch-geometry (18):
    g0: LineSegment StartX=44.67 StartY=0 StartZ=0 EndX=191.67 EndY=0 EndZ=0
    g1: LineSegment StartX=191.67 StartY=0 StartZ=0 EndX=191.67 EndY=13 EndZ=0
    g2: LineSegment StartX=191.67 StartY=13 StartZ=0 EndX=148.458 EndY=13 EndZ=0
    g3: LineSegment StartX=148.458 StartY=13 StartZ=0 EndX=148.458 EndY=40.7307 EndZ=0
    g4: LineSegment StartX=145.158 StartY=44.0307 StartZ=0 EndX=67.1585 EndY=44.0307 EndZ=0
    g5: LineSegment StartX=63.8585 StartY=40.7307 StartZ=0 EndX=63.8585 EndY=13 EndZ=0
    g6: LineSegment StartX=63.8585 StartY=13 StartZ=0 EndX=44.67 EndY=13 EndZ=0
    g7: LineSegment StartX=44.67 StartY=13 StartZ=0 EndX=44.67 EndY=0 EndZ=0
    g8: Circle CenterX=67.1585 CenterY=40.7307 CenterZ=0 NormalX=0 NormalY=0 NormalZ=1 AngleXU=0 Radius=1.125
    g9: ArcOfCircle CenterX=67.1585 CenterY=40.7307 CenterZ=0 NormalX=0 NormalY=0 NormalZ=1 AngleXU=0 Radius=3.3 StartAngle=1.5708 EndAngle=3.14159
    g10: Circle CenterX=67.1585 CenterY=6.98074 CenterZ=0 NormalX=0 NormalY=0 NormalZ=1 AngleXU=0 Radius=1.125
    g11: ArcOfCircle CenterX=145.158 CenterY=40.7307 CenterZ=0 NormalX=0 NormalY=0 NormalZ=1 AngleXU=0 Radius=3.3 StartAngle=0 EndAngle=1.5708
    g12: Circle CenterX=145.158 CenterY=40.7307 CenterZ=0 NormalX=0 NormalY=0 NormalZ=1 AngleXU=0 Radius=1.125
    g13: Circle CenterX=145.158 CenterY=6.98074 CenterZ=0 NormalX=0 NormalY=0 NormalZ=1 AngleXU=0 Radius=1.125
    g14: LineSegment [constr] StartX=37.67 StartY=8.125 StartZ=0 EndX=44.67 EndY=6e-16 EndZ=0
    g15: LineSegment [constr] StartX=51.67 StartY=8.125 StartZ=0 EndX=44.67 EndY=-3e-16 EndZ=0
    g16: LineSegment [constr] StartX=187.09 StartY=0 StartZ=0 EndX=191.67 EndY=0 EndZ=0
    g17: LineSegment [constr] StartX=196.25 StartY=0 StartZ=0 EndX=191.67 EndY=0 EndZ=0
  constraints (48):
    c: PointOnObject(g0,g-1)
    c: Horizontal(g0)
    c: Coincident(g1,g0)
    c: Vertical(g1)
    c: Coincident(g2,g1)
    c: Horizontal(g2)
    c: Coincident(g3,g2)
    c: Vertical(g3)
    c: Horizontal(g4)
    c: Vertical(g5)
    c: Coincident(g6,g5)
    c: Horizontal(g6)
    c: Coincident(g7,g6)
    c: Vertical(g7)
    c: Coincident(g7,g0)
    c: DistanceX(g5,g3) = 84.6
    c: Diameter(g8) = 2.25
    c: Coincident(g9,g8)
    c: Tangent(g4,g9) = -1.5708
    c: Tangent(g5,g9) = -1.5708
    c: DistanceX(g8) = 67.1585
    c: DistanceY(g8) = 40.7307
    c: Radius(g9) = 3.3
    c: Vertical(g8,g10)
    c: Equal(g10,g8)
    c: Tangent(g4,g11) = -1.5708
    c: Tangent(g3,g11) = -1.5708
    c: Equal(g1,g7)
    c: Coincident(g12,g11)
    c: Equal(g12,g13)
    c: Equal(g13,g8)
    c: Horizontal(g11,g8)
    c: Vertical(g11,g13)
    c: Horizontal(g13,g10)
    c: DistanceY(g10,g8) = 33.75
    c: DistanceY(g1,g1) = 13
    c: Symmetric(g-3,g-3,g14)
    c: Symmetric(g-4,g-4,g15)
    c: Coincident(g15,g14)
    c: Equal(g14,g15)
    c: Coincident(g0,g14)
    c: PointOnObject(g16,g-5)
    c: Horizontal(g16)
    c: PointOnObject(g17,g-6)
    c: Coincident(g17,g16)
    c: Horizontal(g17)
    c: Equal(g16,g17)
    c: Coincident(g16,g0)
FEATURE [PartDesign::Pad] Pad017
  BaseFeature = -> Pocket002
  Direction = (0,-1,2e-16)
  Length = 6
  Length2 = 10
  Profile = -> Sketch031
  ReferenceAxis = -> Sketch031 [N_Axis]
  Suppressed = false
  Type = 0
FEATURE [Sketcher::SketchObject] Sketch032
  ArcFitTolerance = 1e-06
  AttachmentSupport = -> [Pad017]
  ExternalGeometry = -> [Pad017]
  FullyConstrained = true
  MakeInternals = false
  MapMode = 5
  Placement = pos=(0,6,0) rot=(0,0.707107,0.707107;3.14159rad)
  sketch-geometry (7):
    g0: LineSegment StartX=-64.8585 StartY=37.4307 StartZ=0 EndX=-64.8585 EndY=13.0307 EndZ=0
    g1: LineSegment StartX=-95.4585 StartY=13.0307 StartZ=0 EndX=-95.4585 EndY=43.0307 EndZ=0
    g2: LineSegment StartX=-64.8585 StartY=13.0307 StartZ=0 EndX=-95.4585 EndY=13.0307 EndZ=0
    g3: LineSegment StartX=-95.4585 StartY=43.0307 StartZ=0 EndX=-70.4585 EndY=43.0307 EndZ=0
    g4: ArcOfCircle CenterX=-67.1585 CenterY=40.7307 CenterZ=0 NormalX=0 NormalY=0 NormalZ=1 AngleXU=0 Radius=3.3 StartAngle=3.14159 EndAngle=4.71239
    g5: LineSegment StartX=-70.4585 StartY=43.0307 StartZ=0 EndX=-70.4585 EndY=40.7307 EndZ=0
    g6: LineSegment StartX=-67.1585 StartY=37.4307 StartZ=0 EndX=-64.8585 EndY=37.4307 EndZ=0
  constraints (19):
    c: Vertical(g0)
    c: Vertical(g1)
    c: Coincident(g2,g0)
    c: Coincident(g2,g1)
    c: Horizontal(g2)
    c: Coincident(g3,g1)
    c: Horizontal(g3)
    c: DistanceY(g3,g-4) = 1
    c: DistanceX(g0,g-3) = 1
    c: Coincident(g5,g3)
    c: Vertical(g5)
    c: Horizontal(g6)
    c: Coincident(g0,g6)
    c: Coincident(g4,g-5)
    c: Equal(g-6,g4)
    c: DistanceX(g3,g3) = 25
    c: DistanceY(g1,g1) = 30
    c: Tangent(g5,g4) = -1.5708
    c: Tangent(g6,g4) = -1.5708
FEATURE [PartDesign::Pocket] Pocket013
  BaseFeature = -> Pad017
  Direction = (0,-1,2e-16)
  Length = 4
  Length2 = 5
  Profile = -> Sketch032
  ReferenceAxis = -> Sketch032 [N_Axis]
  Suppressed = false
  Type = 0
FEATURE [App::Link] D_Z_5V6_miniMELF_D_MiniMELF_Standard_a8192f6c5621_ln_  label="_Z_5V6_miniMELF_D_MiniMELF_Standard_ca1fadf4eb28"
  LinkPlacement = pos=(57.8,46.4,0) rot=(0,0,1;0rad)
  LinkedObject = -> Shape235
  Placement = pos=(57.8,46.4,0) rot=(0,0,1;0rad)
FEATURE [App::Link] D_Z_5V6_miniMELF_D_MiniMELF_Standard_a8192f6c5621_ln_001  label="_Z_5V6_miniMELF_D_MiniMELF_Standard_49aaf989b642"
  LinkPlacement = pos=(64.4,23.5,0) rot=(0,0,-1;1.5708rad)
  LinkedObject = -> Shape235
  Placement = pos=(64.4,23.5,0) rot=(0,0,-1;1.5708rad)
FEATURE [App::Link] D_Z_5V6_miniMELF_D_MiniMELF_Standard_a8192f6c5621_ln_002  label="_Z_5V6_miniMELF_D_MiniMELF_Standard_869c8d3e9313"
  LinkPlacement = pos=(45,7.6,0) rot=(0,0,1;0rad)
  LinkedObject = -> Shape235
  Placement = pos=(45,7.6,0) rot=(0,0,1;0rad)
FEATURE [PartDesign::CoordinateSystem] Local_CS_f042
  AttacherType = Attacher::AttachEngine3D
  MapMode = 2
FEATURE [Sketcher::SketchObject] PCB_Sketch_f042
  ArcFitTolerance = 1e-06
  FullyConstrained = false
  MakeInternals = false
  sketch-geometry (18):
    g0: LineSegment StartX=36.25 StartY=-13.5 StartZ=0 EndX=36.25 EndY=-8 EndZ=0
    g1: LineSegment StartX=-10 StartY=-4 StartZ=0 EndX=32.25 EndY=-4 EndZ=0
    g2: LineSegment StartX=-14 StartY=-1.7e-15 StartZ=0 EndX=-14 EndY=52 EndZ=0
    g3: LineSegment StartX=165 StartY=52 StartZ=0 EndX=165 EndY=47 EndZ=0
    g4: LineSegment StartX=64 StartY=-4 StartZ=0 EndX=161 EndY=-4 EndZ=0
    g5: LineSegment StartX=165 StartY=4.99998 StartZ=0 EndX=165 EndY=0 EndZ=0
    g6: LineSegment StartX=60 StartY=-13.5 StartZ=0 EndX=60 EndY=-8 EndZ=0
    g7: LineSegment StartX=39.25 StartY=-16.5 StartZ=0 EndX=57 EndY=-16.5 EndZ=0
    g8: LineSegment StartX=-10 StartY=56 StartZ=0 EndX=161 EndY=56 EndZ=0
    g9: LineSegment StartX=165 StartY=47 StartZ=0 EndX=165 EndY=4.99998 EndZ=0
    g10: ArcOfCircle CenterX=-10 CenterY=52 CenterZ=0 NormalX=0 NormalY=0 NormalZ=-1 AngleXU=-3.30773e-06 Radius=3.99999 StartAngle=0 EndAngle=1.5708
    g11: ArcOfCircle CenterX=57 CenterY=-13.5 CenterZ=0 NormalX=0 NormalY=0 NormalZ=-1 AngleXU=-3.14158 Radius=3.00005 StartAngle=0 EndAngle=1.57077
    g12: ArcOfCircle CenterX=64 CenterY=-7.99995 CenterZ=0 NormalX=0 NormalY=0 NormalZ=-1 AngleXU=-1.18432e-05 Radius=3.99995 StartAngle=0 EndAngle=1.57082
    g13: ArcOfCircle CenterX=161 CenterY=4.48113e-05 CenterZ=0 NormalX=0 NormalY=0 NormalZ=-1 AngleXU=-3.14158 Radius=4.00004 StartAngle=0 EndAngle=1.57077
    g14: ArcOfCircle CenterX=39.25 CenterY=-13.5 CenterZ=0 NormalX=0 NormalY=0 NormalZ=-1 AngleXU=-1.5708 Radius=2.99998 StartAngle=0 EndAngle=1.57081
    g15: ArcOfCircle CenterX=32.25 CenterY=-8.00002 CenterZ=0 NormalX=0 NormalY=0 NormalZ=-1 AngleXU=1.5708 Radius=4.00002 StartAngle=0 EndAngle=1.57079
    g16: ArcOfCircle CenterX=-10 CenterY=-1.83522e-05 CenterZ=0 NormalX=0 NormalY=0 NormalZ=-1 AngleXU=-1.5708 Radius=3.99998 StartAngle=0 EndAngle=1.57081
    g17: ArcOfCircle CenterX=161 CenterY=52 CenterZ=0 NormalX=0 NormalY=0 NormalZ=-1 AngleXU=1.5708 Radius=4.00002 StartAngle=0 EndAngle=1.57079
  constraints (18):
    c: Coincident(g2,g16)
    c: Coincident(g2,g10)
    c: Coincident(g1,g16)
    c: Coincident(g8,g10)
    c: Coincident(g1,g15)
    c: Coincident(g0,g14)
    c: Coincident(g0,g15)
    c: Coincident(g7,g14)
    c: Coincident(g7,g11)
    c: Coincident(g6,g11)
    c: Coincident(g6,g12)
    c: Coincident(g4,g12)
    c: Coincident(g4,g13)
    c: Coincident(g8,g17)
    c: Coincident(g5,g13)
    c: Coincident(g5,g9)
    c: Coincident(g3,g9)
    c: Coincident(g3,g17)
FEATURE [Part::Feature] Part__Feature564  label="TestPoint_Loop_D2_54mm_Drill1_5mm_Beaded_cp008"
  shape: bbox 3 x 3 x 3 mm, 4 faces (baked)
FEATURE [Part::Feature] Part__Feature565  label="TestPoint_Loop_D2_54mm_Drill1_5mm_Beaded_cp009"
  shape: bbox 3.415 x 0.9501 x 9.255 mm, 7 faces (baked)
FEATURE [Part::Feature] Part__Feature566  label="9e9c6de3-9c39-11ed-93f0-dde97e994e83_part"
  shape: bbox 6.22 x 6.5 x 2.3 mm, 13 faces (baked)
FEATURE [Part::Feature] Part__Feature567  label="9e9c6de4-9c39-11ed-93f0-dde97e994e83_part"
  shape: bbox 5.24 x 5.4 x 0.5 mm, 16 faces (baked)
FEATURE [Part::Feature] Part__Feature568  label="9e9c6de5-9c39-11ed-93f0-dde97e994e83_part"
  shape: bbox 3.552 x 0.84 x 1.44 mm, 22 faces (baked)
FEATURE [Part::Feature] Part__Feature569  label="9e9c6de5-9c39-11ed-93f0-dde97e994e83_part001"
  shape: bbox 3.552 x 0.84 x 1.44 mm, 22 faces (baked)
FEATURE [Part::Feature] Part__Feature570  label="9e9c6de5-9c39-11ed-93f0-dde97e994e83_part002"
  shape: bbox 3.552 x 0.84 x 1.44 mm, 22 faces (baked)
FEATURE [Part::Feature] Part__Feature571  label="9e9c6de5-9c39-11ed-93f0-dde97e994e83_part003"
  shape: bbox 3.552 x 0.84 x 1.44 mm, 22 faces (baked)
FEATURE [Part::Feature] Part__Feature572  label="9e9c6de5-9c39-11ed-93f0-dde97e994e83_part004"
  shape: bbox 3.552 x 0.84 x 1.44 mm, 22 faces (baked)
FEATURE [Part::Feature] Part__Feature573  label="SC1291"
  shape: bbox 3.8 x 1 x 3.8 mm, 6 faces (baked)
FEATURE [Part::Feature] Part__Feature574  label="SC1292"
  shape: bbox 3.8 x 1 x 3.8 mm, 6 faces (baked)
FEATURE [Part::Feature] Part__Feature575  label="SC1293"
  shape: bbox 3.8 x 1 x 3.8 mm, 6 faces (baked)
FEATURE [Part::Feature] Part__Feature576  label="SC1294"
  shape: bbox 3.8 x 1 x 3.8 mm, 6 faces (baked)
FEATURE [Part::Feature] Part__Feature577  label="SC1295"
  shape: bbox 2.41 x 1 x 1.6 mm, 10 faces (baked)
FEATURE [Part::Feature] Part__Feature578  label="SC1296"
  shape: bbox 2.41 x 1 x 1.6 mm, 10 faces (baked)
FEATURE [Part::Feature] Part__Feature579  label="SC1297"
  shape: bbox 2.41 x 1 x 1.6 mm, 10 faces (baked)
FEATURE [Part::Feature] Part__Feature580  label="SC1298"
  shape: bbox 2.41 x 1 x 1.6 mm, 10 faces (baked)
FEATURE [Part::Feature] Part__Feature581  label="SC1299"
  shape: bbox 2.41 x 1 x 1.6 mm, 10 faces (baked)
FEATURE [Part::Feature] Part__Feature582  label="SC1300"
  shape: bbox 2.41 x 1 x 1.6 mm, 10 faces (baked)
FEATURE [Part::Feature] Part__Feature583  label="SC1301"
  shape: bbox 2.41 x 1 x 1.6 mm, 10 faces (baked)
FEATURE [Part::Feature] Part__Feature584  label="SC1302"
  shape: bbox 2.41 x 1 x 1.6 mm, 10 faces (baked)
FEATURE [Part::Feature] Part__Feature585  label="SC1303"
  shape: bbox 2.41 x 1 x 1.6 mm, 10 faces (baked)
FEATURE [Part::Feature] Part__Feature586  label="SC1304"
  shape: bbox 2.41 x 1 x 1.6 mm, 10 faces (baked)
FEATURE [Part::Feature] Part__Feature587  label="SC1305"
  shape: bbox 2.41 x 1 x 1.6 mm, 10 faces (baked)
FEATURE [Part::Feature] Part__Feature588  label="SC1306"
  shape: bbox 2.41 x 1 x 1.6 mm, 10 faces (baked)
FEATURE [Part::Feature] Part__Feature589  label="SC1307"
  shape: bbox 2.41 x 1 x 1.6 mm, 10 faces (baked)
FEATURE [Part::Feature] Part__Feature590  label="SC1308"
  shape: bbox 2.41 x 1 x 1.6 mm, 10 faces (baked)
FEATURE [Part::Feature] Part__Feature591  label="SC1309"
  shape: bbox 2.41 x 1 x 1.6 mm, 10 faces (baked)
FEATURE [Part::Feature] Part__Feature592  label="SC1310"
  shape: bbox 2.41 x 1 x 1.6 mm, 10 faces (baked)
FEATURE [Part::Feature] Part__Feature593  label="SC1311"
  shape: bbox 2.41 x 1 x 1.6 mm, 12 faces (baked)
FEATURE [Part::Feature] Part__Feature594  label="SC1312"
  shape: bbox 2.41 x 1 x 1.6 mm, 12 faces (baked)
FEATURE [Part::Feature] Part__Feature595  label="SC1313"
  shape: bbox 2.41 x 1 x 1.6 mm, 12 faces (baked)
FEATURE [Part::Feature] Part__Feature596  label="SC1314"
  shape: bbox 2.41 x 1 x 1.6 mm, 12 faces (baked)
FEATURE [Part::Feature] Part__Feature597  label="SC1315"
  shape: bbox 2.41 x 1 x 1.6 mm, 12 faces (baked)
FEATURE [Part::Feature] Part__Feature598  label="SC1316"
  shape: bbox 2.41 x 1 x 1.6 mm, 12 faces (baked)
FEATURE [Part::Feature] Part__Feature599  label="SC1317"
  shape: bbox 2.41 x 1 x 1.6 mm, 12 faces (baked)
FEATURE [Part::Feature] Part__Feature600  label="SC1318"
  shape: bbox 2.41 x 1 x 1.6 mm, 12 faces (baked)
FEATURE [Part::Feature] Part__Feature601  label="SC1319"
  shape: bbox 2.41 x 1 x 1.6 mm, 10 faces (baked)
FEATURE [Part::Feature] Part__Feature602  label="SC1320"
  shape: bbox 2.41 x 1 x 1.6 mm, 10 faces (baked)
FEATURE [Part::Feature] Part__Feature603  label="SC1321"
  shape: bbox 2.41 x 1 x 1.6 mm, 10 faces (baked)
FEATURE [Part::Feature] Part__Feature604  label="SC1322"
  shape: bbox 2.41 x 1 x 1.6 mm, 10 faces (baked)
FEATURE [Part::Feature] Part__Feature605  label="SC1323"
  shape: bbox 2.41 x 1 x 1.6 mm, 10 faces (baked)
FEATURE [Part::Feature] Part__Feature606  label="SC1324"
  shape: bbox 2.41 x 1 x 1.6 mm, 10 faces (baked)
FEATURE [Part::Feature] Part__Feature607  label="SC1325"
  shape: bbox 2.41 x 1 x 1.6 mm, 10 faces (baked)
FEATURE [Part::Feature] Part__Feature608  label="SC1326"
  shape: bbox 2.41 x 1 x 1.6 mm, 10 faces (baked)
FEATURE [Part::Feature] Part__Feature609  label="SC1327"
  shape: bbox 2.41 x 1 x 1.6 mm, 10 faces (baked)
FEATURE [Part::Feature] Part__Feature610  label="SC1328"
  shape: bbox 2.41 x 1 x 1.6 mm, 10 faces (baked)
FEATURE [Part::Feature] Part__Feature611  label="SC1329"
  shape: bbox 2.41 x 1 x 1.6 mm, 10 faces (baked)
FEATURE [Part::Feature] Part__Feature612  label="SC1330"
  shape: bbox 2.41 x 1 x 1.6 mm, 10 faces (baked)
FEATURE [Part::Feature] Part__Feature613  label="SC1331"
  shape: bbox 2.41 x 1 x 1.6 mm, 10 faces (baked)
FEATURE [Part::Feature] Part__Feature614  label="SC1332"
  shape: bbox 2.41 x 1 x 1.6 mm, 10 faces (baked)
FEATURE [Part::Feature] Part__Feature615  label="SC1333"
  shape: bbox 2.41 x 1 x 1.6 mm, 10 faces (baked)
FEATURE [Part::Feature] Part__Feature616  label="SC1334"
  shape: bbox 2.41 x 1 x 1.6 mm, 10 faces (baked)
FEATURE [Part::Feature] Part__Feature617  label="SC1335"
  shape: bbox 1.6 x 1 x 2.41 mm, 12 faces (baked)
FEATURE [Part::Feature] Part__Feature618  label="SC1336"
  shape: bbox 1.6 x 1 x 2.41 mm, 12 faces (baked)
FEATURE [Part::Feature] Part__Feature619  label="SC1337"
  shape: bbox 1.6 x 1 x 2.41 mm, 13 faces (baked)
FEATURE [Part::Feature] Part__Feature620  label="SC1338"
  shape: bbox 3.35 x 0.9 x 4.2 mm, 6 faces (baked)
FEATURE [Part::Feature] Part__Feature621  label="SC1339"
  shape: bbox 2.2 x 0.9 x 2.8 mm, 6 faces (baked)
FEATURE [Part::Feature] Part__Feature622  label="SC1340"
  shape: bbox 7 x 0.9 x 7 mm, 6 faces (baked)
FEATURE [Part::Feature] Part__Feature623  label="SC1341"
  shape: bbox 2.1 x 0.9 x 3 mm, 6 faces (baked)
FEATURE [Part::Feature] Part__Feature624  label="SC1342"
  shape: bbox 3 x 0.9 x 2.2 mm, 6 faces (baked)
FEATURE [Part::Feature] Part__Feature625  label="SC1343"
  shape: bbox 2.4 x 0.9 x 2.4 mm, 6 faces (baked)
FEATURE [Part::Feature] Part__Feature626  label="SC1344"
  shape: bbox 2.25 x 1.1 x 3.4 mm, 13 faces (baked)
FEATURE [Part::Feature] Part__Feature627  label="SC1345"
  shape: bbox 0.35 x 0.1 x 0.5 mm, 6 faces (baked)
FEATURE [Part::Feature] Part__Feature628  label="SC1346"
  shape: bbox 1.75 x 0.1 x 0.9 mm, 6 faces (baked)
FEATURE [Part::Feature] Part__Feature629  label="SC1347"
  shape: bbox 1.2 x 0.1 x 0.505 mm, 6 faces (baked)
FEATURE [Part::Feature] Part__Feature630  label="SC1348"
  shape: bbox 1.2 x 0.1 x 0.505 mm, 6 faces (baked)
FEATURE [Part::Feature] Part__Feature631  label="SC1349"
  shape: bbox 0.35 x 0.1 x 0.5 mm, 6 faces (baked)
FEATURE [Part::Feature] Part__Feature632  label="SC1350"
  shape: bbox 0.35 x 0.1 x 0.5 mm, 6 faces (baked)
FEATURE [Part::Feature] Part__Feature633  label="SC1351"
  shape: bbox 1.2 x 1.25 x 1.2 mm, 6 faces (baked)
FEATURE [Part::Feature] Part__Feature634  label="SC1352"
  shape: bbox 2 x 1.25 x 1 mm, 6 faces (baked)
FEATURE [Part::Feature] Part__Feature635  label="SC1353"
  shape: bbox 1.2 x 1.25 x 1.2 mm, 6 faces (baked)
FEATURE [Part::Feature] Part__Feature636  label="SC1354"
  shape: bbox 0.4 x 1.25 x 1.2 mm, 6 faces (baked)
FEATURE [Part::Feature] Part__Feature637  label="SC1355"
  shape: bbox 2 x 1.25 x 0.7 mm, 6 faces (baked)
FEATURE [Part::Feature] Part__Feature638  label="SC1356"
  shape: bbox 0.4 x 1.25 x 1.2 mm, 6 faces (baked)
FEATURE [Part::Feature] Part__Feature639  label="SC1357"
  shape: bbox 0.4 x 1.25 x 1.2 mm, 6 faces (baked)
FEATURE [Part::Feature] Part__Feature640  label="SC1358"
  shape: bbox 0.4 x 1.25 x 1.2 mm, 6 faces (baked)
FEATURE [Part::Feature] Part__Feature641  label="SC1359"
  shape: bbox 2 x 1.25 x 0.7 mm, 6 faces (baked)
FEATURE [Part::Feature] Part__Feature642  label="SC1360"
  shape: bbox 0.9 x 0.2 x 0.9 mm, 6 faces (baked)
FEATURE [Part::Feature] Part__Feature643  label="SC1361"
  shape: bbox 1.95 x 0.85 x 1 mm, 6 faces (baked)
FEATURE [Part::Feature] Part__Feature644  label="SC1362"
  shape: bbox 0.42 x 0.15 x 2.3 mm, 6 faces (baked)
FEATURE [Part::Feature] Part__Feature645  label="SC1363"
  shape: bbox 0.42 x 0.15 x 2.3 mm, 6 faces (baked)
FEATURE [Part::Feature] Part__Feature646  label="SC1364"
  shape: bbox 0.42 x 0.15 x 2.3 mm, 6 faces (baked)
FEATURE [Part::Feature] Part__Feature647  label="SC1365"
  shape: bbox 0.42 x 0.15 x 2.3 mm, 6 faces (baked)
FEATURE [Part::Feature] Part__Feature648  label="SC1366"
  shape: bbox 0.42 x 0.15 x 2.3 mm, 6 faces (baked)
FEATURE [Part::Feature] Part__Feature649  label="SC1367"
  shape: bbox 7.1 x 2.52 x 4.21 mm, 184 faces (baked)
FEATURE [Part::Feature] Part__Feature650  label="SC1368"
  shape: bbox 8 x 3.48 x 5.5 mm, 288 faces (baked)
FEATURE [Part::Feature] Part__Feature651  label="SC1369"
  shape: bbox 0.25 x 0.25 x 0.7 mm, 14 faces (baked)
FEATURE [Part::Feature] Part__Feature652  label="SC1370"
  shape: bbox 0.25 x 0.25 x 0.7 mm, 14 faces (baked)
FEATURE [Part::Feature] Part__Feature653  label="SC1371"
  shape: bbox 0.25 x 0.25 x 0.7 mm, 14 faces (baked)
FEATURE [Part::Feature] Part__Feature654  label="SC1372"
  shape: bbox 0.25 x 0.25 x 0.7 mm, 14 faces (baked)
FEATURE [Part::Feature] Part__Feature655  label="SC1373"
  shape: bbox 0.25 x 0.25 x 0.7 mm, 14 faces (baked)
FEATURE [Part::Feature] Part__Feature656  label="SC1374"
  shape: bbox 1.5 x 0.1 x 1.5 mm, 10 faces (baked)
FEATURE [Part::Feature] Part__Feature657  label="SC1375"
  shape: bbox 1.5 x 0.1 x 1.5 mm, 10 faces (baked)
FEATURE [Part::Feature] Part__Feature658  label="SC1376"
  shape: bbox 1.5 x 0.1 x 1.5 mm, 10 faces (baked)
FEATURE [Part::Feature] Part__Feature659  label="SC1377"
  shape: bbox 1.5 x 0.1 x 1.5 mm, 10 faces (baked)
FEATURE [Part::Feature] Part__Feature096  label="SC1378"
  shape: bbox 1.5 x 0.1 x 1.5 mm, 10 faces (baked)
FEATURE [Part::Feature] Part__Feature097  label="SC1379"
  shape: bbox 1.5 x 0.1 x 1.5 mm, 10 faces (baked)
FEATURE [Part::Feature] Part__Feature098  label="SC1380"
  shape: bbox 21 x 1 x 51 mm, 284 faces (baked)
FEATURE [Part::Feature] Part__Feature099  label="SC1381"
  shape: bbox 1.1 x 0.1 x 1.8 mm, 7 faces (baked)
FEATURE [Part::Feature] Part__Feature100  label="SC1382"
  shape: bbox 1.1 x 0.1 x 1.8 mm, 7 faces (baked)
FEATURE [Part::Feature] Part__Feature101  label="SC1383"
  shape: bbox 1.05 x 0.1 x 1.45 mm, 7 faces (baked)
FEATURE [Part::Feature] Part__Feature102  label="SC1384"
  shape: bbox 1.05 x 0.1 x 1.45 mm, 7 faces (baked)
FEATURE [Part::Feature] Pcb_f042
  Placement = pos=(-38.5,81.5284,0) rot=(0,0,1;0rad)
  shape: bbox 179 x 72.5 x 1.592 mm, 129 faces (baked)
FEATURE [App::Part] Board_Geoms_f042  label="Board_Geoms_f043"
  Group = -> [Pcb_f042,PCB_Sketch_f042]
  Origin = -> Origin132
FEATURE [App::Part] SC0919  label="_SC1009_bf1f1e83e550"
  Group = -> [Part__Feature573,Part__Feature574,Part__Feature575,Part__Feature576,Part__Feature577,Part__Feature578,Part__Feature579,Part__Feature580,Part__Feature581,Part__Feature582,Part__Feature583,Part__Feature584,Part__Feature585,Part__Feature586,Part__Feature587,Part__Feature588,Part__Feature589,Part__Feature590,Part__Feature591,Part__Feature592,Part__Feature593,Part__Feature594,Part__Feature595,+71 more]
  Origin = -> Origin144
  Placement = pos=(125.8,21.61,0) rot=(0.57735,0.57735,0.57735;2.0944rad)
FEATURE [Part::Feature] Shape227  label="_C_0805_2012Metric_42e76acedcba"
  Placement = pos=(16.25,14.8,0) rot=(0,0,1;1.5708rad)
  shape: bbox 1.25 x 2 x 1.25 mm, 28 faces (baked)
FEATURE [Part::Feature] Shape228  label="_R_0805_2012Metric_900e5a3da9ce001"
  Placement = pos=(4.5,52.6,0) rot=(0,0,1;1.5708rad)
  shape: bbox 1.2 x 2 x 0.45 mm, 26 faces (baked)
FEATURE [Part::Feature] Shape229  label="_L_Bourns_SRN6045TA_dece260f1e7e"
  Placement = pos=(6.3,40.5,0) rot=(0,0,-1;1.5708rad)
  shape: bbox 6 x 6 x 4.2 mm, 60 faces (baked)
FEATURE [Part::Feature] Shape230  label="_CP_Elec_5x58_0ee41fe4bfd3"
  Placement = pos=(61.95,31.35,0) rot=(0,0,1;1.5708rad)
  shape: bbox 6.828 x 6.985 x 5.8 mm, 41 faces (baked)
FEATURE [Part::Feature] Shape231  label="1_PinHeader_1x03_P254mm_Vertical_a2001c85ec40"
  Placement = pos=(31.8,41.2,0) rot=(0,0,-1;1.5708rad)
  shape: bbox 7.62 x 2.54 x 11.54 mm, 76 faces (baked)
FEATURE [Part::Feature] Shape232  label="_D_SOD_123_5a20a041a246"
  Placement = pos=(48.6,22.5,0) rot=(0,0,1;3.14159rad)
  shape: bbox 3.8 x 1.6 x 1.25 mm, 67 faces (baked)
FEATURE [Part::Feature] Shape233  label="_CP_Elec_8x105_ee50de3c8e020"
  Placement = pos=(17.1,49.65,0) rot=(0,0,1;1.5708rad)
  shape: bbox 10.92 x 10.73 x 10.5 mm, 41 faces (baked)
FEATURE [Part::Feature] Shape234  label="_Fuse_1206_3216Metric_05f556a6ff0d001"
  Placement = pos=(-6.35,40.75,0) rot=(0,0,1;0rad)
  shape: bbox 3.2 x 1.6 x 0.55 mm, 26 faces (baked)
FEATURE [Part::Feature] Shape235  label="D_Z_5V6_miniMELF_D_MiniMELF_Standard_a8192f6c5621"
  Placement = pos=(15.2,37.6,0) rot=(0,0,-1;1.5708rad)
  shape: bbox 1.4 x 3.6 x 1.4 mm, 13 faces (baked)
FEATURE [Part::Feature] Shape236  label="_SOIC_28W_75x179mm_P127mm_746d43082d9a001"
  Placement = pos=(83.5,16,0) rot=(0,0,-1;1.5708rad)
  shape: bbox 17.9 x 10.3 x 2.75 mm, 456 faces (baked)
FEATURE [Part::Feature] Shape237  label="_Fan_Pin_Header_Straight_1x04_37f54f52d17d001"
  Placement = pos=(18.48,4.5,0) rot=(0,0,1;0rad)
  shape: bbox 10.2 x 5.84 x 13.5 mm, 99 faces (baked)
FEATURE [Part::Feature] Shape238  label="_SOT_323_SC_70_c919c89d7c036"
  Placement = pos=(76.8,32,0) rot=(0,0,1;3.14159rad)
  shape: bbox 2 x 2 x 1.05 mm, 76 faces (baked)
FEATURE [Part::Feature] Shape239  label="_LED_0805_2012Metric_630bc1ac9417"
  Placement = pos=(30.1625,44.05,0) rot=(0,0,1;0rad)
  shape: bbox 2 x 1.25 x 1.1 mm, 50 faces (baked)
FEATURE [Part::Feature] Shape240  label="1_PinHeader_1x02_P254mm_Vertical_3b80083b2131"
  Placement = pos=(20.1,10,0) rot=(0,0,-1;1.5708rad)
  shape: bbox 5.08 x 2.54 x 11.54 mm, 52 faces (baked)
FEATURE [Part::Feature] Shape241  label="_D_SMA_147b90238019"
  Placement = pos=(12.15,41.5,0) rot=(0,0,1;1.5708rad)
  shape: bbox 2.7 x 5 x 2.22 mm, 41 faces (baked)
FEATURE [Part::Feature] Shape242  label="_MCV_01x02_G_3_81mm_8d2d7ae2d0cf001"
  Placement = pos=(-6.40002,4.7,0) rot=(0,0,1;1.5708rad)
  shape: bbox 7.55 x 9.01 x 12.6 mm, 76 faces (baked)
FEATURE [Part::Feature] Shape243  label="_L_1210_3225Metric_8f5c69fc0356"
  Placement = pos=(52.4,46,0) rot=(0,0,1;3.14159rad)
  shape: bbox 3.2 x 2.5 x 2.5 mm, 28 faces (baked)
FEATURE [Part::Feature] Shape244  label="1_PinHeader_1x06_P254mm_Vertical_f561237d0f054"
  Placement = pos=(137.72,38.7,0) rot=(0,0,1;1.5708rad)
  shape: bbox 15.24 x 2.54 x 11.54 mm, 148 faces (baked)
FEATURE [Part::Feature] Shape245  label="1_PinHeader_2x08_P254mm_Vertical_411dce5b0f098"
  Placement = pos=(118.075,4.87498,0) rot=(0,0,-1;1.5708rad)
  shape: bbox 20.32 x 5.08 x 11.54 mm, 340 faces (baked)
FEATURE [Part::Feature] Shape246  label="_JST_B2B_XH_A_3a5731dab8f004"
  Placement = pos=(94.7,44.05,0) rot=(0,0,1;0rad)
  shape: bbox 7.4 x 5.75 x 10.4 mm, 89 faces (baked)
FEATURE [Part::Feature] Shape247  label="_QSOP_16_39x49mm_P0635mm_61417655afff001"
  Placement = pos=(25.6,16,0) rot=(0,0,1;1.5708rad)
  shape: bbox 4.9 x 6 x 1.42 mm, 260 faces (baked)
FEATURE [Part::Feature] Shape248  label="_Buzzer_12x95RM76_7e9dc41d8346"
  Placement = pos=(133.6,2.45,0) rot=(0,0,1;0rad)
  shape: bbox 12.99 x 12.99 x 12.53 mm, 13 faces (baked)
FEATURE [Part::Feature] Shape249  label="_SOT_223_9813f15a1231"
  Placement = pos=(71.8,44.6,0) rot=(0,0,-1;1.5708rad)
  shape: bbox 6.5 x 7 x 1.7 mm, 78 faces (baked)
FEATURE [Part::Feature] Shape250  label="_SOT_23_6_80ad3168e82c001"
  Placement = pos=(24.13,30.2,0) rot=(0,0,1;3.14159rad)
  shape: bbox 2.8 x 2.9 x 1.55 mm, 124 faces (baked)
FEATURE [Part::Feature] Shape251  label="U_MC34063AD_SOIC_8_39x49mm_P127mm_b3cb3d8ac857"
  Placement = pos=(5.8,46.85,0) rot=(0,0,1;3.14159rad)
  shape: bbox 6 x 4.9 x 1.75 mm, 156 faces (baked)
FEATURE [Part::Feature] Shape252  label="_IDC_Header_2x08_P254mm_Vertical_e1f45a9088de001"
  Placement = pos=(159.1,27,0) rot=(0,0,1;3.14159rad)
  shape: bbox 9.1 x 27.98 x 12.1 mm, 330 faces (baked)
FEATURE [App::Part] TestPoint_Loop_D2_54mm_Drill1_5mm_Beaded_cp004  label="_TestPoint_Loop_D2_54mm_Drill1_5mm_Beaded_cp002_8f60d36f4fd009"
  Group = -> [Part__Feature564,Part__Feature565]
  Origin = -> Origin137
  Placement = pos=(58.5,14,0) rot=(0,0,1;0rad)
FEATURE [App::Link] U_MC34063AD_SOIC_8_39x49mm_P127mm_b3cb3d8ac857_ln_  label="_MC34063AD_SOIC_8_39x49mm_P127mm_867d4187783b"
  LinkPlacement = pos=(108.665,42.85,0) rot=(0,0,1;0rad)
  LinkedObject = -> Shape251
  Placement = pos=(108.665,42.85,0) rot=(0,0,1;0rad)
FEATURE [App::Link] U_MC34063AD_SOIC_8_39x49mm_P127mm_b3cb3d8ac857_ln_001  label="_MC34063AD_SOIC_8_39x49mm_P127mm_4428ff659321"
  LinkPlacement = pos=(36.475,17.4234,0) rot=(0,0,1;3.14159rad)
  LinkedObject = -> Shape251
  Placement = pos=(36.475,17.4234,0) rot=(0,0,1;3.14159rad)
FEATURE [App::Link] _CP_Elec_5x58_0ee41fe4bfd3_ln_  label="_CP_Elec_5x58_c419cd9c4a2f"
  LinkPlacement = pos=(65.05,44.15,0) rot=(0,0,1;1.5708rad)
  LinkedObject = -> Shape230
  Placement = pos=(65.05,44.15,0) rot=(0,0,1;1.5708rad)
FEATURE [App::Link] _CP_Elec_5x58_0ee41fe4bfd3_ln_001  label="C_10uF_50V_Elec_5_CP_Elec_5x58_0ee654aa8f3e"
  LinkPlacement = pos=(7,10.9,0) rot=(0,0,1;3.14159rad)
  LinkedObject = -> Shape230
  Placement = pos=(7,10.9,0) rot=(0,0,1;3.14159rad)
FEATURE [App::Link] _CP_Elec_5x58_0ee41fe4bfd3_ln_002  label="_CP_Elec_5x58_e794a3d39e80"
  LinkPlacement = pos=(32.2,49.05,0) rot=(0,0,1;1.5708rad)
  LinkedObject = -> Shape230
  Placement = pos=(32.2,49.05,0) rot=(0,0,1;1.5708rad)
FEATURE [App::Link] _CP_Elec_5x58_0ee41fe4bfd3_ln_003  label="_CP_Elec_5x58_5659c7eb80dd"
  LinkPlacement = pos=(59.05,19.25,0) rot=(0,0,1;0rad)
  LinkedObject = -> Shape230
  Placement = pos=(59.05,19.25,0) rot=(0,0,1;0rad)
FEATURE [App::Link] _CP_Elec_5x58_0ee41fe4bfd3_ln_004  label="_CP_Elec_5x58_4c4f2b69c62b"
  LinkPlacement = pos=(48.75,17.45,0) rot=(0,0,1;3.14159rad)
  LinkedObject = -> Shape230
  Placement = pos=(48.75,17.45,0) rot=(0,0,1;3.14159rad)
FEATURE [App::Link] _CP_Elec_5x58_0ee41fe4bfd3_ln_005  label="_CP_Elec_5x58_f829d7b62f1d"
  LinkPlacement = pos=(53.4,10,0) rot=(0,0,1;3.14159rad)
  LinkedObject = -> Shape230
  Placement = pos=(53.4,10,0) rot=(0,0,1;3.14159rad)
FEATURE [App::Link] _CP_Elec_5x58_0ee41fe4bfd3_ln_006  label="_CP_Elec_5x58_11de36914b62"
  LinkPlacement = pos=(85.65,52.25,0) rot=(0,0,1;0rad)
  LinkedObject = -> Shape230
  Placement = pos=(85.65,52.25,0) rot=(0,0,1;0rad)
FEATURE [App::Link] _CP_Elec_5x58_0ee41fe4bfd3_ln_007  label="_CP_Elec_5x58_efdd911fff8c001"
  LinkPlacement = pos=(159.3,13.7,0) rot=(0,0,1;0rad)
  LinkedObject = -> Shape230
  Placement = pos=(159.3,13.7,0) rot=(0,0,1;0rad)
FEATURE [App::Link] _CP_Elec_5x58_0ee41fe4bfd3_ln_008  label="_CP_Elec_5x58_eae7f9406b11"
  LinkPlacement = pos=(23,35.6,0) rot=(0,0,1;3.14159rad)
  LinkedObject = -> Shape230
  Placement = pos=(23,35.6,0) rot=(0,0,1;3.14159rad)
FEATURE [App::Link] _CP_Elec_5x58_0ee41fe4bfd3_ln_009  label="_CP_Elec_5x58_b0d551f2ee6d"
  LinkPlacement = pos=(45.15,43,0) rot=(0,0,1;3.14159rad)
  LinkedObject = -> Shape230
  Placement = pos=(45.15,43,0) rot=(0,0,1;3.14159rad)
FEATURE [App::Link] _CP_Elec_5x58_0ee41fe4bfd3_ln_010  label="_CP_Elec_5x58_a8166e63492a"
  LinkPlacement = pos=(71.7,52.25,0) rot=(0,0,1;0rad)
  LinkedObject = -> Shape230
  Placement = pos=(71.7,52.25,0) rot=(0,0,1;0rad)
FEATURE [App::Link] _CP_Elec_5x58_0ee41fe4bfd3_ln_011  label="_CP_Elec_5x58_6e01dcfa2037"
  LinkPlacement = pos=(56.6,41.2,0) rot=(0,0,1;0rad)
  LinkedObject = -> Shape230
  Placement = pos=(56.6,41.2,0) rot=(0,0,1;0rad)
FEATURE [App::Link] _CP_Elec_8x105_ee50de3c8e19_ln_001  label="_CP_Elec_8x105_9e4795b8782a001"
  LinkPlacement = pos=(-7,46.6,0) rot=(0,0,1;3.14159rad)
  LinkedObject = -> Shape233
  Placement = pos=(-7,46.6,0) rot=(0,0,1;3.14159rad)
FEATURE [App::Link] _C_0805_2012Metric_42e76acedcba_ln_  label="_C_0805_2012Metric_a49b18341ced001"
  LinkPlacement = pos=(30.15,11.2,0) rot=(0,0,1;0rad)
  LinkedObject = -> Shape227
  Placement = pos=(30.15,11.2,0) rot=(0,0,1;0rad)
FEATURE [App::Link] _C_0805_2012Metric_42e76acedcba_ln_001  label="_C_0805_2012Metric_9980a3fec6f001"
  LinkPlacement = pos=(30.85,54.75,0) rot=(0,0,1;3.14159rad)
  LinkedObject = -> Shape227
  Placement = pos=(30.85,54.75,0) rot=(0,0,1;3.14159rad)
FEATURE [App::Link] _C_0805_2012Metric_42e76acedcba_ln_002  label="_C_0805_2012Metric_8605570e78c2"
  LinkPlacement = pos=(8.95,26.6,0) rot=(0,0,1;0rad)
  LinkedObject = -> Shape227
  Placement = pos=(8.95,26.6,0) rot=(0,0,1;0rad)
FEATURE [App::Link] _C_0805_2012Metric_42e76acedcba_ln_003  label="_C_0805_2012Metric_f01b138523b003"
  LinkPlacement = pos=(79.65,41.45,0) rot=(0,0,1;0rad)
  LinkedObject = -> Shape227
  Placement = pos=(79.65,41.45,0) rot=(0,0,1;0rad)
FEATURE [App::Link] _C_0805_2012Metric_42e76acedcba_ln_004  label="_C_0805_2012Metric_e36e869397a001"
  LinkPlacement = pos=(113.565,44.65,0) rot=(0,0,-1;1.5708rad)
  LinkedObject = -> Shape227
  Placement = pos=(113.565,44.65,0) rot=(0,0,-1;1.5708rad)
FEATURE [App::Link] _C_0805_2012Metric_42e76acedcba_ln_005  label="_C_0805_2012Metric_15d6734f493a001"
  LinkPlacement = pos=(80.8,23.3,0) rot=(0,0,1;0rad)
  LinkedObject = -> Shape227
  Placement = pos=(80.8,23.3,0) rot=(0,0,1;0rad)
FEATURE [App::Link] _C_0805_2012Metric_42e76acedcba_ln_006  label="_C_0805_2012Metric_d7b806107520"
  LinkPlacement = pos=(157.546,20.066,0) rot=(0,0,1;0rad)
  LinkedObject = -> Shape227
  Placement = pos=(157.546,20.066,0) rot=(0,0,1;0rad)
FEATURE [App::Link] _C_0805_2012Metric_42e76acedcba_ln_007  label="_C_0805_2012Metric_e26014cc501c001"
  LinkPlacement = pos=(47.9,27.7,0) rot=(0,0,1;3.14159rad)
  LinkedObject = -> Shape227
  Placement = pos=(47.9,27.7,0) rot=(0,0,1;3.14159rad)
FEATURE [App::Link] _C_0805_2012Metric_42e76acedcba_ln_008  label="_C_0805_2012Metric_054ffed93a8c001"
  LinkPlacement = pos=(23.13,27.3,0) rot=(0,0,1;0rad)
  LinkedObject = -> Shape227
  Placement = pos=(23.13,27.3,0) rot=(0,0,1;0rad)
FEATURE [App::Link] _C_0805_2012Metric_42e76acedcba_ln_009  label="_C_0805_2012Metric_73571792734d001"
  LinkPlacement = pos=(157.5,17.9,0) rot=(0,0,1;3.14159rad)
  LinkedObject = -> Shape227
  Placement = pos=(157.5,17.9,0) rot=(0,0,1;3.14159rad)
FEATURE [App::Link] _C_0805_2012Metric_42e76acedcba_ln_010  label="_C_0805_2012Metric_242075c039d001"
  LinkPlacement = pos=(21.7,19.35,0) rot=(0,0,1;1.5708rad)
  LinkedObject = -> Shape227
  Placement = pos=(21.7,19.35,0) rot=(0,0,1;1.5708rad)
FEATURE [App::Link] _C_0805_2012Metric_42e76acedcba_ln_011  label="_C_0805_2012Metric_2b5fb2c51daf001"
  LinkPlacement = pos=(11.05,48.5,0) rot=(0,0,1;1.5708rad)
  LinkedObject = -> Shape227
  Placement = pos=(11.05,48.5,0) rot=(0,0,1;1.5708rad)
FEATURE [App::Link] _C_0805_2012Metric_42e76acedcba_ln_012  label="C_1.0uF_0805_20%_C_0805_2012Metric_4c26ca62740a"
  LinkPlacement = pos=(12.3,15.2,0) rot=(0,0,1;0rad)
  LinkedObject = -> Shape227
  Placement = pos=(12.3,15.2,0) rot=(0,0,1;0rad)
FEATURE [App::Link] _C_0805_2012Metric_42e76acedcba_ln_013  label="_C_0805_2012Metric_4b5c9fa2ab9d001"
  LinkPlacement = pos=(33.7,12.7,0) rot=(0,0,1;1.5708rad)
  LinkedObject = -> Shape227
  Placement = pos=(33.7,12.7,0) rot=(0,0,1;1.5708rad)
FEATURE [App::Link] _C_0805_2012Metric_42e76acedcba_ln_014  label="_C_0805_2012Metric_9c817947d75a001"
  LinkPlacement = pos=(39.2,12.7284,0) rot=(0,0,1;1.5708rad)
  LinkedObject = -> Shape227
  Placement = pos=(39.2,12.7284,0) rot=(0,0,1;1.5708rad)
FEATURE [App::Link] _D_SMA_147b90238018_ln_003  label="_D_SMA_aa7ecee8d937"
  LinkPlacement = pos=(7.9,-1.5,0) rot=(0,0,1;3.14159rad)
  LinkedObject = -> Shape241
  Placement = pos=(7.9,-1.5,0) rot=(0,0,1;3.14159rad)
FEATURE [App::Link] _D_SMA_147b90238018_ln_004  label="_D_SMA_c2646ced11f004"
  LinkPlacement = pos=(18.95,-1.6,0) rot=(0,0,1;3.14159rad)
  LinkedObject = -> Shape241
  Placement = pos=(18.95,-1.6,0) rot=(0,0,1;3.14159rad)
FEATURE [App::Link] _D_SOD_123_5a20a041a245_ln_005  label="_D_SOD_123_9f952dc980be001"
  LinkPlacement = pos=(48.7,38,0) rot=(0,0,1;3.14159rad)
  LinkedObject = -> Shape232
  Placement = pos=(48.7,38,0) rot=(0,0,1;3.14159rad)
FEATURE [App::Link] _D_SOD_123_5a20a041a245_ln_006  label="_D_SOD_123_c8b4b2da39fe001"
  LinkPlacement = pos=(48.6,30.2,0) rot=(0,0,1;3.14159rad)
  LinkedObject = -> Shape232
  Placement = pos=(48.6,30.2,0) rot=(0,0,1;3.14159rad)
FEATURE [App::Link] _D_SOD_123_5a20a041a245_ln_007  label="_D_SOD_123_5a5f85ca8e2f001"
  LinkPlacement = pos=(48.7,35.4,0) rot=(0,0,1;0rad)
  LinkedObject = -> Shape232
  Placement = pos=(48.7,35.4,0) rot=(0,0,1;0rad)
FEATURE [App::Link] _D_SOD_123_5a20a041a245_ln_008  label="_D_SOD_123_161a8bc13197"
  LinkPlacement = pos=(48.65,32.85,0) rot=(0,0,1;3.14159rad)
  LinkedObject = -> Shape232
  Placement = pos=(48.65,32.85,0) rot=(0,0,1;3.14159rad)
FEATURE [App::Link] _D_SOD_123_5a20a041a245_ln_009  label="_D_SOD_123_81fc6af181e010"
  LinkPlacement = pos=(48.6,25.1,0) rot=(0,0,1;0rad)
  LinkedObject = -> Shape232
  Placement = pos=(48.6,25.1,0) rot=(0,0,1;0rad)
FEATURE [App::Link] _Fan_Pin_Header_Straight_1x04_37f54f52d17d_ln_  label="_Fan_Pin_Header_Straight_1x04_832d3213614c"
  LinkPlacement = pos=(6.7,4.5,0) rot=(0,0,1;0rad)
  LinkedObject = -> Shape237
  Placement = pos=(6.7,4.5,0) rot=(0,0,1;0rad)
FEATURE [App::Link] _LED_0805_2012Metric_630bc1ac9416_ln_003  label="_LED_0805_2012Metric_080489ce25e005"
  LinkPlacement = pos=(66.975,18.4,0) rot=(0,0,1;0rad)
  LinkedObject = -> Shape239
  Placement = pos=(66.975,18.4,0) rot=(0,0,1;0rad)
FEATURE [App::Link] _LED_0805_2012Metric_630bc1ac9416_ln_004  label="_LED_0805_2012Metric_31b94944d83b001"
  LinkPlacement = pos=(40.2,3.39998,0) rot=(0,0,1;3.14159rad)
  LinkedObject = -> Shape239
  Placement = pos=(40.2,3.39998,0) rot=(0,0,1;3.14159rad)
FEATURE [App::Link] _LED_0805_2012Metric_630bc1ac9416_ln_005  label="_LED_0805_2012Metric_8e83bb0bb171"
  LinkPlacement = pos=(50.5,49.8,0) rot=(0,0,1;0rad)
  LinkedObject = -> Shape239
  Placement = pos=(50.5,49.8,0) rot=(0,0,1;0rad)
FEATURE [App::Link] _L_1210_3225Metric_8f5c69fc0355_ln_002  label="_L_1210_3225Metric_c8d3be7f3658"
  LinkPlacement = pos=(60.6,25.3,0) rot=(0,0,1;3.14159rad)
  LinkedObject = -> Shape243
  Placement = pos=(60.6,25.3,0) rot=(0,0,1;3.14159rad)
FEATURE [App::Link] _L_1210_3225Metric_8f5c69fc0355_ln_003  label="_L_1210_3225Metric_d7bc27af3adb001"
  LinkPlacement = pos=(46.8,11.3,0) rot=(0,0,1;1.5708rad)
  LinkedObject = -> Shape243
  Placement = pos=(46.8,11.3,0) rot=(0,0,1;1.5708rad)
FEATURE [App::Link] _MCV_01x02_G_3_81mm_8d2d7ae2d0cf_ln_001  label="_MCV_01x02_G_3_81mm_e9d5bdd79c005"
  LinkPlacement = pos=(-6.5075,16.3625,0) rot=(0,0,1;1.5708rad)
  LinkedObject = -> Shape242
  Placement = pos=(-6.5075,16.3625,0) rot=(0,0,1;1.5708rad)
FEATURE [App::Link] _R_0805_2012Metric_900e5a3da9ce_ln_024  label="_R_0805_2012Metric_b23a23415ea6"
  LinkPlacement = pos=(129.55,1.45,0) rot=(0,0,-1;1.5708rad)
  LinkedObject = -> Shape228
  Placement = pos=(129.55,1.45,0) rot=(0,0,-1;1.5708rad)
FEATURE [App::Link] _R_0805_2012Metric_900e5a3da9ce_ln_025  label="_R_0805_2012Metric_2014fa35a193"
  LinkPlacement = pos=(159.1,52.25,0) rot=(0,0,-1;1.5708rad)
  LinkedObject = -> Shape228
  Placement = pos=(159.1,52.25,0) rot=(0,0,-1;1.5708rad)
FEATURE [App::Link] _R_0805_2012Metric_900e5a3da9ce_ln_026  label="_R_0805_2012Metric_42cabd404850"
  LinkPlacement = pos=(7.45,51.9,0) rot=(0,0,1;3.14159rad)
  LinkedObject = -> Shape228
  Placement = pos=(7.45,51.9,0) rot=(0,0,1;3.14159rad)
FEATURE [App::Link] _R_0805_2012Metric_900e5a3da9ce_ln_027  label="_R_0805_2012Metric_139ca9693519"
  LinkPlacement = pos=(26.5,11.2,0) rot=(0,0,1;3.14159rad)
  LinkedObject = -> Shape228
  Placement = pos=(26.5,11.2,0) rot=(0,0,1;3.14159rad)
FEATURE [App::Link] _R_0805_2012Metric_900e5a3da9ce_ln_028  label="_R_0805_2012Metric_5ec229621a058"
  LinkPlacement = pos=(66.9875,16.2,0) rot=(0,0,1;0rad)
  LinkedObject = -> Shape228
  Placement = pos=(66.9875,16.2,0) rot=(0,0,1;0rad)
FEATURE [App::Link] _R_0805_2012Metric_900e5a3da9ce_ln_029  label="R_1.0kΩ_0805_1%_R_0805_2012Metric_8f984b32a8e5"
  LinkPlacement = pos=(12.3,17.25,0) rot=(0,0,1;3.14159rad)
  LinkedObject = -> Shape228
  Placement = pos=(12.3,17.25,0) rot=(0,0,1;3.14159rad)
FEATURE [App::Link] _R_0805_2012Metric_900e5a3da9ce_ln_030  label="_R_0805_2012Metric_e9d7ee01f873"
  LinkPlacement = pos=(24.8,20.9,0) rot=(0,0,1;3.14159rad)
  LinkedObject = -> Shape228
  Placement = pos=(24.8,20.9,0) rot=(0,0,1;3.14159rad)
FEATURE [App::Link] _R_0805_2012Metric_900e5a3da9ce_ln_031  label="_R_0805_2012Metric_28d6e0cd51a003"
  LinkPlacement = pos=(80.5,32.7,0) rot=(0,0,1;3.14159rad)
  LinkedObject = -> Shape228
  Placement = pos=(80.5,32.7,0) rot=(0,0,1;3.14159rad)
FEATURE [App::Link] _R_0805_2012Metric_900e5a3da9ce_ln_032  label="_R_0805_2012Metric_3ba9a919e954"
  LinkPlacement = pos=(12.85,12.05,0) rot=(0,0,1;3.14159rad)
  LinkedObject = -> Shape228
  Placement = pos=(12.85,12.05,0) rot=(0,0,1;3.14159rad)
FEATURE [App::Link] _R_0805_2012Metric_900e5a3da9ce_ln_033  label="_R_0805_2012Metric_41ce170047ef"
  LinkPlacement = pos=(12.85,9.95,0) rot=(0,0,1;3.14159rad)
  LinkedObject = -> Shape228
  Placement = pos=(12.85,9.95,0) rot=(0,0,1;3.14159rad)
FEATURE [App::Link] _R_0805_2012Metric_900e5a3da9ce_ln_034  label="_R_0805_2012Metric_bb24aad5734d001"
  LinkPlacement = pos=(29.6,19.1,0) rot=(0,0,-1;1.5708rad)
  LinkedObject = -> Shape228
  Placement = pos=(29.6,19.1,0) rot=(0,0,-1;1.5708rad)
FEATURE [App::Link] _R_0805_2012Metric_900e5a3da9ce_ln_035  label="_R_0805_2012Metric_78da282b717f"
  LinkPlacement = pos=(15.8,31.9,0) rot=(0,0,1;3.14159rad)
  LinkedObject = -> Shape228
  Placement = pos=(15.8,31.9,0) rot=(0,0,1;3.14159rad)
FEATURE [App::Link] _R_0805_2012Metric_900e5a3da9ce_ln_036  label="_R_0805_2012Metric_ea6fdd8e8747"
  LinkPlacement = pos=(72.8,33.8,0) rot=(0,0,1;0rad)
  LinkedObject = -> Shape228
  Placement = pos=(72.8,33.8,0) rot=(0,0,1;0rad)
FEATURE [App::Link] _R_0805_2012Metric_900e5a3da9ce_ln_037  label="_R_0805_2012Metric_272588301ff010"
  LinkPlacement = pos=(43.8,3.4,0) rot=(0,0,1;0rad)
  LinkedObject = -> Shape228
  Placement = pos=(43.8,3.4,0) rot=(0,0,1;0rad)
FEATURE [App::Link] _R_0805_2012Metric_900e5a3da9ce_ln_038  label="R_39.0kΩ_0805_1%_R_0805_2012Metric_628042a7d0a7"
  LinkPlacement = pos=(5.15,18.5,0) rot=(0,0,1;0rad)
  LinkedObject = -> Shape228
  Placement = pos=(5.15,18.5,0) rot=(0,0,1;0rad)
FEATURE [App::Link] _R_0805_2012Metric_900e5a3da9ce_ln_039  label="R_3.3kΩ_0805_1%_R_0805_2012Metric_0484aec14b50"
  LinkPlacement = pos=(5.15,16.4,0) rot=(0,0,1;3.14159rad)
  LinkedObject = -> Shape228
  Placement = pos=(5.15,16.4,0) rot=(0,0,1;3.14159rad)
FEATURE [App::Link] _R_0805_2012Metric_900e5a3da9ce_ln_040  label="R_3.3kΩ_0805_1%_R_0805_2012Metric_c63e75e59e90"
  LinkPlacement = pos=(8.75,17.25,0) rot=(0,0,1;0rad)
  LinkedObject = -> Shape228
  Placement = pos=(8.75,17.25,0) rot=(0,0,1;0rad)
FEATURE [App::Link] _R_0805_2012Metric_900e5a3da9ce_ln_041  label="_R_0805_2012Metric_0dd0370ec1da001"
  LinkPlacement = pos=(29.6,14.6284,0) rot=(0,0,-1;1.5708rad)
  LinkedObject = -> Shape228
  Placement = pos=(29.6,14.6284,0) rot=(0,0,-1;1.5708rad)
FEATURE [App::Link] _R_0805_2012Metric_900e5a3da9ce_ln_042  label="_R_0805_2012Metric_84be3173d966"
  LinkPlacement = pos=(26.5625,44.4,0) rot=(0,0,1;3.14159rad)
  LinkedObject = -> Shape228
  Placement = pos=(26.5625,44.4,0) rot=(0,0,1;3.14159rad)
FEATURE [App::Link] _R_0805_2012Metric_900e5a3da9ce_ln_043  label="_R_0805_2012Metric_d9bee0a38b067"
  LinkPlacement = pos=(80.6,38,0) rot=(0,0,1;3.14159rad)
  LinkedObject = -> Shape228
  Placement = pos=(80.6,38,0) rot=(0,0,1;3.14159rad)
FEATURE [App::Link] _R_0805_2012Metric_900e5a3da9ce_ln_044  label="_R_0805_2012Metric_9433e919f4f6"
  LinkPlacement = pos=(152.6,7.4,0) rot=(0,0,1;0rad)
  LinkedObject = -> Shape228
  Placement = pos=(152.6,7.4,0) rot=(0,0,1;0rad)
FEATURE [App::Link] _R_0805_2012Metric_900e5a3da9ce_ln_045  label="_R_0805_2012Metric_603a57e1dcd6"
  LinkPlacement = pos=(146.95,4.25,0) rot=(0,0,1;0rad)
  LinkedObject = -> Shape228
  Placement = pos=(146.95,4.25,0) rot=(0,0,1;0rad)
FEATURE [App::Link] _R_0805_2012Metric_900e5a3da9ce_ln_046  label="_R_0805_2012Metric_a6c8c79ee0cd001"
  LinkPlacement = pos=(31.7,15.8284,0) rot=(0,0,1;1.5708rad)
  LinkedObject = -> Shape228
  Placement = pos=(31.7,15.8284,0) rot=(0,0,1;1.5708rad)
FEATURE [App::Link] _R_0805_2012Metric_900e5a3da9ce_ln_047  label="_R_0805_2012Metric_fd329559c190"
  LinkPlacement = pos=(153.95,15.5,0) rot=(0,0,-1;1.5708rad)
  LinkedObject = -> Shape228
  Placement = pos=(153.95,15.5,0) rot=(0,0,-1;1.5708rad)
FEATURE [App::Link] _R_0805_2012Metric_900e5a3da9ce_ln_048  label="_R_0805_2012Metric_d37356ee9a082"
  LinkPlacement = pos=(0.75,46,0) rot=(0,0,-1;1.5708rad)
  LinkedObject = -> Shape228
  Placement = pos=(0.75,46,0) rot=(0,0,-1;1.5708rad)
FEATURE [App::Link] _R_0805_2012Metric_900e5a3da9ce_ln_049  label="_R_0805_2012Metric_3d5ced576c1b001"
  LinkPlacement = pos=(24,9.2,0) rot=(0,0,1;0rad)
  LinkedObject = -> Shape228
  Placement = pos=(24,9.2,0) rot=(0,0,1;0rad)
FEATURE [App::Link] _R_0805_2012Metric_900e5a3da9ce_ln_050  label="_R_0805_2012Metric_33922ef02623"
  LinkPlacement = pos=(46.8,49.8,0) rot=(0,0,1;3.14159rad)
  LinkedObject = -> Shape228
  Placement = pos=(46.8,49.8,0) rot=(0,0,1;3.14159rad)
FEATURE [App::Link] _R_0805_2012Metric_900e5a3da9ce_ln_051  label="_R_0805_2012Metric_3e123011b477"
  LinkPlacement = pos=(155.7,52.25,0) rot=(0,0,-1;1.5708rad)
  LinkedObject = -> Shape228
  Placement = pos=(155.7,52.25,0) rot=(0,0,-1;1.5708rad)
FEATURE [App::Link] _R_0805_2012Metric_900e5a3da9ce_ln_052  label="_R_0805_2012Metric_b54dcca9e39f001"
  LinkPlacement = pos=(71,37.5,0) rot=(0,0,1;0rad)
  LinkedObject = -> Shape228
  Placement = pos=(71,37.5,0) rot=(0,0,1;0rad)
FEATURE [App::Link] _R_0805_2012Metric_900e5a3da9ce_ln_053  label="_R_0805_2012Metric_596a6c57280b001"
  LinkPlacement = pos=(153.95,11.7,0) rot=(0,0,-1;1.5708rad)
  LinkedObject = -> Shape228
  Placement = pos=(153.95,11.7,0) rot=(0,0,-1;1.5708rad)
FEATURE [App::Link] _SOT_223_9813f15a1230_ln_002  label="_SOT_223_6d2a4fb53032"
  LinkPlacement = pos=(85.55,44.6,0) rot=(0,0,-1;1.5708rad)
  LinkedObject = -> Shape249
  Placement = pos=(85.55,44.6,0) rot=(0,0,-1;1.5708rad)
FEATURE [App::Link] _SOT_223_9813f15a1230_ln_003  label="_SOT_223_0a21e31ed99f001"
  LinkPlacement = pos=(25.45,50.95,0) rot=(0,0,1;1.5708rad)
  LinkedObject = -> Shape249
  Placement = pos=(25.45,50.95,0) rot=(0,0,1;1.5708rad)
FEATURE [App::Link] _SOT_323_SC_70_c919c89d7c35_ln_001  label="_SOT_323_SC_70_a02c5a9bee035"
  LinkPlacement = pos=(74.8,37,0) rot=(0,0,1;3.14159rad)
  LinkedObject = -> Shape238
  Placement = pos=(74.8,37,0) rot=(0,0,1;3.14159rad)
FEATURE [App::Link] _SOT_323_SC_70_c919c89d7c35_ln_002  label="_SOT_323_SC_70_de0dfd710b9e"
  LinkPlacement = pos=(151.85,3.2,0) rot=(0,0,-1;1.5708rad)
  LinkedObject = -> Shape238
  Placement = pos=(151.85,3.2,0) rot=(0,0,-1;1.5708rad)
FEATURE [App::Link] _TestPoint_Loop_D2_54mm_Drill1_5mm_Beaded_cp002_8f60d36f4fd8_ln_003  label="_TestPoint_Loop_D2_54mm_Drill1_5mm_Beaded_cp002_0b7b98566b059"
  LinkPlacement = pos=(42.1,-1.80002,0) rot=(0,0,1;0rad)
  LinkedObject = -> TestPoint_Loop_D2_54mm_Drill1_5mm_Beaded_cp004
  Placement = pos=(42.1,-1.80002,0) rot=(0,0,1;0rad)
FEATURE [App::Link] _TestPoint_Loop_D2_54mm_Drill1_5mm_Beaded_cp002_8f60d36f4fd8_ln_004  label="_TestPoint_Loop_D2_54mm_Drill1_5mm_Beaded_cp002_9e1e075e0d1f001"
  LinkPlacement = pos=(42.6,49.1,0) rot=(0,0,1;0rad)
  LinkedObject = -> TestPoint_Loop_D2_54mm_Drill1_5mm_Beaded_cp004
  Placement = pos=(42.6,49.1,0) rot=(0,0,1;0rad)
FEATURE [App::Link] _TestPoint_Loop_D2_54mm_Drill1_5mm_Beaded_cp002_8f60d36f4fd8_ln_005  label="_TestPoint_Loop_D2_54mm_Drill1_5mm_Beaded_cp002_4444e0770bde001"
  LinkPlacement = pos=(43.2,14.6,0) rot=(0,0,1;0rad)
  LinkedObject = -> TestPoint_Loop_D2_54mm_Drill1_5mm_Beaded_cp004
  Placement = pos=(43.2,14.6,0) rot=(0,0,1;0rad)
FEATURE [App::Link] __PinHeader_1x02_P254mm_Vertical_3b80083b2130_ln_005  label="1_PinHeader_1x02_P254mm_Vertical_d66317177e01"
  LinkPlacement = pos=(123.85,2.45,0) rot=(0,0,1;3.14159rad)
  LinkedObject = -> Shape240
  Placement = pos=(123.85,2.45,0) rot=(0,0,1;3.14159rad)
FEATURE [App::Link] __PinHeader_1x02_P254mm_Vertical_3b80083b2130_ln_006  label="1_PinHeader_1x02_P254mm_Vertical_0283ff2d24c009"
  LinkPlacement = pos=(-7.5,37.65,0) rot=(0,0,-1;1.5708rad)
  LinkedObject = -> Shape240
  Placement = pos=(-7.5,37.65,0) rot=(0,0,-1;1.5708rad)
FEATURE [App::Link] __PinHeader_1x02_P254mm_Vertical_3b80083b2130_ln_007  label="1_PinHeader_1x02_P254mm_Vertical_806d60fd696a001"
  LinkPlacement = pos=(67.7,25.2,0) rot=(0,0,1;0rad)
  LinkedObject = -> Shape240
  Placement = pos=(67.7,25.2,0) rot=(0,0,1;0rad)
FEATURE [App::Link] __PinHeader_1x02_P254mm_Vertical_3b80083b2130_ln_008  label="1_PinHeader_1x02_P254mm_Vertical_0c23ef1a54e007"
  LinkPlacement = pos=(47.5,4.29998,0) rot=(0,0,1;1.5708rad)
  LinkedObject = -> Shape240
  Placement = pos=(47.5,4.29998,0) rot=(0,0,1;1.5708rad)
FEATURE [App::Link] __PinHeader_1x02_P254mm_Vertical_3b80083b2130_ln_009  label="1_PinHeader_1x02_P254mm_Vertical_963a12bb0eb9"
  LinkPlacement = pos=(14.875,27.5,0) rot=(0,0,1;1.5708rad)
  LinkedObject = -> Shape240
  Placement = pos=(14.875,27.5,0) rot=(0,0,1;1.5708rad)
FEATURE [App::Link] __PinHeader_1x02_P254mm_Vertical_3b80083b2130_ln_010  label="1_PinHeader_1x02_P254mm_Vertical_b2b0b4eb230f001"
  LinkPlacement = pos=(55.95,49.725,0) rot=(0,0,1;1.5708rad)
  LinkedObject = -> Shape240
  Placement = pos=(55.95,49.725,0) rot=(0,0,1;1.5708rad)
FEATURE [App::Link] __PinHeader_1x03_P254mm_Vertical_a2001c85ec40_ln_  label="1_PinHeader_1x03_P254mm_Vertical_21ad5ec019db"
  LinkPlacement = pos=(10.98,31.45,0) rot=(0,0,-1;1.5708rad)
  LinkedObject = -> Shape231
  Placement = pos=(10.98,31.45,0) rot=(0,0,-1;1.5708rad)
FEATURE [App::Link] __PinHeader_1x03_P254mm_Vertical_a2001c85ec40_ln_001  label="1_PinHeader_1x03_P254mm_Vertical_acc2c4d0fc84"
  LinkPlacement = pos=(30.25,5.94,0) rot=(0,0,1;0rad)
  LinkedObject = -> Shape231
  Placement = pos=(30.25,5.94,0) rot=(0,0,1;0rad)
FEATURE [App::Link] __PinHeader_1x03_P254mm_Vertical_a2001c85ec40_ln_002  label="1_PinHeader_1x03_P254mm_Vertical_eb1130131e42"
  LinkPlacement = pos=(96.62,29.1,0) rot=(0,0,-1;1.5708rad)
  LinkedObject = -> Shape231
  Placement = pos=(96.62,29.1,0) rot=(0,0,-1;1.5708rad)
FEATURE [App::Link] __PinHeader_1x03_P254mm_Vertical_a2001c85ec40_ln_003  label="1_PinHeader_1x03_P254mm_Vertical_8bdf9c2084e1"
  LinkPlacement = pos=(4.25,21.46,0) rot=(0,0,1;3.14159rad)
  LinkedObject = -> Shape231
  Placement = pos=(4.25,21.46,0) rot=(0,0,1;3.14159rad)
FEATURE [App::Link] __PinHeader_2x08_P254mm_Vertical_411dce5b0f97_ln_  label="1_PinHeader_2x08_P254mm_Vertical_a805aa90854e"
  LinkPlacement = pos=(57.075,-13.55,-1.592) rot=(0.707107,0.707107,0;3.14159rad)
  LinkedObject = -> Shape245
  Placement = pos=(57.075,-13.55,-1.592) rot=(0.707107,0.707107,0;3.14159rad)
FEATURE [App::Part] Bot_f042  label="Bot_f043"
  Group = -> [__PinHeader_2x08_P254mm_Vertical_411dce5b0f97_ln_]
  Origin = -> Origin136
FEATURE [App::Part] _e9c6de3_9c39_11ed_93f0_dde97e994e83  label="9e9c6de3-9c39-11ed-93f0-dde97e994e83"
  Group = -> [Part__Feature566]
  Origin = -> Origin138
FEATURE [App::Part] _e9c6de4_9c39_11ed_93f0_dde97e994e83  label="9e9c6de4-9c39-11ed-93f0-dde97e994e83"
  Group = -> [Part__Feature567]
  Origin = -> Origin139
FEATURE [App::Part] _e9c6de5_9c39_11ed_93f0_dde97e994e83_part  label="9e9c6de5-9c39-11ed-93f0-dde97e994e83_part005"
  Group = -> [Part__Feature568,Part__Feature569,Part__Feature570,Part__Feature571,Part__Feature572]
  Origin = -> Origin140
FEATURE [App::Part] _e9c6de5_9c39_11ed_93f0_dde97e994e83  label="9e9c6de5-9c39-11ed-93f0-dde97e994e83"
  Group = -> [_e9c6de5_9c39_11ed_93f0_dde97e994e83_part]
  Origin = -> Origin141
FEATURE [App::Part] _e9c6de2_9c39_11ed_93f0_dde97e994e83  label="9e9c6de2-9c39-11ed-93f0-dde97e994e83"
  Group = -> [_e9c6de3_9c39_11ed_93f0_dde97e994e83,_e9c6de4_9c39_11ed_93f0_dde97e994e83,_e9c6de5_9c39_11ed_93f0_dde97e994e83]
  Origin = -> Origin142
FEATURE [App::Part] CQ_assembly003  label="_CQ assembly_655a98f768af"
  Group = -> [_e9c6de2_9c39_11ed_93f0_dde97e994e83]
  Origin = -> Origin143
  Placement = pos=(13.3,21.89,0) rot=(0,0,1;0rad)
FEATURE [App::Part] Top_f042  label="Top_f043"
  Group = -> [Shape227,Shape228,Shape229,Shape230,_R_0805_2012Metric_900e5a3da9ce_ln_024,_R_0805_2012Metric_900e5a3da9ce_ln_025,Shape231,_CP_Elec_5x58_0ee41fe4bfd3_ln_,Shape232,_C_0805_2012Metric_42e76acedcba_ln_,_D_SOD_123_5a20a041a245_ln_005,_CP_Elec_5x58_0ee41fe4bfd3_ln_001,_C_0805_2012Metric_42e76acedcba_ln_001,Shape233,__PinHeader_1x03_P254mm_Vertical_a2001c85ec40_ln_,+108 more]
  Origin = -> Origin135
FEATURE [App::Part] Step_Models_f042  label="Step_Models_f043"
  Group = -> [Top_f042,Bot_f042]
  Origin = -> Origin134
FEATURE [App::Part] Board_f042  label="EL-Load-Power-MCU001"
  Group = -> [Local_CS_f042,Board_Geoms_f042,Step_Models_f042]
  Origin = -> Origin133
  Placement = pos=(191.67,76.67,14.5) rot=(0,0,1;3.14159rad)
FEATURE [Sketcher::SketchObject] Sketch033
  ArcFitTolerance = 1e-06
  AttachmentSupport = -> [Pocket013]
  ExternalGeometry = -> [Pocket013]
  FullyConstrained = true
  MakeInternals = false
  MapMode = 5
  Placement = pos=(0,0,16.25) rot=(0,0,1;0rad)
  sketch-geometry (1):
    g0: Circle CenterX=51.67 CenterY=74.25 CenterZ=0 NormalX=0 NormalY=0 NormalZ=1 AngleXU=0 Radius=3
  constraints (3):
    c: Vertical(g0,g-3)
    c: DistanceY(g0) = 74.25
    c: Radius(g0) = 3
FEATURE [PartDesign::Pocket] Pocket014
  BaseFeature = -> Pocket013
  Direction = (0,0,-1)
  Length = 5
  Length2 = 5
  Profile = -> Sketch033
  ReferenceAxis = -> Sketch033 [N_Axis]
  Suppressed = false
  Type = 0
FEATURE [PartDesign::Body] Body001  label="PCBFrame1"
  AllowCompound = false
  Group = -> [Sketch,Pad001,Sketch001,Pad002,Sketch002,Pocket,Sketch003,Pad003,Sketch004,Pocket001,Sketch008,Pocket002,Sketch031,Pad017,Sketch032,Pocket013,Sketch033,Pocket014]
  Origin = -> Origin068
  Placement = pos=(0,0,-3.4) rot=(0,0,1;0rad)
  Tip = -> Pocket014
FEATURE [PartDesign::Plane] DatumPlane
  AttachmentSupport = -> [Pocket011]
  Length = 235.491
  MapMode = 2
  Placement = pos=(222.8,89.4,20) rot=(0.57735,0.57735,0.57735;2.0944rad)
  ResizeMode = 0
  Width = 103.591
FEATURE [Sketcher::SketchObject] Sketch034
  ArcFitTolerance = 1e-06
  AttachmentSupport = -> [DatumPlane]
  ExternalGeometry = -> [Sketch028]
  FullyConstrained = true
  MakeInternals = false
  MapMode = 5
  Placement = pos=(222.8,89.4,20) rot=(0.57735,0.57735,0.57735;2.0944rad)
  sketch-geometry (7):
    g0: ArcOfCircle CenterX=-58.15 CenterY=15 CenterZ=0 NormalX=0 NormalY=0 NormalZ=1 AngleXU=0 Radius=5.5 StartAngle=1.5708 EndAngle=4.71239
    g1: ArcOfCircle CenterX=-38.15 CenterY=15 CenterZ=0 NormalX=0 NormalY=0 NormalZ=1 AngleXU=0 Radius=5.5 StartAngle=4.71239 EndAngle=7.85398
    g2: LineSegment StartX=-58.15 StartY=20.5 StartZ=0 EndX=-38.15 EndY=20.5 EndZ=0
    g3: LineSegment StartX=-58.15 StartY=9.5 StartZ=0 EndX=-38.15 EndY=9.5 EndZ=0
    g4: LineSegment [constr] StartX=-58.15 StartY=15 StartZ=0 EndX=-38.15 EndY=15 EndZ=0
    g5: LineSegment [constr] StartX=-58.15 StartY=15 StartZ=0 EndX=-51.9 EndY=17 EndZ=0
    g6: LineSegment [constr] StartX=-44.4 StartY=13 StartZ=0 EndX=-38.15 EndY=15 EndZ=0
  constraints (15):
    c: Tangent(g0,g2) = 1.5708
    c: Tangent(g0,g3) = -1.5708
    c: Tangent(g1,g2) = 1.5708
    c: Tangent(g1,g3) = -1.5708
    c: Equal(g0,g1)
    c: Distance(g0,g1) = 20
    c: Radius(g0) = 5.5
    c: Coincident(g4,g0)
    c: Coincident(g4,g1)
    c: Symmetric(g-3,g-4,g4)
    c: Coincident(g5,g0)
    c: Coincident(g5,g-3)
    c: Coincident(g6,g-4)
    c: Coincident(g6,g1)
    c: Equal(g6,g5)
FEATURE [PartDesign::Pocket] Pocket015
  BaseFeature = -> Pocket011
  Direction = (-1,0,0)
  Length = 1
  Length2 = 5
  Placement = pos=(222.8,89.4,20) rot=(0.57735,0.57735,0.57735;2.0944rad)
  Profile = -> Sketch034
  ReferenceAxis = -> Sketch034 [N_Axis]
  Reversed = true
  Suppressed = false
  Type = 0
FEATURE [Sketcher::SketchObject] Sketch035
  ArcFitTolerance = 1e-06
  AttachmentOffset = pos=(0,0,-17) rot=(0,0,1;0rad)
  AttachmentSupport = -> [XZ_Plane124]
  ExternalGeometry = -> [Pocket015]
  FullyConstrained = true
  MakeInternals = false
  MapMode = 5
  Placement = pos=(0,17,-3.8e-15) rot=(1,0,0;1.5708rad)
  sketch-geometry (8):
    g0: LineSegment StartX=222.8 StartY=29.5 StartZ=0 EndX=222.8 EndY=21.5 EndZ=0
    g1: LineSegment StartX=222.8 StartY=29.5 StartZ=0 EndX=218.8 EndY=29.5 EndZ=0
    g2: LineSegment StartX=218.8 StartY=29.5 StartZ=0 EndX=218.8 EndY=21.5 EndZ=0
    g3: LineSegment StartX=222.8 StartY=21.5 StartZ=0 EndX=218.8 EndY=21.5 EndZ=0
    g4: LineSegment StartX=222.8 StartY=40.5 StartZ=0 EndX=222.8 EndY=48.5 EndZ=0
    g5: LineSegment StartX=222.8 StartY=48.5 StartZ=0 EndX=218.8 EndY=48.5 EndZ=0
    g6: LineSegment StartX=218.8 StartY=48.5 StartZ=0 EndX=218.8 EndY=40.5 EndZ=0
    g7: LineSegment StartX=218.8 StartY=40.5 StartZ=0 EndX=222.8 EndY=40.5 EndZ=0
  constraints (22):
    c: Vertical(g0)
    c: Horizontal(g1)
    c: Coincident(g2,g1)
    c: Vertical(g2)
    c: Coincident(g3,g0)
    c: Coincident(g3,g2)
    c: Horizontal(g3)
    c: Coincident(g1,g0)
    c: Coincident(g4,g5)
    c: Coincident(g5,g6)
    c: Coincident(g6,g7)
    c: Coincident(g7,g4)
    c: Vertical(g4)
    c: Vertical(g6)
    c: Horizontal(g5)
    c: Horizontal(g7)
    c: Vertical(g1,g6)
    c: Coincident(g4,g-4)
    c: Coincident(g0,g-3)
    c: DistanceX(g5,g5) = 4
    c: DistanceY(g6,g6) = 8
    c: Equal(g6,g2)
FEATURE [PartDesign::Pad] Pad018
  BaseFeature = -> Pocket015
  Direction = (0,-1,2e-16)
  Length = 46
  Length2 = 10
  Placement = pos=(222.8,89.4,20) rot=(0.57735,0.57735,0.57735;2.0944rad)
  Profile = -> Sketch035
  ReferenceAxis = -> Sketch035 [N_Axis]
  Reversed = true
  Suppressed = false
  Type = 0
FEATURE [Sketcher::SketchObject] Sketch036
  ArcFitTolerance = 1e-06
  AttachmentSupport = -> [Pad018]
  ExternalGeometry = -> [Pad018]
  FullyConstrained = true
  MakeInternals = false
  MapMode = 5
  Placement = pos=(218.8,89.4,20) rot=(0.57735,0.57735,-0.57735;4.18879rad)
  sketch-geometry (10):
    g0: Circle CenterX=-39.4 CenterY=-24.5 CenterZ=0 NormalX=0 NormalY=0 NormalZ=1 AngleXU=0 Radius=1.45
    g1: Circle CenterX=-39.4 CenterY=-5.5 CenterZ=0 NormalX=0 NormalY=0 NormalZ=1 AngleXU=0 Radius=1.45
    g2: Circle CenterX=-59.4 CenterY=-5.5 CenterZ=0 NormalX=0 NormalY=0 NormalZ=1 AngleXU=0 Radius=1.45
    g3: Circle CenterX=-59.4 CenterY=-24.5 CenterZ=0 NormalX=0 NormalY=0 NormalZ=1 AngleXU=0 Radius=1.45
    g4: LineSegment [constr] StartX=-59.4 StartY=-5.5 StartZ=0 EndX=-59.4 EndY=-24.5 EndZ=0
    g5: LineSegment [constr] StartX=-59.4 StartY=-24.5 StartZ=0 EndX=-39.4 EndY=-24.5 EndZ=0
    g6: LineSegment [constr] StartX=-39.4 StartY=-24.5 StartZ=0 EndX=-39.4 EndY=-5.5 EndZ=0
    g7: LineSegment [constr] StartX=-39.4 StartY=-5.5 StartZ=0 EndX=-59.4 EndY=-5.5 EndZ=0
    g8: LineSegment [constr] StartX=-72.4 StartY=-1.5 StartZ=0 EndX=-59.4 EndY=-5.5 EndZ=0
    g9: LineSegment [constr] StartX=-39.4 StartY=-5.5 StartZ=0 EndX=-26.4 EndY=-1.5 EndZ=0
  constraints (22):
    c: Diameter(g0) = 2.9
    c: Coincident(g4,g5)
    c: Coincident(g5,g6)
    c: Coincident(g6,g7)
    c: Coincident(g7,g4)
    c: Vertical(g4)
    c: Vertical(g6)
    c: Coincident(g4,g2)
    c: Coincident(g5,g0)
    c: Coincident(g3,g4)
    c: Coincident(g6,g1)
    c: Equal(g0,g3)
    c: Equal(g3,g2)
    c: Equal(g2,g1)
    c: Symmetric(g-3,g-4,g7)
    c: Symmetric(g-5,g-6,g5)
    c: DistanceX(g7,g7) = 20
    c: Coincident(g8,g-4)
    c: Coincident(g9,g1)
    c: Coincident(g9,g-4)
    c: Equal(g8,g9)
    c: Coincident(g8,g2)
FEATURE [PartDesign::Pocket] Pocket016
  BaseFeature = -> Pad018
  Direction = (1,0,0)
  Length = 5
  Length2 = 5
  Placement = pos=(222.8,89.4,20) rot=(0.57735,0.57735,0.57735;2.0944rad)
  Profile = -> Sketch036
  ReferenceAxis = -> Sketch036 [N_Axis]
  Suppressed = false
  Type = 0
FEATURE [PartDesign::Body] Body005  label="EndPanel_Cutouts"
  AllowCompound = false
  Group = -> [Clone,Sketch028,Pocket011,DatumPlane,Sketch034,Pocket015,Sketch035,Pad018,Sketch036,Pocket016]
  Origin = -> Origin124
  Tip = -> Pocket016
FEATURE [Part::Compound] Compound  label="RearPanel"
  Links = -> [Body004,Body005]
FEATURE [PartDesign::SubShapeBinder] Binder004
  BindCopyOnChange = 0
  BindMode = 0
  ClaimChildren = false
  Fuse = false
  MakeFace = true
  OffsetFill = false
  OffsetIntersection = false
  OffsetJoinType = 0
  OffsetOpenResult = false
  PartialLoad = false
  Relative = true
  Support = -> [Body005[Pocket016.Face39]]
  _Version = 2
FEATURE [PartDesign::Plane] DatumPlane001
  AttachmentSupport = -> [Binder004]
  Length = 95.5602
  MapMode = 5
  Placement = pos=(218.8,4.81e-14,0) rot=(0.57735,-0.57735,-0.57735;2.0944rad)
  ResizeMode = 0
  Width = 90.0602
FEATURE [PartDesign::SubShapeBinder] Binder005
  BindCopyOnChange = 0
  BindMode = 0
  ClaimChildren = false
  Context = -> Body007 [Binder005.]
  Fuse = false
  MakeFace = true
  OffsetFill = false
  OffsetIntersection = false
  OffsetJoinType = 0
  OffsetOpenResult = false
  PartialLoad = false
  Relative = true
  Support = -> [Body005[Pocket016.Face38]]
  _Version = 2
FEATURE [Sketcher::SketchObject] Sketch037
  ArcFitTolerance = 1e-06
  AttachmentSupport = -> [DatumPlane001]
  ExternalGeometry = -> [Binder004,Binder005]
  FullyConstrained = true
  MakeInternals = false
  MapMode = 5
  Placement = pos=(218.8,4.81e-14,0) rot=(0.57735,-0.57735,-0.57735;2.0944rad)
  expr: Constraints[33] = .Constraints.dist1
  sketch-geometry (16):
    g0: ArcOfCircle CenterX=-52.5 CenterY=44.5 CenterZ=0 NormalX=0 NormalY=0 NormalZ=1 AngleXU=0 Radius=1.6 StartAngle=1.5708 EndAngle=4.71239
    g1: ArcOfCircle CenterX=-47.5 CenterY=44.5 CenterZ=0 NormalX=0 NormalY=0 NormalZ=1 AngleXU=0 Radius=1.6 StartAngle=4.71239 EndAngle=7.85398
    g2: LineSegment StartX=-52.5 StartY=46.1 StartZ=0 EndX=-47.5 EndY=46.1 EndZ=0
    g3: LineSegment StartX=-52.5 StartY=42.9 StartZ=0 EndX=-47.5 EndY=42.9 EndZ=0
    g4: ArcOfCircle CenterX=-52.5 CenterY=25.5 CenterZ=0 NormalX=0 NormalY=0 NormalZ=1 AngleXU=0 Radius=1.6 StartAngle=1.5708 EndAngle=4.71239
    g5: ArcOfCircle CenterX=-47.5 CenterY=25.5 CenterZ=0 NormalX=0 NormalY=0 NormalZ=1 AngleXU=0 Radius=1.6 StartAngle=4.71239 EndAngle=7.85398
    g6: LineSegment StartX=-52.5 StartY=27.1 StartZ=0 EndX=-47.5 EndY=27.1 EndZ=0
    g7: LineSegment StartX=-52.5 StartY=23.9 StartZ=0 EndX=-47.5 EndY=23.9 EndZ=0
    g8: ArcOfCircle CenterX=-50 CenterY=44.5 CenterZ=0 NormalX=0 NormalY=0 NormalZ=1 AngleXU=0 Radius=5.1 StartAngle=3.54115e-11 EndAngle=3.14159
    g9: ArcOfCircle CenterX=-50 CenterY=25.5 CenterZ=0 NormalX=0 NormalY=0 NormalZ=1 AngleXU=0 Radius=5.1 StartAngle=3.14159 EndAngle=6.28319
    g10: LineSegment StartX=-44.9 StartY=44.5 StartZ=0 EndX=-44.9 EndY=42 EndZ=0
    g11: LineSegment StartX=-55.1 StartY=44.5 StartZ=0 EndX=-55.1 EndY=25.5 EndZ=0
    g12: LineSegment [constr] StartX=-44.9 StartY=44.5 StartZ=0 EndX=-45.9 EndY=44.5 EndZ=0
    g13: ArcOfCircle CenterX=-42.6461 CenterY=35 CenterZ=0 NormalX=0 NormalY=0 NormalZ=1 AngleXU=0 Radius=7.35392 StartAngle=1.8823 EndAngle=4.40088
    g14: LineSegment [constr] StartX=-50 StartY=44.5 StartZ=0 EndX=-50 EndY=25.5 EndZ=0
    g15: LineSegment StartX=-44.9 StartY=28 StartZ=0 EndX=-44.9 EndY=25.5 EndZ=0
  constraints (39):
    c: Tangent(g0,g2) = 1.5708
    c: Tangent(g0,g3) = -1.5708
    c: Tangent(g1,g2) = 1.5708
    c: Tangent(g1,g3) = -1.5708
    c: Equal(g0,g1)
    c: Horizontal(g2)
    c: Symmetric(g0,g1,g-3)
    c: Diameter(g0) = 3.2
    c: Distance(g2) = 5
    c: Tangent(g4,g6) = 1.5708
    c: Tangent(g4,g7) = -1.5708
    c: Tangent(g5,g6) = 1.5708
    c: Tangent(g5,g7) = -1.5708
    c: Equal(g4,g5)
    c: Horizontal(g6)
    c: Symmetric(g5,g4,g-4)
    c: Equal(g4,g0)
    c: Equal(g6,g3)
    c: Tangent(g8,g10) = 1.5708
    c: Tangent(g8,g11) = -1.5708
    c: Tangent(g9,g11) = -1.5708
    c: Equal(g8,g9)
    c: Coincident(g8,g-3)
    c: Coincident(g9,g-4)
    c: Coincident(g12,g8)
    c: PointOnObject(g12,g1)
    c: Horizontal(g12)
    c: DistanceX(g12,g12) = 1
    c: PointOnObject(g13,g15)
    c: Coincident(g14,g8)
    c: Coincident(g14,g9)
    c: Tangent(g14,g13)
    c: DistanceY(g13,g8) = 2.5  'dist1'
    c: DistanceY(g9,g13) = 2.5
    c: Coincident(g10,g13)
    c: PointOnObject(g15,g13)
    c: Vertical(g15)
    c: Tangent(g9,g15) = 1.5708
    c: Vertical(g10)
FEATURE [PartDesign::Pad] Pad019
  Direction = (-1,0,0)
  Length = 5
  Length2 = 10
  Placement = pos=(218.8,0,2.43e-14) rot=(0.57735,-0.57735,-0.57735;2.0944rad)
  Profile = -> Sketch037
  ReferenceAxis = -> Sketch037 [N_Axis]
  Suppressed = false
  Type = 0
FEATURE [PartDesign::Body] Body007  label="USB clip"
  AllowCompound = false
  Group = -> [Binder004,DatumPlane001,Sketch037,Binder005,Pad019]
  Origin = -> Origin145
  Tip = -> Pad019
FEATURE [Part::Feature] Body008  label="USB clip001"
  Placement = pos=(0,78.1,70.4) rot=(1,0,0;3.14159rad)
  shape: bbox 5 x 10.2 x 29.2 mm, 16 faces (baked)
FEATURE [Mesh::Feature] Encoder_small  label="Encoder-small"
  Placement = pos=(-4.1,93.6,34.2) rot=(0,-1,0;1.5708rad)
